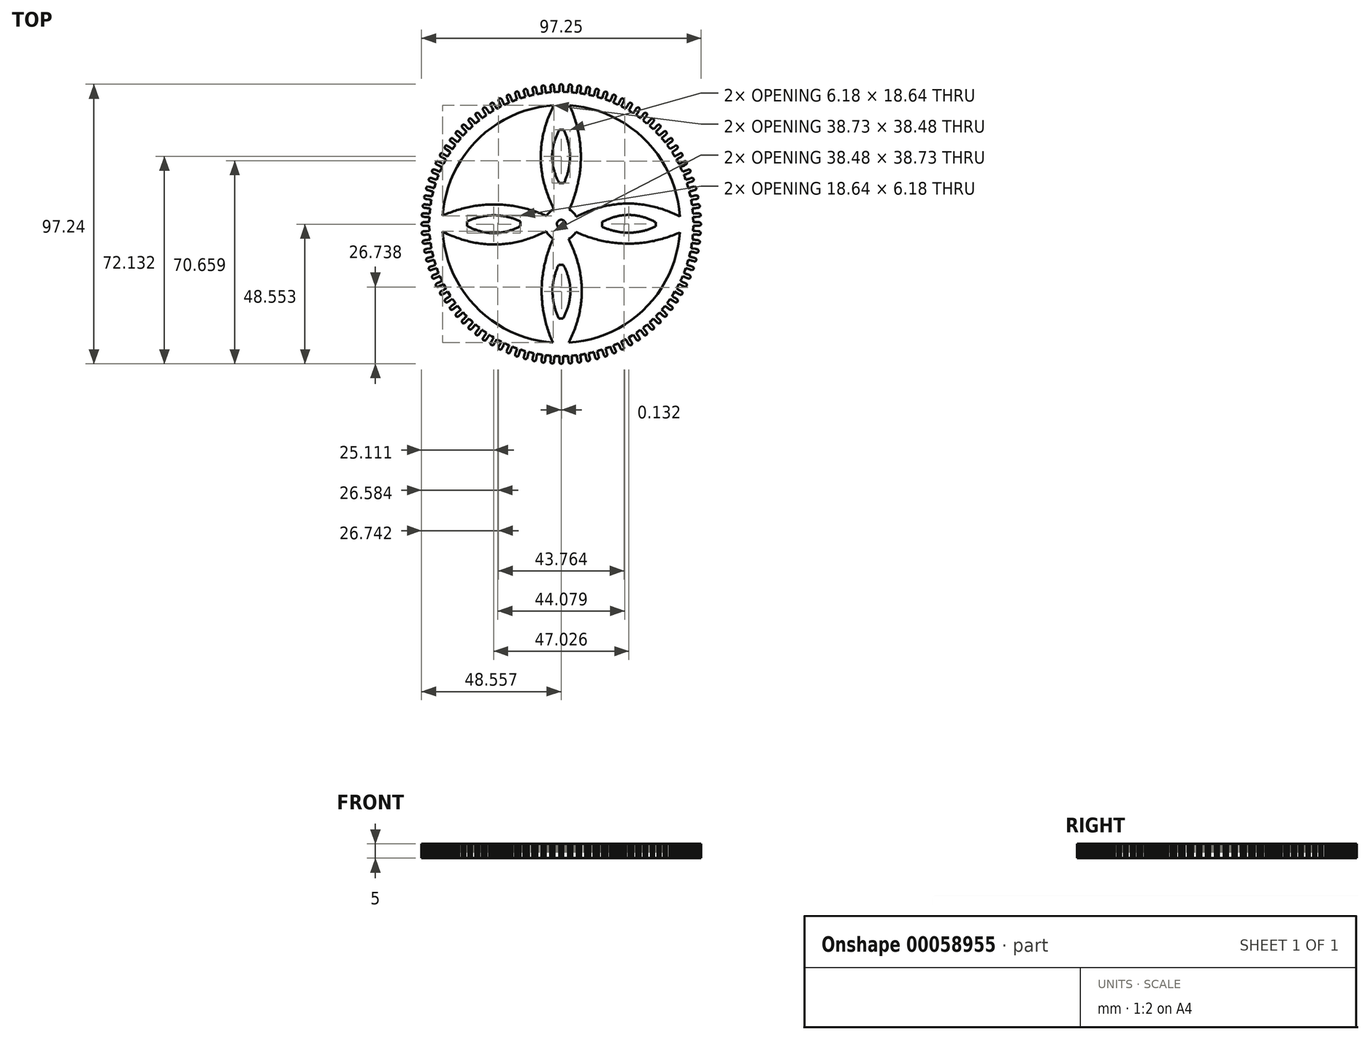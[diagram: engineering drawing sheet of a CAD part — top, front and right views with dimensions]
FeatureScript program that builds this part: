
annotation { "Feature Type Name" : "Feature", "Feature Type Description" : "" }
export const myFeature = defineFeature(function(context is Context, id is Id, definition is map)
    precondition{}
    {
        {
            var Q0;
            Q0=qCreatedBy(makeId("Top.planeOp"),FACE);
            var sketch = newSketch(context, id + "F0", { "sketchPlane" : qUnion([Q0])});
            skLineSegment(sketch, "E0", {"start": v(45.2, -0.6) * mm, "end": v(45.35, -0.6) * mm});
            skLineSegment(sketch, "E1", {"start": v(45.35, -0.6) * mm, "end": v(45.5, -0.6) * mm});
            skLineSegment(sketch, "E2", {"start": v(45.5, -0.6) * mm, "end": v(45.66, -0.6) * mm});
            skLineSegment(sketch, "E3", {"start": v(45.66, -0.6) * mm, "end": v(45.82, -0.6) * mm});
            skLineSegment(sketch, "E4", {"start": v(45.82, -0.6) * mm, "end": v(45.98, -0.6) * mm});
            skLineSegment(sketch, "E5", {"start": v(45.98, -0.6) * mm, "end": v(46.14, -0.61) * mm});
            skLineSegment(sketch, "E6", {"start": v(46.14, -0.61) * mm, "end": v(46.3, -0.61) * mm});
            skLineSegment(sketch, "E7", {"start": v(46.3, -0.61) * mm, "end": v(46.45, -0.62) * mm});
            skLineSegment(sketch, "E8", {"start": v(46.45, -0.62) * mm, "end": v(46.61, -0.62) * mm});
            skLineSegment(sketch, "E9", {"start": v(46.61, -0.62) * mm, "end": v(46.77, -0.62) * mm});
            skLineSegment(sketch, "E10", {"start": v(46.77, -0.62) * mm, "end": v(46.93, -0.62) * mm});
            skLineSegment(sketch, "E11", {"start": v(46.93, -0.62) * mm, "end": v(47.09, -0.62) * mm});
            skLineSegment(sketch, "E12", {"start": v(47.09, -0.62) * mm, "end": v(47.25, -0.63) * mm});
            skLineSegment(sketch, "E13", {"start": v(47.25, -0.63) * mm, "end": v(47.41, -0.6) * mm});
            skLineSegment(sketch, "E14", {"start": v(47.41, -0.6) * mm, "end": v(47.56, -0.54) * mm});
            skLineSegment(sketch, "E15", {"start": v(47.56, -0.54) * mm, "end": v(47.7, -0.44) * mm});
            skLineSegment(sketch, "E16", {"start": v(47.7, -0.44) * mm, "end": v(47.8, -0.31) * mm});
            skLineSegment(sketch, "E17", {"start": v(47.8, -0.31) * mm, "end": v(47.86, -0.16) * mm});
            skLineSegment(sketch, "E18", {"start": v(47.86, -0.16) * mm, "end": v(47.88, 0) * mm});
            skLineSegment(sketch, "E19", {"start": v(47.88, 0) * mm, "end": v(47.86, 0.16) * mm});
            skLineSegment(sketch, "E20", {"start": v(47.86, 0.16) * mm, "end": v(47.8, 0.31) * mm});
            skLineSegment(sketch, "E21", {"start": v(47.8, 0.31) * mm, "end": v(47.7, 0.44) * mm});
            skLineSegment(sketch, "E22", {"start": v(47.7, 0.44) * mm, "end": v(47.56, 0.54) * mm});
            skLineSegment(sketch, "E23", {"start": v(47.56, 0.54) * mm, "end": v(47.41, 0.6) * mm});
            skLineSegment(sketch, "E24", {"start": v(47.41, 0.6) * mm, "end": v(47.25, 0.62) * mm});
            skLineSegment(sketch, "E25", {"start": v(47.25, 0.62) * mm, "end": v(47.1, 0.62) * mm});
            skLineSegment(sketch, "E26", {"start": v(47.1, 0.62) * mm, "end": v(46.94, 0.62) * mm});
            skLineSegment(sketch, "E27", {"start": v(46.94, 0.62) * mm, "end": v(46.77, 0.62) * mm});
            skLineSegment(sketch, "E28", {"start": v(46.77, 0.62) * mm, "end": v(46.62, 0.62) * mm});
            skLineSegment(sketch, "E29", {"start": v(46.62, 0.62) * mm, "end": v(46.46, 0.61) * mm});
            skLineSegment(sketch, "E30", {"start": v(46.46, 0.61) * mm, "end": v(46.3, 0.61) * mm});
            skLineSegment(sketch, "E31", {"start": v(46.3, 0.61) * mm, "end": v(46.14, 0.61) * mm});
            skLineSegment(sketch, "E32", {"start": v(46.14, 0.61) * mm, "end": v(45.98, 0.6) * mm});
            skLineSegment(sketch, "E33", {"start": v(45.98, 0.6) * mm, "end": v(45.82, 0.6) * mm});
            skLineSegment(sketch, "E34", {"start": v(45.82, 0.6) * mm, "end": v(45.66, 0.6) * mm});
            skLineSegment(sketch, "E35", {"start": v(45.66, 0.6) * mm, "end": v(45.5, 0.6) * mm});
            skLineSegment(sketch, "E36", {"start": v(45.5, 0.6) * mm, "end": v(45.35, 0.6) * mm});
            skLineSegment(sketch, "E37", {"start": v(45.35, 0.6) * mm, "end": v(45.2, 0.6) * mm});
            skLineSegment(sketch, "E38", {"start": v(45.2, 0.6) * mm, "end": v(45.2, 0.76) * mm});
            skLineSegment(sketch, "E39", {"start": v(45.2, 0.76) * mm, "end": v(45.2, 0.91) * mm});
            skLineSegment(sketch, "E40", {"start": v(45.2, 0.91) * mm, "end": v(45.2, 1.07) * mm});
            skLineSegment(sketch, "E41", {"start": v(45.2, 1.07) * mm, "end": v(45.19, 1.23) * mm});
            skLineSegment(sketch, "E42", {"start": v(45.19, 1.23) * mm, "end": v(45.18, 1.38) * mm});
            skLineSegment(sketch, "E43", {"start": v(45.18, 1.38) * mm, "end": v(45.18, 1.54) * mm});
            skLineSegment(sketch, "E44", {"start": v(45.18, 1.54) * mm, "end": v(45.17, 1.7) * mm});
            skLineSegment(sketch, "E45", {"start": v(45.17, 1.7) * mm, "end": v(45.17, 1.86) * mm});
            skLineSegment(sketch, "E46", {"start": v(45.17, 1.86) * mm, "end": v(45.16, 2.01) * mm});
            skLineSegment(sketch, "E47", {"start": v(45.16, 2.01) * mm, "end": v(45.16, 2.17) * mm});
            skLineSegment(sketch, "E48", {"start": v(45.16, 2.17) * mm, "end": v(45.15, 2.33) * mm});
            skLineSegment(sketch, "E49", {"start": v(45.15, 2.33) * mm, "end": v(45.15, 2.4) * mm});
            skLineSegment(sketch, "E50", {"start": v(45.15, 2.4) * mm, "end": v(45.3, 2.42) * mm});
            skLineSegment(sketch, "E51", {"start": v(45.3, 2.42) * mm, "end": v(45.46, 2.42) * mm});
            skLineSegment(sketch, "E52", {"start": v(45.46, 2.42) * mm, "end": v(45.63, 2.43) * mm});
            skLineSegment(sketch, "E53", {"start": v(45.63, 2.43) * mm, "end": v(45.78, 2.44) * mm});
            skLineSegment(sketch, "E54", {"start": v(45.78, 2.44) * mm, "end": v(45.94, 2.45) * mm});
            skLineSegment(sketch, "E55", {"start": v(45.94, 2.45) * mm, "end": v(46.1, 2.46) * mm});
            skLineSegment(sketch, "E56", {"start": v(46.1, 2.46) * mm, "end": v(46.26, 2.47) * mm});
            skLineSegment(sketch, "E57", {"start": v(46.26, 2.47) * mm, "end": v(46.42, 2.47) * mm});
            skLineSegment(sketch, "E58", {"start": v(46.42, 2.47) * mm, "end": v(46.58, 2.48) * mm});
            skLineSegment(sketch, "E59", {"start": v(46.58, 2.48) * mm, "end": v(46.73, 2.5) * mm});
            skLineSegment(sketch, "E60", {"start": v(46.73, 2.5) * mm, "end": v(46.9, 2.5) * mm});
            skLineSegment(sketch, "E61", {"start": v(46.9, 2.5) * mm, "end": v(47.05, 2.5) * mm});
            skLineSegment(sketch, "E62", {"start": v(47.05, 2.5) * mm, "end": v(47.22, 2.52) * mm});
            skLineSegment(sketch, "E63", {"start": v(47.22, 2.52) * mm, "end": v(47.38, 2.56) * mm});
            skLineSegment(sketch, "E64", {"start": v(47.38, 2.56) * mm, "end": v(47.52, 2.64) * mm});
            skLineSegment(sketch, "E65", {"start": v(47.52, 2.64) * mm, "end": v(47.64, 2.75) * mm});
            skLineSegment(sketch, "E66", {"start": v(47.64, 2.75) * mm, "end": v(47.72, 2.9) * mm});
            skLineSegment(sketch, "E67", {"start": v(47.72, 2.9) * mm, "end": v(47.77, 3.05) * mm});
            skLineSegment(sketch, "E68", {"start": v(47.77, 3.05) * mm, "end": v(47.77, 3.21) * mm});
            skLineSegment(sketch, "E69", {"start": v(47.77, 3.21) * mm, "end": v(47.73, 3.37) * mm});
            skLineSegment(sketch, "E70", {"start": v(47.73, 3.37) * mm, "end": v(47.65, 3.51) * mm});
            skLineSegment(sketch, "E71", {"start": v(47.65, 3.51) * mm, "end": v(47.54, 3.63) * mm});
            skLineSegment(sketch, "E72", {"start": v(47.54, 3.63) * mm, "end": v(47.4, 3.71) * mm});
            skLineSegment(sketch, "E73", {"start": v(47.4, 3.71) * mm, "end": v(47.24, 3.76) * mm});
            skLineSegment(sketch, "E74", {"start": v(47.24, 3.76) * mm, "end": v(47.14, 3.76) * mm});
            skLineSegment(sketch, "E75", {"start": v(47.14, 3.76) * mm, "end": v(46.97, 3.75) * mm});
            skLineSegment(sketch, "E76", {"start": v(46.97, 3.75) * mm, "end": v(46.81, 3.74) * mm});
            skLineSegment(sketch, "E77", {"start": v(46.81, 3.74) * mm, "end": v(46.66, 3.73) * mm});
            skLineSegment(sketch, "E78", {"start": v(46.66, 3.73) * mm, "end": v(46.5, 3.71) * mm});
            skLineSegment(sketch, "E79", {"start": v(46.5, 3.71) * mm, "end": v(46.34, 3.7) * mm});
            skLineSegment(sketch, "E80", {"start": v(46.34, 3.7) * mm, "end": v(46.18, 3.69) * mm});
            skLineSegment(sketch, "E81", {"start": v(46.18, 3.69) * mm, "end": v(46.02, 3.68) * mm});
            skLineSegment(sketch, "E82", {"start": v(46.02, 3.68) * mm, "end": v(45.86, 3.66) * mm});
            skLineSegment(sketch, "E83", {"start": v(45.86, 3.66) * mm, "end": v(45.7, 3.65) * mm});
            skLineSegment(sketch, "E84", {"start": v(45.7, 3.65) * mm, "end": v(45.55, 3.64) * mm});
            skLineSegment(sketch, "E85", {"start": v(45.55, 3.64) * mm, "end": v(45.39, 3.63) * mm});
            skLineSegment(sketch, "E86", {"start": v(45.39, 3.63) * mm, "end": v(45.23, 3.62) * mm});
            skLineSegment(sketch, "E87", {"start": v(45.23, 3.62) * mm, "end": v(45.07, 3.6) * mm});
            skLineSegment(sketch, "E88", {"start": v(45.07, 3.6) * mm, "end": v(45.06, 3.76) * mm});
            skLineSegment(sketch, "E89", {"start": v(45.06, 3.76) * mm, "end": v(45.04, 3.92) * mm});
            skLineSegment(sketch, "E90", {"start": v(45.04, 3.92) * mm, "end": v(45.03, 4.07) * mm});
            skLineSegment(sketch, "E91", {"start": v(45.03, 4.07) * mm, "end": v(45, 4.23) * mm});
            skLineSegment(sketch, "E92", {"start": v(45, 4.23) * mm, "end": v(45, 4.39) * mm});
            skLineSegment(sketch, "E93", {"start": v(45, 4.39) * mm, "end": v(44.98, 4.54) * mm});
            skLineSegment(sketch, "E94", {"start": v(44.98, 4.54) * mm, "end": v(44.96, 4.7) * mm});
            skLineSegment(sketch, "E95", {"start": v(44.96, 4.7) * mm, "end": v(44.95, 4.85) * mm});
            skLineSegment(sketch, "E96", {"start": v(44.95, 4.85) * mm, "end": v(44.93, 5.01) * mm});
            skLineSegment(sketch, "E97", {"start": v(44.93, 5.01) * mm, "end": v(44.92, 5.17) * mm});
            skLineSegment(sketch, "E98", {"start": v(44.92, 5.17) * mm, "end": v(44.9, 5.32) * mm});
            skLineSegment(sketch, "E99", {"start": v(44.9, 5.32) * mm, "end": v(44.9, 5.4) * mm});
            skLineSegment(sketch, "E100", {"start": v(44.9, 5.4) * mm, "end": v(45.05, 5.42) * mm});
            skLineSegment(sketch, "E101", {"start": v(45.05, 5.42) * mm, "end": v(45.2, 5.44) * mm});
            skLineSegment(sketch, "E102", {"start": v(45.2, 5.44) * mm, "end": v(45.37, 5.46) * mm});
            skLineSegment(sketch, "E103", {"start": v(45.37, 5.46) * mm, "end": v(45.52, 5.48) * mm});
            skLineSegment(sketch, "E104", {"start": v(45.52, 5.48) * mm, "end": v(45.68, 5.5) * mm});
            skLineSegment(sketch, "E105", {"start": v(45.68, 5.5) * mm, "end": v(45.84, 5.52) * mm});
            skLineSegment(sketch, "E106", {"start": v(45.84, 5.52) * mm, "end": v(46, 5.53) * mm});
            skLineSegment(sketch, "E107", {"start": v(46, 5.53) * mm, "end": v(46.15, 5.55) * mm});
            skLineSegment(sketch, "E108", {"start": v(46.15, 5.55) * mm, "end": v(46.31, 5.57) * mm});
            skLineSegment(sketch, "E109", {"start": v(46.31, 5.57) * mm, "end": v(46.47, 5.6) * mm});
            skLineSegment(sketch, "E110", {"start": v(46.47, 5.6) * mm, "end": v(46.63, 5.6) * mm});
            skLineSegment(sketch, "E111", {"start": v(46.63, 5.6) * mm, "end": v(46.79, 5.63) * mm});
            skLineSegment(sketch, "E112", {"start": v(46.79, 5.63) * mm, "end": v(46.95, 5.65) * mm});
            skLineSegment(sketch, "E113", {"start": v(46.95, 5.65) * mm, "end": v(47.1, 5.7) * mm});
            skLineSegment(sketch, "E114", {"start": v(47.1, 5.7) * mm, "end": v(47.25, 5.79) * mm});
            skLineSegment(sketch, "E115", {"start": v(47.25, 5.79) * mm, "end": v(47.36, 5.9) * mm});
            skLineSegment(sketch, "E116", {"start": v(47.36, 5.9) * mm, "end": v(47.43, 6.05) * mm});
            skLineSegment(sketch, "E117", {"start": v(47.43, 6.05) * mm, "end": v(47.47, 6.22) * mm});
            skLineSegment(sketch, "E118", {"start": v(47.47, 6.22) * mm, "end": v(47.46, 6.38) * mm});
            skLineSegment(sketch, "E119", {"start": v(47.46, 6.38) * mm, "end": v(47.4, 6.53) * mm});
            skLineSegment(sketch, "E120", {"start": v(47.4, 6.53) * mm, "end": v(47.32, 6.67) * mm});
            skLineSegment(sketch, "E121", {"start": v(47.32, 6.67) * mm, "end": v(47.2, 6.78) * mm});
            skLineSegment(sketch, "E122", {"start": v(47.2, 6.78) * mm, "end": v(47.05, 6.86) * mm});
            skLineSegment(sketch, "E123", {"start": v(47.05, 6.86) * mm, "end": v(46.89, 6.89) * mm});
            skLineSegment(sketch, "E124", {"start": v(46.89, 6.89) * mm, "end": v(46.86, 6.9) * mm});
            skLineSegment(sketch, "E125", {"start": v(46.86, 6.9) * mm, "end": v(46.7, 6.87) * mm});
            skLineSegment(sketch, "E126", {"start": v(46.7, 6.87) * mm, "end": v(46.53, 6.85) * mm});
            skLineSegment(sketch, "E127", {"start": v(46.53, 6.85) * mm, "end": v(46.38, 6.83) * mm});
            skLineSegment(sketch, "E128", {"start": v(46.38, 6.83) * mm, "end": v(46.22, 6.8) * mm});
            skLineSegment(sketch, "E129", {"start": v(46.22, 6.8) * mm, "end": v(46.06, 6.78) * mm});
            skLineSegment(sketch, "E130", {"start": v(46.06, 6.78) * mm, "end": v(45.9, 6.76) * mm});
            skLineSegment(sketch, "E131", {"start": v(45.9, 6.76) * mm, "end": v(45.75, 6.74) * mm});
            skLineSegment(sketch, "E132", {"start": v(45.75, 6.74) * mm, "end": v(45.6, 6.72) * mm});
            skLineSegment(sketch, "E133", {"start": v(45.6, 6.72) * mm, "end": v(45.44, 6.7) * mm});
            skLineSegment(sketch, "E134", {"start": v(45.44, 6.7) * mm, "end": v(45.28, 6.67) * mm});
            skLineSegment(sketch, "E135", {"start": v(45.28, 6.67) * mm, "end": v(45.12, 6.65) * mm});
            skLineSegment(sketch, "E136", {"start": v(45.12, 6.65) * mm, "end": v(44.97, 6.62) * mm});
            skLineSegment(sketch, "E137", {"start": v(44.97, 6.62) * mm, "end": v(44.8, 6.6) * mm});
            skLineSegment(sketch, "E138", {"start": v(44.8, 6.6) * mm, "end": v(44.74, 6.6) * mm});
            skLineSegment(sketch, "E139", {"start": v(44.74, 6.6) * mm, "end": v(44.71, 6.75) * mm});
            skLineSegment(sketch, "E140", {"start": v(44.71, 6.75) * mm, "end": v(44.69, 6.9) * mm});
            skLineSegment(sketch, "E141", {"start": v(44.69, 6.9) * mm, "end": v(44.66, 7.06) * mm});
            skLineSegment(sketch, "E142", {"start": v(44.66, 7.06) * mm, "end": v(44.64, 7.21) * mm});
            skLineSegment(sketch, "E143", {"start": v(44.64, 7.21) * mm, "end": v(44.6, 7.37) * mm});
            skLineSegment(sketch, "E144", {"start": v(44.6, 7.37) * mm, "end": v(44.58, 7.52) * mm});
            skLineSegment(sketch, "E145", {"start": v(44.58, 7.52) * mm, "end": v(44.56, 7.68) * mm});
            skLineSegment(sketch, "E146", {"start": v(44.56, 7.68) * mm, "end": v(44.53, 7.83) * mm});
            skLineSegment(sketch, "E147", {"start": v(44.53, 7.83) * mm, "end": v(44.5, 7.99) * mm});
            skLineSegment(sketch, "E148", {"start": v(44.5, 7.99) * mm, "end": v(44.48, 8.14) * mm});
            skLineSegment(sketch, "E149", {"start": v(44.48, 8.14) * mm, "end": v(44.46, 8.3) * mm});
            skLineSegment(sketch, "E150", {"start": v(44.46, 8.3) * mm, "end": v(44.44, 8.38) * mm});
            skLineSegment(sketch, "E151", {"start": v(44.44, 8.38) * mm, "end": v(44.6, 8.4) * mm});
            skLineSegment(sketch, "E152", {"start": v(44.6, 8.4) * mm, "end": v(44.75, 8.44) * mm});
            skLineSegment(sketch, "E153", {"start": v(44.75, 8.44) * mm, "end": v(44.91, 8.46) * mm});
            skLineSegment(sketch, "E154", {"start": v(44.91, 8.46) * mm, "end": v(45.07, 8.5) * mm});
            skLineSegment(sketch, "E155", {"start": v(45.07, 8.5) * mm, "end": v(45.22, 8.52) * mm});
            skLineSegment(sketch, "E156", {"start": v(45.22, 8.52) * mm, "end": v(45.38, 8.55) * mm});
            skLineSegment(sketch, "E157", {"start": v(45.38, 8.55) * mm, "end": v(45.53, 8.58) * mm});
            skLineSegment(sketch, "E158", {"start": v(45.53, 8.58) * mm, "end": v(45.69, 8.6) * mm});
            skLineSegment(sketch, "E159", {"start": v(45.69, 8.6) * mm, "end": v(45.85, 8.64) * mm});
            skLineSegment(sketch, "E160", {"start": v(45.85, 8.64) * mm, "end": v(46, 8.67) * mm});
            skLineSegment(sketch, "E161", {"start": v(46, 8.67) * mm, "end": v(46.16, 8.7) * mm});
            skLineSegment(sketch, "E162", {"start": v(46.16, 8.7) * mm, "end": v(46.32, 8.73) * mm});
            skLineSegment(sketch, "E163", {"start": v(46.32, 8.73) * mm, "end": v(46.48, 8.76) * mm});
            skLineSegment(sketch, "E164", {"start": v(46.48, 8.76) * mm, "end": v(46.63, 8.82) * mm});
            skLineSegment(sketch, "E165", {"start": v(46.63, 8.82) * mm, "end": v(46.77, 8.91) * mm});
            skLineSegment(sketch, "E166", {"start": v(46.77, 8.91) * mm, "end": v(46.87, 9.04) * mm});
            skLineSegment(sketch, "E167", {"start": v(46.87, 9.04) * mm, "end": v(46.93, 9.2) * mm});
            skLineSegment(sketch, "E168", {"start": v(46.93, 9.2) * mm, "end": v(46.96, 9.36) * mm});
            skLineSegment(sketch, "E169", {"start": v(46.96, 9.36) * mm, "end": v(46.94, 9.52) * mm});
            skLineSegment(sketch, "E170", {"start": v(46.94, 9.52) * mm, "end": v(46.88, 9.67) * mm});
            skLineSegment(sketch, "E171", {"start": v(46.88, 9.67) * mm, "end": v(46.78, 9.8) * mm});
            skLineSegment(sketch, "E172", {"start": v(46.78, 9.8) * mm, "end": v(46.65, 9.9) * mm});
            skLineSegment(sketch, "E173", {"start": v(46.65, 9.9) * mm, "end": v(46.5, 9.97) * mm});
            skLineSegment(sketch, "E174", {"start": v(46.5, 9.97) * mm, "end": v(46.34, 9.99) * mm});
            skLineSegment(sketch, "E175", {"start": v(46.34, 9.99) * mm, "end": v(46.18, 9.97) * mm});
            skLineSegment(sketch, "E176", {"start": v(46.18, 9.97) * mm, "end": v(46.03, 9.94) * mm});
            skLineSegment(sketch, "E177", {"start": v(46.03, 9.94) * mm, "end": v(45.87, 9.9) * mm});
            skLineSegment(sketch, "E178", {"start": v(45.87, 9.9) * mm, "end": v(45.72, 9.87) * mm});
            skLineSegment(sketch, "E179", {"start": v(45.72, 9.87) * mm, "end": v(45.57, 9.84) * mm});
            skLineSegment(sketch, "E180", {"start": v(45.57, 9.84) * mm, "end": v(45.4, 9.8) * mm});
            skLineSegment(sketch, "E181", {"start": v(45.4, 9.8) * mm, "end": v(45.25, 9.77) * mm});
            skLineSegment(sketch, "E182", {"start": v(45.25, 9.77) * mm, "end": v(45.1, 9.74) * mm});
            skLineSegment(sketch, "E183", {"start": v(45.1, 9.74) * mm, "end": v(44.94, 9.7) * mm});
            skLineSegment(sketch, "E184", {"start": v(44.94, 9.7) * mm, "end": v(44.79, 9.68) * mm});
            skLineSegment(sketch, "E185", {"start": v(44.79, 9.68) * mm, "end": v(44.63, 9.64) * mm});
            skLineSegment(sketch, "E186", {"start": v(44.63, 9.64) * mm, "end": v(44.48, 9.6) * mm});
            skLineSegment(sketch, "E187", {"start": v(44.48, 9.6) * mm, "end": v(44.32, 9.58) * mm});
            skLineSegment(sketch, "E188", {"start": v(44.32, 9.58) * mm, "end": v(44.2, 9.55) * mm});
            skLineSegment(sketch, "E189", {"start": v(44.2, 9.55) * mm, "end": v(44.17, 9.7) * mm});
            skLineSegment(sketch, "E190", {"start": v(44.17, 9.7) * mm, "end": v(44.14, 9.86) * mm});
            skLineSegment(sketch, "E191", {"start": v(44.14, 9.86) * mm, "end": v(44.1, 10.01) * mm});
            skLineSegment(sketch, "E192", {"start": v(44.1, 10.01) * mm, "end": v(44.07, 10.16) * mm});
            skLineSegment(sketch, "E193", {"start": v(44.07, 10.16) * mm, "end": v(44.03, 10.32) * mm});
            skLineSegment(sketch, "E194", {"start": v(44.03, 10.32) * mm, "end": v(44, 10.47) * mm});
            skLineSegment(sketch, "E195", {"start": v(44, 10.47) * mm, "end": v(43.96, 10.62) * mm});
            skLineSegment(sketch, "E196", {"start": v(43.96, 10.62) * mm, "end": v(43.92, 10.78) * mm});
            skLineSegment(sketch, "E197", {"start": v(43.92, 10.78) * mm, "end": v(43.89, 10.93) * mm});
            skLineSegment(sketch, "E198", {"start": v(43.89, 10.93) * mm, "end": v(43.85, 11.08) * mm});
            skLineSegment(sketch, "E199", {"start": v(43.85, 11.08) * mm, "end": v(43.82, 11.24) * mm});
            skLineSegment(sketch, "E200", {"start": v(43.82, 11.24) * mm, "end": v(43.8, 11.32) * mm});
            skLineSegment(sketch, "E201", {"start": v(43.8, 11.32) * mm, "end": v(43.95, 11.35) * mm});
            skLineSegment(sketch, "E202", {"start": v(43.95, 11.35) * mm, "end": v(44.1, 11.4) * mm});
            skLineSegment(sketch, "E203", {"start": v(44.1, 11.4) * mm, "end": v(44.26, 11.43) * mm});
            skLineSegment(sketch, "E204", {"start": v(44.26, 11.43) * mm, "end": v(44.41, 11.47) * mm});
            skLineSegment(sketch, "E205", {"start": v(44.41, 11.47) * mm, "end": v(44.56, 11.51) * mm});
            skLineSegment(sketch, "E206", {"start": v(44.56, 11.51) * mm, "end": v(44.72, 11.55) * mm});
            skLineSegment(sketch, "E207", {"start": v(44.72, 11.55) * mm, "end": v(44.87, 11.59) * mm});
            skLineSegment(sketch, "E208", {"start": v(44.87, 11.59) * mm, "end": v(45.03, 11.63) * mm});
            skLineSegment(sketch, "E209", {"start": v(45.03, 11.63) * mm, "end": v(45.18, 11.67) * mm});
            skLineSegment(sketch, "E210", {"start": v(45.18, 11.67) * mm, "end": v(45.34, 11.7) * mm});
            skLineSegment(sketch, "E211", {"start": v(45.34, 11.7) * mm, "end": v(45.49, 11.74) * mm});
            skLineSegment(sketch, "E212", {"start": v(45.49, 11.74) * mm, "end": v(45.64, 11.78) * mm});
            skLineSegment(sketch, "E213", {"start": v(45.64, 11.78) * mm, "end": v(45.8, 11.83) * mm});
            skLineSegment(sketch, "E214", {"start": v(45.8, 11.83) * mm, "end": v(45.96, 11.9) * mm});
            skLineSegment(sketch, "E215", {"start": v(45.96, 11.9) * mm, "end": v(46.08, 12) * mm});
            skLineSegment(sketch, "E216", {"start": v(46.08, 12) * mm, "end": v(46.17, 12.14) * mm});
            skLineSegment(sketch, "E217", {"start": v(46.17, 12.14) * mm, "end": v(46.23, 12.3) * mm});
            skLineSegment(sketch, "E218", {"start": v(46.23, 12.3) * mm, "end": v(46.24, 12.46) * mm});
            skLineSegment(sketch, "E219", {"start": v(46.24, 12.46) * mm, "end": v(46.21, 12.62) * mm});
            skLineSegment(sketch, "E220", {"start": v(46.21, 12.62) * mm, "end": v(46.14, 12.76) * mm});
            skLineSegment(sketch, "E221", {"start": v(46.14, 12.76) * mm, "end": v(46.04, 12.89) * mm});
            skLineSegment(sketch, "E222", {"start": v(46.04, 12.89) * mm, "end": v(45.9, 12.98) * mm});
            skLineSegment(sketch, "E223", {"start": v(45.9, 12.98) * mm, "end": v(45.75, 13.04) * mm});
            skLineSegment(sketch, "E224", {"start": v(45.75, 13.04) * mm, "end": v(45.61, 13.05) * mm});
            skLineSegment(sketch, "E225", {"start": v(45.61, 13.05) * mm, "end": v(45.45, 13.03) * mm});
            skLineSegment(sketch, "E226", {"start": v(45.45, 13.03) * mm, "end": v(45.3, 12.98) * mm});
            skLineSegment(sketch, "E227", {"start": v(45.3, 12.98) * mm, "end": v(45.15, 12.94) * mm});
            skLineSegment(sketch, "E228", {"start": v(45.15, 12.94) * mm, "end": v(45, 12.9) * mm});
            skLineSegment(sketch, "E229", {"start": v(45, 12.9) * mm, "end": v(44.84, 12.85) * mm});
            skLineSegment(sketch, "E230", {"start": v(44.84, 12.85) * mm, "end": v(44.7, 12.81) * mm});
            skLineSegment(sketch, "E231", {"start": v(44.7, 12.81) * mm, "end": v(44.54, 12.77) * mm});
            skLineSegment(sketch, "E232", {"start": v(44.54, 12.77) * mm, "end": v(44.38, 12.72) * mm});
            skLineSegment(sketch, "E233", {"start": v(44.38, 12.72) * mm, "end": v(44.23, 12.68) * mm});
            skLineSegment(sketch, "E234", {"start": v(44.23, 12.68) * mm, "end": v(44.08, 12.64) * mm});
            skLineSegment(sketch, "E235", {"start": v(44.08, 12.64) * mm, "end": v(43.93, 12.6) * mm});
            skLineSegment(sketch, "E236", {"start": v(43.93, 12.6) * mm, "end": v(43.77, 12.55) * mm});
            skLineSegment(sketch, "E237", {"start": v(43.77, 12.55) * mm, "end": v(43.62, 12.5) * mm});
            skLineSegment(sketch, "E238", {"start": v(43.62, 12.5) * mm, "end": v(43.49, 12.47) * mm});
            skLineSegment(sketch, "E239", {"start": v(43.49, 12.47) * mm, "end": v(43.44, 12.62) * mm});
            skLineSegment(sketch, "E240", {"start": v(43.44, 12.62) * mm, "end": v(43.4, 12.77) * mm});
            skLineSegment(sketch, "E241", {"start": v(43.4, 12.77) * mm, "end": v(43.35, 12.92) * mm});
            skLineSegment(sketch, "E242", {"start": v(43.35, 12.92) * mm, "end": v(43.3, 13.07) * mm});
            skLineSegment(sketch, "E243", {"start": v(43.3, 13.07) * mm, "end": v(43.26, 13.22) * mm});
            skLineSegment(sketch, "E244", {"start": v(43.26, 13.22) * mm, "end": v(43.21, 13.38) * mm});
            skLineSegment(sketch, "E245", {"start": v(43.21, 13.38) * mm, "end": v(43.17, 13.53) * mm});
            skLineSegment(sketch, "E246", {"start": v(43.17, 13.53) * mm, "end": v(43.12, 13.68) * mm});
            skLineSegment(sketch, "E247", {"start": v(43.12, 13.68) * mm, "end": v(43.08, 13.83) * mm});
            skLineSegment(sketch, "E248", {"start": v(43.08, 13.83) * mm, "end": v(43.03, 13.98) * mm});
            skLineSegment(sketch, "E249", {"start": v(43.03, 13.98) * mm, "end": v(42.99, 14.13) * mm});
            skLineSegment(sketch, "E250", {"start": v(42.99, 14.13) * mm, "end": v(42.96, 14.2) * mm});
            skLineSegment(sketch, "E251", {"start": v(42.96, 14.2) * mm, "end": v(43.11, 14.25) * mm});
            skLineSegment(sketch, "E252", {"start": v(43.11, 14.25) * mm, "end": v(43.26, 14.3) * mm});
            skLineSegment(sketch, "E253", {"start": v(43.26, 14.3) * mm, "end": v(43.42, 14.35) * mm});
            skLineSegment(sketch, "E254", {"start": v(43.42, 14.35) * mm, "end": v(43.57, 14.4) * mm});
            skLineSegment(sketch, "E255", {"start": v(43.57, 14.4) * mm, "end": v(43.71, 14.45) * mm});
            skLineSegment(sketch, "E256", {"start": v(43.71, 14.45) * mm, "end": v(43.87, 14.5) * mm});
            skLineSegment(sketch, "E257", {"start": v(43.87, 14.5) * mm, "end": v(44.02, 14.55) * mm});
            skLineSegment(sketch, "E258", {"start": v(44.02, 14.55) * mm, "end": v(44.17, 14.6) * mm});
            skLineSegment(sketch, "E259", {"start": v(44.17, 14.6) * mm, "end": v(44.32, 14.65) * mm});
            skLineSegment(sketch, "E260", {"start": v(44.32, 14.65) * mm, "end": v(44.47, 14.7) * mm});
            skLineSegment(sketch, "E261", {"start": v(44.47, 14.7) * mm, "end": v(44.62, 14.74) * mm});
            skLineSegment(sketch, "E262", {"start": v(44.62, 14.74) * mm, "end": v(44.77, 14.8) * mm});
            skLineSegment(sketch, "E263", {"start": v(44.77, 14.8) * mm, "end": v(44.93, 14.85) * mm});
            skLineSegment(sketch, "E264", {"start": v(44.93, 14.85) * mm, "end": v(45.08, 14.93) * mm});
            skLineSegment(sketch, "E265", {"start": v(45.08, 14.93) * mm, "end": v(45.2, 15.04) * mm});
            skLineSegment(sketch, "E266", {"start": v(45.2, 15.04) * mm, "end": v(45.28, 15.18) * mm});
            skLineSegment(sketch, "E267", {"start": v(45.28, 15.18) * mm, "end": v(45.32, 15.34) * mm});
            skLineSegment(sketch, "E268", {"start": v(45.32, 15.34) * mm, "end": v(45.33, 15.5) * mm});
            skLineSegment(sketch, "E269", {"start": v(45.33, 15.5) * mm, "end": v(45.29, 15.66) * mm});
            skLineSegment(sketch, "E270", {"start": v(45.29, 15.66) * mm, "end": v(45.2, 15.8) * mm});
            skLineSegment(sketch, "E271", {"start": v(45.2, 15.8) * mm, "end": v(45.1, 15.92) * mm});
            skLineSegment(sketch, "E272", {"start": v(45.1, 15.92) * mm, "end": v(44.95, 16) * mm});
            skLineSegment(sketch, "E273", {"start": v(44.95, 16) * mm, "end": v(44.8, 16.05) * mm});
            skLineSegment(sketch, "E274", {"start": v(44.8, 16.05) * mm, "end": v(44.7, 16.05) * mm});
            skLineSegment(sketch, "E275", {"start": v(44.7, 16.05) * mm, "end": v(44.53, 16.03) * mm});
            skLineSegment(sketch, "E276", {"start": v(44.53, 16.03) * mm, "end": v(44.37, 15.97) * mm});
            skLineSegment(sketch, "E277", {"start": v(44.37, 15.97) * mm, "end": v(44.23, 15.92) * mm});
            skLineSegment(sketch, "E278", {"start": v(44.23, 15.92) * mm, "end": v(44.08, 15.87) * mm});
            skLineSegment(sketch, "E279", {"start": v(44.08, 15.87) * mm, "end": v(43.92, 15.82) * mm});
            skLineSegment(sketch, "E280", {"start": v(43.92, 15.82) * mm, "end": v(43.78, 15.76) * mm});
            skLineSegment(sketch, "E281", {"start": v(43.78, 15.76) * mm, "end": v(43.63, 15.71) * mm});
            skLineSegment(sketch, "E282", {"start": v(43.63, 15.71) * mm, "end": v(43.48, 15.66) * mm});
            skLineSegment(sketch, "E283", {"start": v(43.48, 15.66) * mm, "end": v(43.33, 15.6) * mm});
            skLineSegment(sketch, "E284", {"start": v(43.33, 15.6) * mm, "end": v(43.18, 15.55) * mm});
            skLineSegment(sketch, "E285", {"start": v(43.18, 15.55) * mm, "end": v(43.03, 15.5) * mm});
            skLineSegment(sketch, "E286", {"start": v(43.03, 15.5) * mm, "end": v(42.88, 15.44) * mm});
            skLineSegment(sketch, "E287", {"start": v(42.88, 15.44) * mm, "end": v(42.73, 15.4) * mm});
            skLineSegment(sketch, "E288", {"start": v(42.73, 15.4) * mm, "end": v(42.58, 15.34) * mm});
            skLineSegment(sketch, "E289", {"start": v(42.58, 15.34) * mm, "end": v(42.52, 15.49) * mm});
            skLineSegment(sketch, "E290", {"start": v(42.52, 15.49) * mm, "end": v(42.47, 15.63) * mm});
            skLineSegment(sketch, "E291", {"start": v(42.47, 15.63) * mm, "end": v(42.41, 15.78) * mm});
            skLineSegment(sketch, "E292", {"start": v(42.41, 15.78) * mm, "end": v(42.36, 15.93) * mm});
            skLineSegment(sketch, "E293", {"start": v(42.36, 15.93) * mm, "end": v(42.3, 16.07) * mm});
            skLineSegment(sketch, "E294", {"start": v(42.3, 16.07) * mm, "end": v(42.25, 16.22) * mm});
            skLineSegment(sketch, "E295", {"start": v(42.25, 16.22) * mm, "end": v(42.2, 16.37) * mm});
            skLineSegment(sketch, "E296", {"start": v(42.2, 16.37) * mm, "end": v(42.13, 16.52) * mm});
            skLineSegment(sketch, "E297", {"start": v(42.13, 16.52) * mm, "end": v(42.08, 16.66) * mm});
            skLineSegment(sketch, "E298", {"start": v(42.08, 16.66) * mm, "end": v(42.02, 16.81) * mm});
            skLineSegment(sketch, "E299", {"start": v(42.02, 16.81) * mm, "end": v(41.97, 16.96) * mm});
            skLineSegment(sketch, "E300", {"start": v(41.97, 16.96) * mm, "end": v(41.94, 17.03) * mm});
            skLineSegment(sketch, "E301", {"start": v(41.94, 17.03) * mm, "end": v(42.09, 17.1) * mm});
            skLineSegment(sketch, "E302", {"start": v(42.09, 17.1) * mm, "end": v(42.23, 17.15) * mm});
            skLineSegment(sketch, "E303", {"start": v(42.23, 17.15) * mm, "end": v(42.38, 17.2) * mm});
            skLineSegment(sketch, "E304", {"start": v(42.38, 17.2) * mm, "end": v(42.53, 17.27) * mm});
            skLineSegment(sketch, "E305", {"start": v(42.53, 17.27) * mm, "end": v(42.67, 17.33) * mm});
            skLineSegment(sketch, "E306", {"start": v(42.67, 17.33) * mm, "end": v(42.82, 17.39) * mm});
            skLineSegment(sketch, "E307", {"start": v(42.82, 17.39) * mm, "end": v(42.97, 17.44) * mm});
            skLineSegment(sketch, "E308", {"start": v(42.97, 17.44) * mm, "end": v(43.12, 17.5) * mm});
            skLineSegment(sketch, "E309", {"start": v(43.12, 17.5) * mm, "end": v(43.27, 17.56) * mm});
            skLineSegment(sketch, "E310", {"start": v(43.27, 17.56) * mm, "end": v(43.41, 17.62) * mm});
            skLineSegment(sketch, "E311", {"start": v(43.41, 17.62) * mm, "end": v(43.56, 17.68) * mm});
            skLineSegment(sketch, "E312", {"start": v(43.56, 17.68) * mm, "end": v(43.7, 17.74) * mm});
            skLineSegment(sketch, "E313", {"start": v(43.7, 17.74) * mm, "end": v(43.87, 17.8) * mm});
            skLineSegment(sketch, "E314", {"start": v(43.87, 17.8) * mm, "end": v(44, 17.9) * mm});
            skLineSegment(sketch, "E315", {"start": v(44, 17.9) * mm, "end": v(44.11, 18.01) * mm});
            skLineSegment(sketch, "E316", {"start": v(44.11, 18.01) * mm, "end": v(44.19, 18.16) * mm});
            skLineSegment(sketch, "E317", {"start": v(44.19, 18.16) * mm, "end": v(44.22, 18.32) * mm});
            skLineSegment(sketch, "E318", {"start": v(44.22, 18.32) * mm, "end": v(44.21, 18.48) * mm});
            skLineSegment(sketch, "E319", {"start": v(44.21, 18.48) * mm, "end": v(44.16, 18.64) * mm});
            skLineSegment(sketch, "E320", {"start": v(44.16, 18.64) * mm, "end": v(44.07, 18.78) * mm});
            skLineSegment(sketch, "E321", {"start": v(44.07, 18.78) * mm, "end": v(43.95, 18.88) * mm});
            skLineSegment(sketch, "E322", {"start": v(43.95, 18.88) * mm, "end": v(43.8, 18.96) * mm});
            skLineSegment(sketch, "E323", {"start": v(43.8, 18.96) * mm, "end": v(43.65, 19) * mm});
            skLineSegment(sketch, "E324", {"start": v(43.65, 19) * mm, "end": v(43.61, 19) * mm});
            skLineSegment(sketch, "E325", {"start": v(43.61, 19) * mm, "end": v(43.45, 18.98) * mm});
            skLineSegment(sketch, "E326", {"start": v(43.45, 18.98) * mm, "end": v(43.3, 18.92) * mm});
            skLineSegment(sketch, "E327", {"start": v(43.3, 18.92) * mm, "end": v(43.15, 18.86) * mm});
            skLineSegment(sketch, "E328", {"start": v(43.15, 18.86) * mm, "end": v(43, 18.8) * mm});
            skLineSegment(sketch, "E329", {"start": v(43, 18.8) * mm, "end": v(42.86, 18.73) * mm});
            skLineSegment(sketch, "E330", {"start": v(42.86, 18.73) * mm, "end": v(42.71, 18.67) * mm});
            skLineSegment(sketch, "E331", {"start": v(42.71, 18.67) * mm, "end": v(42.57, 18.6) * mm});
            skLineSegment(sketch, "E332", {"start": v(42.57, 18.6) * mm, "end": v(42.42, 18.54) * mm});
            skLineSegment(sketch, "E333", {"start": v(42.42, 18.54) * mm, "end": v(42.27, 18.48) * mm});
            skLineSegment(sketch, "E334", {"start": v(42.27, 18.48) * mm, "end": v(42.13, 18.42) * mm});
            skLineSegment(sketch, "E335", {"start": v(42.13, 18.42) * mm, "end": v(41.98, 18.35) * mm});
            skLineSegment(sketch, "E336", {"start": v(41.98, 18.35) * mm, "end": v(41.84, 18.3) * mm});
            skLineSegment(sketch, "E337", {"start": v(41.84, 18.3) * mm, "end": v(41.7, 18.23) * mm});
            skLineSegment(sketch, "E338", {"start": v(41.7, 18.23) * mm, "end": v(41.54, 18.17) * mm});
            skLineSegment(sketch, "E339", {"start": v(41.54, 18.17) * mm, "end": v(41.48, 18.14) * mm});
            skLineSegment(sketch, "E340", {"start": v(41.48, 18.14) * mm, "end": v(41.42, 18.28) * mm});
            skLineSegment(sketch, "E341", {"start": v(41.42, 18.28) * mm, "end": v(41.35, 18.43) * mm});
            skLineSegment(sketch, "E342", {"start": v(41.35, 18.43) * mm, "end": v(41.29, 18.57) * mm});
            skLineSegment(sketch, "E343", {"start": v(41.29, 18.57) * mm, "end": v(41.22, 18.71) * mm});
            skLineSegment(sketch, "E344", {"start": v(41.22, 18.71) * mm, "end": v(41.16, 18.86) * mm});
            skLineSegment(sketch, "E345", {"start": v(41.16, 18.86) * mm, "end": v(41.1, 19) * mm});
            skLineSegment(sketch, "E346", {"start": v(41.1, 19) * mm, "end": v(41.03, 19.14) * mm});
            skLineSegment(sketch, "E347", {"start": v(41.03, 19.14) * mm, "end": v(40.96, 19.29) * mm});
            skLineSegment(sketch, "E348", {"start": v(40.96, 19.29) * mm, "end": v(40.9, 19.43) * mm});
            skLineSegment(sketch, "E349", {"start": v(40.9, 19.43) * mm, "end": v(40.83, 19.57) * mm});
            skLineSegment(sketch, "E350", {"start": v(40.83, 19.57) * mm, "end": v(40.77, 19.71) * mm});
            skLineSegment(sketch, "E351", {"start": v(40.77, 19.71) * mm, "end": v(40.73, 19.79) * mm});
            skLineSegment(sketch, "E352", {"start": v(40.73, 19.79) * mm, "end": v(40.88, 19.86) * mm});
            skLineSegment(sketch, "E353", {"start": v(40.88, 19.86) * mm, "end": v(41.02, 19.92) * mm});
            skLineSegment(sketch, "E354", {"start": v(41.02, 19.92) * mm, "end": v(41.16, 20) * mm});
            skLineSegment(sketch, "E355", {"start": v(41.16, 20) * mm, "end": v(41.3, 20.06) * mm});
            skLineSegment(sketch, "E356", {"start": v(41.3, 20.06) * mm, "end": v(41.45, 20.13) * mm});
            skLineSegment(sketch, "E357", {"start": v(41.45, 20.13) * mm, "end": v(41.6, 20.2) * mm});
            skLineSegment(sketch, "E358", {"start": v(41.6, 20.2) * mm, "end": v(41.74, 20.27) * mm});
            skLineSegment(sketch, "E359", {"start": v(41.74, 20.27) * mm, "end": v(41.88, 20.33) * mm});
            skLineSegment(sketch, "E360", {"start": v(41.88, 20.33) * mm, "end": v(42.02, 20.4) * mm});
            skLineSegment(sketch, "E361", {"start": v(42.02, 20.4) * mm, "end": v(42.17, 20.47) * mm});
            skLineSegment(sketch, "E362", {"start": v(42.17, 20.47) * mm, "end": v(42.3, 20.54) * mm});
            skLineSegment(sketch, "E363", {"start": v(42.3, 20.54) * mm, "end": v(42.45, 20.6) * mm});
            skLineSegment(sketch, "E364", {"start": v(42.45, 20.6) * mm, "end": v(42.6, 20.68) * mm});
            skLineSegment(sketch, "E365", {"start": v(42.6, 20.68) * mm, "end": v(42.74, 20.78) * mm});
            skLineSegment(sketch, "E366", {"start": v(42.74, 20.78) * mm, "end": v(42.84, 20.9) * mm});
            skLineSegment(sketch, "E367", {"start": v(42.84, 20.9) * mm, "end": v(42.9, 21.06) * mm});
            skLineSegment(sketch, "E368", {"start": v(42.9, 21.06) * mm, "end": v(42.93, 21.22) * mm});
            skLineSegment(sketch, "E369", {"start": v(42.93, 21.22) * mm, "end": v(42.9, 21.38) * mm});
            skLineSegment(sketch, "E370", {"start": v(42.9, 21.38) * mm, "end": v(42.85, 21.53) * mm});
            skLineSegment(sketch, "E371", {"start": v(42.85, 21.53) * mm, "end": v(42.75, 21.67) * mm});
            skLineSegment(sketch, "E372", {"start": v(42.75, 21.67) * mm, "end": v(42.62, 21.77) * mm});
            skLineSegment(sketch, "E373", {"start": v(42.62, 21.77) * mm, "end": v(42.47, 21.83) * mm});
            skLineSegment(sketch, "E374", {"start": v(42.47, 21.83) * mm, "end": v(42.3, 21.85) * mm});
            skLineSegment(sketch, "E375", {"start": v(42.3, 21.85) * mm, "end": v(42.15, 21.83) * mm});
            skLineSegment(sketch, "E376", {"start": v(42.15, 21.83) * mm, "end": v(42, 21.77) * mm});
            skLineSegment(sketch, "E377", {"start": v(42, 21.77) * mm, "end": v(41.86, 21.7) * mm});
            skLineSegment(sketch, "E378", {"start": v(41.86, 21.7) * mm, "end": v(41.72, 21.63) * mm});
            skLineSegment(sketch, "E379", {"start": v(41.72, 21.63) * mm, "end": v(41.58, 21.56) * mm});
            skLineSegment(sketch, "E380", {"start": v(41.58, 21.56) * mm, "end": v(41.44, 21.5) * mm});
            skLineSegment(sketch, "E381", {"start": v(41.44, 21.5) * mm, "end": v(41.3, 21.42) * mm});
            skLineSegment(sketch, "E382", {"start": v(41.3, 21.42) * mm, "end": v(41.16, 21.35) * mm});
            skLineSegment(sketch, "E383", {"start": v(41.16, 21.35) * mm, "end": v(41.02, 21.28) * mm});
            skLineSegment(sketch, "E384", {"start": v(41.02, 21.28) * mm, "end": v(40.87, 21.2) * mm});
            skLineSegment(sketch, "E385", {"start": v(40.87, 21.2) * mm, "end": v(40.73, 21.13) * mm});
            skLineSegment(sketch, "E386", {"start": v(40.73, 21.13) * mm, "end": v(40.6, 21.06) * mm});
            skLineSegment(sketch, "E387", {"start": v(40.6, 21.06) * mm, "end": v(40.45, 20.99) * mm});
            skLineSegment(sketch, "E388", {"start": v(40.45, 20.99) * mm, "end": v(40.3, 20.91) * mm});
            skLineSegment(sketch, "E389", {"start": v(40.3, 20.91) * mm, "end": v(40.2, 20.86) * mm});
            skLineSegment(sketch, "E390", {"start": v(40.2, 20.86) * mm, "end": v(40.13, 21) * mm});
            skLineSegment(sketch, "E391", {"start": v(40.13, 21) * mm, "end": v(40.06, 21.14) * mm});
            skLineSegment(sketch, "E392", {"start": v(40.06, 21.14) * mm, "end": v(39.98, 21.28) * mm});
            skLineSegment(sketch, "E393", {"start": v(39.98, 21.28) * mm, "end": v(39.9, 21.42) * mm});
            skLineSegment(sketch, "E394", {"start": v(39.9, 21.42) * mm, "end": v(39.83, 21.56) * mm});
            skLineSegment(sketch, "E395", {"start": v(39.83, 21.56) * mm, "end": v(39.76, 21.7) * mm});
            skLineSegment(sketch, "E396", {"start": v(39.76, 21.7) * mm, "end": v(39.69, 21.83) * mm});
            skLineSegment(sketch, "E397", {"start": v(39.69, 21.83) * mm, "end": v(39.61, 21.97) * mm});
            skLineSegment(sketch, "E398", {"start": v(39.61, 21.97) * mm, "end": v(39.54, 22.11) * mm});
            skLineSegment(sketch, "E399", {"start": v(39.54, 22.11) * mm, "end": v(39.46, 22.25) * mm});
            skLineSegment(sketch, "E400", {"start": v(39.46, 22.25) * mm, "end": v(39.39, 22.39) * mm});
            skLineSegment(sketch, "E401", {"start": v(39.39, 22.39) * mm, "end": v(39.35, 22.46) * mm});
            skLineSegment(sketch, "E402", {"start": v(39.35, 22.46) * mm, "end": v(39.49, 22.54) * mm});
            skLineSegment(sketch, "E403", {"start": v(39.49, 22.54) * mm, "end": v(39.63, 22.61) * mm});
            skLineSegment(sketch, "E404", {"start": v(39.63, 22.61) * mm, "end": v(39.77, 22.7) * mm});
            skLineSegment(sketch, "E405", {"start": v(39.77, 22.7) * mm, "end": v(39.9, 22.77) * mm});
            skLineSegment(sketch, "E406", {"start": v(39.9, 22.77) * mm, "end": v(40.04, 22.85) * mm});
            skLineSegment(sketch, "E407", {"start": v(40.04, 22.85) * mm, "end": v(40.18, 22.92) * mm});
            skLineSegment(sketch, "E408", {"start": v(40.18, 22.92) * mm, "end": v(40.32, 23) * mm});
            skLineSegment(sketch, "E409", {"start": v(40.32, 23) * mm, "end": v(40.46, 23.08) * mm});
            skLineSegment(sketch, "E410", {"start": v(40.46, 23.08) * mm, "end": v(40.6, 23.16) * mm});
            skLineSegment(sketch, "E411", {"start": v(40.6, 23.16) * mm, "end": v(40.74, 23.23) * mm});
            skLineSegment(sketch, "E412", {"start": v(40.74, 23.23) * mm, "end": v(40.87, 23.31) * mm});
            skLineSegment(sketch, "E413", {"start": v(40.87, 23.31) * mm, "end": v(41.01, 23.39) * mm});
            skLineSegment(sketch, "E414", {"start": v(41.01, 23.39) * mm, "end": v(41.16, 23.47) * mm});
            skLineSegment(sketch, "E415", {"start": v(41.16, 23.47) * mm, "end": v(41.29, 23.58) * mm});
            skLineSegment(sketch, "E416", {"start": v(41.29, 23.58) * mm, "end": v(41.38, 23.71) * mm});
            skLineSegment(sketch, "E417", {"start": v(41.38, 23.71) * mm, "end": v(41.43, 23.87) * mm});
            skLineSegment(sketch, "E418", {"start": v(41.43, 23.87) * mm, "end": v(41.45, 24.03) * mm});
            skLineSegment(sketch, "E419", {"start": v(41.45, 24.03) * mm, "end": v(41.42, 24.2) * mm});
            skLineSegment(sketch, "E420", {"start": v(41.42, 24.2) * mm, "end": v(41.35, 24.34) * mm});
            skLineSegment(sketch, "E421", {"start": v(41.35, 24.34) * mm, "end": v(41.24, 24.46) * mm});
            skLineSegment(sketch, "E422", {"start": v(41.24, 24.46) * mm, "end": v(41.1, 24.56) * mm});
            skLineSegment(sketch, "E423", {"start": v(41.1, 24.56) * mm, "end": v(40.95, 24.61) * mm});
            skLineSegment(sketch, "E424", {"start": v(40.95, 24.61) * mm, "end": v(40.82, 24.62) * mm});
            skLineSegment(sketch, "E425", {"start": v(40.82, 24.62) * mm, "end": v(40.66, 24.6) * mm});
            skLineSegment(sketch, "E426", {"start": v(40.66, 24.6) * mm, "end": v(40.5, 24.54) * mm});
            skLineSegment(sketch, "E427", {"start": v(40.5, 24.54) * mm, "end": v(40.37, 24.46) * mm});
            skLineSegment(sketch, "E428", {"start": v(40.37, 24.46) * mm, "end": v(40.24, 24.38) * mm});
            skLineSegment(sketch, "E429", {"start": v(40.24, 24.38) * mm, "end": v(40.1, 24.3) * mm});
            skLineSegment(sketch, "E430", {"start": v(40.1, 24.3) * mm, "end": v(39.96, 24.22) * mm});
            skLineSegment(sketch, "E431", {"start": v(39.96, 24.22) * mm, "end": v(39.83, 24.13) * mm});
            skLineSegment(sketch, "E432", {"start": v(39.83, 24.13) * mm, "end": v(39.69, 24.05) * mm});
            skLineSegment(sketch, "E433", {"start": v(39.69, 24.05) * mm, "end": v(39.55, 23.97) * mm});
            skLineSegment(sketch, "E434", {"start": v(39.55, 23.97) * mm, "end": v(39.42, 23.9) * mm});
            skLineSegment(sketch, "E435", {"start": v(39.42, 23.9) * mm, "end": v(39.28, 23.8) * mm});
            skLineSegment(sketch, "E436", {"start": v(39.28, 23.8) * mm, "end": v(39.14, 23.73) * mm});
            skLineSegment(sketch, "E437", {"start": v(39.14, 23.73) * mm, "end": v(39, 23.65) * mm});
            skLineSegment(sketch, "E438", {"start": v(39, 23.65) * mm, "end": v(38.87, 23.57) * mm});
            skLineSegment(sketch, "E439", {"start": v(38.87, 23.57) * mm, "end": v(38.75, 23.5) * mm});
            skLineSegment(sketch, "E440", {"start": v(38.75, 23.5) * mm, "end": v(38.67, 23.63) * mm});
            skLineSegment(sketch, "E441", {"start": v(38.67, 23.63) * mm, "end": v(38.59, 23.76) * mm});
            skLineSegment(sketch, "E442", {"start": v(38.59, 23.76) * mm, "end": v(38.5, 23.9) * mm});
            skLineSegment(sketch, "E443", {"start": v(38.5, 23.9) * mm, "end": v(38.42, 24.03) * mm});
            skLineSegment(sketch, "E444", {"start": v(38.42, 24.03) * mm, "end": v(38.34, 24.16) * mm});
            skLineSegment(sketch, "E445", {"start": v(38.34, 24.16) * mm, "end": v(38.25, 24.3) * mm});
            skLineSegment(sketch, "E446", {"start": v(38.25, 24.3) * mm, "end": v(38.17, 24.43) * mm});
            skLineSegment(sketch, "E447", {"start": v(38.17, 24.43) * mm, "end": v(38.09, 24.56) * mm});
            skLineSegment(sketch, "E448", {"start": v(38.09, 24.56) * mm, "end": v(38, 24.7) * mm});
            skLineSegment(sketch, "E449", {"start": v(38, 24.7) * mm, "end": v(37.92, 24.83) * mm});
            skLineSegment(sketch, "E450", {"start": v(37.92, 24.83) * mm, "end": v(37.84, 24.96) * mm});
            skLineSegment(sketch, "E451", {"start": v(37.84, 24.96) * mm, "end": v(37.8, 25.03) * mm});
            skLineSegment(sketch, "E452", {"start": v(37.8, 25.03) * mm, "end": v(37.93, 25.12) * mm});
            skLineSegment(sketch, "E453", {"start": v(37.93, 25.12) * mm, "end": v(38.06, 25.2) * mm});
            skLineSegment(sketch, "E454", {"start": v(38.06, 25.2) * mm, "end": v(38.2, 25.3) * mm});
            skLineSegment(sketch, "E455", {"start": v(38.2, 25.3) * mm, "end": v(38.33, 25.38) * mm});
            skLineSegment(sketch, "E456", {"start": v(38.33, 25.38) * mm, "end": v(38.46, 25.46) * mm});
            skLineSegment(sketch, "E457", {"start": v(38.46, 25.46) * mm, "end": v(38.6, 25.55) * mm});
            skLineSegment(sketch, "E458", {"start": v(38.6, 25.55) * mm, "end": v(38.73, 25.64) * mm});
            skLineSegment(sketch, "E459", {"start": v(38.73, 25.64) * mm, "end": v(38.86, 25.72) * mm});
            skLineSegment(sketch, "E460", {"start": v(38.86, 25.72) * mm, "end": v(39, 25.81) * mm});
            skLineSegment(sketch, "E461", {"start": v(39, 25.81) * mm, "end": v(39.13, 25.9) * mm});
            skLineSegment(sketch, "E462", {"start": v(39.13, 25.9) * mm, "end": v(39.26, 25.98) * mm});
            skLineSegment(sketch, "E463", {"start": v(39.26, 25.98) * mm, "end": v(39.4, 26.07) * mm});
            skLineSegment(sketch, "E464", {"start": v(39.4, 26.07) * mm, "end": v(39.54, 26.16) * mm});
            skLineSegment(sketch, "E465", {"start": v(39.54, 26.16) * mm, "end": v(39.65, 26.28) * mm});
            skLineSegment(sketch, "E466", {"start": v(39.65, 26.28) * mm, "end": v(39.74, 26.42) * mm});
            skLineSegment(sketch, "E467", {"start": v(39.74, 26.42) * mm, "end": v(39.78, 26.58) * mm});
            skLineSegment(sketch, "E468", {"start": v(39.78, 26.58) * mm, "end": v(39.79, 26.74) * mm});
            skLineSegment(sketch, "E469", {"start": v(39.79, 26.74) * mm, "end": v(39.75, 26.9) * mm});
            skLineSegment(sketch, "E470", {"start": v(39.75, 26.9) * mm, "end": v(39.66, 27.04) * mm});
            skLineSegment(sketch, "E471", {"start": v(39.66, 27.04) * mm, "end": v(39.55, 27.16) * mm});
            skLineSegment(sketch, "E472", {"start": v(39.55, 27.16) * mm, "end": v(39.4, 27.24) * mm});
            skLineSegment(sketch, "E473", {"start": v(39.4, 27.24) * mm, "end": v(39.25, 27.29) * mm});
            skLineSegment(sketch, "E474", {"start": v(39.25, 27.29) * mm, "end": v(39.15, 27.3) * mm});
            skLineSegment(sketch, "E475", {"start": v(39.15, 27.3) * mm, "end": v(39, 27.27) * mm});
            skLineSegment(sketch, "E476", {"start": v(39, 27.27) * mm, "end": v(38.84, 27.2) * mm});
            skLineSegment(sketch, "E477", {"start": v(38.84, 27.2) * mm, "end": v(38.7, 27.1) * mm});
            skLineSegment(sketch, "E478", {"start": v(38.7, 27.1) * mm, "end": v(38.57, 27.02) * mm});
            skLineSegment(sketch, "E479", {"start": v(38.57, 27.02) * mm, "end": v(38.44, 26.93) * mm});
            skLineSegment(sketch, "E480", {"start": v(38.44, 26.93) * mm, "end": v(38.3, 26.84) * mm});
            skLineSegment(sketch, "E481", {"start": v(38.3, 26.84) * mm, "end": v(38.18, 26.75) * mm});
            skLineSegment(sketch, "E482", {"start": v(38.18, 26.75) * mm, "end": v(38.05, 26.66) * mm});
            skLineSegment(sketch, "E483", {"start": v(38.05, 26.66) * mm, "end": v(37.92, 26.57) * mm});
            skLineSegment(sketch, "E484", {"start": v(37.92, 26.57) * mm, "end": v(37.79, 26.48) * mm});
            skLineSegment(sketch, "E485", {"start": v(37.79, 26.48) * mm, "end": v(37.66, 26.4) * mm});
            skLineSegment(sketch, "E486", {"start": v(37.66, 26.4) * mm, "end": v(37.52, 26.3) * mm});
            skLineSegment(sketch, "E487", {"start": v(37.52, 26.3) * mm, "end": v(37.4, 26.2) * mm});
            skLineSegment(sketch, "E488", {"start": v(37.4, 26.2) * mm, "end": v(37.26, 26.12) * mm});
            skLineSegment(sketch, "E489", {"start": v(37.26, 26.12) * mm, "end": v(37.13, 26.03) * mm});
            skLineSegment(sketch, "E490", {"start": v(37.13, 26.03) * mm, "end": v(37.04, 26.16) * mm});
            skLineSegment(sketch, "E491", {"start": v(37.04, 26.16) * mm, "end": v(36.95, 26.28) * mm});
            skLineSegment(sketch, "E492", {"start": v(36.95, 26.28) * mm, "end": v(36.86, 26.41) * mm});
            skLineSegment(sketch, "E493", {"start": v(36.86, 26.41) * mm, "end": v(36.77, 26.54) * mm});
            skLineSegment(sketch, "E494", {"start": v(36.77, 26.54) * mm, "end": v(36.67, 26.67) * mm});
            skLineSegment(sketch, "E495", {"start": v(36.67, 26.67) * mm, "end": v(36.58, 26.8) * mm});
            skLineSegment(sketch, "E496", {"start": v(36.58, 26.8) * mm, "end": v(36.5, 26.92) * mm});
            skLineSegment(sketch, "E497", {"start": v(36.5, 26.92) * mm, "end": v(36.4, 27.05) * mm});
            skLineSegment(sketch, "E498", {"start": v(36.4, 27.05) * mm, "end": v(36.3, 27.18) * mm});
            skLineSegment(sketch, "E499", {"start": v(36.3, 27.18) * mm, "end": v(36.22, 27.3) * mm});
            skLineSegment(sketch, "E500", {"start": v(36.22, 27.3) * mm, "end": v(36.12, 27.44) * mm});
            skLineSegment(sketch, "E501", {"start": v(36.12, 27.44) * mm, "end": v(36.08, 27.5) * mm});
            skLineSegment(sketch, "E502", {"start": v(36.08, 27.5) * mm, "end": v(36.2, 27.6) * mm});
            skLineSegment(sketch, "E503", {"start": v(36.2, 27.6) * mm, "end": v(36.33, 27.69) * mm});
            skLineSegment(sketch, "E504", {"start": v(36.33, 27.69) * mm, "end": v(36.46, 27.79) * mm});
            skLineSegment(sketch, "E505", {"start": v(36.46, 27.79) * mm, "end": v(36.58, 27.88) * mm});
            skLineSegment(sketch, "E506", {"start": v(36.58, 27.88) * mm, "end": v(36.71, 27.97) * mm});
            skLineSegment(sketch, "E507", {"start": v(36.71, 27.97) * mm, "end": v(36.84, 28.07) * mm});
            skLineSegment(sketch, "E508", {"start": v(36.84, 28.07) * mm, "end": v(36.97, 28.16) * mm});
            skLineSegment(sketch, "E509", {"start": v(36.97, 28.16) * mm, "end": v(37.1, 28.26) * mm});
            skLineSegment(sketch, "E510", {"start": v(37.1, 28.26) * mm, "end": v(37.22, 28.36) * mm});
            skLineSegment(sketch, "E511", {"start": v(37.22, 28.36) * mm, "end": v(37.35, 28.45) * mm});
            skLineSegment(sketch, "E512", {"start": v(37.35, 28.45) * mm, "end": v(37.47, 28.54) * mm});
            skLineSegment(sketch, "E513", {"start": v(37.47, 28.54) * mm, "end": v(37.6, 28.64) * mm});
            skLineSegment(sketch, "E514", {"start": v(37.6, 28.64) * mm, "end": v(37.74, 28.74) * mm});
            skLineSegment(sketch, "E515", {"start": v(37.74, 28.74) * mm, "end": v(37.85, 28.86) * mm});
            skLineSegment(sketch, "E516", {"start": v(37.85, 28.86) * mm, "end": v(37.92, 29) * mm});
            skLineSegment(sketch, "E517", {"start": v(37.92, 29) * mm, "end": v(37.96, 29.17) * mm});
            skLineSegment(sketch, "E518", {"start": v(37.96, 29.17) * mm, "end": v(37.95, 29.33) * mm});
            skLineSegment(sketch, "E519", {"start": v(37.95, 29.33) * mm, "end": v(37.9, 29.49) * mm});
            skLineSegment(sketch, "E520", {"start": v(37.9, 29.49) * mm, "end": v(37.8, 29.63) * mm});
            skLineSegment(sketch, "E521", {"start": v(37.8, 29.63) * mm, "end": v(37.69, 29.74) * mm});
            skLineSegment(sketch, "E522", {"start": v(37.69, 29.74) * mm, "end": v(37.54, 29.8) * mm});
            skLineSegment(sketch, "E523", {"start": v(37.54, 29.8) * mm, "end": v(37.38, 29.84) * mm});
            skLineSegment(sketch, "E524", {"start": v(37.38, 29.84) * mm, "end": v(37.35, 29.85) * mm});
            skLineSegment(sketch, "E525", {"start": v(37.35, 29.85) * mm, "end": v(37.19, 29.83) * mm});
            skLineSegment(sketch, "E526", {"start": v(37.19, 29.83) * mm, "end": v(37.03, 29.77) * mm});
            skLineSegment(sketch, "E527", {"start": v(37.03, 29.77) * mm, "end": v(36.9, 29.67) * mm});
            skLineSegment(sketch, "E528", {"start": v(36.9, 29.67) * mm, "end": v(36.77, 29.57) * mm});
            skLineSegment(sketch, "E529", {"start": v(36.77, 29.57) * mm, "end": v(36.65, 29.48) * mm});
            skLineSegment(sketch, "E530", {"start": v(36.65, 29.48) * mm, "end": v(36.52, 29.38) * mm});
            skLineSegment(sketch, "E531", {"start": v(36.52, 29.38) * mm, "end": v(36.4, 29.28) * mm});
            skLineSegment(sketch, "E532", {"start": v(36.4, 29.28) * mm, "end": v(36.28, 29.18) * mm});
            skLineSegment(sketch, "E533", {"start": v(36.28, 29.18) * mm, "end": v(36.15, 29.08) * mm});
            skLineSegment(sketch, "E534", {"start": v(36.15, 29.08) * mm, "end": v(36.03, 28.98) * mm});
            skLineSegment(sketch, "E535", {"start": v(36.03, 28.98) * mm, "end": v(35.9, 28.89) * mm});
            skLineSegment(sketch, "E536", {"start": v(35.9, 28.89) * mm, "end": v(35.78, 28.79) * mm});
            skLineSegment(sketch, "E537", {"start": v(35.78, 28.79) * mm, "end": v(35.65, 28.69) * mm});
            skLineSegment(sketch, "E538", {"start": v(35.65, 28.69) * mm, "end": v(35.53, 28.6) * mm});
            skLineSegment(sketch, "E539", {"start": v(35.53, 28.6) * mm, "end": v(35.4, 28.5) * mm});
            skLineSegment(sketch, "E540", {"start": v(35.4, 28.5) * mm, "end": v(35.35, 28.45) * mm});
            skLineSegment(sketch, "E541", {"start": v(35.35, 28.45) * mm, "end": v(35.25, 28.57) * mm});
            skLineSegment(sketch, "E542", {"start": v(35.25, 28.57) * mm, "end": v(35.15, 28.7) * mm});
            skLineSegment(sketch, "E543", {"start": v(35.15, 28.7) * mm, "end": v(35.05, 28.82) * mm});
            skLineSegment(sketch, "E544", {"start": v(35.05, 28.82) * mm, "end": v(34.95, 28.94) * mm});
            skLineSegment(sketch, "E545", {"start": v(34.95, 28.94) * mm, "end": v(34.85, 29.06) * mm});
            skLineSegment(sketch, "E546", {"start": v(34.85, 29.06) * mm, "end": v(34.75, 29.18) * mm});
            skLineSegment(sketch, "E547", {"start": v(34.75, 29.18) * mm, "end": v(34.65, 29.3) * mm});
            skLineSegment(sketch, "E548", {"start": v(34.65, 29.3) * mm, "end": v(34.55, 29.42) * mm});
            skLineSegment(sketch, "E549", {"start": v(34.55, 29.42) * mm, "end": v(34.45, 29.54) * mm});
            skLineSegment(sketch, "E550", {"start": v(34.45, 29.54) * mm, "end": v(34.35, 29.67) * mm});
            skLineSegment(sketch, "E551", {"start": v(34.35, 29.67) * mm, "end": v(34.25, 29.79) * mm});
            skLineSegment(sketch, "E552", {"start": v(34.25, 29.79) * mm, "end": v(34.2, 29.85) * mm});
            skLineSegment(sketch, "E553", {"start": v(34.2, 29.85) * mm, "end": v(34.32, 29.95) * mm});
            skLineSegment(sketch, "E554", {"start": v(34.32, 29.95) * mm, "end": v(34.44, 30.05) * mm});
            skLineSegment(sketch, "E555", {"start": v(34.44, 30.05) * mm, "end": v(34.56, 30.16) * mm});
            skLineSegment(sketch, "E556", {"start": v(34.56, 30.16) * mm, "end": v(34.68, 30.26) * mm});
            skLineSegment(sketch, "E557", {"start": v(34.68, 30.26) * mm, "end": v(34.8, 30.36) * mm});
            skLineSegment(sketch, "E558", {"start": v(34.8, 30.36) * mm, "end": v(34.92, 30.47) * mm});
            skLineSegment(sketch, "E559", {"start": v(34.92, 30.47) * mm, "end": v(35.04, 30.57) * mm});
            skLineSegment(sketch, "E560", {"start": v(35.04, 30.57) * mm, "end": v(35.16, 30.67) * mm});
            skLineSegment(sketch, "E561", {"start": v(35.16, 30.67) * mm, "end": v(35.29, 30.78) * mm});
            skLineSegment(sketch, "E562", {"start": v(35.29, 30.78) * mm, "end": v(35.4, 30.88) * mm});
            skLineSegment(sketch, "E563", {"start": v(35.4, 30.88) * mm, "end": v(35.52, 30.98) * mm});
            skLineSegment(sketch, "E564", {"start": v(35.52, 30.98) * mm, "end": v(35.65, 31.09) * mm});
            skLineSegment(sketch, "E565", {"start": v(35.65, 31.09) * mm, "end": v(35.78, 31.2) * mm});
            skLineSegment(sketch, "E566", {"start": v(35.78, 31.2) * mm, "end": v(35.88, 31.33) * mm});
            skLineSegment(sketch, "E567", {"start": v(35.88, 31.33) * mm, "end": v(35.94, 31.48) * mm});
            skLineSegment(sketch, "E568", {"start": v(35.94, 31.48) * mm, "end": v(35.97, 31.64) * mm});
            skLineSegment(sketch, "E569", {"start": v(35.97, 31.64) * mm, "end": v(35.95, 31.8) * mm});
            skLineSegment(sketch, "E570", {"start": v(35.95, 31.8) * mm, "end": v(35.89, 31.95) * mm});
            skLineSegment(sketch, "E571", {"start": v(35.89, 31.95) * mm, "end": v(35.79, 32.08) * mm});
            skLineSegment(sketch, "E572", {"start": v(35.79, 32.08) * mm, "end": v(35.66, 32.19) * mm});
            skLineSegment(sketch, "E573", {"start": v(35.66, 32.19) * mm, "end": v(35.51, 32.25) * mm});
            skLineSegment(sketch, "E574", {"start": v(35.51, 32.25) * mm, "end": v(35.35, 32.27) * mm});
            skLineSegment(sketch, "E575", {"start": v(35.35, 32.27) * mm, "end": v(35.19, 32.25) * mm});
            skLineSegment(sketch, "E576", {"start": v(35.19, 32.25) * mm, "end": v(35.03, 32.2) * mm});
            skLineSegment(sketch, "E577", {"start": v(35.03, 32.2) * mm, "end": v(34.9, 32.1) * mm});
            skLineSegment(sketch, "E578", {"start": v(34.9, 32.1) * mm, "end": v(34.8, 32) * mm});
            skLineSegment(sketch, "E579", {"start": v(34.8, 32) * mm, "end": v(34.67, 31.89) * mm});
            skLineSegment(sketch, "E580", {"start": v(34.67, 31.89) * mm, "end": v(34.56, 31.78) * mm});
            skLineSegment(sketch, "E581", {"start": v(34.56, 31.78) * mm, "end": v(34.44, 31.68) * mm});
            skLineSegment(sketch, "E582", {"start": v(34.44, 31.68) * mm, "end": v(34.32, 31.57) * mm});
            skLineSegment(sketch, "E583", {"start": v(34.32, 31.57) * mm, "end": v(34.2, 31.46) * mm});
            skLineSegment(sketch, "E584", {"start": v(34.2, 31.46) * mm, "end": v(34.09, 31.36) * mm});
            skLineSegment(sketch, "E585", {"start": v(34.09, 31.36) * mm, "end": v(33.97, 31.25) * mm});
            skLineSegment(sketch, "E586", {"start": v(33.97, 31.25) * mm, "end": v(33.85, 31.15) * mm});
            skLineSegment(sketch, "E587", {"start": v(33.85, 31.15) * mm, "end": v(33.73, 31.04) * mm});
            skLineSegment(sketch, "E588", {"start": v(33.73, 31.04) * mm, "end": v(33.61, 30.93) * mm});
            skLineSegment(sketch, "E589", {"start": v(33.61, 30.93) * mm, "end": v(33.5, 30.83) * mm});
            skLineSegment(sketch, "E590", {"start": v(33.5, 30.83) * mm, "end": v(33.41, 30.75) * mm});
            skLineSegment(sketch, "E591", {"start": v(33.41, 30.75) * mm, "end": v(33.3, 30.87) * mm});
            skLineSegment(sketch, "E592", {"start": v(33.3, 30.87) * mm, "end": v(33.2, 30.98) * mm});
            skLineSegment(sketch, "E593", {"start": v(33.2, 30.98) * mm, "end": v(33.09, 31.1) * mm});
            skLineSegment(sketch, "E594", {"start": v(33.09, 31.1) * mm, "end": v(32.98, 31.2) * mm});
            skLineSegment(sketch, "E595", {"start": v(32.98, 31.2) * mm, "end": v(32.87, 31.32) * mm});
            skLineSegment(sketch, "E596", {"start": v(32.87, 31.32) * mm, "end": v(32.76, 31.44) * mm});
            skLineSegment(sketch, "E597", {"start": v(32.76, 31.44) * mm, "end": v(32.66, 31.55) * mm});
            skLineSegment(sketch, "E598", {"start": v(32.66, 31.55) * mm, "end": v(32.55, 31.67) * mm});
            skLineSegment(sketch, "E599", {"start": v(32.55, 31.67) * mm, "end": v(32.44, 31.78) * mm});
            skLineSegment(sketch, "E600", {"start": v(32.44, 31.78) * mm, "end": v(32.33, 31.9) * mm});
            skLineSegment(sketch, "E601", {"start": v(32.33, 31.9) * mm, "end": v(32.23, 32.01) * mm});
            skLineSegment(sketch, "E602", {"start": v(32.23, 32.01) * mm, "end": v(32.17, 32.07) * mm});
            skLineSegment(sketch, "E603", {"start": v(32.17, 32.07) * mm, "end": v(32.29, 32.18) * mm});
            skLineSegment(sketch, "E604", {"start": v(32.29, 32.18) * mm, "end": v(32.4, 32.3) * mm});
            skLineSegment(sketch, "E605", {"start": v(32.4, 32.3) * mm, "end": v(32.51, 32.4) * mm});
            skLineSegment(sketch, "E606", {"start": v(32.51, 32.4) * mm, "end": v(32.63, 32.51) * mm});
            skLineSegment(sketch, "E607", {"start": v(32.63, 32.51) * mm, "end": v(32.74, 32.62) * mm});
            skLineSegment(sketch, "E608", {"start": v(32.74, 32.62) * mm, "end": v(32.85, 32.74) * mm});
            skLineSegment(sketch, "E609", {"start": v(32.85, 32.74) * mm, "end": v(32.97, 32.85) * mm});
            skLineSegment(sketch, "E610", {"start": v(32.97, 32.85) * mm, "end": v(33.08, 32.96) * mm});
            skLineSegment(sketch, "E611", {"start": v(33.08, 32.96) * mm, "end": v(33.2, 33.07) * mm});
            skLineSegment(sketch, "E612", {"start": v(33.2, 33.07) * mm, "end": v(33.3, 33.18) * mm});
            skLineSegment(sketch, "E613", {"start": v(33.3, 33.18) * mm, "end": v(33.42, 33.29) * mm});
            skLineSegment(sketch, "E614", {"start": v(33.42, 33.29) * mm, "end": v(33.54, 33.4) * mm});
            skLineSegment(sketch, "E615", {"start": v(33.54, 33.4) * mm, "end": v(33.66, 33.52) * mm});
            skLineSegment(sketch, "E616", {"start": v(33.66, 33.52) * mm, "end": v(33.75, 33.65) * mm});
            skLineSegment(sketch, "E617", {"start": v(33.75, 33.65) * mm, "end": v(33.8, 33.8) * mm});
            skLineSegment(sketch, "E618", {"start": v(33.8, 33.8) * mm, "end": v(33.82, 33.97) * mm});
            skLineSegment(sketch, "E619", {"start": v(33.82, 33.97) * mm, "end": v(33.79, 34.13) * mm});
            skLineSegment(sketch, "E620", {"start": v(33.79, 34.13) * mm, "end": v(33.72, 34.28) * mm});
            skLineSegment(sketch, "E621", {"start": v(33.72, 34.28) * mm, "end": v(33.61, 34.4) * mm});
            skLineSegment(sketch, "E622", {"start": v(33.61, 34.4) * mm, "end": v(33.48, 34.5) * mm});
            skLineSegment(sketch, "E623", {"start": v(33.48, 34.5) * mm, "end": v(33.32, 34.55) * mm});
            skLineSegment(sketch, "E624", {"start": v(33.32, 34.55) * mm, "end": v(33.2, 34.57) * mm});
            skLineSegment(sketch, "E625", {"start": v(33.2, 34.57) * mm, "end": v(33.03, 34.54) * mm});
            skLineSegment(sketch, "E626", {"start": v(33.03, 34.54) * mm, "end": v(32.88, 34.48) * mm});
            skLineSegment(sketch, "E627", {"start": v(32.88, 34.48) * mm, "end": v(32.75, 34.38) * mm});
            skLineSegment(sketch, "E628", {"start": v(32.75, 34.38) * mm, "end": v(32.64, 34.27) * mm});
            skLineSegment(sketch, "E629", {"start": v(32.64, 34.27) * mm, "end": v(32.53, 34.15) * mm});
            skLineSegment(sketch, "E630", {"start": v(32.53, 34.15) * mm, "end": v(32.42, 34.04) * mm});
            skLineSegment(sketch, "E631", {"start": v(32.42, 34.04) * mm, "end": v(32.3, 33.93) * mm});
            skLineSegment(sketch, "E632", {"start": v(32.3, 33.93) * mm, "end": v(32.2, 33.81) * mm});
            skLineSegment(sketch, "E633", {"start": v(32.2, 33.81) * mm, "end": v(32.09, 33.7) * mm});
            skLineSegment(sketch, "E634", {"start": v(32.09, 33.7) * mm, "end": v(31.98, 33.59) * mm});
            skLineSegment(sketch, "E635", {"start": v(31.98, 33.59) * mm, "end": v(31.87, 33.47) * mm});
            skLineSegment(sketch, "E636", {"start": v(31.87, 33.47) * mm, "end": v(31.75, 33.36) * mm});
            skLineSegment(sketch, "E637", {"start": v(31.75, 33.36) * mm, "end": v(31.64, 33.24) * mm});
            skLineSegment(sketch, "E638", {"start": v(31.64, 33.24) * mm, "end": v(31.53, 33.13) * mm});
            skLineSegment(sketch, "E639", {"start": v(31.53, 33.13) * mm, "end": v(31.42, 33.02) * mm});
            skLineSegment(sketch, "E640", {"start": v(31.42, 33.02) * mm, "end": v(31.33, 32.92) * mm});
            skLineSegment(sketch, "E641", {"start": v(31.33, 32.92) * mm, "end": v(31.21, 33.03) * mm});
            skLineSegment(sketch, "E642", {"start": v(31.21, 33.03) * mm, "end": v(31.1, 33.13) * mm});
            skLineSegment(sketch, "E643", {"start": v(31.1, 33.13) * mm, "end": v(30.98, 33.24) * mm});
            skLineSegment(sketch, "E644", {"start": v(30.98, 33.24) * mm, "end": v(30.87, 33.35) * mm});
            skLineSegment(sketch, "E645", {"start": v(30.87, 33.35) * mm, "end": v(30.75, 33.46) * mm});
            skLineSegment(sketch, "E646", {"start": v(30.75, 33.46) * mm, "end": v(30.64, 33.56) * mm});
            skLineSegment(sketch, "E647", {"start": v(30.64, 33.56) * mm, "end": v(30.52, 33.67) * mm});
            skLineSegment(sketch, "E648", {"start": v(30.52, 33.67) * mm, "end": v(30.4, 33.78) * mm});
            skLineSegment(sketch, "E649", {"start": v(30.4, 33.78) * mm, "end": v(30.3, 33.89) * mm});
            skLineSegment(sketch, "E650", {"start": v(30.3, 33.89) * mm, "end": v(30.18, 34) * mm});
            skLineSegment(sketch, "E651", {"start": v(30.18, 34) * mm, "end": v(30.06, 34.1) * mm});
            skLineSegment(sketch, "E652", {"start": v(30.06, 34.1) * mm, "end": v(30, 34.16) * mm});
            skLineSegment(sketch, "E653", {"start": v(30, 34.16) * mm, "end": v(30.1, 34.27) * mm});
            skLineSegment(sketch, "E654", {"start": v(30.1, 34.27) * mm, "end": v(30.21, 34.39) * mm});
            skLineSegment(sketch, "E655", {"start": v(30.21, 34.39) * mm, "end": v(30.32, 34.5) * mm});
            skLineSegment(sketch, "E656", {"start": v(30.32, 34.5) * mm, "end": v(30.43, 34.63) * mm});
            skLineSegment(sketch, "E657", {"start": v(30.43, 34.63) * mm, "end": v(30.53, 34.74) * mm});
            skLineSegment(sketch, "E658", {"start": v(30.53, 34.74) * mm, "end": v(30.64, 34.86) * mm});
            skLineSegment(sketch, "E659", {"start": v(30.64, 34.86) * mm, "end": v(30.75, 34.98) * mm});
            skLineSegment(sketch, "E660", {"start": v(30.75, 34.98) * mm, "end": v(30.85, 35.1) * mm});
            skLineSegment(sketch, "E661", {"start": v(30.85, 35.1) * mm, "end": v(30.96, 35.22) * mm});
            skLineSegment(sketch, "E662", {"start": v(30.96, 35.22) * mm, "end": v(31.07, 35.33) * mm});
            skLineSegment(sketch, "E663", {"start": v(31.07, 35.33) * mm, "end": v(31.17, 35.45) * mm});
            skLineSegment(sketch, "E664", {"start": v(31.17, 35.45) * mm, "end": v(31.28, 35.57) * mm});
            skLineSegment(sketch, "E665", {"start": v(31.28, 35.57) * mm, "end": v(31.4, 35.7) * mm});
            skLineSegment(sketch, "E666", {"start": v(31.4, 35.7) * mm, "end": v(31.48, 35.84) * mm});
            skLineSegment(sketch, "E667", {"start": v(31.48, 35.84) * mm, "end": v(31.52, 36) * mm});
            skLineSegment(sketch, "E668", {"start": v(31.52, 36) * mm, "end": v(31.52, 36.16) * mm});
            skLineSegment(sketch, "E669", {"start": v(31.52, 36.16) * mm, "end": v(31.48, 36.32) * mm});
            skLineSegment(sketch, "E670", {"start": v(31.48, 36.32) * mm, "end": v(31.4, 36.46) * mm});
            skLineSegment(sketch, "E671", {"start": v(31.4, 36.46) * mm, "end": v(31.29, 36.58) * mm});
            skLineSegment(sketch, "E672", {"start": v(31.29, 36.58) * mm, "end": v(31.15, 36.66) * mm});
            skLineSegment(sketch, "E673", {"start": v(31.15, 36.66) * mm, "end": v(31, 36.7) * mm});
            skLineSegment(sketch, "E674", {"start": v(31, 36.7) * mm, "end": v(30.9, 36.71) * mm});
            skLineSegment(sketch, "E675", {"start": v(30.9, 36.71) * mm, "end": v(30.73, 36.69) * mm});
            skLineSegment(sketch, "E676", {"start": v(30.73, 36.69) * mm, "end": v(30.58, 36.62) * mm});
            skLineSegment(sketch, "E677", {"start": v(30.58, 36.62) * mm, "end": v(30.45, 36.52) * mm});
            skLineSegment(sketch, "E678", {"start": v(30.45, 36.52) * mm, "end": v(30.34, 36.4) * mm});
            skLineSegment(sketch, "E679", {"start": v(30.34, 36.4) * mm, "end": v(30.24, 36.27) * mm});
            skLineSegment(sketch, "E680", {"start": v(30.24, 36.27) * mm, "end": v(30.14, 36.15) * mm});
            skLineSegment(sketch, "E681", {"start": v(30.14, 36.15) * mm, "end": v(30.03, 36.03) * mm});
            skLineSegment(sketch, "E682", {"start": v(30.03, 36.03) * mm, "end": v(29.93, 35.91) * mm});
            skLineSegment(sketch, "E683", {"start": v(29.93, 35.91) * mm, "end": v(29.83, 35.8) * mm});
            skLineSegment(sketch, "E684", {"start": v(29.83, 35.8) * mm, "end": v(29.72, 35.67) * mm});
            skLineSegment(sketch, "E685", {"start": v(29.72, 35.67) * mm, "end": v(29.62, 35.55) * mm});
            skLineSegment(sketch, "E686", {"start": v(29.62, 35.55) * mm, "end": v(29.52, 35.43) * mm});
            skLineSegment(sketch, "E687", {"start": v(29.52, 35.43) * mm, "end": v(29.41, 35.3) * mm});
            skLineSegment(sketch, "E688", {"start": v(29.41, 35.3) * mm, "end": v(29.31, 35.19) * mm});
            skLineSegment(sketch, "E689", {"start": v(29.31, 35.19) * mm, "end": v(29.2, 35.07) * mm});
            skLineSegment(sketch, "E690", {"start": v(29.2, 35.07) * mm, "end": v(29.1, 34.95) * mm});
            skLineSegment(sketch, "E691", {"start": v(29.1, 34.95) * mm, "end": v(28.98, 35.05) * mm});
            skLineSegment(sketch, "E692", {"start": v(28.98, 35.05) * mm, "end": v(28.86, 35.14) * mm});
            skLineSegment(sketch, "E693", {"start": v(28.86, 35.14) * mm, "end": v(28.74, 35.24) * mm});
            skLineSegment(sketch, "E694", {"start": v(28.74, 35.24) * mm, "end": v(28.62, 35.34) * mm});
            skLineSegment(sketch, "E695", {"start": v(28.62, 35.34) * mm, "end": v(28.5, 35.44) * mm});
            skLineSegment(sketch, "E696", {"start": v(28.5, 35.44) * mm, "end": v(28.37, 35.54) * mm});
            skLineSegment(sketch, "E697", {"start": v(28.37, 35.54) * mm, "end": v(28.25, 35.64) * mm});
            skLineSegment(sketch, "E698", {"start": v(28.25, 35.64) * mm, "end": v(28.13, 35.74) * mm});
            skLineSegment(sketch, "E699", {"start": v(28.13, 35.74) * mm, "end": v(28, 35.84) * mm});
            skLineSegment(sketch, "E700", {"start": v(28, 35.84) * mm, "end": v(27.89, 35.94) * mm});
            skLineSegment(sketch, "E701", {"start": v(27.89, 35.94) * mm, "end": v(27.77, 36.04) * mm});
            skLineSegment(sketch, "E702", {"start": v(27.77, 36.04) * mm, "end": v(27.7, 36.1) * mm});
            skLineSegment(sketch, "E703", {"start": v(27.7, 36.1) * mm, "end": v(27.8, 36.22) * mm});
            skLineSegment(sketch, "E704", {"start": v(27.8, 36.22) * mm, "end": v(27.9, 36.34) * mm});
            skLineSegment(sketch, "E705", {"start": v(27.9, 36.34) * mm, "end": v(28, 36.47) * mm});
            skLineSegment(sketch, "E706", {"start": v(28, 36.47) * mm, "end": v(28.1, 36.6) * mm});
            skLineSegment(sketch, "E707", {"start": v(28.1, 36.6) * mm, "end": v(28.2, 36.71) * mm});
            skLineSegment(sketch, "E708", {"start": v(28.2, 36.71) * mm, "end": v(28.3, 36.84) * mm});
            skLineSegment(sketch, "E709", {"start": v(28.3, 36.84) * mm, "end": v(28.4, 36.97) * mm});
            skLineSegment(sketch, "E710", {"start": v(28.4, 36.97) * mm, "end": v(28.49, 37.09) * mm});
            skLineSegment(sketch, "E711", {"start": v(28.49, 37.09) * mm, "end": v(28.59, 37.22) * mm});
            skLineSegment(sketch, "E712", {"start": v(28.59, 37.22) * mm, "end": v(28.69, 37.34) * mm});
            skLineSegment(sketch, "E713", {"start": v(28.69, 37.34) * mm, "end": v(28.78, 37.46) * mm});
            skLineSegment(sketch, "E714", {"start": v(28.78, 37.46) * mm, "end": v(28.88, 37.59) * mm});
            skLineSegment(sketch, "E715", {"start": v(28.88, 37.59) * mm, "end": v(28.99, 37.72) * mm});
            skLineSegment(sketch, "E716", {"start": v(28.99, 37.72) * mm, "end": v(29.06, 37.87) * mm});
            skLineSegment(sketch, "E717", {"start": v(29.06, 37.87) * mm, "end": v(29.1, 38.03) * mm});
            skLineSegment(sketch, "E718", {"start": v(29.1, 38.03) * mm, "end": v(29.09, 38.2) * mm});
            skLineSegment(sketch, "E719", {"start": v(29.09, 38.2) * mm, "end": v(29.04, 38.35) * mm});
            skLineSegment(sketch, "E720", {"start": v(29.04, 38.35) * mm, "end": v(28.95, 38.49) * mm});
            skLineSegment(sketch, "E721", {"start": v(28.95, 38.49) * mm, "end": v(28.83, 38.6) * mm});
            skLineSegment(sketch, "E722", {"start": v(28.83, 38.6) * mm, "end": v(28.68, 38.67) * mm});
            skLineSegment(sketch, "E723", {"start": v(28.68, 38.67) * mm, "end": v(28.52, 38.7) * mm});
            skLineSegment(sketch, "E724", {"start": v(28.52, 38.7) * mm, "end": v(28.49, 38.7) * mm});
            skLineSegment(sketch, "E725", {"start": v(28.49, 38.7) * mm, "end": v(28.33, 38.69) * mm});
            skLineSegment(sketch, "E726", {"start": v(28.33, 38.69) * mm, "end": v(28.17, 38.63) * mm});
            skLineSegment(sketch, "E727", {"start": v(28.17, 38.63) * mm, "end": v(28.04, 38.53) * mm});
            skLineSegment(sketch, "E728", {"start": v(28.04, 38.53) * mm, "end": v(27.94, 38.4) * mm});
            skLineSegment(sketch, "E729", {"start": v(27.94, 38.4) * mm, "end": v(27.84, 38.28) * mm});
            skLineSegment(sketch, "E730", {"start": v(27.84, 38.28) * mm, "end": v(27.75, 38.15) * mm});
            skLineSegment(sketch, "E731", {"start": v(27.75, 38.15) * mm, "end": v(27.65, 38.02) * mm});
            skLineSegment(sketch, "E732", {"start": v(27.65, 38.02) * mm, "end": v(27.56, 37.9) * mm});
            skLineSegment(sketch, "E733", {"start": v(27.56, 37.9) * mm, "end": v(27.46, 37.77) * mm});
            skLineSegment(sketch, "E734", {"start": v(27.46, 37.77) * mm, "end": v(27.37, 37.64) * mm});
            skLineSegment(sketch, "E735", {"start": v(27.37, 37.64) * mm, "end": v(27.27, 37.51) * mm});
            skLineSegment(sketch, "E736", {"start": v(27.27, 37.51) * mm, "end": v(27.18, 37.39) * mm});
            skLineSegment(sketch, "E737", {"start": v(27.18, 37.39) * mm, "end": v(27.08, 37.26) * mm});
            skLineSegment(sketch, "E738", {"start": v(27.08, 37.26) * mm, "end": v(26.99, 37.13) * mm});
            skLineSegment(sketch, "E739", {"start": v(26.99, 37.13) * mm, "end": v(26.9, 37) * mm});
            skLineSegment(sketch, "E740", {"start": v(26.9, 37) * mm, "end": v(26.8, 36.88) * mm});
            skLineSegment(sketch, "E741", {"start": v(26.8, 36.88) * mm, "end": v(26.75, 36.82) * mm});
            skLineSegment(sketch, "E742", {"start": v(26.75, 36.82) * mm, "end": v(26.63, 36.91) * mm});
            skLineSegment(sketch, "E743", {"start": v(26.63, 36.91) * mm, "end": v(26.5, 37) * mm});
            skLineSegment(sketch, "E744", {"start": v(26.5, 37) * mm, "end": v(26.37, 37.1) * mm});
            skLineSegment(sketch, "E745", {"start": v(26.37, 37.1) * mm, "end": v(26.24, 37.19) * mm});
            skLineSegment(sketch, "E746", {"start": v(26.24, 37.19) * mm, "end": v(26.12, 37.28) * mm});
            skLineSegment(sketch, "E747", {"start": v(26.12, 37.28) * mm, "end": v(25.99, 37.37) * mm});
            skLineSegment(sketch, "E748", {"start": v(25.99, 37.37) * mm, "end": v(25.86, 37.46) * mm});
            skLineSegment(sketch, "E749", {"start": v(25.86, 37.46) * mm, "end": v(25.73, 37.56) * mm});
            skLineSegment(sketch, "E750", {"start": v(25.73, 37.56) * mm, "end": v(25.6, 37.65) * mm});
            skLineSegment(sketch, "E751", {"start": v(25.6, 37.65) * mm, "end": v(25.48, 37.74) * mm});
            skLineSegment(sketch, "E752", {"start": v(25.48, 37.74) * mm, "end": v(25.35, 37.83) * mm});
            skLineSegment(sketch, "E753", {"start": v(25.35, 37.83) * mm, "end": v(25.28, 37.88) * mm});
            skLineSegment(sketch, "E754", {"start": v(25.28, 37.88) * mm, "end": v(25.37, 38) * mm});
            skLineSegment(sketch, "E755", {"start": v(25.37, 38) * mm, "end": v(25.46, 38.14) * mm});
            skLineSegment(sketch, "E756", {"start": v(25.46, 38.14) * mm, "end": v(25.55, 38.27) * mm});
            skLineSegment(sketch, "E757", {"start": v(25.55, 38.27) * mm, "end": v(25.64, 38.4) * mm});
            skLineSegment(sketch, "E758", {"start": v(25.64, 38.4) * mm, "end": v(25.73, 38.53) * mm});
            skLineSegment(sketch, "E759", {"start": v(25.73, 38.53) * mm, "end": v(25.82, 38.66) * mm});
            skLineSegment(sketch, "E760", {"start": v(25.82, 38.66) * mm, "end": v(25.91, 38.8) * mm});
            skLineSegment(sketch, "E761", {"start": v(25.91, 38.8) * mm, "end": v(26, 38.92) * mm});
            skLineSegment(sketch, "E762", {"start": v(26, 38.92) * mm, "end": v(26.1, 39.05) * mm});
            skLineSegment(sketch, "E763", {"start": v(26.1, 39.05) * mm, "end": v(26.18, 39.18) * mm});
            skLineSegment(sketch, "E764", {"start": v(26.18, 39.18) * mm, "end": v(26.27, 39.31) * mm});
            skLineSegment(sketch, "E765", {"start": v(26.27, 39.31) * mm, "end": v(26.36, 39.45) * mm});
            skLineSegment(sketch, "E766", {"start": v(26.36, 39.45) * mm, "end": v(26.46, 39.59) * mm});
            skLineSegment(sketch, "E767", {"start": v(26.46, 39.59) * mm, "end": v(26.52, 39.74) * mm});
            skLineSegment(sketch, "E768", {"start": v(26.52, 39.74) * mm, "end": v(26.55, 39.9) * mm});
            skLineSegment(sketch, "E769", {"start": v(26.55, 39.9) * mm, "end": v(26.53, 40.06) * mm});
            skLineSegment(sketch, "E770", {"start": v(26.53, 40.06) * mm, "end": v(26.47, 40.21) * mm});
            skLineSegment(sketch, "E771", {"start": v(26.47, 40.21) * mm, "end": v(26.37, 40.35) * mm});
            skLineSegment(sketch, "E772", {"start": v(26.37, 40.35) * mm, "end": v(26.24, 40.45) * mm});
            skLineSegment(sketch, "E773", {"start": v(26.24, 40.45) * mm, "end": v(26.09, 40.51) * mm});
            skLineSegment(sketch, "E774", {"start": v(26.09, 40.51) * mm, "end": v(25.93, 40.54) * mm});
            skLineSegment(sketch, "E775", {"start": v(25.93, 40.54) * mm, "end": v(25.77, 40.52) * mm});
            skLineSegment(sketch, "E776", {"start": v(25.77, 40.52) * mm, "end": v(25.61, 40.45) * mm});
            skLineSegment(sketch, "E777", {"start": v(25.61, 40.45) * mm, "end": v(25.48, 40.36) * mm});
            skLineSegment(sketch, "E778", {"start": v(25.48, 40.36) * mm, "end": v(25.39, 40.23) * mm});
            skLineSegment(sketch, "E779", {"start": v(25.39, 40.23) * mm, "end": v(25.3, 40.1) * mm});
            skLineSegment(sketch, "E780", {"start": v(25.3, 40.1) * mm, "end": v(25.21, 39.97) * mm});
            skLineSegment(sketch, "E781", {"start": v(25.21, 39.97) * mm, "end": v(25.13, 39.84) * mm});
            skLineSegment(sketch, "E782", {"start": v(25.13, 39.84) * mm, "end": v(25.04, 39.7) * mm});
            skLineSegment(sketch, "E783", {"start": v(25.04, 39.7) * mm, "end": v(24.95, 39.57) * mm});
            skLineSegment(sketch, "E784", {"start": v(24.95, 39.57) * mm, "end": v(24.87, 39.44) * mm});
            skLineSegment(sketch, "E785", {"start": v(24.87, 39.44) * mm, "end": v(24.78, 39.3) * mm});
            skLineSegment(sketch, "E786", {"start": v(24.78, 39.3) * mm, "end": v(24.7, 39.17) * mm});
            skLineSegment(sketch, "E787", {"start": v(24.7, 39.17) * mm, "end": v(24.6, 39.04) * mm});
            skLineSegment(sketch, "E788", {"start": v(24.6, 39.04) * mm, "end": v(24.52, 38.9) * mm});
            skLineSegment(sketch, "E789", {"start": v(24.52, 38.9) * mm, "end": v(24.44, 38.77) * mm});
            skLineSegment(sketch, "E790", {"start": v(24.44, 38.77) * mm, "end": v(24.35, 38.64) * mm});
            skLineSegment(sketch, "E791", {"start": v(24.35, 38.64) * mm, "end": v(24.29, 38.54) * mm});
            skLineSegment(sketch, "E792", {"start": v(24.29, 38.54) * mm, "end": v(24.15, 38.63) * mm});
            skLineSegment(sketch, "E793", {"start": v(24.15, 38.63) * mm, "end": v(24.02, 38.7) * mm});
            skLineSegment(sketch, "E794", {"start": v(24.02, 38.7) * mm, "end": v(23.89, 38.8) * mm});
            skLineSegment(sketch, "E795", {"start": v(23.89, 38.8) * mm, "end": v(23.75, 38.87) * mm});
            skLineSegment(sketch, "E796", {"start": v(23.75, 38.87) * mm, "end": v(23.62, 38.96) * mm});
            skLineSegment(sketch, "E797", {"start": v(23.62, 38.96) * mm, "end": v(23.49, 39.04) * mm});
            skLineSegment(sketch, "E798", {"start": v(23.49, 39.04) * mm, "end": v(23.35, 39.12) * mm});
            skLineSegment(sketch, "E799", {"start": v(23.35, 39.12) * mm, "end": v(23.22, 39.2) * mm});
            skLineSegment(sketch, "E800", {"start": v(23.22, 39.2) * mm, "end": v(23.09, 39.3) * mm});
            skLineSegment(sketch, "E801", {"start": v(23.09, 39.3) * mm, "end": v(22.95, 39.37) * mm});
            skLineSegment(sketch, "E802", {"start": v(22.95, 39.37) * mm, "end": v(22.82, 39.46) * mm});
            skLineSegment(sketch, "E803", {"start": v(22.82, 39.46) * mm, "end": v(22.75, 39.5) * mm});
            skLineSegment(sketch, "E804", {"start": v(22.75, 39.5) * mm, "end": v(22.83, 39.63) * mm});
            skLineSegment(sketch, "E805", {"start": v(22.83, 39.63) * mm, "end": v(22.91, 39.77) * mm});
            skLineSegment(sketch, "E806", {"start": v(22.91, 39.77) * mm, "end": v(23, 39.9) * mm});
            skLineSegment(sketch, "E807", {"start": v(23, 39.9) * mm, "end": v(23.07, 40.04) * mm});
            skLineSegment(sketch, "E808", {"start": v(23.07, 40.04) * mm, "end": v(23.15, 40.18) * mm});
            skLineSegment(sketch, "E809", {"start": v(23.15, 40.18) * mm, "end": v(23.24, 40.32) * mm});
            skLineSegment(sketch, "E810", {"start": v(23.24, 40.32) * mm, "end": v(23.32, 40.45) * mm});
            skLineSegment(sketch, "E811", {"start": v(23.32, 40.45) * mm, "end": v(23.4, 40.59) * mm});
            skLineSegment(sketch, "E812", {"start": v(23.4, 40.59) * mm, "end": v(23.48, 40.73) * mm});
            skLineSegment(sketch, "E813", {"start": v(23.48, 40.73) * mm, "end": v(23.56, 40.86) * mm});
            skLineSegment(sketch, "E814", {"start": v(23.56, 40.86) * mm, "end": v(23.64, 41) * mm});
            skLineSegment(sketch, "E815", {"start": v(23.64, 41) * mm, "end": v(23.72, 41.14) * mm});
            skLineSegment(sketch, "E816", {"start": v(23.72, 41.14) * mm, "end": v(23.8, 41.28) * mm});
            skLineSegment(sketch, "E817", {"start": v(23.8, 41.28) * mm, "end": v(23.86, 41.44) * mm});
            skLineSegment(sketch, "E818", {"start": v(23.86, 41.44) * mm, "end": v(23.88, 41.6) * mm});
            skLineSegment(sketch, "E819", {"start": v(23.88, 41.6) * mm, "end": v(23.85, 41.76) * mm});
            skLineSegment(sketch, "E820", {"start": v(23.85, 41.76) * mm, "end": v(23.78, 41.9) * mm});
            skLineSegment(sketch, "E821", {"start": v(23.78, 41.9) * mm, "end": v(23.67, 42.03) * mm});
            skLineSegment(sketch, "E822", {"start": v(23.67, 42.03) * mm, "end": v(23.54, 42.13) * mm});
            skLineSegment(sketch, "E823", {"start": v(23.54, 42.13) * mm, "end": v(23.38, 42.18) * mm});
            skLineSegment(sketch, "E824", {"start": v(23.38, 42.18) * mm, "end": v(23.25, 42.2) * mm});
            skLineSegment(sketch, "E825", {"start": v(23.25, 42.2) * mm, "end": v(23.09, 42.17) * mm});
            skLineSegment(sketch, "E826", {"start": v(23.09, 42.17) * mm, "end": v(22.94, 42.1) * mm});
            skLineSegment(sketch, "E827", {"start": v(22.94, 42.1) * mm, "end": v(22.8, 42) * mm});
            skLineSegment(sketch, "E828", {"start": v(22.8, 42) * mm, "end": v(22.71, 41.88) * mm});
            skLineSegment(sketch, "E829", {"start": v(22.71, 41.88) * mm, "end": v(22.63, 41.74) * mm});
            skLineSegment(sketch, "E830", {"start": v(22.63, 41.74) * mm, "end": v(22.56, 41.6) * mm});
            skLineSegment(sketch, "E831", {"start": v(22.56, 41.6) * mm, "end": v(22.48, 41.46) * mm});
            skLineSegment(sketch, "E832", {"start": v(22.48, 41.46) * mm, "end": v(22.4, 41.33) * mm});
            skLineSegment(sketch, "E833", {"start": v(22.4, 41.33) * mm, "end": v(22.32, 41.19) * mm});
            skLineSegment(sketch, "E834", {"start": v(22.32, 41.19) * mm, "end": v(22.24, 41.05) * mm});
            skLineSegment(sketch, "E835", {"start": v(22.24, 41.05) * mm, "end": v(22.17, 40.9) * mm});
            skLineSegment(sketch, "E836", {"start": v(22.17, 40.9) * mm, "end": v(22.1, 40.77) * mm});
            skLineSegment(sketch, "E837", {"start": v(22.1, 40.77) * mm, "end": v(22.01, 40.63) * mm});
            skLineSegment(sketch, "E838", {"start": v(22.01, 40.63) * mm, "end": v(21.94, 40.5) * mm});
            skLineSegment(sketch, "E839", {"start": v(21.94, 40.5) * mm, "end": v(21.86, 40.36) * mm});
            skLineSegment(sketch, "E840", {"start": v(21.86, 40.36) * mm, "end": v(21.78, 40.22) * mm});
            skLineSegment(sketch, "E841", {"start": v(21.78, 40.22) * mm, "end": v(21.71, 40.1) * mm});
            skLineSegment(sketch, "E842", {"start": v(21.71, 40.1) * mm, "end": v(21.57, 40.17) * mm});
            skLineSegment(sketch, "E843", {"start": v(21.57, 40.17) * mm, "end": v(21.44, 40.25) * mm});
            skLineSegment(sketch, "E844", {"start": v(21.44, 40.25) * mm, "end": v(21.3, 40.32) * mm});
            skLineSegment(sketch, "E845", {"start": v(21.3, 40.32) * mm, "end": v(21.16, 40.4) * mm});
            skLineSegment(sketch, "E846", {"start": v(21.16, 40.4) * mm, "end": v(21.02, 40.47) * mm});
            skLineSegment(sketch, "E847", {"start": v(21.02, 40.47) * mm, "end": v(20.88, 40.54) * mm});
            skLineSegment(sketch, "E848", {"start": v(20.88, 40.54) * mm, "end": v(20.74, 40.62) * mm});
            skLineSegment(sketch, "E849", {"start": v(20.74, 40.62) * mm, "end": v(20.6, 40.7) * mm});
            skLineSegment(sketch, "E850", {"start": v(20.6, 40.7) * mm, "end": v(20.46, 40.76) * mm});
            skLineSegment(sketch, "E851", {"start": v(20.46, 40.76) * mm, "end": v(20.33, 40.84) * mm});
            skLineSegment(sketch, "E852", {"start": v(20.33, 40.84) * mm, "end": v(20.19, 40.91) * mm});
            skLineSegment(sketch, "E853", {"start": v(20.19, 40.91) * mm, "end": v(20.12, 40.95) * mm});
            skLineSegment(sketch, "E854", {"start": v(20.12, 40.95) * mm, "end": v(20.19, 41.1) * mm});
            skLineSegment(sketch, "E855", {"start": v(20.19, 41.1) * mm, "end": v(20.26, 41.23) * mm});
            skLineSegment(sketch, "E856", {"start": v(20.26, 41.23) * mm, "end": v(20.33, 41.38) * mm});
            skLineSegment(sketch, "E857", {"start": v(20.33, 41.38) * mm, "end": v(20.4, 41.52) * mm});
            skLineSegment(sketch, "E858", {"start": v(20.4, 41.52) * mm, "end": v(20.48, 41.66) * mm});
            skLineSegment(sketch, "E859", {"start": v(20.48, 41.66) * mm, "end": v(20.55, 41.8) * mm});
            skLineSegment(sketch, "E860", {"start": v(20.55, 41.8) * mm, "end": v(20.62, 41.94) * mm});
            skLineSegment(sketch, "E861", {"start": v(20.62, 41.94) * mm, "end": v(20.7, 42.08) * mm});
            skLineSegment(sketch, "E862", {"start": v(20.7, 42.08) * mm, "end": v(20.76, 42.22) * mm});
            skLineSegment(sketch, "E863", {"start": v(20.76, 42.22) * mm, "end": v(20.84, 42.36) * mm});
            skLineSegment(sketch, "E864", {"start": v(20.84, 42.36) * mm, "end": v(20.9, 42.5) * mm});
            skLineSegment(sketch, "E865", {"start": v(20.9, 42.5) * mm, "end": v(20.98, 42.65) * mm});
            skLineSegment(sketch, "E866", {"start": v(20.98, 42.65) * mm, "end": v(21.06, 42.8) * mm});
            skLineSegment(sketch, "E867", {"start": v(21.06, 42.8) * mm, "end": v(21.1, 42.96) * mm});
            skLineSegment(sketch, "E868", {"start": v(21.1, 42.96) * mm, "end": v(21.1, 43.12) * mm});
            skLineSegment(sketch, "E869", {"start": v(21.1, 43.12) * mm, "end": v(21.07, 43.28) * mm});
            skLineSegment(sketch, "E870", {"start": v(21.07, 43.28) * mm, "end": v(20.99, 43.42) * mm});
            skLineSegment(sketch, "E871", {"start": v(20.99, 43.42) * mm, "end": v(20.87, 43.54) * mm});
            skLineSegment(sketch, "E872", {"start": v(20.87, 43.54) * mm, "end": v(20.73, 43.62) * mm});
            skLineSegment(sketch, "E873", {"start": v(20.73, 43.62) * mm, "end": v(20.57, 43.67) * mm});
            skLineSegment(sketch, "E874", {"start": v(20.57, 43.67) * mm, "end": v(20.47, 43.67) * mm});
            skLineSegment(sketch, "E875", {"start": v(20.47, 43.67) * mm, "end": v(20.31, 43.65) * mm});
            skLineSegment(sketch, "E876", {"start": v(20.31, 43.65) * mm, "end": v(20.16, 43.59) * mm});
            skLineSegment(sketch, "E877", {"start": v(20.16, 43.59) * mm, "end": v(20.03, 43.48) * mm});
            skLineSegment(sketch, "E878", {"start": v(20.03, 43.48) * mm, "end": v(19.94, 43.35) * mm});
            skLineSegment(sketch, "E879", {"start": v(19.94, 43.35) * mm, "end": v(19.86, 43.2) * mm});
            skLineSegment(sketch, "E880", {"start": v(19.86, 43.2) * mm, "end": v(19.8, 43.06) * mm});
            skLineSegment(sketch, "E881", {"start": v(19.8, 43.06) * mm, "end": v(19.73, 42.92) * mm});
            skLineSegment(sketch, "E882", {"start": v(19.73, 42.92) * mm, "end": v(19.66, 42.77) * mm});
            skLineSegment(sketch, "E883", {"start": v(19.66, 42.77) * mm, "end": v(19.59, 42.63) * mm});
            skLineSegment(sketch, "E884", {"start": v(19.59, 42.63) * mm, "end": v(19.52, 42.49) * mm});
            skLineSegment(sketch, "E885", {"start": v(19.52, 42.49) * mm, "end": v(19.45, 42.34) * mm});
            skLineSegment(sketch, "E886", {"start": v(19.45, 42.34) * mm, "end": v(19.38, 42.2) * mm});
            skLineSegment(sketch, "E887", {"start": v(19.38, 42.2) * mm, "end": v(19.32, 42.06) * mm});
            skLineSegment(sketch, "E888", {"start": v(19.32, 42.06) * mm, "end": v(19.25, 41.91) * mm});
            skLineSegment(sketch, "E889", {"start": v(19.25, 41.91) * mm, "end": v(19.18, 41.77) * mm});
            skLineSegment(sketch, "E890", {"start": v(19.18, 41.77) * mm, "end": v(19.11, 41.63) * mm});
            skLineSegment(sketch, "E891", {"start": v(19.11, 41.63) * mm, "end": v(19.04, 41.48) * mm});
            skLineSegment(sketch, "E892", {"start": v(19.04, 41.48) * mm, "end": v(18.9, 41.55) * mm});
            skLineSegment(sketch, "E893", {"start": v(18.9, 41.55) * mm, "end": v(18.76, 41.61) * mm});
            skLineSegment(sketch, "E894", {"start": v(18.76, 41.61) * mm, "end": v(18.61, 41.68) * mm});
            skLineSegment(sketch, "E895", {"start": v(18.61, 41.68) * mm, "end": v(18.47, 41.74) * mm});
            skLineSegment(sketch, "E896", {"start": v(18.47, 41.74) * mm, "end": v(18.33, 41.8) * mm});
            skLineSegment(sketch, "E897", {"start": v(18.33, 41.8) * mm, "end": v(18.18, 41.87) * mm});
            skLineSegment(sketch, "E898", {"start": v(18.18, 41.87) * mm, "end": v(18.04, 41.93) * mm});
            skLineSegment(sketch, "E899", {"start": v(18.04, 41.93) * mm, "end": v(17.9, 42) * mm});
            skLineSegment(sketch, "E900", {"start": v(17.9, 42) * mm, "end": v(17.75, 42.06) * mm});
            skLineSegment(sketch, "E901", {"start": v(17.75, 42.06) * mm, "end": v(17.6, 42.13) * mm});
            skLineSegment(sketch, "E902", {"start": v(17.6, 42.13) * mm, "end": v(17.47, 42.2) * mm});
            skLineSegment(sketch, "E903", {"start": v(17.47, 42.2) * mm, "end": v(17.4, 42.23) * mm});
            skLineSegment(sketch, "E904", {"start": v(17.4, 42.23) * mm, "end": v(17.46, 42.37) * mm});
            skLineSegment(sketch, "E905", {"start": v(17.46, 42.37) * mm, "end": v(17.52, 42.52) * mm});
            skLineSegment(sketch, "E906", {"start": v(17.52, 42.52) * mm, "end": v(17.58, 42.67) * mm});
            skLineSegment(sketch, "E907", {"start": v(17.58, 42.67) * mm, "end": v(17.64, 42.8) * mm});
            skLineSegment(sketch, "E908", {"start": v(17.64, 42.8) * mm, "end": v(17.7, 42.95) * mm});
            skLineSegment(sketch, "E909", {"start": v(17.7, 42.95) * mm, "end": v(17.77, 43.1) * mm});
            skLineSegment(sketch, "E910", {"start": v(17.77, 43.1) * mm, "end": v(17.83, 43.25) * mm});
            skLineSegment(sketch, "E911", {"start": v(17.83, 43.25) * mm, "end": v(17.9, 43.4) * mm});
            skLineSegment(sketch, "E912", {"start": v(17.9, 43.4) * mm, "end": v(17.96, 43.54) * mm});
            skLineSegment(sketch, "E913", {"start": v(17.96, 43.54) * mm, "end": v(18.02, 43.68) * mm});
            skLineSegment(sketch, "E914", {"start": v(18.02, 43.68) * mm, "end": v(18.08, 43.83) * mm});
            skLineSegment(sketch, "E915", {"start": v(18.08, 43.83) * mm, "end": v(18.14, 43.98) * mm});
            skLineSegment(sketch, "E916", {"start": v(18.14, 43.98) * mm, "end": v(18.21, 44.13) * mm});
            skLineSegment(sketch, "E917", {"start": v(18.21, 44.13) * mm, "end": v(18.25, 44.3) * mm});
            skLineSegment(sketch, "E918", {"start": v(18.25, 44.3) * mm, "end": v(18.24, 44.46) * mm});
            skLineSegment(sketch, "E919", {"start": v(18.24, 44.46) * mm, "end": v(18.19, 44.61) * mm});
            skLineSegment(sketch, "E920", {"start": v(18.19, 44.61) * mm, "end": v(18.1, 44.75) * mm});
            skLineSegment(sketch, "E921", {"start": v(18.1, 44.75) * mm, "end": v(17.98, 44.86) * mm});
            skLineSegment(sketch, "E922", {"start": v(17.98, 44.86) * mm, "end": v(17.83, 44.94) * mm});
            skLineSegment(sketch, "E923", {"start": v(17.83, 44.94) * mm, "end": v(17.67, 44.97) * mm});
            skLineSegment(sketch, "E924", {"start": v(17.67, 44.97) * mm, "end": v(17.64, 44.97) * mm});
            skLineSegment(sketch, "E925", {"start": v(17.64, 44.97) * mm, "end": v(17.47, 44.95) * mm});
            skLineSegment(sketch, "E926", {"start": v(17.47, 44.95) * mm, "end": v(17.32, 44.9) * mm});
            skLineSegment(sketch, "E927", {"start": v(17.32, 44.9) * mm, "end": v(17.19, 44.8) * mm});
            skLineSegment(sketch, "E928", {"start": v(17.19, 44.8) * mm, "end": v(17.09, 44.67) * mm});
            skLineSegment(sketch, "E929", {"start": v(17.09, 44.67) * mm, "end": v(17.02, 44.52) * mm});
            skLineSegment(sketch, "E930", {"start": v(17.02, 44.52) * mm, "end": v(16.96, 44.37) * mm});
            skLineSegment(sketch, "E931", {"start": v(16.96, 44.37) * mm, "end": v(16.9, 44.23) * mm});
            skLineSegment(sketch, "E932", {"start": v(16.9, 44.23) * mm, "end": v(16.84, 44.08) * mm});
            skLineSegment(sketch, "E933", {"start": v(16.84, 44.08) * mm, "end": v(16.78, 43.93) * mm});
            skLineSegment(sketch, "E934", {"start": v(16.78, 43.93) * mm, "end": v(16.73, 43.78) * mm});
            skLineSegment(sketch, "E935", {"start": v(16.73, 43.78) * mm, "end": v(16.67, 43.63) * mm});
            skLineSegment(sketch, "E936", {"start": v(16.67, 43.63) * mm, "end": v(16.6, 43.49) * mm});
            skLineSegment(sketch, "E937", {"start": v(16.6, 43.49) * mm, "end": v(16.55, 43.34) * mm});
            skLineSegment(sketch, "E938", {"start": v(16.55, 43.34) * mm, "end": v(16.49, 43.2) * mm});
            skLineSegment(sketch, "E939", {"start": v(16.49, 43.2) * mm, "end": v(16.43, 43.05) * mm});
            skLineSegment(sketch, "E940", {"start": v(16.43, 43.05) * mm, "end": v(16.37, 42.9) * mm});
            skLineSegment(sketch, "E941", {"start": v(16.37, 42.9) * mm, "end": v(16.31, 42.75) * mm});
            skLineSegment(sketch, "E942", {"start": v(16.31, 42.75) * mm, "end": v(16.29, 42.69) * mm});
            skLineSegment(sketch, "E943", {"start": v(16.29, 42.69) * mm, "end": v(16.14, 42.74) * mm});
            skLineSegment(sketch, "E944", {"start": v(16.14, 42.74) * mm, "end": v(16, 42.8) * mm});
            skLineSegment(sketch, "E945", {"start": v(16, 42.8) * mm, "end": v(15.85, 42.85) * mm});
            skLineSegment(sketch, "E946", {"start": v(15.85, 42.85) * mm, "end": v(15.7, 42.9) * mm});
            skLineSegment(sketch, "E947", {"start": v(15.7, 42.9) * mm, "end": v(15.55, 42.96) * mm});
            skLineSegment(sketch, "E948", {"start": v(15.55, 42.96) * mm, "end": v(15.4, 43.02) * mm});
            skLineSegment(sketch, "E949", {"start": v(15.4, 43.02) * mm, "end": v(15.26, 43.07) * mm});
            skLineSegment(sketch, "E950", {"start": v(15.26, 43.07) * mm, "end": v(15.1, 43.13) * mm});
            skLineSegment(sketch, "E951", {"start": v(15.1, 43.13) * mm, "end": v(14.96, 43.18) * mm});
            skLineSegment(sketch, "E952", {"start": v(14.96, 43.18) * mm, "end": v(14.81, 43.24) * mm});
            skLineSegment(sketch, "E953", {"start": v(14.81, 43.24) * mm, "end": v(14.67, 43.3) * mm});
            skLineSegment(sketch, "E954", {"start": v(14.67, 43.3) * mm, "end": v(14.6, 43.32) * mm});
            skLineSegment(sketch, "E955", {"start": v(14.6, 43.32) * mm, "end": v(14.65, 43.47) * mm});
            skLineSegment(sketch, "E956", {"start": v(14.65, 43.47) * mm, "end": v(14.7, 43.62) * mm});
            skLineSegment(sketch, "E957", {"start": v(14.7, 43.62) * mm, "end": v(14.75, 43.77) * mm});
            skLineSegment(sketch, "E958", {"start": v(14.75, 43.77) * mm, "end": v(14.8, 43.92) * mm});
            skLineSegment(sketch, "E959", {"start": v(14.8, 43.92) * mm, "end": v(14.86, 44.07) * mm});
            skLineSegment(sketch, "E960", {"start": v(14.86, 44.07) * mm, "end": v(14.91, 44.22) * mm});
            skLineSegment(sketch, "E961", {"start": v(14.91, 44.22) * mm, "end": v(14.96, 44.37) * mm});
            skLineSegment(sketch, "E962", {"start": v(14.96, 44.37) * mm, "end": v(15.02, 44.52) * mm});
            skLineSegment(sketch, "E963", {"start": v(15.02, 44.52) * mm, "end": v(15.07, 44.67) * mm});
            skLineSegment(sketch, "E964", {"start": v(15.07, 44.67) * mm, "end": v(15.12, 44.82) * mm});
            skLineSegment(sketch, "E965", {"start": v(15.12, 44.82) * mm, "end": v(15.17, 44.97) * mm});
            skLineSegment(sketch, "E966", {"start": v(15.17, 44.97) * mm, "end": v(15.23, 45.12) * mm});
            skLineSegment(sketch, "E967", {"start": v(15.23, 45.12) * mm, "end": v(15.28, 45.28) * mm});
            skLineSegment(sketch, "E968", {"start": v(15.28, 45.28) * mm, "end": v(15.3, 45.44) * mm});
            skLineSegment(sketch, "E969", {"start": v(15.3, 45.44) * mm, "end": v(15.29, 45.6) * mm});
            skLineSegment(sketch, "E970", {"start": v(15.29, 45.6) * mm, "end": v(15.23, 45.76) * mm});
            skLineSegment(sketch, "E971", {"start": v(15.23, 45.76) * mm, "end": v(15.13, 45.89) * mm});
            skLineSegment(sketch, "E972", {"start": v(15.13, 45.89) * mm, "end": v(15, 45.99) * mm});
            skLineSegment(sketch, "E973", {"start": v(15, 45.99) * mm, "end": v(14.85, 46.05) * mm});
            skLineSegment(sketch, "E974", {"start": v(14.85, 46.05) * mm, "end": v(14.7, 46.08) * mm});
            skLineSegment(sketch, "E975", {"start": v(14.7, 46.08) * mm, "end": v(14.53, 46.06) * mm});
            skLineSegment(sketch, "E976", {"start": v(14.53, 46.06) * mm, "end": v(14.38, 46) * mm});
            skLineSegment(sketch, "E977", {"start": v(14.38, 46) * mm, "end": v(14.24, 45.9) * mm});
            skLineSegment(sketch, "E978", {"start": v(14.24, 45.9) * mm, "end": v(14.14, 45.77) * mm});
            skLineSegment(sketch, "E979", {"start": v(14.14, 45.77) * mm, "end": v(14.08, 45.62) * mm});
            skLineSegment(sketch, "E980", {"start": v(14.08, 45.62) * mm, "end": v(14.03, 45.47) * mm});
            skLineSegment(sketch, "E981", {"start": v(14.03, 45.47) * mm, "end": v(13.98, 45.33) * mm});
            skLineSegment(sketch, "E982", {"start": v(13.98, 45.33) * mm, "end": v(13.94, 45.18) * mm});
            skLineSegment(sketch, "E983", {"start": v(13.94, 45.18) * mm, "end": v(13.89, 45.03) * mm});
            skLineSegment(sketch, "E984", {"start": v(13.89, 45.03) * mm, "end": v(13.84, 44.87) * mm});
            skLineSegment(sketch, "E985", {"start": v(13.84, 44.87) * mm, "end": v(13.79, 44.72) * mm});
            skLineSegment(sketch, "E986", {"start": v(13.79, 44.72) * mm, "end": v(13.74, 44.57) * mm});
            skLineSegment(sketch, "E987", {"start": v(13.74, 44.57) * mm, "end": v(13.69, 44.42) * mm});
            skLineSegment(sketch, "E988", {"start": v(13.69, 44.42) * mm, "end": v(13.64, 44.27) * mm});
            skLineSegment(sketch, "E989", {"start": v(13.64, 44.27) * mm, "end": v(13.6, 44.12) * mm});
            skLineSegment(sketch, "E990", {"start": v(13.6, 44.12) * mm, "end": v(13.54, 43.97) * mm});
            skLineSegment(sketch, "E991", {"start": v(13.54, 43.97) * mm, "end": v(13.5, 43.82) * mm});
            skLineSegment(sketch, "E992", {"start": v(13.5, 43.82) * mm, "end": v(13.46, 43.7) * mm});
            skLineSegment(sketch, "E993", {"start": v(13.46, 43.7) * mm, "end": v(13.3, 43.75) * mm});
            skLineSegment(sketch, "E994", {"start": v(13.3, 43.75) * mm, "end": v(13.16, 43.8) * mm});
            skLineSegment(sketch, "E995", {"start": v(13.16, 43.8) * mm, "end": v(13, 43.85) * mm});
            skLineSegment(sketch, "E996", {"start": v(13, 43.85) * mm, "end": v(12.86, 43.9) * mm});
            skLineSegment(sketch, "E997", {"start": v(12.86, 43.9) * mm, "end": v(12.7, 43.94) * mm});
            skLineSegment(sketch, "E998", {"start": v(12.7, 43.94) * mm, "end": v(12.56, 43.98) * mm});
            skLineSegment(sketch, "E999", {"start": v(12.56, 43.98) * mm, "end": v(12.4, 44.03) * mm});
            skLineSegment(sketch, "E1000", {"start": v(12.4, 44.03) * mm, "end": v(12.25, 44.07) * mm});
            skLineSegment(sketch, "E1001", {"start": v(12.25, 44.07) * mm, "end": v(12.1, 44.12) * mm});
            skLineSegment(sketch, "E1002", {"start": v(12.1, 44.12) * mm, "end": v(11.95, 44.17) * mm});
            skLineSegment(sketch, "E1003", {"start": v(11.95, 44.17) * mm, "end": v(11.8, 44.21) * mm});
            skLineSegment(sketch, "E1004", {"start": v(11.8, 44.21) * mm, "end": v(11.73, 44.23) * mm});
            skLineSegment(sketch, "E1005", {"start": v(11.73, 44.23) * mm, "end": v(11.77, 44.39) * mm});
            skLineSegment(sketch, "E1006", {"start": v(11.77, 44.39) * mm, "end": v(11.81, 44.54) * mm});
            skLineSegment(sketch, "E1007", {"start": v(11.81, 44.54) * mm, "end": v(11.86, 44.7) * mm});
            skLineSegment(sketch, "E1008", {"start": v(11.86, 44.7) * mm, "end": v(11.9, 44.84) * mm});
            skLineSegment(sketch, "E1009", {"start": v(11.9, 44.84) * mm, "end": v(11.94, 45) * mm});
            skLineSegment(sketch, "E1010", {"start": v(11.94, 45) * mm, "end": v(11.98, 45.15) * mm});
            skLineSegment(sketch, "E1011", {"start": v(11.98, 45.15) * mm, "end": v(12.03, 45.3) * mm});
            skLineSegment(sketch, "E1012", {"start": v(12.03, 45.3) * mm, "end": v(12.07, 45.45) * mm});
            skLineSegment(sketch, "E1013", {"start": v(12.07, 45.45) * mm, "end": v(12.11, 45.6) * mm});
            skLineSegment(sketch, "E1014", {"start": v(12.11, 45.6) * mm, "end": v(12.16, 45.76) * mm});
            skLineSegment(sketch, "E1015", {"start": v(12.16, 45.76) * mm, "end": v(12.2, 45.91) * mm});
            skLineSegment(sketch, "E1016", {"start": v(12.2, 45.91) * mm, "end": v(12.24, 46.07) * mm});
            skLineSegment(sketch, "E1017", {"start": v(12.24, 46.07) * mm, "end": v(12.29, 46.23) * mm});
            skLineSegment(sketch, "E1018", {"start": v(12.29, 46.23) * mm, "end": v(12.3, 46.4) * mm});
            skLineSegment(sketch, "E1019", {"start": v(12.3, 46.4) * mm, "end": v(12.27, 46.55) * mm});
            skLineSegment(sketch, "E1020", {"start": v(12.27, 46.55) * mm, "end": v(12.2, 46.7) * mm});
            skLineSegment(sketch, "E1021", {"start": v(12.2, 46.7) * mm, "end": v(12.1, 46.83) * mm});
            skLineSegment(sketch, "E1022", {"start": v(12.1, 46.83) * mm, "end": v(11.96, 46.92) * mm});
            skLineSegment(sketch, "E1023", {"start": v(11.96, 46.92) * mm, "end": v(11.8, 46.98) * mm});
            skLineSegment(sketch, "E1024", {"start": v(11.8, 46.98) * mm, "end": v(11.68, 46.99) * mm});
            skLineSegment(sketch, "E1025", {"start": v(11.68, 46.99) * mm, "end": v(11.51, 46.97) * mm});
            skLineSegment(sketch, "E1026", {"start": v(11.51, 46.97) * mm, "end": v(11.36, 46.9) * mm});
            skLineSegment(sketch, "E1027", {"start": v(11.36, 46.9) * mm, "end": v(11.23, 46.8) * mm});
            skLineSegment(sketch, "E1028", {"start": v(11.23, 46.8) * mm, "end": v(11.13, 46.67) * mm});
            skLineSegment(sketch, "E1029", {"start": v(11.13, 46.67) * mm, "end": v(11.07, 46.52) * mm});
            skLineSegment(sketch, "E1030", {"start": v(11.07, 46.52) * mm, "end": v(11.03, 46.37) * mm});
            skLineSegment(sketch, "E1031", {"start": v(11.03, 46.37) * mm, "end": v(11, 46.22) * mm});
            skLineSegment(sketch, "E1032", {"start": v(11, 46.22) * mm, "end": v(10.95, 46.06) * mm});
            skLineSegment(sketch, "E1033", {"start": v(10.95, 46.06) * mm, "end": v(10.92, 45.9) * mm});
            skLineSegment(sketch, "E1034", {"start": v(10.92, 45.9) * mm, "end": v(10.88, 45.76) * mm});
            skLineSegment(sketch, "E1035", {"start": v(10.88, 45.76) * mm, "end": v(10.84, 45.6) * mm});
            skLineSegment(sketch, "E1036", {"start": v(10.84, 45.6) * mm, "end": v(10.8, 45.45) * mm});
            skLineSegment(sketch, "E1037", {"start": v(10.8, 45.45) * mm, "end": v(10.76, 45.3) * mm});
            skLineSegment(sketch, "E1038", {"start": v(10.76, 45.3) * mm, "end": v(10.72, 45.14) * mm});
            skLineSegment(sketch, "E1039", {"start": v(10.72, 45.14) * mm, "end": v(10.68, 44.98) * mm});
            skLineSegment(sketch, "E1040", {"start": v(10.68, 44.98) * mm, "end": v(10.64, 44.83) * mm});
            skLineSegment(sketch, "E1041", {"start": v(10.64, 44.83) * mm, "end": v(10.6, 44.68) * mm});
            skLineSegment(sketch, "E1042", {"start": v(10.6, 44.68) * mm, "end": v(10.57, 44.54) * mm});
            skLineSegment(sketch, "E1043", {"start": v(10.57, 44.54) * mm, "end": v(10.42, 44.58) * mm});
            skLineSegment(sketch, "E1044", {"start": v(10.42, 44.58) * mm, "end": v(10.26, 44.62) * mm});
            skLineSegment(sketch, "E1045", {"start": v(10.26, 44.62) * mm, "end": v(10.11, 44.65) * mm});
            skLineSegment(sketch, "E1046", {"start": v(10.11, 44.65) * mm, "end": v(9.96, 44.69) * mm});
            skLineSegment(sketch, "E1047", {"start": v(9.96, 44.69) * mm, "end": v(9.8, 44.72) * mm});
            skLineSegment(sketch, "E1048", {"start": v(9.8, 44.72) * mm, "end": v(9.65, 44.76) * mm});
            skLineSegment(sketch, "E1049", {"start": v(9.65, 44.76) * mm, "end": v(9.5, 44.8) * mm});
            skLineSegment(sketch, "E1050", {"start": v(9.5, 44.8) * mm, "end": v(9.34, 44.83) * mm});
            skLineSegment(sketch, "E1051", {"start": v(9.34, 44.83) * mm, "end": v(9.2, 44.87) * mm});
            skLineSegment(sketch, "E1052", {"start": v(9.2, 44.87) * mm, "end": v(9.04, 44.9) * mm});
            skLineSegment(sketch, "E1053", {"start": v(9.04, 44.9) * mm, "end": v(8.88, 44.94) * mm});
            skLineSegment(sketch, "E1054", {"start": v(8.88, 44.94) * mm, "end": v(8.8, 44.96) * mm});
            skLineSegment(sketch, "E1055", {"start": v(8.8, 44.96) * mm, "end": v(8.84, 45.1) * mm});
            skLineSegment(sketch, "E1056", {"start": v(8.84, 45.1) * mm, "end": v(8.87, 45.26) * mm});
            skLineSegment(sketch, "E1057", {"start": v(8.87, 45.26) * mm, "end": v(8.9, 45.42) * mm});
            skLineSegment(sketch, "E1058", {"start": v(8.9, 45.42) * mm, "end": v(8.94, 45.57) * mm});
            skLineSegment(sketch, "E1059", {"start": v(8.94, 45.57) * mm, "end": v(8.97, 45.73) * mm});
            skLineSegment(sketch, "E1060", {"start": v(8.97, 45.73) * mm, "end": v(9, 45.89) * mm});
            skLineSegment(sketch, "E1061", {"start": v(9, 45.89) * mm, "end": v(9.04, 46.04) * mm});
            skLineSegment(sketch, "E1062", {"start": v(9.04, 46.04) * mm, "end": v(9.07, 46.2) * mm});
            skLineSegment(sketch, "E1063", {"start": v(9.07, 46.2) * mm, "end": v(9.1, 46.35) * mm});
            skLineSegment(sketch, "E1064", {"start": v(9.1, 46.35) * mm, "end": v(9.14, 46.5) * mm});
            skLineSegment(sketch, "E1065", {"start": v(9.14, 46.5) * mm, "end": v(9.17, 46.66) * mm});
            skLineSegment(sketch, "E1066", {"start": v(9.17, 46.66) * mm, "end": v(9.2, 46.82) * mm});
            skLineSegment(sketch, "E1067", {"start": v(9.2, 46.82) * mm, "end": v(9.24, 46.98) * mm});
            skLineSegment(sketch, "E1068", {"start": v(9.24, 46.98) * mm, "end": v(9.24, 47.15) * mm});
            skLineSegment(sketch, "E1069", {"start": v(9.24, 47.15) * mm, "end": v(9.2, 47.3) * mm});
            skLineSegment(sketch, "E1070", {"start": v(9.2, 47.3) * mm, "end": v(9.12, 47.45) * mm});
            skLineSegment(sketch, "E1071", {"start": v(9.12, 47.45) * mm, "end": v(9, 47.57) * mm});
            skLineSegment(sketch, "E1072", {"start": v(9, 47.57) * mm, "end": v(8.87, 47.65) * mm});
            skLineSegment(sketch, "E1073", {"start": v(8.87, 47.65) * mm, "end": v(8.7, 47.7) * mm});
            skLineSegment(sketch, "E1074", {"start": v(8.7, 47.7) * mm, "end": v(8.6, 47.7) * mm});
            skLineSegment(sketch, "E1075", {"start": v(8.6, 47.7) * mm, "end": v(8.45, 47.68) * mm});
            skLineSegment(sketch, "E1076", {"start": v(8.45, 47.68) * mm, "end": v(8.3, 47.61) * mm});
            skLineSegment(sketch, "E1077", {"start": v(8.3, 47.61) * mm, "end": v(8.17, 47.51) * mm});
            skLineSegment(sketch, "E1078", {"start": v(8.17, 47.51) * mm, "end": v(8.07, 47.38) * mm});
            skLineSegment(sketch, "E1079", {"start": v(8.07, 47.38) * mm, "end": v(8.01, 47.23) * mm});
            skLineSegment(sketch, "E1080", {"start": v(8.01, 47.23) * mm, "end": v(7.98, 47.06) * mm});
            skLineSegment(sketch, "E1081", {"start": v(7.98, 47.06) * mm, "end": v(7.95, 46.9) * mm});
            skLineSegment(sketch, "E1082", {"start": v(7.95, 46.9) * mm, "end": v(7.92, 46.75) * mm});
            skLineSegment(sketch, "E1083", {"start": v(7.92, 46.75) * mm, "end": v(7.9, 46.6) * mm});
            skLineSegment(sketch, "E1084", {"start": v(7.9, 46.6) * mm, "end": v(7.86, 46.44) * mm});
            skLineSegment(sketch, "E1085", {"start": v(7.86, 46.44) * mm, "end": v(7.84, 46.28) * mm});
            skLineSegment(sketch, "E1086", {"start": v(7.84, 46.28) * mm, "end": v(7.8, 46.13) * mm});
            skLineSegment(sketch, "E1087", {"start": v(7.8, 46.13) * mm, "end": v(7.78, 45.97) * mm});
            skLineSegment(sketch, "E1088", {"start": v(7.78, 45.97) * mm, "end": v(7.75, 45.82) * mm});
            skLineSegment(sketch, "E1089", {"start": v(7.75, 45.82) * mm, "end": v(7.72, 45.66) * mm});
            skLineSegment(sketch, "E1090", {"start": v(7.72, 45.66) * mm, "end": v(7.7, 45.5) * mm});
            skLineSegment(sketch, "E1091", {"start": v(7.7, 45.5) * mm, "end": v(7.66, 45.35) * mm});
            skLineSegment(sketch, "E1092", {"start": v(7.66, 45.35) * mm, "end": v(7.63, 45.19) * mm});
            skLineSegment(sketch, "E1093", {"start": v(7.63, 45.19) * mm, "end": v(7.48, 45.21) * mm});
            skLineSegment(sketch, "E1094", {"start": v(7.48, 45.21) * mm, "end": v(7.32, 45.24) * mm});
            skLineSegment(sketch, "E1095", {"start": v(7.32, 45.24) * mm, "end": v(7.17, 45.27) * mm});
            skLineSegment(sketch, "E1096", {"start": v(7.17, 45.27) * mm, "end": v(7.01, 45.3) * mm});
            skLineSegment(sketch, "E1097", {"start": v(7.01, 45.3) * mm, "end": v(6.86, 45.32) * mm});
            skLineSegment(sketch, "E1098", {"start": v(6.86, 45.32) * mm, "end": v(6.7, 45.34) * mm});
            skLineSegment(sketch, "E1099", {"start": v(6.7, 45.34) * mm, "end": v(6.55, 45.37) * mm});
            skLineSegment(sketch, "E1100", {"start": v(6.55, 45.37) * mm, "end": v(6.4, 45.4) * mm});
            skLineSegment(sketch, "E1101", {"start": v(6.4, 45.4) * mm, "end": v(6.24, 45.42) * mm});
            skLineSegment(sketch, "E1102", {"start": v(6.24, 45.42) * mm, "end": v(6.08, 45.44) * mm});
            skLineSegment(sketch, "E1103", {"start": v(6.08, 45.44) * mm, "end": v(5.93, 45.47) * mm});
            skLineSegment(sketch, "E1104", {"start": v(5.93, 45.47) * mm, "end": v(5.85, 45.48) * mm});
            skLineSegment(sketch, "E1105", {"start": v(5.85, 45.48) * mm, "end": v(5.87, 45.64) * mm});
            skLineSegment(sketch, "E1106", {"start": v(5.87, 45.64) * mm, "end": v(5.9, 45.8) * mm});
            skLineSegment(sketch, "E1107", {"start": v(5.9, 45.8) * mm, "end": v(5.91, 45.95) * mm});
            skLineSegment(sketch, "E1108", {"start": v(5.91, 45.95) * mm, "end": v(5.94, 46.11) * mm});
            skLineSegment(sketch, "E1109", {"start": v(5.94, 46.11) * mm, "end": v(5.96, 46.27) * mm});
            skLineSegment(sketch, "E1110", {"start": v(5.96, 46.27) * mm, "end": v(5.98, 46.43) * mm});
            skLineSegment(sketch, "E1111", {"start": v(5.98, 46.43) * mm, "end": v(6, 46.58) * mm});
            skLineSegment(sketch, "E1112", {"start": v(6, 46.58) * mm, "end": v(6.03, 46.74) * mm});
            skLineSegment(sketch, "E1113", {"start": v(6.03, 46.74) * mm, "end": v(6.05, 46.9) * mm});
            skLineSegment(sketch, "E1114", {"start": v(6.05, 46.9) * mm, "end": v(6.07, 47.05) * mm});
            skLineSegment(sketch, "E1115", {"start": v(6.07, 47.05) * mm, "end": v(6.1, 47.2) * mm});
            skLineSegment(sketch, "E1116", {"start": v(6.1, 47.2) * mm, "end": v(6.12, 47.37) * mm});
            skLineSegment(sketch, "E1117", {"start": v(6.12, 47.37) * mm, "end": v(6.14, 47.54) * mm});
            skLineSegment(sketch, "E1118", {"start": v(6.14, 47.54) * mm, "end": v(6.13, 47.7) * mm});
            skLineSegment(sketch, "E1119", {"start": v(6.13, 47.7) * mm, "end": v(6.08, 47.86) * mm});
            skLineSegment(sketch, "E1120", {"start": v(6.08, 47.86) * mm, "end": v(6, 48) * mm});
            skLineSegment(sketch, "E1121", {"start": v(6, 48) * mm, "end": v(5.87, 48.1) * mm});
            skLineSegment(sketch, "E1122", {"start": v(5.87, 48.1) * mm, "end": v(5.73, 48.18) * mm});
            skLineSegment(sketch, "E1123", {"start": v(5.73, 48.18) * mm, "end": v(5.57, 48.21) * mm});
            skLineSegment(sketch, "E1124", {"start": v(5.57, 48.21) * mm, "end": v(5.54, 48.21) * mm});
            skLineSegment(sketch, "E1125", {"start": v(5.54, 48.21) * mm, "end": v(5.37, 48.2) * mm});
            skLineSegment(sketch, "E1126", {"start": v(5.37, 48.2) * mm, "end": v(5.22, 48.14) * mm});
            skLineSegment(sketch, "E1127", {"start": v(5.22, 48.14) * mm, "end": v(5.09, 48.04) * mm});
            skLineSegment(sketch, "E1128", {"start": v(5.09, 48.04) * mm, "end": v(4.98, 47.91) * mm});
            skLineSegment(sketch, "E1129", {"start": v(4.98, 47.91) * mm, "end": v(4.92, 47.76) * mm});
            skLineSegment(sketch, "E1130", {"start": v(4.92, 47.76) * mm, "end": v(4.9, 47.6) * mm});
            skLineSegment(sketch, "E1131", {"start": v(4.9, 47.6) * mm, "end": v(4.87, 47.44) * mm});
            skLineSegment(sketch, "E1132", {"start": v(4.87, 47.44) * mm, "end": v(4.85, 47.29) * mm});
            skLineSegment(sketch, "E1133", {"start": v(4.85, 47.29) * mm, "end": v(4.83, 47.13) * mm});
            skLineSegment(sketch, "E1134", {"start": v(4.83, 47.13) * mm, "end": v(4.82, 46.97) * mm});
            skLineSegment(sketch, "E1135", {"start": v(4.82, 46.97) * mm, "end": v(4.8, 46.81) * mm});
            skLineSegment(sketch, "E1136", {"start": v(4.8, 46.81) * mm, "end": v(4.78, 46.65) * mm});
            skLineSegment(sketch, "E1137", {"start": v(4.78, 46.65) * mm, "end": v(4.76, 46.5) * mm});
            skLineSegment(sketch, "E1138", {"start": v(4.76, 46.5) * mm, "end": v(4.74, 46.34) * mm});
            skLineSegment(sketch, "E1139", {"start": v(4.74, 46.34) * mm, "end": v(4.72, 46.18) * mm});
            skLineSegment(sketch, "E1140", {"start": v(4.72, 46.18) * mm, "end": v(4.7, 46.02) * mm});
            skLineSegment(sketch, "E1141", {"start": v(4.7, 46.02) * mm, "end": v(4.69, 45.87) * mm});
            skLineSegment(sketch, "E1142", {"start": v(4.69, 45.87) * mm, "end": v(4.67, 45.7) * mm});
            skLineSegment(sketch, "E1143", {"start": v(4.67, 45.7) * mm, "end": v(4.66, 45.64) * mm});
            skLineSegment(sketch, "E1144", {"start": v(4.66, 45.64) * mm, "end": v(4.5, 45.66) * mm});
            skLineSegment(sketch, "E1145", {"start": v(4.5, 45.66) * mm, "end": v(4.35, 45.67) * mm});
            skLineSegment(sketch, "E1146", {"start": v(4.35, 45.67) * mm, "end": v(4.19, 45.69) * mm});
            skLineSegment(sketch, "E1147", {"start": v(4.19, 45.69) * mm, "end": v(4.03, 45.7) * mm});
            skLineSegment(sketch, "E1148", {"start": v(4.03, 45.7) * mm, "end": v(3.88, 45.72) * mm});
            skLineSegment(sketch, "E1149", {"start": v(3.88, 45.72) * mm, "end": v(3.72, 45.73) * mm});
            skLineSegment(sketch, "E1150", {"start": v(3.72, 45.73) * mm, "end": v(3.56, 45.75) * mm});
            skLineSegment(sketch, "E1151", {"start": v(3.56, 45.75) * mm, "end": v(3.4, 45.76) * mm});
            skLineSegment(sketch, "E1152", {"start": v(3.4, 45.76) * mm, "end": v(3.25, 45.78) * mm});
            skLineSegment(sketch, "E1153", {"start": v(3.25, 45.78) * mm, "end": v(3.1, 45.8) * mm});
            skLineSegment(sketch, "E1154", {"start": v(3.1, 45.8) * mm, "end": v(2.94, 45.8) * mm});
            skLineSegment(sketch, "E1155", {"start": v(2.94, 45.8) * mm, "end": v(2.86, 45.82) * mm});
            skLineSegment(sketch, "E1156", {"start": v(2.86, 45.82) * mm, "end": v(2.87, 45.97) * mm});
            skLineSegment(sketch, "E1157", {"start": v(2.87, 45.97) * mm, "end": v(2.88, 46.13) * mm});
            skLineSegment(sketch, "E1158", {"start": v(2.88, 46.13) * mm, "end": v(2.9, 46.3) * mm});
            skLineSegment(sketch, "E1159", {"start": v(2.9, 46.3) * mm, "end": v(2.9, 46.45) * mm});
            skLineSegment(sketch, "E1160", {"start": v(2.9, 46.45) * mm, "end": v(2.92, 46.6) * mm});
            skLineSegment(sketch, "E1161", {"start": v(2.92, 46.6) * mm, "end": v(2.93, 46.77) * mm});
            skLineSegment(sketch, "E1162", {"start": v(2.93, 46.77) * mm, "end": v(2.94, 46.92) * mm});
            skLineSegment(sketch, "E1163", {"start": v(2.94, 46.92) * mm, "end": v(2.96, 47.08) * mm});
            skLineSegment(sketch, "E1164", {"start": v(2.96, 47.08) * mm, "end": v(2.97, 47.24) * mm});
            skLineSegment(sketch, "E1165", {"start": v(2.97, 47.24) * mm, "end": v(2.98, 47.4) * mm});
            skLineSegment(sketch, "E1166", {"start": v(2.98, 47.4) * mm, "end": v(3, 47.56) * mm});
            skLineSegment(sketch, "E1167", {"start": v(3, 47.56) * mm, "end": v(3, 47.72) * mm});
            skLineSegment(sketch, "E1168", {"start": v(3, 47.72) * mm, "end": v(3.02, 47.88) * mm});
            skLineSegment(sketch, "E1169", {"start": v(3.02, 47.88) * mm, "end": v(3, 48.05) * mm});
            skLineSegment(sketch, "E1170", {"start": v(3, 48.05) * mm, "end": v(2.94, 48.2) * mm});
            skLineSegment(sketch, "E1171", {"start": v(2.94, 48.2) * mm, "end": v(2.84, 48.33) * mm});
            skLineSegment(sketch, "E1172", {"start": v(2.84, 48.33) * mm, "end": v(2.71, 48.43) * mm});
            skLineSegment(sketch, "E1173", {"start": v(2.71, 48.43) * mm, "end": v(2.56, 48.5) * mm});
            skLineSegment(sketch, "E1174", {"start": v(2.56, 48.5) * mm, "end": v(2.4, 48.52) * mm});
            skLineSegment(sketch, "E1175", {"start": v(2.4, 48.52) * mm, "end": v(2.24, 48.5) * mm});
            skLineSegment(sketch, "E1176", {"start": v(2.24, 48.5) * mm, "end": v(2.09, 48.44) * mm});
            skLineSegment(sketch, "E1177", {"start": v(2.09, 48.44) * mm, "end": v(1.96, 48.34) * mm});
            skLineSegment(sketch, "E1178", {"start": v(1.96, 48.34) * mm, "end": v(1.85, 48.21) * mm});
            skLineSegment(sketch, "E1179", {"start": v(1.85, 48.21) * mm, "end": v(1.8, 48.06) * mm});
            skLineSegment(sketch, "E1180", {"start": v(1.8, 48.06) * mm, "end": v(1.77, 47.9) * mm});
            skLineSegment(sketch, "E1181", {"start": v(1.77, 47.9) * mm, "end": v(1.76, 47.75) * mm});
            skLineSegment(sketch, "E1182", {"start": v(1.76, 47.75) * mm, "end": v(1.75, 47.6) * mm});
            skLineSegment(sketch, "E1183", {"start": v(1.75, 47.6) * mm, "end": v(1.74, 47.44) * mm});
            skLineSegment(sketch, "E1184", {"start": v(1.74, 47.44) * mm, "end": v(1.73, 47.28) * mm});
            skLineSegment(sketch, "E1185", {"start": v(1.73, 47.28) * mm, "end": v(1.73, 47.12) * mm});
            skLineSegment(sketch, "E1186", {"start": v(1.73, 47.12) * mm, "end": v(1.72, 46.96) * mm});
            skLineSegment(sketch, "E1187", {"start": v(1.72, 46.96) * mm, "end": v(1.7, 46.8) * mm});
            skLineSegment(sketch, "E1188", {"start": v(1.7, 46.8) * mm, "end": v(1.7, 46.64) * mm});
            skLineSegment(sketch, "E1189", {"start": v(1.7, 46.64) * mm, "end": v(1.7, 46.49) * mm});
            skLineSegment(sketch, "E1190", {"start": v(1.7, 46.49) * mm, "end": v(1.68, 46.33) * mm});
            skLineSegment(sketch, "E1191", {"start": v(1.68, 46.33) * mm, "end": v(1.68, 46.17) * mm});
            skLineSegment(sketch, "E1192", {"start": v(1.68, 46.17) * mm, "end": v(1.67, 46.01) * mm});
            skLineSegment(sketch, "E1193", {"start": v(1.67, 46.01) * mm, "end": v(1.66, 45.9) * mm});
            skLineSegment(sketch, "E1194", {"start": v(1.66, 45.9) * mm, "end": v(1.5, 45.9) * mm});
            skLineSegment(sketch, "E1195", {"start": v(1.5, 45.9) * mm, "end": v(1.35, 45.9) * mm});
            skLineSegment(sketch, "E1196", {"start": v(1.35, 45.9) * mm, "end": v(1.2, 45.91) * mm});
            skLineSegment(sketch, "E1197", {"start": v(1.2, 45.91) * mm, "end": v(1.03, 45.92) * mm});
            skLineSegment(sketch, "E1198", {"start": v(1.03, 45.92) * mm, "end": v(0.88, 45.92) * mm});
            skLineSegment(sketch, "E1199", {"start": v(0.88, 45.92) * mm, "end": v(0.72, 45.93) * mm});
            skLineSegment(sketch, "E1200", {"start": v(0.72, 45.93) * mm, "end": v(0.56, 45.93) * mm});
            skLineSegment(sketch, "E1201", {"start": v(0.56, 45.93) * mm, "end": v(0.4, 45.94) * mm});
            skLineSegment(sketch, "E1202", {"start": v(0.4, 45.94) * mm, "end": v(0.25, 45.94) * mm});
            skLineSegment(sketch, "E1203", {"start": v(0.25, 45.94) * mm, "end": v(0.09, 45.95) * mm});
            skLineSegment(sketch, "E1204", {"start": v(0.09, 45.95) * mm, "end": v(-0.07, 45.95) * mm});
            skLineSegment(sketch, "E1205", {"start": v(-0.07, 45.95) * mm, "end": v(-0.15, 45.95) * mm});
            skLineSegment(sketch, "E1206", {"start": v(-0.15, 45.95) * mm, "end": v(-0.15, 46.11) * mm});
            skLineSegment(sketch, "E1207", {"start": v(-0.15, 46.11) * mm, "end": v(-0.14, 46.27) * mm});
            skLineSegment(sketch, "E1208", {"start": v(-0.14, 46.27) * mm, "end": v(-0.14, 46.43) * mm});
            skLineSegment(sketch, "E1209", {"start": v(-0.14, 46.43) * mm, "end": v(-0.14, 46.59) * mm});
            skLineSegment(sketch, "E1210", {"start": v(-0.14, 46.59) * mm, "end": v(-0.14, 46.75) * mm});
            skLineSegment(sketch, "E1211", {"start": v(-0.14, 46.75) * mm, "end": v(-0.14, 46.9) * mm});
            skLineSegment(sketch, "E1212", {"start": v(-0.14, 46.9) * mm, "end": v(-0.13, 47.06) * mm});
            skLineSegment(sketch, "E1213", {"start": v(-0.13, 47.06) * mm, "end": v(-0.13, 47.22) * mm});
            skLineSegment(sketch, "E1214", {"start": v(-0.13, 47.22) * mm, "end": v(-0.13, 47.38) * mm});
            skLineSegment(sketch, "E1215", {"start": v(-0.13, 47.38) * mm, "end": v(-0.13, 47.54) * mm});
            skLineSegment(sketch, "E1216", {"start": v(-0.13, 47.54) * mm, "end": v(-0.12, 47.7) * mm});
            skLineSegment(sketch, "E1217", {"start": v(-0.12, 47.7) * mm, "end": v(-0.12, 47.86) * mm});
            skLineSegment(sketch, "E1218", {"start": v(-0.12, 47.86) * mm, "end": v(-0.12, 48.03) * mm});
            skLineSegment(sketch, "E1219", {"start": v(-0.12, 48.03) * mm, "end": v(-0.15, 48.19) * mm});
            skLineSegment(sketch, "E1220", {"start": v(-0.15, 48.19) * mm, "end": v(-0.22, 48.34) * mm});
            skLineSegment(sketch, "E1221", {"start": v(-0.22, 48.34) * mm, "end": v(-0.33, 48.46) * mm});
            skLineSegment(sketch, "E1222", {"start": v(-0.33, 48.46) * mm, "end": v(-0.46, 48.56) * mm});
            skLineSegment(sketch, "E1223", {"start": v(-0.46, 48.56) * mm, "end": v(-0.62, 48.61) * mm});
            skLineSegment(sketch, "E1224", {"start": v(-0.62, 48.61) * mm, "end": v(-0.75, 48.62) * mm});
            skLineSegment(sketch, "E1225", {"start": v(-0.75, 48.62) * mm, "end": v(-0.9, 48.6) * mm});
            skLineSegment(sketch, "E1226", {"start": v(-0.9, 48.6) * mm, "end": v(-1.06, 48.54) * mm});
            skLineSegment(sketch, "E1227", {"start": v(-1.06, 48.54) * mm, "end": v(-1.19, 48.44) * mm});
            skLineSegment(sketch, "E1228", {"start": v(-1.19, 48.44) * mm, "end": v(-1.29, 48.3) * mm});
            skLineSegment(sketch, "E1229", {"start": v(-1.29, 48.3) * mm, "end": v(-1.35, 48.16) * mm});
            skLineSegment(sketch, "E1230", {"start": v(-1.35, 48.16) * mm, "end": v(-1.37, 48) * mm});
            skLineSegment(sketch, "E1231", {"start": v(-1.37, 48) * mm, "end": v(-1.37, 47.84) * mm});
            skLineSegment(sketch, "E1232", {"start": v(-1.37, 47.84) * mm, "end": v(-1.37, 47.68) * mm});
            skLineSegment(sketch, "E1233", {"start": v(-1.37, 47.68) * mm, "end": v(-1.37, 47.52) * mm});
            skLineSegment(sketch, "E1234", {"start": v(-1.37, 47.52) * mm, "end": v(-1.36, 47.36) * mm});
            skLineSegment(sketch, "E1235", {"start": v(-1.36, 47.36) * mm, "end": v(-1.36, 47.2) * mm});
            skLineSegment(sketch, "E1236", {"start": v(-1.36, 47.2) * mm, "end": v(-1.36, 47.04) * mm});
            skLineSegment(sketch, "E1237", {"start": v(-1.36, 47.04) * mm, "end": v(-1.36, 46.89) * mm});
            skLineSegment(sketch, "E1238", {"start": v(-1.36, 46.89) * mm, "end": v(-1.36, 46.73) * mm});
            skLineSegment(sketch, "E1239", {"start": v(-1.36, 46.73) * mm, "end": v(-1.35, 46.57) * mm});
            skLineSegment(sketch, "E1240", {"start": v(-1.35, 46.57) * mm, "end": v(-1.35, 46.4) * mm});
            skLineSegment(sketch, "E1241", {"start": v(-1.35, 46.4) * mm, "end": v(-1.35, 46.25) * mm});
            skLineSegment(sketch, "E1242", {"start": v(-1.35, 46.25) * mm, "end": v(-1.35, 46.1) * mm});
            skLineSegment(sketch, "E1243", {"start": v(-1.35, 46.1) * mm, "end": v(-1.34, 45.95) * mm});
            skLineSegment(sketch, "E1244", {"start": v(-1.34, 45.95) * mm, "end": v(-1.5, 45.95) * mm});
            skLineSegment(sketch, "E1245", {"start": v(-1.5, 45.95) * mm, "end": v(-1.66, 45.94) * mm});
            skLineSegment(sketch, "E1246", {"start": v(-1.66, 45.94) * mm, "end": v(-1.82, 45.94) * mm});
            skLineSegment(sketch, "E1247", {"start": v(-1.82, 45.94) * mm, "end": v(-1.97, 45.93) * mm});
            skLineSegment(sketch, "E1248", {"start": v(-1.97, 45.93) * mm, "end": v(-2.13, 45.93) * mm});
            skLineSegment(sketch, "E1249", {"start": v(-2.13, 45.93) * mm, "end": v(-2.29, 45.92) * mm});
            skLineSegment(sketch, "E1250", {"start": v(-2.29, 45.92) * mm, "end": v(-2.45, 45.92) * mm});
            skLineSegment(sketch, "E1251", {"start": v(-2.45, 45.92) * mm, "end": v(-2.6, 45.91) * mm});
            skLineSegment(sketch, "E1252", {"start": v(-2.6, 45.91) * mm, "end": v(-2.76, 45.9) * mm});
            skLineSegment(sketch, "E1253", {"start": v(-2.76, 45.9) * mm, "end": v(-2.92, 45.9) * mm});
            skLineSegment(sketch, "E1254", {"start": v(-2.92, 45.9) * mm, "end": v(-3.07, 45.9) * mm});
            skLineSegment(sketch, "E1255", {"start": v(-3.07, 45.9) * mm, "end": v(-3.15, 45.9) * mm});
            skLineSegment(sketch, "E1256", {"start": v(-3.15, 45.9) * mm, "end": v(-3.16, 46.05) * mm});
            skLineSegment(sketch, "E1257", {"start": v(-3.16, 46.05) * mm, "end": v(-3.17, 46.2) * mm});
            skLineSegment(sketch, "E1258", {"start": v(-3.17, 46.2) * mm, "end": v(-3.18, 46.37) * mm});
            skLineSegment(sketch, "E1259", {"start": v(-3.18, 46.37) * mm, "end": v(-3.19, 46.53) * mm});
            skLineSegment(sketch, "E1260", {"start": v(-3.19, 46.53) * mm, "end": v(-3.2, 46.69) * mm});
            skLineSegment(sketch, "E1261", {"start": v(-3.2, 46.69) * mm, "end": v(-3.2, 46.85) * mm});
            skLineSegment(sketch, "E1262", {"start": v(-3.2, 46.85) * mm, "end": v(-3.21, 47) * mm});
            skLineSegment(sketch, "E1263", {"start": v(-3.21, 47) * mm, "end": v(-3.22, 47.16) * mm});
            skLineSegment(sketch, "E1264", {"start": v(-3.22, 47.16) * mm, "end": v(-3.23, 47.32) * mm});
            skLineSegment(sketch, "E1265", {"start": v(-3.23, 47.32) * mm, "end": v(-3.24, 47.48) * mm});
            skLineSegment(sketch, "E1266", {"start": v(-3.24, 47.48) * mm, "end": v(-3.25, 47.64) * mm});
            skLineSegment(sketch, "E1267", {"start": v(-3.25, 47.64) * mm, "end": v(-3.25, 47.8) * mm});
            skLineSegment(sketch, "E1268", {"start": v(-3.25, 47.8) * mm, "end": v(-3.26, 47.97) * mm});
            skLineSegment(sketch, "E1269", {"start": v(-3.26, 47.97) * mm, "end": v(-3.3, 48.13) * mm});
            skLineSegment(sketch, "E1270", {"start": v(-3.3, 48.13) * mm, "end": v(-3.38, 48.27) * mm});
            skLineSegment(sketch, "E1271", {"start": v(-3.38, 48.27) * mm, "end": v(-3.5, 48.39) * mm});
            skLineSegment(sketch, "E1272", {"start": v(-3.5, 48.39) * mm, "end": v(-3.64, 48.47) * mm});
            skLineSegment(sketch, "E1273", {"start": v(-3.64, 48.47) * mm, "end": v(-3.8, 48.52) * mm});
            skLineSegment(sketch, "E1274", {"start": v(-3.8, 48.52) * mm, "end": v(-3.9, 48.52) * mm});
            skLineSegment(sketch, "E1275", {"start": v(-3.9, 48.52) * mm, "end": v(-4.06, 48.5) * mm});
            skLineSegment(sketch, "E1276", {"start": v(-4.06, 48.5) * mm, "end": v(-4.2, 48.43) * mm});
            skLineSegment(sketch, "E1277", {"start": v(-4.2, 48.43) * mm, "end": v(-4.33, 48.33) * mm});
            skLineSegment(sketch, "E1278", {"start": v(-4.33, 48.33) * mm, "end": v(-4.43, 48.2) * mm});
            skLineSegment(sketch, "E1279", {"start": v(-4.43, 48.2) * mm, "end": v(-4.5, 48.05) * mm});
            skLineSegment(sketch, "E1280", {"start": v(-4.5, 48.05) * mm, "end": v(-4.51, 47.88) * mm});
            skLineSegment(sketch, "E1281", {"start": v(-4.51, 47.88) * mm, "end": v(-4.5, 47.72) * mm});
            skLineSegment(sketch, "E1282", {"start": v(-4.5, 47.72) * mm, "end": v(-4.49, 47.56) * mm});
            skLineSegment(sketch, "E1283", {"start": v(-4.49, 47.56) * mm, "end": v(-4.47, 47.4) * mm});
            skLineSegment(sketch, "E1284", {"start": v(-4.47, 47.4) * mm, "end": v(-4.46, 47.24) * mm});
            skLineSegment(sketch, "E1285", {"start": v(-4.46, 47.24) * mm, "end": v(-4.45, 47.08) * mm});
            skLineSegment(sketch, "E1286", {"start": v(-4.45, 47.08) * mm, "end": v(-4.44, 46.93) * mm});
            skLineSegment(sketch, "E1287", {"start": v(-4.44, 46.93) * mm, "end": v(-4.42, 46.77) * mm});
            skLineSegment(sketch, "E1288", {"start": v(-4.42, 46.77) * mm, "end": v(-4.41, 46.61) * mm});
            skLineSegment(sketch, "E1289", {"start": v(-4.41, 46.61) * mm, "end": v(-4.4, 46.45) * mm});
            skLineSegment(sketch, "E1290", {"start": v(-4.4, 46.45) * mm, "end": v(-4.39, 46.3) * mm});
            skLineSegment(sketch, "E1291", {"start": v(-4.39, 46.3) * mm, "end": v(-4.37, 46.14) * mm});
            skLineSegment(sketch, "E1292", {"start": v(-4.37, 46.14) * mm, "end": v(-4.36, 45.98) * mm});
            skLineSegment(sketch, "E1293", {"start": v(-4.36, 45.98) * mm, "end": v(-4.35, 45.82) * mm});
            skLineSegment(sketch, "E1294", {"start": v(-4.35, 45.82) * mm, "end": v(-4.5, 45.8) * mm});
            skLineSegment(sketch, "E1295", {"start": v(-4.5, 45.8) * mm, "end": v(-4.66, 45.79) * mm});
            skLineSegment(sketch, "E1296", {"start": v(-4.66, 45.79) * mm, "end": v(-4.82, 45.77) * mm});
            skLineSegment(sketch, "E1297", {"start": v(-4.82, 45.77) * mm, "end": v(-4.98, 45.76) * mm});
            skLineSegment(sketch, "E1298", {"start": v(-4.98, 45.76) * mm, "end": v(-5.13, 45.74) * mm});
            skLineSegment(sketch, "E1299", {"start": v(-5.13, 45.74) * mm, "end": v(-5.29, 45.72) * mm});
            skLineSegment(sketch, "E1300", {"start": v(-5.29, 45.72) * mm, "end": v(-5.44, 45.7) * mm});
            skLineSegment(sketch, "E1301", {"start": v(-5.44, 45.7) * mm, "end": v(-5.6, 45.7) * mm});
            skLineSegment(sketch, "E1302", {"start": v(-5.6, 45.7) * mm, "end": v(-5.76, 45.68) * mm});
            skLineSegment(sketch, "E1303", {"start": v(-5.76, 45.68) * mm, "end": v(-5.91, 45.66) * mm});
            skLineSegment(sketch, "E1304", {"start": v(-5.91, 45.66) * mm, "end": v(-6.07, 45.65) * mm});
            skLineSegment(sketch, "E1305", {"start": v(-6.07, 45.65) * mm, "end": v(-6.15, 45.64) * mm});
            skLineSegment(sketch, "E1306", {"start": v(-6.15, 45.64) * mm, "end": v(-6.17, 45.8) * mm});
            skLineSegment(sketch, "E1307", {"start": v(-6.17, 45.8) * mm, "end": v(-6.19, 45.95) * mm});
            skLineSegment(sketch, "E1308", {"start": v(-6.19, 45.95) * mm, "end": v(-6.2, 46.11) * mm});
            skLineSegment(sketch, "E1309", {"start": v(-6.2, 46.11) * mm, "end": v(-6.23, 46.27) * mm});
            skLineSegment(sketch, "E1310", {"start": v(-6.23, 46.27) * mm, "end": v(-6.24, 46.43) * mm});
            skLineSegment(sketch, "E1311", {"start": v(-6.24, 46.43) * mm, "end": v(-6.26, 46.59) * mm});
            skLineSegment(sketch, "E1312", {"start": v(-6.26, 46.59) * mm, "end": v(-6.28, 46.74) * mm});
            skLineSegment(sketch, "E1313", {"start": v(-6.28, 46.74) * mm, "end": v(-6.3, 46.9) * mm});
            skLineSegment(sketch, "E1314", {"start": v(-6.3, 46.9) * mm, "end": v(-6.32, 47.06) * mm});
            skLineSegment(sketch, "E1315", {"start": v(-6.32, 47.06) * mm, "end": v(-6.34, 47.21) * mm});
            skLineSegment(sketch, "E1316", {"start": v(-6.34, 47.21) * mm, "end": v(-6.36, 47.37) * mm});
            skLineSegment(sketch, "E1317", {"start": v(-6.36, 47.37) * mm, "end": v(-6.38, 47.53) * mm});
            skLineSegment(sketch, "E1318", {"start": v(-6.38, 47.53) * mm, "end": v(-6.4, 47.7) * mm});
            skLineSegment(sketch, "E1319", {"start": v(-6.4, 47.7) * mm, "end": v(-6.45, 47.86) * mm});
            skLineSegment(sketch, "E1320", {"start": v(-6.45, 47.86) * mm, "end": v(-6.53, 48) * mm});
            skLineSegment(sketch, "E1321", {"start": v(-6.53, 48) * mm, "end": v(-6.66, 48.1) * mm});
            skLineSegment(sketch, "E1322", {"start": v(-6.66, 48.1) * mm, "end": v(-6.8, 48.18) * mm});
            skLineSegment(sketch, "E1323", {"start": v(-6.8, 48.18) * mm, "end": v(-6.96, 48.21) * mm});
            skLineSegment(sketch, "E1324", {"start": v(-6.96, 48.21) * mm, "end": v(-7.03, 48.21) * mm});
            skLineSegment(sketch, "E1325", {"start": v(-7.03, 48.21) * mm, "end": v(-7.19, 48.19) * mm});
            skLineSegment(sketch, "E1326", {"start": v(-7.19, 48.19) * mm, "end": v(-7.34, 48.12) * mm});
            skLineSegment(sketch, "E1327", {"start": v(-7.34, 48.12) * mm, "end": v(-7.47, 48.02) * mm});
            skLineSegment(sketch, "E1328", {"start": v(-7.47, 48.02) * mm, "end": v(-7.56, 47.89) * mm});
            skLineSegment(sketch, "E1329", {"start": v(-7.56, 47.89) * mm, "end": v(-7.62, 47.73) * mm});
            skLineSegment(sketch, "E1330", {"start": v(-7.62, 47.73) * mm, "end": v(-7.64, 47.57) * mm});
            skLineSegment(sketch, "E1331", {"start": v(-7.64, 47.57) * mm, "end": v(-7.62, 47.41) * mm});
            skLineSegment(sketch, "E1332", {"start": v(-7.62, 47.41) * mm, "end": v(-7.6, 47.26) * mm});
            skLineSegment(sketch, "E1333", {"start": v(-7.6, 47.26) * mm, "end": v(-7.57, 47.1) * mm});
            skLineSegment(sketch, "E1334", {"start": v(-7.57, 47.1) * mm, "end": v(-7.55, 46.94) * mm});
            skLineSegment(sketch, "E1335", {"start": v(-7.55, 46.94) * mm, "end": v(-7.53, 46.79) * mm});
            skLineSegment(sketch, "E1336", {"start": v(-7.53, 46.79) * mm, "end": v(-7.5, 46.63) * mm});
            skLineSegment(sketch, "E1337", {"start": v(-7.5, 46.63) * mm, "end": v(-7.48, 46.47) * mm});
            skLineSegment(sketch, "E1338", {"start": v(-7.48, 46.47) * mm, "end": v(-7.46, 46.32) * mm});
            skLineSegment(sketch, "E1339", {"start": v(-7.46, 46.32) * mm, "end": v(-7.44, 46.16) * mm});
            skLineSegment(sketch, "E1340", {"start": v(-7.44, 46.16) * mm, "end": v(-7.41, 46) * mm});
            skLineSegment(sketch, "E1341", {"start": v(-7.41, 46) * mm, "end": v(-7.4, 45.85) * mm});
            skLineSegment(sketch, "E1342", {"start": v(-7.4, 45.85) * mm, "end": v(-7.37, 45.69) * mm});
            skLineSegment(sketch, "E1343", {"start": v(-7.37, 45.69) * mm, "end": v(-7.34, 45.53) * mm});
            skLineSegment(sketch, "E1344", {"start": v(-7.34, 45.53) * mm, "end": v(-7.34, 45.48) * mm});
            skLineSegment(sketch, "E1345", {"start": v(-7.34, 45.48) * mm, "end": v(-7.5, 45.46) * mm});
            skLineSegment(sketch, "E1346", {"start": v(-7.5, 45.46) * mm, "end": v(-7.65, 45.43) * mm});
            skLineSegment(sketch, "E1347", {"start": v(-7.65, 45.43) * mm, "end": v(-7.8, 45.4) * mm});
            skLineSegment(sketch, "E1348", {"start": v(-7.8, 45.4) * mm, "end": v(-7.96, 45.38) * mm});
            skLineSegment(sketch, "E1349", {"start": v(-7.96, 45.38) * mm, "end": v(-8.11, 45.36) * mm});
            skLineSegment(sketch, "E1350", {"start": v(-8.11, 45.36) * mm, "end": v(-8.27, 45.33) * mm});
            skLineSegment(sketch, "E1351", {"start": v(-8.27, 45.33) * mm, "end": v(-8.42, 45.3) * mm});
            skLineSegment(sketch, "E1352", {"start": v(-8.42, 45.3) * mm, "end": v(-8.58, 45.28) * mm});
            skLineSegment(sketch, "E1353", {"start": v(-8.58, 45.28) * mm, "end": v(-8.73, 45.25) * mm});
            skLineSegment(sketch, "E1354", {"start": v(-8.73, 45.25) * mm, "end": v(-8.9, 45.23) * mm});
            skLineSegment(sketch, "E1355", {"start": v(-8.9, 45.23) * mm, "end": v(-9.05, 45.2) * mm});
            skLineSegment(sketch, "E1356", {"start": v(-9.05, 45.2) * mm, "end": v(-9.12, 45.19) * mm});
            skLineSegment(sketch, "E1357", {"start": v(-9.12, 45.19) * mm, "end": v(-9.15, 45.34) * mm});
            skLineSegment(sketch, "E1358", {"start": v(-9.15, 45.34) * mm, "end": v(-9.18, 45.5) * mm});
            skLineSegment(sketch, "E1359", {"start": v(-9.18, 45.5) * mm, "end": v(-9.21, 45.66) * mm});
            skLineSegment(sketch, "E1360", {"start": v(-9.21, 45.66) * mm, "end": v(-9.24, 45.81) * mm});
            skLineSegment(sketch, "E1361", {"start": v(-9.24, 45.81) * mm, "end": v(-9.27, 45.97) * mm});
            skLineSegment(sketch, "E1362", {"start": v(-9.27, 45.97) * mm, "end": v(-9.3, 46.13) * mm});
            skLineSegment(sketch, "E1363", {"start": v(-9.3, 46.13) * mm, "end": v(-9.33, 46.28) * mm});
            skLineSegment(sketch, "E1364", {"start": v(-9.33, 46.28) * mm, "end": v(-9.36, 46.43) * mm});
            skLineSegment(sketch, "E1365", {"start": v(-9.36, 46.43) * mm, "end": v(-9.38, 46.6) * mm});
            skLineSegment(sketch, "E1366", {"start": v(-9.38, 46.6) * mm, "end": v(-9.41, 46.75) * mm});
            skLineSegment(sketch, "E1367", {"start": v(-9.41, 46.75) * mm, "end": v(-9.44, 46.9) * mm});
            skLineSegment(sketch, "E1368", {"start": v(-9.44, 46.9) * mm, "end": v(-9.47, 47.06) * mm});
            skLineSegment(sketch, "E1369", {"start": v(-9.47, 47.06) * mm, "end": v(-9.5, 47.23) * mm});
            skLineSegment(sketch, "E1370", {"start": v(-9.5, 47.23) * mm, "end": v(-9.56, 47.38) * mm});
            skLineSegment(sketch, "E1371", {"start": v(-9.56, 47.38) * mm, "end": v(-9.66, 47.51) * mm});
            skLineSegment(sketch, "E1372", {"start": v(-9.66, 47.51) * mm, "end": v(-9.79, 47.61) * mm});
            skLineSegment(sketch, "E1373", {"start": v(-9.79, 47.61) * mm, "end": v(-9.94, 47.68) * mm});
            skLineSegment(sketch, "E1374", {"start": v(-9.94, 47.68) * mm, "end": v(-10.1, 47.7) * mm});
            skLineSegment(sketch, "E1375", {"start": v(-10.1, 47.7) * mm, "end": v(-10.26, 47.68) * mm});
            skLineSegment(sketch, "E1376", {"start": v(-10.26, 47.68) * mm, "end": v(-10.42, 47.62) * mm});
            skLineSegment(sketch, "E1377", {"start": v(-10.42, 47.62) * mm, "end": v(-10.55, 47.52) * mm});
            skLineSegment(sketch, "E1378", {"start": v(-10.55, 47.52) * mm, "end": v(-10.65, 47.4) * mm});
            skLineSegment(sketch, "E1379", {"start": v(-10.65, 47.4) * mm, "end": v(-10.71, 47.24) * mm});
            skLineSegment(sketch, "E1380", {"start": v(-10.71, 47.24) * mm, "end": v(-10.74, 47.08) * mm});
            skLineSegment(sketch, "E1381", {"start": v(-10.74, 47.08) * mm, "end": v(-10.71, 46.93) * mm});
            skLineSegment(sketch, "E1382", {"start": v(-10.71, 46.93) * mm, "end": v(-10.68, 46.77) * mm});
            skLineSegment(sketch, "E1383", {"start": v(-10.68, 46.77) * mm, "end": v(-10.65, 46.62) * mm});
            skLineSegment(sketch, "E1384", {"start": v(-10.65, 46.62) * mm, "end": v(-10.62, 46.46) * mm});
            skLineSegment(sketch, "E1385", {"start": v(-10.62, 46.46) * mm, "end": v(-10.59, 46.31) * mm});
            skLineSegment(sketch, "E1386", {"start": v(-10.59, 46.31) * mm, "end": v(-10.55, 46.15) * mm});
            skLineSegment(sketch, "E1387", {"start": v(-10.55, 46.15) * mm, "end": v(-10.52, 46) * mm});
            skLineSegment(sketch, "E1388", {"start": v(-10.52, 46) * mm, "end": v(-10.49, 45.85) * mm});
            skLineSegment(sketch, "E1389", {"start": v(-10.49, 45.85) * mm, "end": v(-10.45, 45.69) * mm});
            skLineSegment(sketch, "E1390", {"start": v(-10.45, 45.69) * mm, "end": v(-10.42, 45.53) * mm});
            skLineSegment(sketch, "E1391", {"start": v(-10.42, 45.53) * mm, "end": v(-10.39, 45.38) * mm});
            skLineSegment(sketch, "E1392", {"start": v(-10.39, 45.38) * mm, "end": v(-10.36, 45.22) * mm});
            skLineSegment(sketch, "E1393", {"start": v(-10.36, 45.22) * mm, "end": v(-10.32, 45.07) * mm});
            skLineSegment(sketch, "E1394", {"start": v(-10.32, 45.07) * mm, "end": v(-10.3, 44.96) * mm});
            skLineSegment(sketch, "E1395", {"start": v(-10.3, 44.96) * mm, "end": v(-10.45, 44.92) * mm});
            skLineSegment(sketch, "E1396", {"start": v(-10.45, 44.92) * mm, "end": v(-10.6, 44.88) * mm});
            skLineSegment(sketch, "E1397", {"start": v(-10.6, 44.88) * mm, "end": v(-10.76, 44.85) * mm});
            skLineSegment(sketch, "E1398", {"start": v(-10.76, 44.85) * mm, "end": v(-10.91, 44.81) * mm});
            skLineSegment(sketch, "E1399", {"start": v(-10.91, 44.81) * mm, "end": v(-11.06, 44.78) * mm});
            skLineSegment(sketch, "E1400", {"start": v(-11.06, 44.78) * mm, "end": v(-11.22, 44.74) * mm});
            skLineSegment(sketch, "E1401", {"start": v(-11.22, 44.74) * mm, "end": v(-11.37, 44.7) * mm});
            skLineSegment(sketch, "E1402", {"start": v(-11.37, 44.7) * mm, "end": v(-11.52, 44.67) * mm});
            skLineSegment(sketch, "E1403", {"start": v(-11.52, 44.67) * mm, "end": v(-11.68, 44.63) * mm});
            skLineSegment(sketch, "E1404", {"start": v(-11.68, 44.63) * mm, "end": v(-11.83, 44.6) * mm});
            skLineSegment(sketch, "E1405", {"start": v(-11.83, 44.6) * mm, "end": v(-11.98, 44.56) * mm});
            skLineSegment(sketch, "E1406", {"start": v(-11.98, 44.56) * mm, "end": v(-12.06, 44.54) * mm});
            skLineSegment(sketch, "E1407", {"start": v(-12.06, 44.54) * mm, "end": v(-12.1, 44.7) * mm});
            skLineSegment(sketch, "E1408", {"start": v(-12.1, 44.7) * mm, "end": v(-12.14, 44.85) * mm});
            skLineSegment(sketch, "E1409", {"start": v(-12.14, 44.85) * mm, "end": v(-12.18, 45) * mm});
            skLineSegment(sketch, "E1410", {"start": v(-12.18, 45) * mm, "end": v(-12.22, 45.16) * mm});
            skLineSegment(sketch, "E1411", {"start": v(-12.22, 45.16) * mm, "end": v(-12.26, 45.31) * mm});
            skLineSegment(sketch, "E1412", {"start": v(-12.26, 45.31) * mm, "end": v(-12.3, 45.47) * mm});
            skLineSegment(sketch, "E1413", {"start": v(-12.3, 45.47) * mm, "end": v(-12.34, 45.62) * mm});
            skLineSegment(sketch, "E1414", {"start": v(-12.34, 45.62) * mm, "end": v(-12.37, 45.77) * mm});
            skLineSegment(sketch, "E1415", {"start": v(-12.37, 45.77) * mm, "end": v(-12.41, 45.93) * mm});
            skLineSegment(sketch, "E1416", {"start": v(-12.41, 45.93) * mm, "end": v(-12.45, 46.08) * mm});
            skLineSegment(sketch, "E1417", {"start": v(-12.45, 46.08) * mm, "end": v(-12.5, 46.23) * mm});
            skLineSegment(sketch, "E1418", {"start": v(-12.5, 46.23) * mm, "end": v(-12.53, 46.4) * mm});
            skLineSegment(sketch, "E1419", {"start": v(-12.53, 46.4) * mm, "end": v(-12.57, 46.55) * mm});
            skLineSegment(sketch, "E1420", {"start": v(-12.57, 46.55) * mm, "end": v(-12.64, 46.7) * mm});
            skLineSegment(sketch, "E1421", {"start": v(-12.64, 46.7) * mm, "end": v(-12.75, 46.83) * mm});
            skLineSegment(sketch, "E1422", {"start": v(-12.75, 46.83) * mm, "end": v(-12.88, 46.92) * mm});
            skLineSegment(sketch, "E1423", {"start": v(-12.88, 46.92) * mm, "end": v(-13.04, 46.98) * mm});
            skLineSegment(sketch, "E1424", {"start": v(-13.04, 46.98) * mm, "end": v(-13.17, 46.99) * mm});
            skLineSegment(sketch, "E1425", {"start": v(-13.17, 46.99) * mm, "end": v(-13.33, 46.97) * mm});
            skLineSegment(sketch, "E1426", {"start": v(-13.33, 46.97) * mm, "end": v(-13.48, 46.9) * mm});
            skLineSegment(sketch, "E1427", {"start": v(-13.48, 46.9) * mm, "end": v(-13.61, 46.8) * mm});
            skLineSegment(sketch, "E1428", {"start": v(-13.61, 46.8) * mm, "end": v(-13.71, 46.67) * mm});
            skLineSegment(sketch, "E1429", {"start": v(-13.71, 46.67) * mm, "end": v(-13.77, 46.52) * mm});
            skLineSegment(sketch, "E1430", {"start": v(-13.77, 46.52) * mm, "end": v(-13.8, 46.36) * mm});
            skLineSegment(sketch, "E1431", {"start": v(-13.8, 46.36) * mm, "end": v(-13.77, 46.2) * mm});
            skLineSegment(sketch, "E1432", {"start": v(-13.77, 46.2) * mm, "end": v(-13.73, 46.05) * mm});
            skLineSegment(sketch, "E1433", {"start": v(-13.73, 46.05) * mm, "end": v(-13.69, 45.9) * mm});
            skLineSegment(sketch, "E1434", {"start": v(-13.69, 45.9) * mm, "end": v(-13.64, 45.74) * mm});
            skLineSegment(sketch, "E1435", {"start": v(-13.64, 45.74) * mm, "end": v(-13.6, 45.59) * mm});
            skLineSegment(sketch, "E1436", {"start": v(-13.6, 45.59) * mm, "end": v(-13.56, 45.44) * mm});
            skLineSegment(sketch, "E1437", {"start": v(-13.56, 45.44) * mm, "end": v(-13.51, 45.28) * mm});
            skLineSegment(sketch, "E1438", {"start": v(-13.51, 45.28) * mm, "end": v(-13.47, 45.13) * mm});
            skLineSegment(sketch, "E1439", {"start": v(-13.47, 45.13) * mm, "end": v(-13.43, 44.98) * mm});
            skLineSegment(sketch, "E1440", {"start": v(-13.43, 44.98) * mm, "end": v(-13.38, 44.82) * mm});
            skLineSegment(sketch, "E1441", {"start": v(-13.38, 44.82) * mm, "end": v(-13.34, 44.67) * mm});
            skLineSegment(sketch, "E1442", {"start": v(-13.34, 44.67) * mm, "end": v(-13.3, 44.52) * mm});
            skLineSegment(sketch, "E1443", {"start": v(-13.3, 44.52) * mm, "end": v(-13.26, 44.37) * mm});
            skLineSegment(sketch, "E1444", {"start": v(-13.26, 44.37) * mm, "end": v(-13.22, 44.23) * mm});
            skLineSegment(sketch, "E1445", {"start": v(-13.22, 44.23) * mm, "end": v(-13.37, 44.19) * mm});
            skLineSegment(sketch, "E1446", {"start": v(-13.37, 44.19) * mm, "end": v(-13.52, 44.14) * mm});
            skLineSegment(sketch, "E1447", {"start": v(-13.52, 44.14) * mm, "end": v(-13.67, 44.1) * mm});
            skLineSegment(sketch, "E1448", {"start": v(-13.67, 44.1) * mm, "end": v(-13.82, 44.05) * mm});
            skLineSegment(sketch, "E1449", {"start": v(-13.82, 44.05) * mm, "end": v(-13.97, 44) * mm});
            skLineSegment(sketch, "E1450", {"start": v(-13.97, 44) * mm, "end": v(-14.12, 43.96) * mm});
            skLineSegment(sketch, "E1451", {"start": v(-14.12, 43.96) * mm, "end": v(-14.27, 43.91) * mm});
            skLineSegment(sketch, "E1452", {"start": v(-14.27, 43.91) * mm, "end": v(-14.42, 43.87) * mm});
            skLineSegment(sketch, "E1453", {"start": v(-14.42, 43.87) * mm, "end": v(-14.57, 43.82) * mm});
            skLineSegment(sketch, "E1454", {"start": v(-14.57, 43.82) * mm, "end": v(-14.72, 43.78) * mm});
            skLineSegment(sketch, "E1455", {"start": v(-14.72, 43.78) * mm, "end": v(-14.87, 43.73) * mm});
            skLineSegment(sketch, "E1456", {"start": v(-14.87, 43.73) * mm, "end": v(-14.95, 43.7) * mm});
            skLineSegment(sketch, "E1457", {"start": v(-14.95, 43.7) * mm, "end": v(-15, 43.86) * mm});
            skLineSegment(sketch, "E1458", {"start": v(-15, 43.86) * mm, "end": v(-15.05, 44) * mm});
            skLineSegment(sketch, "E1459", {"start": v(-15.05, 44) * mm, "end": v(-15.1, 44.16) * mm});
            skLineSegment(sketch, "E1460", {"start": v(-15.1, 44.16) * mm, "end": v(-15.15, 44.31) * mm});
            skLineSegment(sketch, "E1461", {"start": v(-15.15, 44.31) * mm, "end": v(-15.2, 44.46) * mm});
            skLineSegment(sketch, "E1462", {"start": v(-15.2, 44.46) * mm, "end": v(-15.25, 44.61) * mm});
            skLineSegment(sketch, "E1463", {"start": v(-15.25, 44.61) * mm, "end": v(-15.3, 44.76) * mm});
            skLineSegment(sketch, "E1464", {"start": v(-15.3, 44.76) * mm, "end": v(-15.34, 44.91) * mm});
            skLineSegment(sketch, "E1465", {"start": v(-15.34, 44.91) * mm, "end": v(-15.4, 45.07) * mm});
            skLineSegment(sketch, "E1466", {"start": v(-15.4, 45.07) * mm, "end": v(-15.44, 45.22) * mm});
            skLineSegment(sketch, "E1467", {"start": v(-15.44, 45.22) * mm, "end": v(-15.49, 45.37) * mm});
            skLineSegment(sketch, "E1468", {"start": v(-15.49, 45.37) * mm, "end": v(-15.54, 45.52) * mm});
            skLineSegment(sketch, "E1469", {"start": v(-15.54, 45.52) * mm, "end": v(-15.6, 45.68) * mm});
            skLineSegment(sketch, "E1470", {"start": v(-15.6, 45.68) * mm, "end": v(-15.67, 45.82) * mm});
            skLineSegment(sketch, "E1471", {"start": v(-15.67, 45.82) * mm, "end": v(-15.79, 45.94) * mm});
            skLineSegment(sketch, "E1472", {"start": v(-15.79, 45.94) * mm, "end": v(-15.93, 46.03) * mm});
            skLineSegment(sketch, "E1473", {"start": v(-15.93, 46.03) * mm, "end": v(-16.08, 46.07) * mm});
            skLineSegment(sketch, "E1474", {"start": v(-16.08, 46.07) * mm, "end": v(-16.18, 46.08) * mm});
            skLineSegment(sketch, "E1475", {"start": v(-16.18, 46.08) * mm, "end": v(-16.34, 46.05) * mm});
            skLineSegment(sketch, "E1476", {"start": v(-16.34, 46.05) * mm, "end": v(-16.5, 45.99) * mm});
            skLineSegment(sketch, "E1477", {"start": v(-16.5, 45.99) * mm, "end": v(-16.62, 45.89) * mm});
            skLineSegment(sketch, "E1478", {"start": v(-16.62, 45.89) * mm, "end": v(-16.72, 45.76) * mm});
            skLineSegment(sketch, "E1479", {"start": v(-16.72, 45.76) * mm, "end": v(-16.78, 45.6) * mm});
            skLineSegment(sketch, "E1480", {"start": v(-16.78, 45.6) * mm, "end": v(-16.8, 45.44) * mm});
            skLineSegment(sketch, "E1481", {"start": v(-16.8, 45.44) * mm, "end": v(-16.78, 45.28) * mm});
            skLineSegment(sketch, "E1482", {"start": v(-16.78, 45.28) * mm, "end": v(-16.72, 45.12) * mm});
            skLineSegment(sketch, "E1483", {"start": v(-16.72, 45.12) * mm, "end": v(-16.67, 44.97) * mm});
            skLineSegment(sketch, "E1484", {"start": v(-16.67, 44.97) * mm, "end": v(-16.62, 44.82) * mm});
            skLineSegment(sketch, "E1485", {"start": v(-16.62, 44.82) * mm, "end": v(-16.56, 44.67) * mm});
            skLineSegment(sketch, "E1486", {"start": v(-16.56, 44.67) * mm, "end": v(-16.5, 44.52) * mm});
            skLineSegment(sketch, "E1487", {"start": v(-16.5, 44.52) * mm, "end": v(-16.46, 44.37) * mm});
            skLineSegment(sketch, "E1488", {"start": v(-16.46, 44.37) * mm, "end": v(-16.4, 44.22) * mm});
            skLineSegment(sketch, "E1489", {"start": v(-16.4, 44.22) * mm, "end": v(-16.35, 44.07) * mm});
            skLineSegment(sketch, "E1490", {"start": v(-16.35, 44.07) * mm, "end": v(-16.3, 43.92) * mm});
            skLineSegment(sketch, "E1491", {"start": v(-16.3, 43.92) * mm, "end": v(-16.24, 43.77) * mm});
            skLineSegment(sketch, "E1492", {"start": v(-16.24, 43.77) * mm, "end": v(-16.2, 43.62) * mm});
            skLineSegment(sketch, "E1493", {"start": v(-16.2, 43.62) * mm, "end": v(-16.14, 43.48) * mm});
            skLineSegment(sketch, "E1494", {"start": v(-16.14, 43.48) * mm, "end": v(-16.09, 43.32) * mm});
            skLineSegment(sketch, "E1495", {"start": v(-16.09, 43.32) * mm, "end": v(-16.23, 43.27) * mm});
            skLineSegment(sketch, "E1496", {"start": v(-16.23, 43.27) * mm, "end": v(-16.38, 43.21) * mm});
            skLineSegment(sketch, "E1497", {"start": v(-16.38, 43.21) * mm, "end": v(-16.53, 43.16) * mm});
            skLineSegment(sketch, "E1498", {"start": v(-16.53, 43.16) * mm, "end": v(-16.67, 43.1) * mm});
            skLineSegment(sketch, "E1499", {"start": v(-16.67, 43.1) * mm, "end": v(-16.82, 43.05) * mm});
            skLineSegment(sketch, "E1500", {"start": v(-16.82, 43.05) * mm, "end": v(-16.97, 43) * mm});
            skLineSegment(sketch, "E1501", {"start": v(-16.97, 43) * mm, "end": v(-17.12, 42.94) * mm});
            skLineSegment(sketch, "E1502", {"start": v(-17.12, 42.94) * mm, "end": v(-17.26, 42.88) * mm});
            skLineSegment(sketch, "E1503", {"start": v(-17.26, 42.88) * mm, "end": v(-17.4, 42.83) * mm});
            skLineSegment(sketch, "E1504", {"start": v(-17.4, 42.83) * mm, "end": v(-17.56, 42.77) * mm});
            skLineSegment(sketch, "E1505", {"start": v(-17.56, 42.77) * mm, "end": v(-17.7, 42.71) * mm});
            skLineSegment(sketch, "E1506", {"start": v(-17.7, 42.71) * mm, "end": v(-17.78, 42.69) * mm});
            skLineSegment(sketch, "E1507", {"start": v(-17.78, 42.69) * mm, "end": v(-17.84, 42.83) * mm});
            skLineSegment(sketch, "E1508", {"start": v(-17.84, 42.83) * mm, "end": v(-17.9, 42.98) * mm});
            skLineSegment(sketch, "E1509", {"start": v(-17.9, 42.98) * mm, "end": v(-17.96, 43.13) * mm});
            skLineSegment(sketch, "E1510", {"start": v(-17.96, 43.13) * mm, "end": v(-18.01, 43.27) * mm});
            skLineSegment(sketch, "E1511", {"start": v(-18.01, 43.27) * mm, "end": v(-18.07, 43.42) * mm});
            skLineSegment(sketch, "E1512", {"start": v(-18.07, 43.42) * mm, "end": v(-18.13, 43.57) * mm});
            skLineSegment(sketch, "E1513", {"start": v(-18.13, 43.57) * mm, "end": v(-18.2, 43.72) * mm});
            skLineSegment(sketch, "E1514", {"start": v(-18.2, 43.72) * mm, "end": v(-18.25, 43.86) * mm});
            skLineSegment(sketch, "E1515", {"start": v(-18.25, 43.86) * mm, "end": v(-18.3, 44.01) * mm});
            skLineSegment(sketch, "E1516", {"start": v(-18.3, 44.01) * mm, "end": v(-18.37, 44.16) * mm});
            skLineSegment(sketch, "E1517", {"start": v(-18.37, 44.16) * mm, "end": v(-18.43, 44.3) * mm});
            skLineSegment(sketch, "E1518", {"start": v(-18.43, 44.3) * mm, "end": v(-18.49, 44.45) * mm});
            skLineSegment(sketch, "E1519", {"start": v(-18.49, 44.45) * mm, "end": v(-18.55, 44.61) * mm});
            skLineSegment(sketch, "E1520", {"start": v(-18.55, 44.61) * mm, "end": v(-18.64, 44.75) * mm});
            skLineSegment(sketch, "E1521", {"start": v(-18.64, 44.75) * mm, "end": v(-18.76, 44.86) * mm});
            skLineSegment(sketch, "E1522", {"start": v(-18.76, 44.86) * mm, "end": v(-18.9, 44.93) * mm});
            skLineSegment(sketch, "E1523", {"start": v(-18.9, 44.93) * mm, "end": v(-19.06, 44.97) * mm});
            skLineSegment(sketch, "E1524", {"start": v(-19.06, 44.97) * mm, "end": v(-19.13, 44.97) * mm});
            skLineSegment(sketch, "E1525", {"start": v(-19.13, 44.97) * mm, "end": v(-19.3, 44.95) * mm});
            skLineSegment(sketch, "E1526", {"start": v(-19.3, 44.95) * mm, "end": v(-19.44, 44.88) * mm});
            skLineSegment(sketch, "E1527", {"start": v(-19.44, 44.88) * mm, "end": v(-19.57, 44.78) * mm});
            skLineSegment(sketch, "E1528", {"start": v(-19.57, 44.78) * mm, "end": v(-19.67, 44.64) * mm});
            skLineSegment(sketch, "E1529", {"start": v(-19.67, 44.64) * mm, "end": v(-19.72, 44.49) * mm});
            skLineSegment(sketch, "E1530", {"start": v(-19.72, 44.49) * mm, "end": v(-19.74, 44.33) * mm});
            skLineSegment(sketch, "E1531", {"start": v(-19.74, 44.33) * mm, "end": v(-19.71, 44.16) * mm});
            skLineSegment(sketch, "E1532", {"start": v(-19.71, 44.16) * mm, "end": v(-19.65, 44.02) * mm});
            skLineSegment(sketch, "E1533", {"start": v(-19.65, 44.02) * mm, "end": v(-19.6, 43.87) * mm});
            skLineSegment(sketch, "E1534", {"start": v(-19.6, 43.87) * mm, "end": v(-19.53, 43.73) * mm});
            skLineSegment(sketch, "E1535", {"start": v(-19.53, 43.73) * mm, "end": v(-19.47, 43.58) * mm});
            skLineSegment(sketch, "E1536", {"start": v(-19.47, 43.58) * mm, "end": v(-19.4, 43.44) * mm});
            skLineSegment(sketch, "E1537", {"start": v(-19.4, 43.44) * mm, "end": v(-19.34, 43.3) * mm});
            skLineSegment(sketch, "E1538", {"start": v(-19.34, 43.3) * mm, "end": v(-19.28, 43.15) * mm});
            skLineSegment(sketch, "E1539", {"start": v(-19.28, 43.15) * mm, "end": v(-19.22, 43) * mm});
            skLineSegment(sketch, "E1540", {"start": v(-19.22, 43) * mm, "end": v(-19.15, 42.85) * mm});
            skLineSegment(sketch, "E1541", {"start": v(-19.15, 42.85) * mm, "end": v(-19.1, 42.7) * mm});
            skLineSegment(sketch, "E1542", {"start": v(-19.1, 42.7) * mm, "end": v(-19.03, 42.56) * mm});
            skLineSegment(sketch, "E1543", {"start": v(-19.03, 42.56) * mm, "end": v(-18.97, 42.42) * mm});
            skLineSegment(sketch, "E1544", {"start": v(-18.97, 42.42) * mm, "end": v(-18.9, 42.27) * mm});
            skLineSegment(sketch, "E1545", {"start": v(-18.9, 42.27) * mm, "end": v(-18.89, 42.23) * mm});
            skLineSegment(sketch, "E1546", {"start": v(-18.89, 42.23) * mm, "end": v(-19.03, 42.16) * mm});
            skLineSegment(sketch, "E1547", {"start": v(-19.03, 42.16) * mm, "end": v(-19.17, 42.1) * mm});
            skLineSegment(sketch, "E1548", {"start": v(-19.17, 42.1) * mm, "end": v(-19.32, 42.03) * mm});
            skLineSegment(sketch, "E1549", {"start": v(-19.32, 42.03) * mm, "end": v(-19.46, 41.97) * mm});
            skLineSegment(sketch, "E1550", {"start": v(-19.46, 41.97) * mm, "end": v(-19.6, 41.9) * mm});
            skLineSegment(sketch, "E1551", {"start": v(-19.6, 41.9) * mm, "end": v(-19.75, 41.84) * mm});
            skLineSegment(sketch, "E1552", {"start": v(-19.75, 41.84) * mm, "end": v(-19.89, 41.77) * mm});
            skLineSegment(sketch, "E1553", {"start": v(-19.89, 41.77) * mm, "end": v(-20.03, 41.7) * mm});
            skLineSegment(sketch, "E1554", {"start": v(-20.03, 41.7) * mm, "end": v(-20.18, 41.64) * mm});
            skLineSegment(sketch, "E1555", {"start": v(-20.18, 41.64) * mm, "end": v(-20.32, 41.58) * mm});
            skLineSegment(sketch, "E1556", {"start": v(-20.32, 41.58) * mm, "end": v(-20.46, 41.51) * mm});
            skLineSegment(sketch, "E1557", {"start": v(-20.46, 41.51) * mm, "end": v(-20.53, 41.48) * mm});
            skLineSegment(sketch, "E1558", {"start": v(-20.53, 41.48) * mm, "end": v(-20.6, 41.62) * mm});
            skLineSegment(sketch, "E1559", {"start": v(-20.6, 41.62) * mm, "end": v(-20.67, 41.76) * mm});
            skLineSegment(sketch, "E1560", {"start": v(-20.67, 41.76) * mm, "end": v(-20.74, 41.91) * mm});
            skLineSegment(sketch, "E1561", {"start": v(-20.74, 41.91) * mm, "end": v(-20.8, 42.05) * mm});
            skLineSegment(sketch, "E1562", {"start": v(-20.8, 42.05) * mm, "end": v(-20.88, 42.2) * mm});
            skLineSegment(sketch, "E1563", {"start": v(-20.88, 42.2) * mm, "end": v(-20.94, 42.34) * mm});
            skLineSegment(sketch, "E1564", {"start": v(-20.94, 42.34) * mm, "end": v(-21.01, 42.48) * mm});
            skLineSegment(sketch, "E1565", {"start": v(-21.01, 42.48) * mm, "end": v(-21.08, 42.62) * mm});
            skLineSegment(sketch, "E1566", {"start": v(-21.08, 42.62) * mm, "end": v(-21.15, 42.77) * mm});
            skLineSegment(sketch, "E1567", {"start": v(-21.15, 42.77) * mm, "end": v(-21.22, 42.91) * mm});
            skLineSegment(sketch, "E1568", {"start": v(-21.22, 42.91) * mm, "end": v(-21.29, 43.05) * mm});
            skLineSegment(sketch, "E1569", {"start": v(-21.29, 43.05) * mm, "end": v(-21.35, 43.2) * mm});
            skLineSegment(sketch, "E1570", {"start": v(-21.35, 43.2) * mm, "end": v(-21.43, 43.35) * mm});
            skLineSegment(sketch, "E1571", {"start": v(-21.43, 43.35) * mm, "end": v(-21.53, 43.48) * mm});
            skLineSegment(sketch, "E1572", {"start": v(-21.53, 43.48) * mm, "end": v(-21.65, 43.59) * mm});
            skLineSegment(sketch, "E1573", {"start": v(-21.65, 43.59) * mm, "end": v(-21.8, 43.65) * mm});
            skLineSegment(sketch, "E1574", {"start": v(-21.8, 43.65) * mm, "end": v(-21.97, 43.67) * mm});
            skLineSegment(sketch, "E1575", {"start": v(-21.97, 43.67) * mm, "end": v(-22.13, 43.66) * mm});
            skLineSegment(sketch, "E1576", {"start": v(-22.13, 43.66) * mm, "end": v(-22.28, 43.6) * mm});
            skLineSegment(sketch, "E1577", {"start": v(-22.28, 43.6) * mm, "end": v(-22.41, 43.5) * mm});
            skLineSegment(sketch, "E1578", {"start": v(-22.41, 43.5) * mm, "end": v(-22.51, 43.37) * mm});
            skLineSegment(sketch, "E1579", {"start": v(-22.51, 43.37) * mm, "end": v(-22.58, 43.22) * mm});
            skLineSegment(sketch, "E1580", {"start": v(-22.58, 43.22) * mm, "end": v(-22.6, 43.05) * mm});
            skLineSegment(sketch, "E1581", {"start": v(-22.6, 43.05) * mm, "end": v(-22.58, 42.9) * mm});
            skLineSegment(sketch, "E1582", {"start": v(-22.58, 42.9) * mm, "end": v(-22.52, 42.75) * mm});
            skLineSegment(sketch, "E1583", {"start": v(-22.52, 42.75) * mm, "end": v(-22.45, 42.6) * mm});
            skLineSegment(sketch, "E1584", {"start": v(-22.45, 42.6) * mm, "end": v(-22.38, 42.47) * mm});
            skLineSegment(sketch, "E1585", {"start": v(-22.38, 42.47) * mm, "end": v(-22.3, 42.33) * mm});
            skLineSegment(sketch, "E1586", {"start": v(-22.3, 42.33) * mm, "end": v(-22.24, 42.19) * mm});
            skLineSegment(sketch, "E1587", {"start": v(-22.24, 42.19) * mm, "end": v(-22.16, 42.04) * mm});
            skLineSegment(sketch, "E1588", {"start": v(-22.16, 42.04) * mm, "end": v(-22.1, 41.9) * mm});
            skLineSegment(sketch, "E1589", {"start": v(-22.1, 41.9) * mm, "end": v(-22.02, 41.76) * mm});
            skLineSegment(sketch, "E1590", {"start": v(-22.02, 41.76) * mm, "end": v(-21.95, 41.62) * mm});
            skLineSegment(sketch, "E1591", {"start": v(-21.95, 41.62) * mm, "end": v(-21.88, 41.48) * mm});
            skLineSegment(sketch, "E1592", {"start": v(-21.88, 41.48) * mm, "end": v(-21.8, 41.34) * mm});
            skLineSegment(sketch, "E1593", {"start": v(-21.8, 41.34) * mm, "end": v(-21.73, 41.2) * mm});
            skLineSegment(sketch, "E1594", {"start": v(-21.73, 41.2) * mm, "end": v(-21.66, 41.05) * mm});
            skLineSegment(sketch, "E1595", {"start": v(-21.66, 41.05) * mm, "end": v(-21.6, 40.95) * mm});
            skLineSegment(sketch, "E1596", {"start": v(-21.6, 40.95) * mm, "end": v(-21.75, 40.88) * mm});
            skLineSegment(sketch, "E1597", {"start": v(-21.75, 40.88) * mm, "end": v(-21.89, 40.8) * mm});
            skLineSegment(sketch, "E1598", {"start": v(-21.89, 40.8) * mm, "end": v(-22.02, 40.73) * mm});
            skLineSegment(sketch, "E1599", {"start": v(-22.02, 40.73) * mm, "end": v(-22.16, 40.65) * mm});
            skLineSegment(sketch, "E1600", {"start": v(-22.16, 40.65) * mm, "end": v(-22.3, 40.58) * mm});
            skLineSegment(sketch, "E1601", {"start": v(-22.3, 40.58) * mm, "end": v(-22.44, 40.5) * mm});
            skLineSegment(sketch, "E1602", {"start": v(-22.44, 40.5) * mm, "end": v(-22.58, 40.43) * mm});
            skLineSegment(sketch, "E1603", {"start": v(-22.58, 40.43) * mm, "end": v(-22.72, 40.36) * mm});
            skLineSegment(sketch, "E1604", {"start": v(-22.72, 40.36) * mm, "end": v(-22.86, 40.28) * mm});
            skLineSegment(sketch, "E1605", {"start": v(-22.86, 40.28) * mm, "end": v(-23, 40.2) * mm});
            skLineSegment(sketch, "E1606", {"start": v(-23, 40.2) * mm, "end": v(-23.13, 40.14) * mm});
            skLineSegment(sketch, "E1607", {"start": v(-23.13, 40.14) * mm, "end": v(-23.2, 40.1) * mm});
            skLineSegment(sketch, "E1608", {"start": v(-23.2, 40.1) * mm, "end": v(-23.28, 40.23) * mm});
            skLineSegment(sketch, "E1609", {"start": v(-23.28, 40.23) * mm, "end": v(-23.36, 40.37) * mm});
            skLineSegment(sketch, "E1610", {"start": v(-23.36, 40.37) * mm, "end": v(-23.44, 40.51) * mm});
            skLineSegment(sketch, "E1611", {"start": v(-23.44, 40.51) * mm, "end": v(-23.52, 40.65) * mm});
            skLineSegment(sketch, "E1612", {"start": v(-23.52, 40.65) * mm, "end": v(-23.6, 40.79) * mm});
            skLineSegment(sketch, "E1613", {"start": v(-23.6, 40.79) * mm, "end": v(-23.67, 40.93) * mm});
            skLineSegment(sketch, "E1614", {"start": v(-23.67, 40.93) * mm, "end": v(-23.75, 41.07) * mm});
            skLineSegment(sketch, "E1615", {"start": v(-23.75, 41.07) * mm, "end": v(-23.82, 41.2) * mm});
            skLineSegment(sketch, "E1616", {"start": v(-23.82, 41.2) * mm, "end": v(-23.9, 41.34) * mm});
            skLineSegment(sketch, "E1617", {"start": v(-23.9, 41.34) * mm, "end": v(-23.98, 41.48) * mm});
            skLineSegment(sketch, "E1618", {"start": v(-23.98, 41.48) * mm, "end": v(-24.06, 41.62) * mm});
            skLineSegment(sketch, "E1619", {"start": v(-24.06, 41.62) * mm, "end": v(-24.14, 41.76) * mm});
            skLineSegment(sketch, "E1620", {"start": v(-24.14, 41.76) * mm, "end": v(-24.22, 41.9) * mm});
            skLineSegment(sketch, "E1621", {"start": v(-24.22, 41.9) * mm, "end": v(-24.33, 42.03) * mm});
            skLineSegment(sketch, "E1622", {"start": v(-24.33, 42.03) * mm, "end": v(-24.46, 42.12) * mm});
            skLineSegment(sketch, "E1623", {"start": v(-24.46, 42.12) * mm, "end": v(-24.61, 42.18) * mm});
            skLineSegment(sketch, "E1624", {"start": v(-24.61, 42.18) * mm, "end": v(-24.74, 42.2) * mm});
            skLineSegment(sketch, "E1625", {"start": v(-24.74, 42.2) * mm, "end": v(-24.9, 42.17) * mm});
            skLineSegment(sketch, "E1626", {"start": v(-24.9, 42.17) * mm, "end": v(-25.06, 42.11) * mm});
            skLineSegment(sketch, "E1627", {"start": v(-25.06, 42.11) * mm, "end": v(-25.19, 42.01) * mm});
            skLineSegment(sketch, "E1628", {"start": v(-25.19, 42.01) * mm, "end": v(-25.29, 41.88) * mm});
            skLineSegment(sketch, "E1629", {"start": v(-25.29, 41.88) * mm, "end": v(-25.35, 41.73) * mm});
            skLineSegment(sketch, "E1630", {"start": v(-25.35, 41.73) * mm, "end": v(-25.37, 41.57) * mm});
            skLineSegment(sketch, "E1631", {"start": v(-25.37, 41.57) * mm, "end": v(-25.35, 41.4) * mm});
            skLineSegment(sketch, "E1632", {"start": v(-25.35, 41.4) * mm, "end": v(-25.29, 41.25) * mm});
            skLineSegment(sketch, "E1633", {"start": v(-25.29, 41.25) * mm, "end": v(-25.2, 41.12) * mm});
            skLineSegment(sketch, "E1634", {"start": v(-25.2, 41.12) * mm, "end": v(-25.12, 40.98) * mm});
            skLineSegment(sketch, "E1635", {"start": v(-25.12, 40.98) * mm, "end": v(-25.04, 40.84) * mm});
            skLineSegment(sketch, "E1636", {"start": v(-25.04, 40.84) * mm, "end": v(-24.96, 40.7) * mm});
            skLineSegment(sketch, "E1637", {"start": v(-24.96, 40.7) * mm, "end": v(-24.88, 40.57) * mm});
            skLineSegment(sketch, "E1638", {"start": v(-24.88, 40.57) * mm, "end": v(-24.8, 40.43) * mm});
            skLineSegment(sketch, "E1639", {"start": v(-24.8, 40.43) * mm, "end": v(-24.72, 40.3) * mm});
            skLineSegment(sketch, "E1640", {"start": v(-24.72, 40.3) * mm, "end": v(-24.64, 40.16) * mm});
            skLineSegment(sketch, "E1641", {"start": v(-24.64, 40.16) * mm, "end": v(-24.56, 40.02) * mm});
            skLineSegment(sketch, "E1642", {"start": v(-24.56, 40.02) * mm, "end": v(-24.48, 39.89) * mm});
            skLineSegment(sketch, "E1643", {"start": v(-24.48, 39.89) * mm, "end": v(-24.4, 39.75) * mm});
            skLineSegment(sketch, "E1644", {"start": v(-24.4, 39.75) * mm, "end": v(-24.31, 39.62) * mm});
            skLineSegment(sketch, "E1645", {"start": v(-24.31, 39.62) * mm, "end": v(-24.24, 39.5) * mm});
            skLineSegment(sketch, "E1646", {"start": v(-24.24, 39.5) * mm, "end": v(-24.38, 39.42) * mm});
            skLineSegment(sketch, "E1647", {"start": v(-24.38, 39.42) * mm, "end": v(-24.5, 39.33) * mm});
            skLineSegment(sketch, "E1648", {"start": v(-24.5, 39.33) * mm, "end": v(-24.64, 39.25) * mm});
            skLineSegment(sketch, "E1649", {"start": v(-24.64, 39.25) * mm, "end": v(-24.78, 39.17) * mm});
            skLineSegment(sketch, "E1650", {"start": v(-24.78, 39.17) * mm, "end": v(-24.91, 39.08) * mm});
            skLineSegment(sketch, "E1651", {"start": v(-24.91, 39.08) * mm, "end": v(-25.04, 39) * mm});
            skLineSegment(sketch, "E1652", {"start": v(-25.04, 39) * mm, "end": v(-25.18, 38.92) * mm});
            skLineSegment(sketch, "E1653", {"start": v(-25.18, 38.92) * mm, "end": v(-25.31, 38.83) * mm});
            skLineSegment(sketch, "E1654", {"start": v(-25.31, 38.83) * mm, "end": v(-25.44, 38.75) * mm});
            skLineSegment(sketch, "E1655", {"start": v(-25.44, 38.75) * mm, "end": v(-25.58, 38.67) * mm});
            skLineSegment(sketch, "E1656", {"start": v(-25.58, 38.67) * mm, "end": v(-25.71, 38.59) * mm});
            skLineSegment(sketch, "E1657", {"start": v(-25.71, 38.59) * mm, "end": v(-25.78, 38.54) * mm});
            skLineSegment(sketch, "E1658", {"start": v(-25.78, 38.54) * mm, "end": v(-25.87, 38.67) * mm});
            skLineSegment(sketch, "E1659", {"start": v(-25.87, 38.67) * mm, "end": v(-25.95, 38.8) * mm});
            skLineSegment(sketch, "E1660", {"start": v(-25.95, 38.8) * mm, "end": v(-26.04, 38.94) * mm});
            skLineSegment(sketch, "E1661", {"start": v(-26.04, 38.94) * mm, "end": v(-26.12, 39.07) * mm});
            skLineSegment(sketch, "E1662", {"start": v(-26.12, 39.07) * mm, "end": v(-26.21, 39.2) * mm});
            skLineSegment(sketch, "E1663", {"start": v(-26.21, 39.2) * mm, "end": v(-26.3, 39.34) * mm});
            skLineSegment(sketch, "E1664", {"start": v(-26.3, 39.34) * mm, "end": v(-26.38, 39.47) * mm});
            skLineSegment(sketch, "E1665", {"start": v(-26.38, 39.47) * mm, "end": v(-26.47, 39.6) * mm});
            skLineSegment(sketch, "E1666", {"start": v(-26.47, 39.6) * mm, "end": v(-26.56, 39.74) * mm});
            skLineSegment(sketch, "E1667", {"start": v(-26.56, 39.74) * mm, "end": v(-26.64, 39.87) * mm});
            skLineSegment(sketch, "E1668", {"start": v(-26.64, 39.87) * mm, "end": v(-26.73, 40) * mm});
            skLineSegment(sketch, "E1669", {"start": v(-26.73, 40) * mm, "end": v(-26.82, 40.14) * mm});
            skLineSegment(sketch, "E1670", {"start": v(-26.82, 40.14) * mm, "end": v(-26.91, 40.28) * mm});
            skLineSegment(sketch, "E1671", {"start": v(-26.91, 40.28) * mm, "end": v(-27.02, 40.4) * mm});
            skLineSegment(sketch, "E1672", {"start": v(-27.02, 40.4) * mm, "end": v(-27.16, 40.48) * mm});
            skLineSegment(sketch, "E1673", {"start": v(-27.16, 40.48) * mm, "end": v(-27.32, 40.53) * mm});
            skLineSegment(sketch, "E1674", {"start": v(-27.32, 40.53) * mm, "end": v(-27.42, 40.54) * mm});
            skLineSegment(sketch, "E1675", {"start": v(-27.42, 40.54) * mm, "end": v(-27.58, 40.51) * mm});
            skLineSegment(sketch, "E1676", {"start": v(-27.58, 40.51) * mm, "end": v(-27.73, 40.45) * mm});
            skLineSegment(sketch, "E1677", {"start": v(-27.73, 40.45) * mm, "end": v(-27.86, 40.35) * mm});
            skLineSegment(sketch, "E1678", {"start": v(-27.86, 40.35) * mm, "end": v(-27.96, 40.21) * mm});
            skLineSegment(sketch, "E1679", {"start": v(-27.96, 40.21) * mm, "end": v(-28.02, 40.06) * mm});
            skLineSegment(sketch, "E1680", {"start": v(-28.02, 40.06) * mm, "end": v(-28.04, 39.9) * mm});
            skLineSegment(sketch, "E1681", {"start": v(-28.04, 39.9) * mm, "end": v(-28.01, 39.74) * mm});
            skLineSegment(sketch, "E1682", {"start": v(-28.01, 39.74) * mm, "end": v(-27.95, 39.59) * mm});
            skLineSegment(sketch, "E1683", {"start": v(-27.95, 39.59) * mm, "end": v(-27.85, 39.45) * mm});
            skLineSegment(sketch, "E1684", {"start": v(-27.85, 39.45) * mm, "end": v(-27.77, 39.32) * mm});
            skLineSegment(sketch, "E1685", {"start": v(-27.77, 39.32) * mm, "end": v(-27.68, 39.19) * mm});
            skLineSegment(sketch, "E1686", {"start": v(-27.68, 39.19) * mm, "end": v(-27.58, 39.05) * mm});
            skLineSegment(sketch, "E1687", {"start": v(-27.58, 39.05) * mm, "end": v(-27.5, 38.93) * mm});
            skLineSegment(sketch, "E1688", {"start": v(-27.5, 38.93) * mm, "end": v(-27.4, 38.8) * mm});
            skLineSegment(sketch, "E1689", {"start": v(-27.4, 38.8) * mm, "end": v(-27.31, 38.66) * mm});
            skLineSegment(sketch, "E1690", {"start": v(-27.31, 38.66) * mm, "end": v(-27.23, 38.53) * mm});
            skLineSegment(sketch, "E1691", {"start": v(-27.23, 38.53) * mm, "end": v(-27.14, 38.4) * mm});
            skLineSegment(sketch, "E1692", {"start": v(-27.14, 38.4) * mm, "end": v(-27.05, 38.27) * mm});
            skLineSegment(sketch, "E1693", {"start": v(-27.05, 38.27) * mm, "end": v(-26.96, 38.14) * mm});
            skLineSegment(sketch, "E1694", {"start": v(-26.96, 38.14) * mm, "end": v(-26.87, 38.01) * mm});
            skLineSegment(sketch, "E1695", {"start": v(-26.87, 38.01) * mm, "end": v(-26.78, 37.88) * mm});
            skLineSegment(sketch, "E1696", {"start": v(-26.78, 37.88) * mm, "end": v(-26.9, 37.79) * mm});
            skLineSegment(sketch, "E1697", {"start": v(-26.9, 37.79) * mm, "end": v(-27.03, 37.7) * mm});
            skLineSegment(sketch, "E1698", {"start": v(-27.03, 37.7) * mm, "end": v(-27.16, 37.6) * mm});
            skLineSegment(sketch, "E1699", {"start": v(-27.16, 37.6) * mm, "end": v(-27.29, 37.51) * mm});
            skLineSegment(sketch, "E1700", {"start": v(-27.29, 37.51) * mm, "end": v(-27.41, 37.42) * mm});
            skLineSegment(sketch, "E1701", {"start": v(-27.41, 37.42) * mm, "end": v(-27.54, 37.33) * mm});
            skLineSegment(sketch, "E1702", {"start": v(-27.54, 37.33) * mm, "end": v(-27.67, 37.24) * mm});
            skLineSegment(sketch, "E1703", {"start": v(-27.67, 37.24) * mm, "end": v(-27.8, 37.14) * mm});
            skLineSegment(sketch, "E1704", {"start": v(-27.8, 37.14) * mm, "end": v(-27.93, 37.05) * mm});
            skLineSegment(sketch, "E1705", {"start": v(-27.93, 37.05) * mm, "end": v(-28.05, 36.96) * mm});
            skLineSegment(sketch, "E1706", {"start": v(-28.05, 36.96) * mm, "end": v(-28.18, 36.87) * mm});
            skLineSegment(sketch, "E1707", {"start": v(-28.18, 36.87) * mm, "end": v(-28.25, 36.82) * mm});
            skLineSegment(sketch, "E1708", {"start": v(-28.25, 36.82) * mm, "end": v(-28.34, 36.95) * mm});
            skLineSegment(sketch, "E1709", {"start": v(-28.34, 36.95) * mm, "end": v(-28.44, 37.07) * mm});
            skLineSegment(sketch, "E1710", {"start": v(-28.44, 37.07) * mm, "end": v(-28.53, 37.2) * mm});
            skLineSegment(sketch, "E1711", {"start": v(-28.53, 37.2) * mm, "end": v(-28.63, 37.33) * mm});
            skLineSegment(sketch, "E1712", {"start": v(-28.63, 37.33) * mm, "end": v(-28.72, 37.46) * mm});
            skLineSegment(sketch, "E1713", {"start": v(-28.72, 37.46) * mm, "end": v(-28.82, 37.59) * mm});
            skLineSegment(sketch, "E1714", {"start": v(-28.82, 37.59) * mm, "end": v(-28.91, 37.71) * mm});
            skLineSegment(sketch, "E1715", {"start": v(-28.91, 37.71) * mm, "end": v(-29, 37.84) * mm});
            skLineSegment(sketch, "E1716", {"start": v(-29, 37.84) * mm, "end": v(-29.1, 37.97) * mm});
            skLineSegment(sketch, "E1717", {"start": v(-29.1, 37.97) * mm, "end": v(-29.2, 38.1) * mm});
            skLineSegment(sketch, "E1718", {"start": v(-29.2, 38.1) * mm, "end": v(-29.3, 38.22) * mm});
            skLineSegment(sketch, "E1719", {"start": v(-29.3, 38.22) * mm, "end": v(-29.39, 38.35) * mm});
            skLineSegment(sketch, "E1720", {"start": v(-29.39, 38.35) * mm, "end": v(-29.49, 38.48) * mm});
            skLineSegment(sketch, "E1721", {"start": v(-29.49, 38.48) * mm, "end": v(-29.6, 38.6) * mm});
            skLineSegment(sketch, "E1722", {"start": v(-29.6, 38.6) * mm, "end": v(-29.76, 38.67) * mm});
            skLineSegment(sketch, "E1723", {"start": v(-29.76, 38.67) * mm, "end": v(-29.92, 38.7) * mm});
            skLineSegment(sketch, "E1724", {"start": v(-29.92, 38.7) * mm, "end": v(-29.98, 38.7) * mm});
            skLineSegment(sketch, "E1725", {"start": v(-29.98, 38.7) * mm, "end": v(-30.14, 38.68) * mm});
            skLineSegment(sketch, "E1726", {"start": v(-30.14, 38.68) * mm, "end": v(-30.3, 38.61) * mm});
            skLineSegment(sketch, "E1727", {"start": v(-30.3, 38.61) * mm, "end": v(-30.42, 38.51) * mm});
            skLineSegment(sketch, "E1728", {"start": v(-30.42, 38.51) * mm, "end": v(-30.52, 38.38) * mm});
            skLineSegment(sketch, "E1729", {"start": v(-30.52, 38.38) * mm, "end": v(-30.58, 38.22) * mm});
            skLineSegment(sketch, "E1730", {"start": v(-30.58, 38.22) * mm, "end": v(-30.6, 38.06) * mm});
            skLineSegment(sketch, "E1731", {"start": v(-30.6, 38.06) * mm, "end": v(-30.57, 37.9) * mm});
            skLineSegment(sketch, "E1732", {"start": v(-30.57, 37.9) * mm, "end": v(-30.5, 37.75) * mm});
            skLineSegment(sketch, "E1733", {"start": v(-30.5, 37.75) * mm, "end": v(-30.4, 37.63) * mm});
            skLineSegment(sketch, "E1734", {"start": v(-30.4, 37.63) * mm, "end": v(-30.3, 37.5) * mm});
            skLineSegment(sketch, "E1735", {"start": v(-30.3, 37.5) * mm, "end": v(-30.2, 37.38) * mm});
            skLineSegment(sketch, "E1736", {"start": v(-30.2, 37.38) * mm, "end": v(-30.11, 37.25) * mm});
            skLineSegment(sketch, "E1737", {"start": v(-30.11, 37.25) * mm, "end": v(-30.01, 37.13) * mm});
            skLineSegment(sketch, "E1738", {"start": v(-30.01, 37.13) * mm, "end": v(-29.91, 37) * mm});
            skLineSegment(sketch, "E1739", {"start": v(-29.91, 37) * mm, "end": v(-29.82, 36.88) * mm});
            skLineSegment(sketch, "E1740", {"start": v(-29.82, 36.88) * mm, "end": v(-29.72, 36.76) * mm});
            skLineSegment(sketch, "E1741", {"start": v(-29.72, 36.76) * mm, "end": v(-29.62, 36.63) * mm});
            skLineSegment(sketch, "E1742", {"start": v(-29.62, 36.63) * mm, "end": v(-29.52, 36.5) * mm});
            skLineSegment(sketch, "E1743", {"start": v(-29.52, 36.5) * mm, "end": v(-29.42, 36.38) * mm});
            skLineSegment(sketch, "E1744", {"start": v(-29.42, 36.38) * mm, "end": v(-29.32, 36.25) * mm});
            skLineSegment(sketch, "E1745", {"start": v(-29.32, 36.25) * mm, "end": v(-29.23, 36.13) * mm});
            skLineSegment(sketch, "E1746", {"start": v(-29.23, 36.13) * mm, "end": v(-29.2, 36.1) * mm});
            skLineSegment(sketch, "E1747", {"start": v(-29.2, 36.1) * mm, "end": v(-29.32, 36) * mm});
            skLineSegment(sketch, "E1748", {"start": v(-29.32, 36) * mm, "end": v(-29.44, 35.9) * mm});
            skLineSegment(sketch, "E1749", {"start": v(-29.44, 35.9) * mm, "end": v(-29.56, 35.8) * mm});
            skLineSegment(sketch, "E1750", {"start": v(-29.56, 35.8) * mm, "end": v(-29.68, 35.7) * mm});
            skLineSegment(sketch, "E1751", {"start": v(-29.68, 35.7) * mm, "end": v(-29.8, 35.6) * mm});
            skLineSegment(sketch, "E1752", {"start": v(-29.8, 35.6) * mm, "end": v(-29.93, 35.5) * mm});
            skLineSegment(sketch, "E1753", {"start": v(-29.93, 35.5) * mm, "end": v(-30.05, 35.4) * mm});
            skLineSegment(sketch, "E1754", {"start": v(-30.05, 35.4) * mm, "end": v(-30.17, 35.3) * mm});
            skLineSegment(sketch, "E1755", {"start": v(-30.17, 35.3) * mm, "end": v(-30.3, 35.2) * mm});
            skLineSegment(sketch, "E1756", {"start": v(-30.3, 35.2) * mm, "end": v(-30.41, 35.1) * mm});
            skLineSegment(sketch, "E1757", {"start": v(-30.41, 35.1) * mm, "end": v(-30.53, 35) * mm});
            skLineSegment(sketch, "E1758", {"start": v(-30.53, 35) * mm, "end": v(-30.6, 34.95) * mm});
            skLineSegment(sketch, "E1759", {"start": v(-30.6, 34.95) * mm, "end": v(-30.7, 35.07) * mm});
            skLineSegment(sketch, "E1760", {"start": v(-30.7, 35.07) * mm, "end": v(-30.8, 35.18) * mm});
            skLineSegment(sketch, "E1761", {"start": v(-30.8, 35.18) * mm, "end": v(-30.9, 35.3) * mm});
            skLineSegment(sketch, "E1762", {"start": v(-30.9, 35.3) * mm, "end": v(-31, 35.43) * mm});
            skLineSegment(sketch, "E1763", {"start": v(-31, 35.43) * mm, "end": v(-31.11, 35.55) * mm});
            skLineSegment(sketch, "E1764", {"start": v(-31.11, 35.55) * mm, "end": v(-31.22, 35.67) * mm});
            skLineSegment(sketch, "E1765", {"start": v(-31.22, 35.67) * mm, "end": v(-31.32, 35.79) * mm});
            skLineSegment(sketch, "E1766", {"start": v(-31.32, 35.79) * mm, "end": v(-31.42, 35.9) * mm});
            skLineSegment(sketch, "E1767", {"start": v(-31.42, 35.9) * mm, "end": v(-31.52, 36.03) * mm});
            skLineSegment(sketch, "E1768", {"start": v(-31.52, 36.03) * mm, "end": v(-31.63, 36.15) * mm});
            skLineSegment(sketch, "E1769", {"start": v(-31.63, 36.15) * mm, "end": v(-31.73, 36.27) * mm});
            skLineSegment(sketch, "E1770", {"start": v(-31.73, 36.27) * mm, "end": v(-31.83, 36.4) * mm});
            skLineSegment(sketch, "E1771", {"start": v(-31.83, 36.4) * mm, "end": v(-31.94, 36.52) * mm});
            skLineSegment(sketch, "E1772", {"start": v(-31.94, 36.52) * mm, "end": v(-32.07, 36.62) * mm});
            skLineSegment(sketch, "E1773", {"start": v(-32.07, 36.62) * mm, "end": v(-32.22, 36.69) * mm});
            skLineSegment(sketch, "E1774", {"start": v(-32.22, 36.69) * mm, "end": v(-32.38, 36.71) * mm});
            skLineSegment(sketch, "E1775", {"start": v(-32.38, 36.71) * mm, "end": v(-32.55, 36.7) * mm});
            skLineSegment(sketch, "E1776", {"start": v(-32.55, 36.7) * mm, "end": v(-32.7, 36.63) * mm});
            skLineSegment(sketch, "E1777", {"start": v(-32.7, 36.63) * mm, "end": v(-32.83, 36.54) * mm});
            skLineSegment(sketch, "E1778", {"start": v(-32.83, 36.54) * mm, "end": v(-32.93, 36.4) * mm});
            skLineSegment(sketch, "E1779", {"start": v(-32.93, 36.4) * mm, "end": v(-33, 36.26) * mm});
            skLineSegment(sketch, "E1780", {"start": v(-33, 36.26) * mm, "end": v(-33.02, 36.1) * mm});
            skLineSegment(sketch, "E1781", {"start": v(-33.02, 36.1) * mm, "end": v(-33, 35.93) * mm});
            skLineSegment(sketch, "E1782", {"start": v(-33, 35.93) * mm, "end": v(-32.94, 35.78) * mm});
            skLineSegment(sketch, "E1783", {"start": v(-32.94, 35.78) * mm, "end": v(-32.84, 35.65) * mm});
            skLineSegment(sketch, "E1784", {"start": v(-32.84, 35.65) * mm, "end": v(-32.74, 35.54) * mm});
            skLineSegment(sketch, "E1785", {"start": v(-32.74, 35.54) * mm, "end": v(-32.63, 35.42) * mm});
            skLineSegment(sketch, "E1786", {"start": v(-32.63, 35.42) * mm, "end": v(-32.53, 35.3) * mm});
            skLineSegment(sketch, "E1787", {"start": v(-32.53, 35.3) * mm, "end": v(-32.42, 35.19) * mm});
            skLineSegment(sketch, "E1788", {"start": v(-32.42, 35.19) * mm, "end": v(-32.32, 35.07) * mm});
            skLineSegment(sketch, "E1789", {"start": v(-32.32, 35.07) * mm, "end": v(-32.21, 34.95) * mm});
            skLineSegment(sketch, "E1790", {"start": v(-32.21, 34.95) * mm, "end": v(-32.1, 34.83) * mm});
            skLineSegment(sketch, "E1791", {"start": v(-32.1, 34.83) * mm, "end": v(-32, 34.71) * mm});
            skLineSegment(sketch, "E1792", {"start": v(-32, 34.71) * mm, "end": v(-31.9, 34.6) * mm});
            skLineSegment(sketch, "E1793", {"start": v(-31.9, 34.6) * mm, "end": v(-31.79, 34.48) * mm});
            skLineSegment(sketch, "E1794", {"start": v(-31.79, 34.48) * mm, "end": v(-31.68, 34.36) * mm});
            skLineSegment(sketch, "E1795", {"start": v(-31.68, 34.36) * mm, "end": v(-31.57, 34.24) * mm});
            skLineSegment(sketch, "E1796", {"start": v(-31.57, 34.24) * mm, "end": v(-31.5, 34.16) * mm});
            skLineSegment(sketch, "E1797", {"start": v(-31.5, 34.16) * mm, "end": v(-31.61, 34.05) * mm});
            skLineSegment(sketch, "E1798", {"start": v(-31.61, 34.05) * mm, "end": v(-31.73, 33.94) * mm});
            skLineSegment(sketch, "E1799", {"start": v(-31.73, 33.94) * mm, "end": v(-31.84, 33.83) * mm});
            skLineSegment(sketch, "E1800", {"start": v(-31.84, 33.83) * mm, "end": v(-31.96, 33.73) * mm});
            skLineSegment(sketch, "E1801", {"start": v(-31.96, 33.73) * mm, "end": v(-32.07, 33.62) * mm});
            skLineSegment(sketch, "E1802", {"start": v(-32.07, 33.62) * mm, "end": v(-32.19, 33.51) * mm});
            skLineSegment(sketch, "E1803", {"start": v(-32.19, 33.51) * mm, "end": v(-32.3, 33.4) * mm});
            skLineSegment(sketch, "E1804", {"start": v(-32.3, 33.4) * mm, "end": v(-32.42, 33.3) * mm});
            skLineSegment(sketch, "E1805", {"start": v(-32.42, 33.3) * mm, "end": v(-32.53, 33.19) * mm});
            skLineSegment(sketch, "E1806", {"start": v(-32.53, 33.19) * mm, "end": v(-32.64, 33.08) * mm});
            skLineSegment(sketch, "E1807", {"start": v(-32.64, 33.08) * mm, "end": v(-32.76, 32.97) * mm});
            skLineSegment(sketch, "E1808", {"start": v(-32.76, 32.97) * mm, "end": v(-32.82, 32.92) * mm});
            skLineSegment(sketch, "E1809", {"start": v(-32.82, 32.92) * mm, "end": v(-32.93, 33.03) * mm});
            skLineSegment(sketch, "E1810", {"start": v(-32.93, 33.03) * mm, "end": v(-33.04, 33.14) * mm});
            skLineSegment(sketch, "E1811", {"start": v(-33.04, 33.14) * mm, "end": v(-33.15, 33.26) * mm});
            skLineSegment(sketch, "E1812", {"start": v(-33.15, 33.26) * mm, "end": v(-33.26, 33.37) * mm});
            skLineSegment(sketch, "E1813", {"start": v(-33.26, 33.37) * mm, "end": v(-33.37, 33.48) * mm});
            skLineSegment(sketch, "E1814", {"start": v(-33.37, 33.48) * mm, "end": v(-33.48, 33.6) * mm});
            skLineSegment(sketch, "E1815", {"start": v(-33.48, 33.6) * mm, "end": v(-33.6, 33.71) * mm});
            skLineSegment(sketch, "E1816", {"start": v(-33.6, 33.71) * mm, "end": v(-33.7, 33.83) * mm});
            skLineSegment(sketch, "E1817", {"start": v(-33.7, 33.83) * mm, "end": v(-33.82, 33.94) * mm});
            skLineSegment(sketch, "E1818", {"start": v(-33.82, 33.94) * mm, "end": v(-33.92, 34.05) * mm});
            skLineSegment(sketch, "E1819", {"start": v(-33.92, 34.05) * mm, "end": v(-34.03, 34.17) * mm});
            skLineSegment(sketch, "E1820", {"start": v(-34.03, 34.17) * mm, "end": v(-34.15, 34.28) * mm});
            skLineSegment(sketch, "E1821", {"start": v(-34.15, 34.28) * mm, "end": v(-34.27, 34.4) * mm});
            skLineSegment(sketch, "E1822", {"start": v(-34.27, 34.4) * mm, "end": v(-34.4, 34.5) * mm});
            skLineSegment(sketch, "E1823", {"start": v(-34.4, 34.5) * mm, "end": v(-34.55, 34.55) * mm});
            skLineSegment(sketch, "E1824", {"start": v(-34.55, 34.55) * mm, "end": v(-34.69, 34.57) * mm});
            skLineSegment(sketch, "E1825", {"start": v(-34.69, 34.57) * mm, "end": v(-34.85, 34.54) * mm});
            skLineSegment(sketch, "E1826", {"start": v(-34.85, 34.54) * mm, "end": v(-35, 34.48) * mm});
            skLineSegment(sketch, "E1827", {"start": v(-35, 34.48) * mm, "end": v(-35.13, 34.38) * mm});
            skLineSegment(sketch, "E1828", {"start": v(-35.13, 34.38) * mm, "end": v(-35.23, 34.25) * mm});
            skLineSegment(sketch, "E1829", {"start": v(-35.23, 34.25) * mm, "end": v(-35.3, 34.1) * mm});
            skLineSegment(sketch, "E1830", {"start": v(-35.3, 34.1) * mm, "end": v(-35.31, 33.94) * mm});
            skLineSegment(sketch, "E1831", {"start": v(-35.31, 33.94) * mm, "end": v(-35.3, 33.78) * mm});
            skLineSegment(sketch, "E1832", {"start": v(-35.3, 33.78) * mm, "end": v(-35.23, 33.63) * mm});
            skLineSegment(sketch, "E1833", {"start": v(-35.23, 33.63) * mm, "end": v(-35.13, 33.5) * mm});
            skLineSegment(sketch, "E1834", {"start": v(-35.13, 33.5) * mm, "end": v(-35.01, 33.39) * mm});
            skLineSegment(sketch, "E1835", {"start": v(-35.01, 33.39) * mm, "end": v(-34.9, 33.28) * mm});
            skLineSegment(sketch, "E1836", {"start": v(-34.9, 33.28) * mm, "end": v(-34.79, 33.16) * mm});
            skLineSegment(sketch, "E1837", {"start": v(-34.79, 33.16) * mm, "end": v(-34.67, 33.05) * mm});
            skLineSegment(sketch, "E1838", {"start": v(-34.67, 33.05) * mm, "end": v(-34.56, 32.94) * mm});
            skLineSegment(sketch, "E1839", {"start": v(-34.56, 32.94) * mm, "end": v(-34.44, 32.83) * mm});
            skLineSegment(sketch, "E1840", {"start": v(-34.44, 32.83) * mm, "end": v(-34.33, 32.72) * mm});
            skLineSegment(sketch, "E1841", {"start": v(-34.33, 32.72) * mm, "end": v(-34.22, 32.61) * mm});
            skLineSegment(sketch, "E1842", {"start": v(-34.22, 32.61) * mm, "end": v(-34.1, 32.5) * mm});
            skLineSegment(sketch, "E1843", {"start": v(-34.1, 32.5) * mm, "end": v(-34, 32.39) * mm});
            skLineSegment(sketch, "E1844", {"start": v(-34, 32.39) * mm, "end": v(-33.88, 32.28) * mm});
            skLineSegment(sketch, "E1845", {"start": v(-33.88, 32.28) * mm, "end": v(-33.76, 32.17) * mm});
            skLineSegment(sketch, "E1846", {"start": v(-33.76, 32.17) * mm, "end": v(-33.67, 32.07) * mm});
            skLineSegment(sketch, "E1847", {"start": v(-33.67, 32.07) * mm, "end": v(-33.77, 31.96) * mm});
            skLineSegment(sketch, "E1848", {"start": v(-33.77, 31.96) * mm, "end": v(-33.88, 31.84) * mm});
            skLineSegment(sketch, "E1849", {"start": v(-33.88, 31.84) * mm, "end": v(-33.99, 31.73) * mm});
            skLineSegment(sketch, "E1850", {"start": v(-33.99, 31.73) * mm, "end": v(-34.1, 31.61) * mm});
            skLineSegment(sketch, "E1851", {"start": v(-34.1, 31.61) * mm, "end": v(-34.2, 31.5) * mm});
            skLineSegment(sketch, "E1852", {"start": v(-34.2, 31.5) * mm, "end": v(-34.31, 31.38) * mm});
            skLineSegment(sketch, "E1853", {"start": v(-34.31, 31.38) * mm, "end": v(-34.42, 31.27) * mm});
            skLineSegment(sketch, "E1854", {"start": v(-34.42, 31.27) * mm, "end": v(-34.53, 31.15) * mm});
            skLineSegment(sketch, "E1855", {"start": v(-34.53, 31.15) * mm, "end": v(-34.63, 31.04) * mm});
            skLineSegment(sketch, "E1856", {"start": v(-34.63, 31.04) * mm, "end": v(-34.74, 30.92) * mm});
            skLineSegment(sketch, "E1857", {"start": v(-34.74, 30.92) * mm, "end": v(-34.85, 30.8) * mm});
            skLineSegment(sketch, "E1858", {"start": v(-34.85, 30.8) * mm, "end": v(-34.9, 30.75) * mm});
            skLineSegment(sketch, "E1859", {"start": v(-34.9, 30.75) * mm, "end": v(-35.02, 30.86) * mm});
            skLineSegment(sketch, "E1860", {"start": v(-35.02, 30.86) * mm, "end": v(-35.14, 30.96) * mm});
            skLineSegment(sketch, "E1861", {"start": v(-35.14, 30.96) * mm, "end": v(-35.26, 31.07) * mm});
            skLineSegment(sketch, "E1862", {"start": v(-35.26, 31.07) * mm, "end": v(-35.37, 31.17) * mm});
            skLineSegment(sketch, "E1863", {"start": v(-35.37, 31.17) * mm, "end": v(-35.5, 31.28) * mm});
            skLineSegment(sketch, "E1864", {"start": v(-35.5, 31.28) * mm, "end": v(-35.61, 31.39) * mm});
            skLineSegment(sketch, "E1865", {"start": v(-35.61, 31.39) * mm, "end": v(-35.73, 31.5) * mm});
            skLineSegment(sketch, "E1866", {"start": v(-35.73, 31.5) * mm, "end": v(-35.84, 31.6) * mm});
            skLineSegment(sketch, "E1867", {"start": v(-35.84, 31.6) * mm, "end": v(-35.96, 31.7) * mm});
            skLineSegment(sketch, "E1868", {"start": v(-35.96, 31.7) * mm, "end": v(-36.08, 31.81) * mm});
            skLineSegment(sketch, "E1869", {"start": v(-36.08, 31.81) * mm, "end": v(-36.2, 31.92) * mm});
            skLineSegment(sketch, "E1870", {"start": v(-36.2, 31.92) * mm, "end": v(-36.32, 32.02) * mm});
            skLineSegment(sketch, "E1871", {"start": v(-36.32, 32.02) * mm, "end": v(-36.44, 32.14) * mm});
            skLineSegment(sketch, "E1872", {"start": v(-36.44, 32.14) * mm, "end": v(-36.58, 32.22) * mm});
            skLineSegment(sketch, "E1873", {"start": v(-36.58, 32.22) * mm, "end": v(-36.74, 32.27) * mm});
            skLineSegment(sketch, "E1874", {"start": v(-36.74, 32.27) * mm, "end": v(-36.84, 32.27) * mm});
            skLineSegment(sketch, "E1875", {"start": v(-36.84, 32.27) * mm, "end": v(-37, 32.25) * mm});
            skLineSegment(sketch, "E1876", {"start": v(-37, 32.25) * mm, "end": v(-37.15, 32.19) * mm});
            skLineSegment(sketch, "E1877", {"start": v(-37.15, 32.19) * mm, "end": v(-37.28, 32.08) * mm});
            skLineSegment(sketch, "E1878", {"start": v(-37.28, 32.08) * mm, "end": v(-37.38, 31.95) * mm});
            skLineSegment(sketch, "E1879", {"start": v(-37.38, 31.95) * mm, "end": v(-37.44, 31.8) * mm});
            skLineSegment(sketch, "E1880", {"start": v(-37.44, 31.8) * mm, "end": v(-37.46, 31.64) * mm});
            skLineSegment(sketch, "E1881", {"start": v(-37.46, 31.64) * mm, "end": v(-37.44, 31.48) * mm});
            skLineSegment(sketch, "E1882", {"start": v(-37.44, 31.48) * mm, "end": v(-37.37, 31.33) * mm});
            skLineSegment(sketch, "E1883", {"start": v(-37.37, 31.33) * mm, "end": v(-37.27, 31.2) * mm});
            skLineSegment(sketch, "E1884", {"start": v(-37.27, 31.2) * mm, "end": v(-37.14, 31.09) * mm});
            skLineSegment(sketch, "E1885", {"start": v(-37.14, 31.09) * mm, "end": v(-37.02, 30.98) * mm});
            skLineSegment(sketch, "E1886", {"start": v(-37.02, 30.98) * mm, "end": v(-36.9, 30.88) * mm});
            skLineSegment(sketch, "E1887", {"start": v(-36.9, 30.88) * mm, "end": v(-36.78, 30.78) * mm});
            skLineSegment(sketch, "E1888", {"start": v(-36.78, 30.78) * mm, "end": v(-36.66, 30.68) * mm});
            skLineSegment(sketch, "E1889", {"start": v(-36.66, 30.68) * mm, "end": v(-36.54, 30.57) * mm});
            skLineSegment(sketch, "E1890", {"start": v(-36.54, 30.57) * mm, "end": v(-36.42, 30.47) * mm});
            skLineSegment(sketch, "E1891", {"start": v(-36.42, 30.47) * mm, "end": v(-36.3, 30.37) * mm});
            skLineSegment(sketch, "E1892", {"start": v(-36.3, 30.37) * mm, "end": v(-36.18, 30.26) * mm});
            skLineSegment(sketch, "E1893", {"start": v(-36.18, 30.26) * mm, "end": v(-36.05, 30.16) * mm});
            skLineSegment(sketch, "E1894", {"start": v(-36.05, 30.16) * mm, "end": v(-35.93, 30.06) * mm});
            skLineSegment(sketch, "E1895", {"start": v(-35.93, 30.06) * mm, "end": v(-35.82, 29.95) * mm});
            skLineSegment(sketch, "E1896", {"start": v(-35.82, 29.95) * mm, "end": v(-35.7, 29.85) * mm});
            skLineSegment(sketch, "E1897", {"start": v(-35.7, 29.85) * mm, "end": v(-35.8, 29.73) * mm});
            skLineSegment(sketch, "E1898", {"start": v(-35.8, 29.73) * mm, "end": v(-35.9, 29.6) * mm});
            skLineSegment(sketch, "E1899", {"start": v(-35.9, 29.6) * mm, "end": v(-36, 29.49) * mm});
            skLineSegment(sketch, "E1900", {"start": v(-36, 29.49) * mm, "end": v(-36.1, 29.36) * mm});
            skLineSegment(sketch, "E1901", {"start": v(-36.1, 29.36) * mm, "end": v(-36.2, 29.24) * mm});
            skLineSegment(sketch, "E1902", {"start": v(-36.2, 29.24) * mm, "end": v(-36.3, 29.12) * mm});
            skLineSegment(sketch, "E1903", {"start": v(-36.3, 29.12) * mm, "end": v(-36.4, 29) * mm});
            skLineSegment(sketch, "E1904", {"start": v(-36.4, 29) * mm, "end": v(-36.5, 28.88) * mm});
            skLineSegment(sketch, "E1905", {"start": v(-36.5, 28.88) * mm, "end": v(-36.6, 28.76) * mm});
            skLineSegment(sketch, "E1906", {"start": v(-36.6, 28.76) * mm, "end": v(-36.69, 28.63) * mm});
            skLineSegment(sketch, "E1907", {"start": v(-36.69, 28.63) * mm, "end": v(-36.79, 28.51) * mm});
            skLineSegment(sketch, "E1908", {"start": v(-36.79, 28.51) * mm, "end": v(-36.84, 28.45) * mm});
            skLineSegment(sketch, "E1909", {"start": v(-36.84, 28.45) * mm, "end": v(-36.96, 28.55) * mm});
            skLineSegment(sketch, "E1910", {"start": v(-36.96, 28.55) * mm, "end": v(-37.09, 28.65) * mm});
            skLineSegment(sketch, "E1911", {"start": v(-37.09, 28.65) * mm, "end": v(-37.21, 28.75) * mm});
            skLineSegment(sketch, "E1912", {"start": v(-37.21, 28.75) * mm, "end": v(-37.34, 28.84) * mm});
            skLineSegment(sketch, "E1913", {"start": v(-37.34, 28.84) * mm, "end": v(-37.46, 28.94) * mm});
            skLineSegment(sketch, "E1914", {"start": v(-37.46, 28.94) * mm, "end": v(-37.59, 29.04) * mm});
            skLineSegment(sketch, "E1915", {"start": v(-37.59, 29.04) * mm, "end": v(-37.71, 29.14) * mm});
            skLineSegment(sketch, "E1916", {"start": v(-37.71, 29.14) * mm, "end": v(-37.84, 29.23) * mm});
            skLineSegment(sketch, "E1917", {"start": v(-37.84, 29.23) * mm, "end": v(-37.96, 29.33) * mm});
            skLineSegment(sketch, "E1918", {"start": v(-37.96, 29.33) * mm, "end": v(-38.09, 29.43) * mm});
            skLineSegment(sketch, "E1919", {"start": v(-38.09, 29.43) * mm, "end": v(-38.2, 29.53) * mm});
            skLineSegment(sketch, "E1920", {"start": v(-38.2, 29.53) * mm, "end": v(-38.34, 29.63) * mm});
            skLineSegment(sketch, "E1921", {"start": v(-38.34, 29.63) * mm, "end": v(-38.47, 29.73) * mm});
            skLineSegment(sketch, "E1922", {"start": v(-38.47, 29.73) * mm, "end": v(-38.62, 29.8) * mm});
            skLineSegment(sketch, "E1923", {"start": v(-38.62, 29.8) * mm, "end": v(-38.78, 29.84) * mm});
            skLineSegment(sketch, "E1924", {"start": v(-38.78, 29.84) * mm, "end": v(-38.84, 29.85) * mm});
            skLineSegment(sketch, "E1925", {"start": v(-38.84, 29.85) * mm, "end": v(-39, 29.82) * mm});
            skLineSegment(sketch, "E1926", {"start": v(-39, 29.82) * mm, "end": v(-39.15, 29.75) * mm});
            skLineSegment(sketch, "E1927", {"start": v(-39.15, 29.75) * mm, "end": v(-39.28, 29.65) * mm});
            skLineSegment(sketch, "E1928", {"start": v(-39.28, 29.65) * mm, "end": v(-39.38, 29.52) * mm});
            skLineSegment(sketch, "E1929", {"start": v(-39.38, 29.52) * mm, "end": v(-39.44, 29.36) * mm});
            skLineSegment(sketch, "E1930", {"start": v(-39.44, 29.36) * mm, "end": v(-39.45, 29.2) * mm});
            skLineSegment(sketch, "E1931", {"start": v(-39.45, 29.2) * mm, "end": v(-39.43, 29.04) * mm});
            skLineSegment(sketch, "E1932", {"start": v(-39.43, 29.04) * mm, "end": v(-39.36, 28.9) * mm});
            skLineSegment(sketch, "E1933", {"start": v(-39.36, 28.9) * mm, "end": v(-39.25, 28.76) * mm});
            skLineSegment(sketch, "E1934", {"start": v(-39.25, 28.76) * mm, "end": v(-39.13, 28.67) * mm});
            skLineSegment(sketch, "E1935", {"start": v(-39.13, 28.67) * mm, "end": v(-39, 28.57) * mm});
            skLineSegment(sketch, "E1936", {"start": v(-39, 28.57) * mm, "end": v(-38.88, 28.48) * mm});
            skLineSegment(sketch, "E1937", {"start": v(-38.88, 28.48) * mm, "end": v(-38.75, 28.38) * mm});
            skLineSegment(sketch, "E1938", {"start": v(-38.75, 28.38) * mm, "end": v(-38.63, 28.29) * mm});
            skLineSegment(sketch, "E1939", {"start": v(-38.63, 28.29) * mm, "end": v(-38.5, 28.2) * mm});
            skLineSegment(sketch, "E1940", {"start": v(-38.5, 28.2) * mm, "end": v(-38.37, 28.1) * mm});
            skLineSegment(sketch, "E1941", {"start": v(-38.37, 28.1) * mm, "end": v(-38.24, 28) * mm});
            skLineSegment(sketch, "E1942", {"start": v(-38.24, 28) * mm, "end": v(-38.11, 27.9) * mm});
            skLineSegment(sketch, "E1943", {"start": v(-38.11, 27.9) * mm, "end": v(-37.99, 27.81) * mm});
            skLineSegment(sketch, "E1944", {"start": v(-37.99, 27.81) * mm, "end": v(-37.86, 27.72) * mm});
            skLineSegment(sketch, "E1945", {"start": v(-37.86, 27.72) * mm, "end": v(-37.73, 27.62) * mm});
            skLineSegment(sketch, "E1946", {"start": v(-37.73, 27.62) * mm, "end": v(-37.6, 27.53) * mm});
            skLineSegment(sketch, "E1947", {"start": v(-37.6, 27.53) * mm, "end": v(-37.57, 27.5) * mm});
            skLineSegment(sketch, "E1948", {"start": v(-37.57, 27.5) * mm, "end": v(-37.66, 27.37) * mm});
            skLineSegment(sketch, "E1949", {"start": v(-37.66, 27.37) * mm, "end": v(-37.75, 27.24) * mm});
            skLineSegment(sketch, "E1950", {"start": v(-37.75, 27.24) * mm, "end": v(-37.84, 27.12) * mm});
            skLineSegment(sketch, "E1951", {"start": v(-37.84, 27.12) * mm, "end": v(-37.94, 26.99) * mm});
            skLineSegment(sketch, "E1952", {"start": v(-37.94, 26.99) * mm, "end": v(-38.03, 26.86) * mm});
            skLineSegment(sketch, "E1953", {"start": v(-38.03, 26.86) * mm, "end": v(-38.12, 26.73) * mm});
            skLineSegment(sketch, "E1954", {"start": v(-38.12, 26.73) * mm, "end": v(-38.21, 26.6) * mm});
            skLineSegment(sketch, "E1955", {"start": v(-38.21, 26.6) * mm, "end": v(-38.3, 26.48) * mm});
            skLineSegment(sketch, "E1956", {"start": v(-38.3, 26.48) * mm, "end": v(-38.4, 26.35) * mm});
            skLineSegment(sketch, "E1957", {"start": v(-38.4, 26.35) * mm, "end": v(-38.49, 26.22) * mm});
            skLineSegment(sketch, "E1958", {"start": v(-38.49, 26.22) * mm, "end": v(-38.58, 26.1) * mm});
            skLineSegment(sketch, "E1959", {"start": v(-38.58, 26.1) * mm, "end": v(-38.62, 26.03) * mm});
            skLineSegment(sketch, "E1960", {"start": v(-38.62, 26.03) * mm, "end": v(-38.75, 26.12) * mm});
            skLineSegment(sketch, "E1961", {"start": v(-38.75, 26.12) * mm, "end": v(-38.88, 26.2) * mm});
            skLineSegment(sketch, "E1962", {"start": v(-38.88, 26.2) * mm, "end": v(-39.02, 26.3) * mm});
            skLineSegment(sketch, "E1963", {"start": v(-39.02, 26.3) * mm, "end": v(-39.15, 26.39) * mm});
            skLineSegment(sketch, "E1964", {"start": v(-39.15, 26.39) * mm, "end": v(-39.28, 26.48) * mm});
            skLineSegment(sketch, "E1965", {"start": v(-39.28, 26.48) * mm, "end": v(-39.4, 26.57) * mm});
            skLineSegment(sketch, "E1966", {"start": v(-39.4, 26.57) * mm, "end": v(-39.54, 26.66) * mm});
            skLineSegment(sketch, "E1967", {"start": v(-39.54, 26.66) * mm, "end": v(-39.67, 26.75) * mm});
            skLineSegment(sketch, "E1968", {"start": v(-39.67, 26.75) * mm, "end": v(-39.8, 26.84) * mm});
            skLineSegment(sketch, "E1969", {"start": v(-39.8, 26.84) * mm, "end": v(-39.93, 26.93) * mm});
            skLineSegment(sketch, "E1970", {"start": v(-39.93, 26.93) * mm, "end": v(-40.06, 27.02) * mm});
            skLineSegment(sketch, "E1971", {"start": v(-40.06, 27.02) * mm, "end": v(-40.2, 27.1) * mm});
            skLineSegment(sketch, "E1972", {"start": v(-40.2, 27.1) * mm, "end": v(-40.33, 27.2) * mm});
            skLineSegment(sketch, "E1973", {"start": v(-40.33, 27.2) * mm, "end": v(-40.48, 27.27) * mm});
            skLineSegment(sketch, "E1974", {"start": v(-40.48, 27.27) * mm, "end": v(-40.65, 27.3) * mm});
            skLineSegment(sketch, "E1975", {"start": v(-40.65, 27.3) * mm, "end": v(-40.8, 27.27) * mm});
            skLineSegment(sketch, "E1976", {"start": v(-40.8, 27.27) * mm, "end": v(-40.96, 27.21) * mm});
            skLineSegment(sketch, "E1977", {"start": v(-40.96, 27.21) * mm, "end": v(-41.1, 27.12) * mm});
            skLineSegment(sketch, "E1978", {"start": v(-41.1, 27.12) * mm, "end": v(-41.2, 26.99) * mm});
            skLineSegment(sketch, "E1979", {"start": v(-41.2, 26.99) * mm, "end": v(-41.26, 26.84) * mm});
            skLineSegment(sketch, "E1980", {"start": v(-41.26, 26.84) * mm, "end": v(-41.28, 26.67) * mm});
            skLineSegment(sketch, "E1981", {"start": v(-41.28, 26.67) * mm, "end": v(-41.26, 26.51) * mm});
            skLineSegment(sketch, "E1982", {"start": v(-41.26, 26.51) * mm, "end": v(-41.2, 26.36) * mm});
            skLineSegment(sketch, "E1983", {"start": v(-41.2, 26.36) * mm, "end": v(-41.1, 26.23) * mm});
            skLineSegment(sketch, "E1984", {"start": v(-41.1, 26.23) * mm, "end": v(-40.98, 26.13) * mm});
            skLineSegment(sketch, "E1985", {"start": v(-40.98, 26.13) * mm, "end": v(-40.85, 26.05) * mm});
            skLineSegment(sketch, "E1986", {"start": v(-40.85, 26.05) * mm, "end": v(-40.72, 25.96) * mm});
            skLineSegment(sketch, "E1987", {"start": v(-40.72, 25.96) * mm, "end": v(-40.58, 25.87) * mm});
            skLineSegment(sketch, "E1988", {"start": v(-40.58, 25.87) * mm, "end": v(-40.45, 25.79) * mm});
            skLineSegment(sketch, "E1989", {"start": v(-40.45, 25.79) * mm, "end": v(-40.32, 25.7) * mm});
            skLineSegment(sketch, "E1990", {"start": v(-40.32, 25.7) * mm, "end": v(-40.18, 25.61) * mm});
            skLineSegment(sketch, "E1991", {"start": v(-40.18, 25.61) * mm, "end": v(-40.05, 25.53) * mm});
            skLineSegment(sketch, "E1992", {"start": v(-40.05, 25.53) * mm, "end": v(-39.92, 25.44) * mm});
            skLineSegment(sketch, "E1993", {"start": v(-39.92, 25.44) * mm, "end": v(-39.79, 25.36) * mm});
            skLineSegment(sketch, "E1994", {"start": v(-39.79, 25.36) * mm, "end": v(-39.65, 25.27) * mm});
            skLineSegment(sketch, "E1995", {"start": v(-39.65, 25.27) * mm, "end": v(-39.52, 25.18) * mm});
            skLineSegment(sketch, "E1996", {"start": v(-39.52, 25.18) * mm, "end": v(-39.39, 25.1) * mm});
            skLineSegment(sketch, "E1997", {"start": v(-39.39, 25.1) * mm, "end": v(-39.29, 25.03) * mm});
            skLineSegment(sketch, "E1998", {"start": v(-39.29, 25.03) * mm, "end": v(-39.37, 24.9) * mm});
            skLineSegment(sketch, "E1999", {"start": v(-39.37, 24.9) * mm, "end": v(-39.46, 24.77) * mm});
            skLineSegment(sketch, "E2000", {"start": v(-39.46, 24.77) * mm, "end": v(-39.54, 24.63) * mm});
            skLineSegment(sketch, "E2001", {"start": v(-39.54, 24.63) * mm, "end": v(-39.62, 24.5) * mm});
            skLineSegment(sketch, "E2002", {"start": v(-39.62, 24.5) * mm, "end": v(-39.7, 24.37) * mm});
            skLineSegment(sketch, "E2003", {"start": v(-39.7, 24.37) * mm, "end": v(-39.79, 24.23) * mm});
            skLineSegment(sketch, "E2004", {"start": v(-39.79, 24.23) * mm, "end": v(-39.87, 24.1) * mm});
            skLineSegment(sketch, "E2005", {"start": v(-39.87, 24.1) * mm, "end": v(-39.95, 23.96) * mm});
            skLineSegment(sketch, "E2006", {"start": v(-39.95, 23.96) * mm, "end": v(-40.04, 23.83) * mm});
            skLineSegment(sketch, "E2007", {"start": v(-40.04, 23.83) * mm, "end": v(-40.12, 23.7) * mm});
            skLineSegment(sketch, "E2008", {"start": v(-40.12, 23.7) * mm, "end": v(-40.2, 23.56) * mm});
            skLineSegment(sketch, "E2009", {"start": v(-40.2, 23.56) * mm, "end": v(-40.25, 23.5) * mm});
            skLineSegment(sketch, "E2010", {"start": v(-40.25, 23.5) * mm, "end": v(-40.38, 23.58) * mm});
            skLineSegment(sketch, "E2011", {"start": v(-40.38, 23.58) * mm, "end": v(-40.52, 23.66) * mm});
            skLineSegment(sketch, "E2012", {"start": v(-40.52, 23.66) * mm, "end": v(-40.65, 23.74) * mm});
            skLineSegment(sketch, "E2013", {"start": v(-40.65, 23.74) * mm, "end": v(-40.79, 23.82) * mm});
            skLineSegment(sketch, "E2014", {"start": v(-40.79, 23.82) * mm, "end": v(-40.93, 23.9) * mm});
            skLineSegment(sketch, "E2015", {"start": v(-40.93, 23.9) * mm, "end": v(-41.06, 23.98) * mm});
            skLineSegment(sketch, "E2016", {"start": v(-41.06, 23.98) * mm, "end": v(-41.2, 24.06) * mm});
            skLineSegment(sketch, "E2017", {"start": v(-41.2, 24.06) * mm, "end": v(-41.33, 24.14) * mm});
            skLineSegment(sketch, "E2018", {"start": v(-41.33, 24.14) * mm, "end": v(-41.47, 24.23) * mm});
            skLineSegment(sketch, "E2019", {"start": v(-41.47, 24.23) * mm, "end": v(-41.6, 24.3) * mm});
            skLineSegment(sketch, "E2020", {"start": v(-41.6, 24.3) * mm, "end": v(-41.74, 24.39) * mm});
            skLineSegment(sketch, "E2021", {"start": v(-41.74, 24.39) * mm, "end": v(-41.88, 24.47) * mm});
            skLineSegment(sketch, "E2022", {"start": v(-41.88, 24.47) * mm, "end": v(-42.03, 24.55) * mm});
            skLineSegment(sketch, "E2023", {"start": v(-42.03, 24.55) * mm, "end": v(-42.18, 24.61) * mm});
            skLineSegment(sketch, "E2024", {"start": v(-42.18, 24.61) * mm, "end": v(-42.31, 24.62) * mm});
            skLineSegment(sketch, "E2025", {"start": v(-42.31, 24.62) * mm, "end": v(-42.48, 24.6) * mm});
            skLineSegment(sketch, "E2026", {"start": v(-42.48, 24.6) * mm, "end": v(-42.63, 24.54) * mm});
            skLineSegment(sketch, "E2027", {"start": v(-42.63, 24.54) * mm, "end": v(-42.76, 24.44) * mm});
            skLineSegment(sketch, "E2028", {"start": v(-42.76, 24.44) * mm, "end": v(-42.86, 24.31) * mm});
            skLineSegment(sketch, "E2029", {"start": v(-42.86, 24.31) * mm, "end": v(-42.92, 24.16) * mm});
            skLineSegment(sketch, "E2030", {"start": v(-42.92, 24.16) * mm, "end": v(-42.94, 24) * mm});
            skLineSegment(sketch, "E2031", {"start": v(-42.94, 24) * mm, "end": v(-42.92, 23.84) * mm});
            skLineSegment(sketch, "E2032", {"start": v(-42.92, 23.84) * mm, "end": v(-42.86, 23.68) * mm});
            skLineSegment(sketch, "E2033", {"start": v(-42.86, 23.68) * mm, "end": v(-42.76, 23.56) * mm});
            skLineSegment(sketch, "E2034", {"start": v(-42.76, 23.56) * mm, "end": v(-42.62, 23.46) * mm});
            skLineSegment(sketch, "E2035", {"start": v(-42.62, 23.46) * mm, "end": v(-42.49, 23.38) * mm});
            skLineSegment(sketch, "E2036", {"start": v(-42.49, 23.38) * mm, "end": v(-42.35, 23.3) * mm});
            skLineSegment(sketch, "E2037", {"start": v(-42.35, 23.3) * mm, "end": v(-42.2, 23.22) * mm});
            skLineSegment(sketch, "E2038", {"start": v(-42.2, 23.22) * mm, "end": v(-42.07, 23.15) * mm});
            skLineSegment(sketch, "E2039", {"start": v(-42.07, 23.15) * mm, "end": v(-41.93, 23.07) * mm});
            skLineSegment(sketch, "E2040", {"start": v(-41.93, 23.07) * mm, "end": v(-41.8, 23) * mm});
            skLineSegment(sketch, "E2041", {"start": v(-41.8, 23) * mm, "end": v(-41.66, 22.91) * mm});
            skLineSegment(sketch, "E2042", {"start": v(-41.66, 22.91) * mm, "end": v(-41.52, 22.84) * mm});
            skLineSegment(sketch, "E2043", {"start": v(-41.52, 22.84) * mm, "end": v(-41.38, 22.76) * mm});
            skLineSegment(sketch, "E2044", {"start": v(-41.38, 22.76) * mm, "end": v(-41.24, 22.68) * mm});
            skLineSegment(sketch, "E2045", {"start": v(-41.24, 22.68) * mm, "end": v(-41.1, 22.6) * mm});
            skLineSegment(sketch, "E2046", {"start": v(-41.1, 22.6) * mm, "end": v(-40.96, 22.53) * mm});
            skLineSegment(sketch, "E2047", {"start": v(-40.96, 22.53) * mm, "end": v(-40.84, 22.46) * mm});
            skLineSegment(sketch, "E2048", {"start": v(-40.84, 22.46) * mm, "end": v(-40.92, 22.32) * mm});
            skLineSegment(sketch, "E2049", {"start": v(-40.92, 22.32) * mm, "end": v(-41, 22.18) * mm});
            skLineSegment(sketch, "E2050", {"start": v(-41, 22.18) * mm, "end": v(-41.07, 22.04) * mm});
            skLineSegment(sketch, "E2051", {"start": v(-41.07, 22.04) * mm, "end": v(-41.14, 21.9) * mm});
            skLineSegment(sketch, "E2052", {"start": v(-41.14, 21.9) * mm, "end": v(-41.21, 21.77) * mm});
            skLineSegment(sketch, "E2053", {"start": v(-41.21, 21.77) * mm, "end": v(-41.29, 21.63) * mm});
            skLineSegment(sketch, "E2054", {"start": v(-41.29, 21.63) * mm, "end": v(-41.36, 21.49) * mm});
            skLineSegment(sketch, "E2055", {"start": v(-41.36, 21.49) * mm, "end": v(-41.44, 21.35) * mm});
            skLineSegment(sketch, "E2056", {"start": v(-41.44, 21.35) * mm, "end": v(-41.51, 21.21) * mm});
            skLineSegment(sketch, "E2057", {"start": v(-41.51, 21.21) * mm, "end": v(-41.59, 21.07) * mm});
            skLineSegment(sketch, "E2058", {"start": v(-41.59, 21.07) * mm, "end": v(-41.66, 20.93) * mm});
            skLineSegment(sketch, "E2059", {"start": v(-41.66, 20.93) * mm, "end": v(-41.7, 20.86) * mm});
            skLineSegment(sketch, "E2060", {"start": v(-41.7, 20.86) * mm, "end": v(-41.84, 20.93) * mm});
            skLineSegment(sketch, "E2061", {"start": v(-41.84, 20.93) * mm, "end": v(-41.98, 21) * mm});
            skLineSegment(sketch, "E2062", {"start": v(-41.98, 21) * mm, "end": v(-42.12, 21.08) * mm});
            skLineSegment(sketch, "E2063", {"start": v(-42.12, 21.08) * mm, "end": v(-42.26, 21.15) * mm});
            skLineSegment(sketch, "E2064", {"start": v(-42.26, 21.15) * mm, "end": v(-42.4, 21.22) * mm});
            skLineSegment(sketch, "E2065", {"start": v(-42.4, 21.22) * mm, "end": v(-42.55, 21.3) * mm});
            skLineSegment(sketch, "E2066", {"start": v(-42.55, 21.3) * mm, "end": v(-42.69, 21.37) * mm});
            skLineSegment(sketch, "E2067", {"start": v(-42.69, 21.37) * mm, "end": v(-42.83, 21.44) * mm});
            skLineSegment(sketch, "E2068", {"start": v(-42.83, 21.44) * mm, "end": v(-42.97, 21.51) * mm});
            skLineSegment(sketch, "E2069", {"start": v(-42.97, 21.51) * mm, "end": v(-43.11, 21.58) * mm});
            skLineSegment(sketch, "E2070", {"start": v(-43.11, 21.58) * mm, "end": v(-43.25, 21.65) * mm});
            skLineSegment(sketch, "E2071", {"start": v(-43.25, 21.65) * mm, "end": v(-43.4, 21.73) * mm});
            skLineSegment(sketch, "E2072", {"start": v(-43.4, 21.73) * mm, "end": v(-43.55, 21.8) * mm});
            skLineSegment(sketch, "E2073", {"start": v(-43.55, 21.8) * mm, "end": v(-43.7, 21.85) * mm});
            skLineSegment(sketch, "E2074", {"start": v(-43.7, 21.85) * mm, "end": v(-43.8, 21.85) * mm});
            skLineSegment(sketch, "E2075", {"start": v(-43.8, 21.85) * mm, "end": v(-43.96, 21.83) * mm});
            skLineSegment(sketch, "E2076", {"start": v(-43.96, 21.83) * mm, "end": v(-44.11, 21.77) * mm});
            skLineSegment(sketch, "E2077", {"start": v(-44.11, 21.77) * mm, "end": v(-44.24, 21.67) * mm});
            skLineSegment(sketch, "E2078", {"start": v(-44.24, 21.67) * mm, "end": v(-44.34, 21.53) * mm});
            skLineSegment(sketch, "E2079", {"start": v(-44.34, 21.53) * mm, "end": v(-44.4, 21.38) * mm});
            skLineSegment(sketch, "E2080", {"start": v(-44.4, 21.38) * mm, "end": v(-44.42, 21.22) * mm});
            skLineSegment(sketch, "E2081", {"start": v(-44.42, 21.22) * mm, "end": v(-44.4, 21.06) * mm});
            skLineSegment(sketch, "E2082", {"start": v(-44.4, 21.06) * mm, "end": v(-44.33, 20.9) * mm});
            skLineSegment(sketch, "E2083", {"start": v(-44.33, 20.9) * mm, "end": v(-44.23, 20.78) * mm});
            skLineSegment(sketch, "E2084", {"start": v(-44.23, 20.78) * mm, "end": v(-44.1, 20.68) * mm});
            skLineSegment(sketch, "E2085", {"start": v(-44.1, 20.68) * mm, "end": v(-43.95, 20.6) * mm});
            skLineSegment(sketch, "E2086", {"start": v(-43.95, 20.6) * mm, "end": v(-43.8, 20.54) * mm});
            skLineSegment(sketch, "E2087", {"start": v(-43.8, 20.54) * mm, "end": v(-43.66, 20.47) * mm});
            skLineSegment(sketch, "E2088", {"start": v(-43.66, 20.47) * mm, "end": v(-43.52, 20.4) * mm});
            skLineSegment(sketch, "E2089", {"start": v(-43.52, 20.4) * mm, "end": v(-43.37, 20.34) * mm});
            skLineSegment(sketch, "E2090", {"start": v(-43.37, 20.34) * mm, "end": v(-43.23, 20.27) * mm});
            skLineSegment(sketch, "E2091", {"start": v(-43.23, 20.27) * mm, "end": v(-43.09, 20.2) * mm});
            skLineSegment(sketch, "E2092", {"start": v(-43.09, 20.2) * mm, "end": v(-42.94, 20.13) * mm});
            skLineSegment(sketch, "E2093", {"start": v(-42.94, 20.13) * mm, "end": v(-42.8, 20.06) * mm});
            skLineSegment(sketch, "E2094", {"start": v(-42.8, 20.06) * mm, "end": v(-42.66, 20) * mm});
            skLineSegment(sketch, "E2095", {"start": v(-42.66, 20) * mm, "end": v(-42.52, 19.93) * mm});
            skLineSegment(sketch, "E2096", {"start": v(-42.52, 19.93) * mm, "end": v(-42.37, 19.86) * mm});
            skLineSegment(sketch, "E2097", {"start": v(-42.37, 19.86) * mm, "end": v(-42.23, 19.79) * mm});
            skLineSegment(sketch, "E2098", {"start": v(-42.23, 19.79) * mm, "end": v(-42.3, 19.64) * mm});
            skLineSegment(sketch, "E2099", {"start": v(-42.3, 19.64) * mm, "end": v(-42.36, 19.5) * mm});
            skLineSegment(sketch, "E2100", {"start": v(-42.36, 19.5) * mm, "end": v(-42.42, 19.36) * mm});
            skLineSegment(sketch, "E2101", {"start": v(-42.42, 19.36) * mm, "end": v(-42.49, 19.22) * mm});
            skLineSegment(sketch, "E2102", {"start": v(-42.49, 19.22) * mm, "end": v(-42.55, 19.07) * mm});
            skLineSegment(sketch, "E2103", {"start": v(-42.55, 19.07) * mm, "end": v(-42.62, 18.93) * mm});
            skLineSegment(sketch, "E2104", {"start": v(-42.62, 18.93) * mm, "end": v(-42.68, 18.79) * mm});
            skLineSegment(sketch, "E2105", {"start": v(-42.68, 18.79) * mm, "end": v(-42.75, 18.64) * mm});
            skLineSegment(sketch, "E2106", {"start": v(-42.75, 18.64) * mm, "end": v(-42.81, 18.5) * mm});
            skLineSegment(sketch, "E2107", {"start": v(-42.81, 18.5) * mm, "end": v(-42.88, 18.36) * mm});
            skLineSegment(sketch, "E2108", {"start": v(-42.88, 18.36) * mm, "end": v(-42.94, 18.21) * mm});
            skLineSegment(sketch, "E2109", {"start": v(-42.94, 18.21) * mm, "end": v(-42.97, 18.14) * mm});
            skLineSegment(sketch, "E2110", {"start": v(-42.97, 18.14) * mm, "end": v(-43.12, 18.2) * mm});
            skLineSegment(sketch, "E2111", {"start": v(-43.12, 18.2) * mm, "end": v(-43.26, 18.26) * mm});
            skLineSegment(sketch, "E2112", {"start": v(-43.26, 18.26) * mm, "end": v(-43.41, 18.33) * mm});
            skLineSegment(sketch, "E2113", {"start": v(-43.41, 18.33) * mm, "end": v(-43.56, 18.39) * mm});
            skLineSegment(sketch, "E2114", {"start": v(-43.56, 18.39) * mm, "end": v(-43.7, 18.45) * mm});
            skLineSegment(sketch, "E2115", {"start": v(-43.7, 18.45) * mm, "end": v(-43.85, 18.51) * mm});
            skLineSegment(sketch, "E2116", {"start": v(-43.85, 18.51) * mm, "end": v(-44, 18.58) * mm});
            skLineSegment(sketch, "E2117", {"start": v(-44, 18.58) * mm, "end": v(-44.14, 18.64) * mm});
            skLineSegment(sketch, "E2118", {"start": v(-44.14, 18.64) * mm, "end": v(-44.29, 18.7) * mm});
            skLineSegment(sketch, "E2119", {"start": v(-44.29, 18.7) * mm, "end": v(-44.43, 18.76) * mm});
            skLineSegment(sketch, "E2120", {"start": v(-44.43, 18.76) * mm, "end": v(-44.58, 18.83) * mm});
            skLineSegment(sketch, "E2121", {"start": v(-44.58, 18.83) * mm, "end": v(-44.72, 18.9) * mm});
            skLineSegment(sketch, "E2122", {"start": v(-44.72, 18.9) * mm, "end": v(-44.88, 18.96) * mm});
            skLineSegment(sketch, "E2123", {"start": v(-44.88, 18.96) * mm, "end": v(-45.04, 19) * mm});
            skLineSegment(sketch, "E2124", {"start": v(-45.04, 19) * mm, "end": v(-45.1, 19) * mm});
            skLineSegment(sketch, "E2125", {"start": v(-45.1, 19) * mm, "end": v(-45.27, 18.97) * mm});
            skLineSegment(sketch, "E2126", {"start": v(-45.27, 18.97) * mm, "end": v(-45.42, 18.9) * mm});
            skLineSegment(sketch, "E2127", {"start": v(-45.42, 18.9) * mm, "end": v(-45.55, 18.8) * mm});
            skLineSegment(sketch, "E2128", {"start": v(-45.55, 18.8) * mm, "end": v(-45.64, 18.67) * mm});
            skLineSegment(sketch, "E2129", {"start": v(-45.64, 18.67) * mm, "end": v(-45.7, 18.51) * mm});
            skLineSegment(sketch, "E2130", {"start": v(-45.7, 18.51) * mm, "end": v(-45.72, 18.35) * mm});
            skLineSegment(sketch, "E2131", {"start": v(-45.72, 18.35) * mm, "end": v(-45.7, 18.19) * mm});
            skLineSegment(sketch, "E2132", {"start": v(-45.7, 18.19) * mm, "end": v(-45.62, 18.04) * mm});
            skLineSegment(sketch, "E2133", {"start": v(-45.62, 18.04) * mm, "end": v(-45.52, 17.91) * mm});
            skLineSegment(sketch, "E2134", {"start": v(-45.52, 17.91) * mm, "end": v(-45.39, 17.82) * mm});
            skLineSegment(sketch, "E2135", {"start": v(-45.39, 17.82) * mm, "end": v(-45.24, 17.76) * mm});
            skLineSegment(sketch, "E2136", {"start": v(-45.24, 17.76) * mm, "end": v(-45.1, 17.7) * mm});
            skLineSegment(sketch, "E2137", {"start": v(-45.1, 17.7) * mm, "end": v(-44.95, 17.64) * mm});
            skLineSegment(sketch, "E2138", {"start": v(-44.95, 17.64) * mm, "end": v(-44.8, 17.58) * mm});
            skLineSegment(sketch, "E2139", {"start": v(-44.8, 17.58) * mm, "end": v(-44.66, 17.52) * mm});
            skLineSegment(sketch, "E2140", {"start": v(-44.66, 17.52) * mm, "end": v(-44.5, 17.46) * mm});
            skLineSegment(sketch, "E2141", {"start": v(-44.5, 17.46) * mm, "end": v(-44.36, 17.4) * mm});
            skLineSegment(sketch, "E2142", {"start": v(-44.36, 17.4) * mm, "end": v(-44.21, 17.34) * mm});
            skLineSegment(sketch, "E2143", {"start": v(-44.21, 17.34) * mm, "end": v(-44.06, 17.28) * mm});
            skLineSegment(sketch, "E2144", {"start": v(-44.06, 17.28) * mm, "end": v(-43.92, 17.23) * mm});
            skLineSegment(sketch, "E2145", {"start": v(-43.92, 17.23) * mm, "end": v(-43.77, 17.17) * mm});
            skLineSegment(sketch, "E2146", {"start": v(-43.77, 17.17) * mm, "end": v(-43.62, 17.1) * mm});
            skLineSegment(sketch, "E2147", {"start": v(-43.62, 17.1) * mm, "end": v(-43.48, 17.05) * mm});
            skLineSegment(sketch, "E2148", {"start": v(-43.48, 17.05) * mm, "end": v(-43.43, 17.03) * mm});
            skLineSegment(sketch, "E2149", {"start": v(-43.43, 17.03) * mm, "end": v(-43.49, 16.89) * mm});
            skLineSegment(sketch, "E2150", {"start": v(-43.49, 16.89) * mm, "end": v(-43.54, 16.74) * mm});
            skLineSegment(sketch, "E2151", {"start": v(-43.54, 16.74) * mm, "end": v(-43.6, 16.6) * mm});
            skLineSegment(sketch, "E2152", {"start": v(-43.6, 16.6) * mm, "end": v(-43.65, 16.44) * mm});
            skLineSegment(sketch, "E2153", {"start": v(-43.65, 16.44) * mm, "end": v(-43.7, 16.3) * mm});
            skLineSegment(sketch, "E2154", {"start": v(-43.7, 16.3) * mm, "end": v(-43.77, 16.15) * mm});
            skLineSegment(sketch, "E2155", {"start": v(-43.77, 16.15) * mm, "end": v(-43.82, 16) * mm});
            skLineSegment(sketch, "E2156", {"start": v(-43.82, 16) * mm, "end": v(-43.88, 15.86) * mm});
            skLineSegment(sketch, "E2157", {"start": v(-43.88, 15.86) * mm, "end": v(-43.93, 15.7) * mm});
            skLineSegment(sketch, "E2158", {"start": v(-43.93, 15.7) * mm, "end": v(-43.99, 15.56) * mm});
            skLineSegment(sketch, "E2159", {"start": v(-43.99, 15.56) * mm, "end": v(-44.04, 15.41) * mm});
            skLineSegment(sketch, "E2160", {"start": v(-44.04, 15.41) * mm, "end": v(-44.07, 15.34) * mm});
            skLineSegment(sketch, "E2161", {"start": v(-44.07, 15.34) * mm, "end": v(-44.22, 15.4) * mm});
            skLineSegment(sketch, "E2162", {"start": v(-44.22, 15.4) * mm, "end": v(-44.37, 15.44) * mm});
            skLineSegment(sketch, "E2163", {"start": v(-44.37, 15.44) * mm, "end": v(-44.52, 15.5) * mm});
            skLineSegment(sketch, "E2164", {"start": v(-44.52, 15.5) * mm, "end": v(-44.67, 15.55) * mm});
            skLineSegment(sketch, "E2165", {"start": v(-44.67, 15.55) * mm, "end": v(-44.82, 15.6) * mm});
            skLineSegment(sketch, "E2166", {"start": v(-44.82, 15.6) * mm, "end": v(-44.97, 15.66) * mm});
            skLineSegment(sketch, "E2167", {"start": v(-44.97, 15.66) * mm, "end": v(-45.12, 15.7) * mm});
            skLineSegment(sketch, "E2168", {"start": v(-45.12, 15.7) * mm, "end": v(-45.26, 15.76) * mm});
            skLineSegment(sketch, "E2169", {"start": v(-45.26, 15.76) * mm, "end": v(-45.42, 15.82) * mm});
            skLineSegment(sketch, "E2170", {"start": v(-45.42, 15.82) * mm, "end": v(-45.57, 15.87) * mm});
            skLineSegment(sketch, "E2171", {"start": v(-45.57, 15.87) * mm, "end": v(-45.71, 15.92) * mm});
            skLineSegment(sketch, "E2172", {"start": v(-45.71, 15.92) * mm, "end": v(-45.87, 15.97) * mm});
            skLineSegment(sketch, "E2173", {"start": v(-45.87, 15.97) * mm, "end": v(-46.03, 16.03) * mm});
            skLineSegment(sketch, "E2174", {"start": v(-46.03, 16.03) * mm, "end": v(-46.19, 16.05) * mm});
            skLineSegment(sketch, "E2175", {"start": v(-46.19, 16.05) * mm, "end": v(-46.35, 16.04) * mm});
            skLineSegment(sketch, "E2176", {"start": v(-46.35, 16.04) * mm, "end": v(-46.5, 15.98) * mm});
            skLineSegment(sketch, "E2177", {"start": v(-46.5, 15.98) * mm, "end": v(-46.63, 15.88) * mm});
            skLineSegment(sketch, "E2178", {"start": v(-46.63, 15.88) * mm, "end": v(-46.74, 15.75) * mm});
            skLineSegment(sketch, "E2179", {"start": v(-46.74, 15.75) * mm, "end": v(-46.8, 15.6) * mm});
            skLineSegment(sketch, "E2180", {"start": v(-46.8, 15.6) * mm, "end": v(-46.82, 15.44) * mm});
            skLineSegment(sketch, "E2181", {"start": v(-46.82, 15.44) * mm, "end": v(-46.8, 15.27) * mm});
            skLineSegment(sketch, "E2182", {"start": v(-46.8, 15.27) * mm, "end": v(-46.74, 15.12) * mm});
            skLineSegment(sketch, "E2183", {"start": v(-46.74, 15.12) * mm, "end": v(-46.64, 15) * mm});
            skLineSegment(sketch, "E2184", {"start": v(-46.64, 15) * mm, "end": v(-46.52, 14.89) * mm});
            skLineSegment(sketch, "E2185", {"start": v(-46.52, 14.89) * mm, "end": v(-46.37, 14.83) * mm});
            skLineSegment(sketch, "E2186", {"start": v(-46.37, 14.83) * mm, "end": v(-46.22, 14.78) * mm});
            skLineSegment(sketch, "E2187", {"start": v(-46.22, 14.78) * mm, "end": v(-46.07, 14.73) * mm});
            skLineSegment(sketch, "E2188", {"start": v(-46.07, 14.73) * mm, "end": v(-45.92, 14.68) * mm});
            skLineSegment(sketch, "E2189", {"start": v(-45.92, 14.68) * mm, "end": v(-45.77, 14.63) * mm});
            skLineSegment(sketch, "E2190", {"start": v(-45.77, 14.63) * mm, "end": v(-45.62, 14.58) * mm});
            skLineSegment(sketch, "E2191", {"start": v(-45.62, 14.58) * mm, "end": v(-45.47, 14.53) * mm});
            skLineSegment(sketch, "E2192", {"start": v(-45.47, 14.53) * mm, "end": v(-45.32, 14.49) * mm});
            skLineSegment(sketch, "E2193", {"start": v(-45.32, 14.49) * mm, "end": v(-45.17, 14.44) * mm});
            skLineSegment(sketch, "E2194", {"start": v(-45.17, 14.44) * mm, "end": v(-45.02, 14.39) * mm});
            skLineSegment(sketch, "E2195", {"start": v(-45.02, 14.39) * mm, "end": v(-44.87, 14.34) * mm});
            skLineSegment(sketch, "E2196", {"start": v(-44.87, 14.34) * mm, "end": v(-44.71, 14.29) * mm});
            skLineSegment(sketch, "E2197", {"start": v(-44.71, 14.29) * mm, "end": v(-44.56, 14.24) * mm});
            skLineSegment(sketch, "E2198", {"start": v(-44.56, 14.24) * mm, "end": v(-44.46, 14.2) * mm});
            skLineSegment(sketch, "E2199", {"start": v(-44.46, 14.2) * mm, "end": v(-44.5, 14.05) * mm});
            skLineSegment(sketch, "E2200", {"start": v(-44.5, 14.05) * mm, "end": v(-44.55, 13.9) * mm});
            skLineSegment(sketch, "E2201", {"start": v(-44.55, 13.9) * mm, "end": v(-44.6, 13.75) * mm});
            skLineSegment(sketch, "E2202", {"start": v(-44.6, 13.75) * mm, "end": v(-44.64, 13.6) * mm});
            skLineSegment(sketch, "E2203", {"start": v(-44.64, 13.6) * mm, "end": v(-44.68, 13.45) * mm});
            skLineSegment(sketch, "E2204", {"start": v(-44.68, 13.45) * mm, "end": v(-44.73, 13.3) * mm});
            skLineSegment(sketch, "E2205", {"start": v(-44.73, 13.3) * mm, "end": v(-44.77, 13.15) * mm});
            skLineSegment(sketch, "E2206", {"start": v(-44.77, 13.15) * mm, "end": v(-44.82, 13) * mm});
            skLineSegment(sketch, "E2207", {"start": v(-44.82, 13) * mm, "end": v(-44.87, 12.85) * mm});
            skLineSegment(sketch, "E2208", {"start": v(-44.87, 12.85) * mm, "end": v(-44.91, 12.7) * mm});
            skLineSegment(sketch, "E2209", {"start": v(-44.91, 12.7) * mm, "end": v(-44.96, 12.55) * mm});
            skLineSegment(sketch, "E2210", {"start": v(-44.96, 12.55) * mm, "end": v(-44.98, 12.47) * mm});
            skLineSegment(sketch, "E2211", {"start": v(-44.98, 12.47) * mm, "end": v(-45.13, 12.51) * mm});
            skLineSegment(sketch, "E2212", {"start": v(-45.13, 12.51) * mm, "end": v(-45.28, 12.56) * mm});
            skLineSegment(sketch, "E2213", {"start": v(-45.28, 12.56) * mm, "end": v(-45.44, 12.6) * mm});
            skLineSegment(sketch, "E2214", {"start": v(-45.44, 12.6) * mm, "end": v(-45.6, 12.64) * mm});
            skLineSegment(sketch, "E2215", {"start": v(-45.6, 12.64) * mm, "end": v(-45.74, 12.69) * mm});
            skLineSegment(sketch, "E2216", {"start": v(-45.74, 12.69) * mm, "end": v(-45.9, 12.73) * mm});
            skLineSegment(sketch, "E2217", {"start": v(-45.9, 12.73) * mm, "end": v(-46.05, 12.77) * mm});
            skLineSegment(sketch, "E2218", {"start": v(-46.05, 12.77) * mm, "end": v(-46.2, 12.82) * mm});
            skLineSegment(sketch, "E2219", {"start": v(-46.2, 12.82) * mm, "end": v(-46.36, 12.86) * mm});
            skLineSegment(sketch, "E2220", {"start": v(-46.36, 12.86) * mm, "end": v(-46.5, 12.9) * mm});
            skLineSegment(sketch, "E2221", {"start": v(-46.5, 12.9) * mm, "end": v(-46.66, 12.95) * mm});
            skLineSegment(sketch, "E2222", {"start": v(-46.66, 12.95) * mm, "end": v(-46.81, 12.99) * mm});
            skLineSegment(sketch, "E2223", {"start": v(-46.81, 12.99) * mm, "end": v(-46.98, 13.03) * mm});
            skLineSegment(sketch, "E2224", {"start": v(-46.98, 13.03) * mm, "end": v(-47.1, 13.05) * mm});
            skLineSegment(sketch, "E2225", {"start": v(-47.1, 13.05) * mm, "end": v(-47.27, 13.03) * mm});
            skLineSegment(sketch, "E2226", {"start": v(-47.27, 13.03) * mm, "end": v(-47.42, 12.97) * mm});
            skLineSegment(sketch, "E2227", {"start": v(-47.42, 12.97) * mm, "end": v(-47.55, 12.87) * mm});
            skLineSegment(sketch, "E2228", {"start": v(-47.55, 12.87) * mm, "end": v(-47.65, 12.74) * mm});
            skLineSegment(sketch, "E2229", {"start": v(-47.65, 12.74) * mm, "end": v(-47.71, 12.58) * mm});
            skLineSegment(sketch, "E2230", {"start": v(-47.71, 12.58) * mm, "end": v(-47.74, 12.42) * mm});
            skLineSegment(sketch, "E2231", {"start": v(-47.74, 12.42) * mm, "end": v(-47.71, 12.26) * mm});
            skLineSegment(sketch, "E2232", {"start": v(-47.71, 12.26) * mm, "end": v(-47.65, 12.1) * mm});
            skLineSegment(sketch, "E2233", {"start": v(-47.65, 12.1) * mm, "end": v(-47.55, 11.98) * mm});
            skLineSegment(sketch, "E2234", {"start": v(-47.55, 11.98) * mm, "end": v(-47.42, 11.88) * mm});
            skLineSegment(sketch, "E2235", {"start": v(-47.42, 11.88) * mm, "end": v(-47.27, 11.82) * mm});
            skLineSegment(sketch, "E2236", {"start": v(-47.27, 11.82) * mm, "end": v(-47.12, 11.78) * mm});
            skLineSegment(sketch, "E2237", {"start": v(-47.12, 11.78) * mm, "end": v(-46.96, 11.74) * mm});
            skLineSegment(sketch, "E2238", {"start": v(-46.96, 11.74) * mm, "end": v(-46.8, 11.7) * mm});
            skLineSegment(sketch, "E2239", {"start": v(-46.8, 11.7) * mm, "end": v(-46.65, 11.66) * mm});
            skLineSegment(sketch, "E2240", {"start": v(-46.65, 11.66) * mm, "end": v(-46.5, 11.62) * mm});
            skLineSegment(sketch, "E2241", {"start": v(-46.5, 11.62) * mm, "end": v(-46.35, 11.58) * mm});
            skLineSegment(sketch, "E2242", {"start": v(-46.35, 11.58) * mm, "end": v(-46.2, 11.54) * mm});
            skLineSegment(sketch, "E2243", {"start": v(-46.2, 11.54) * mm, "end": v(-46.04, 11.5) * mm});
            skLineSegment(sketch, "E2244", {"start": v(-46.04, 11.5) * mm, "end": v(-45.88, 11.47) * mm});
            skLineSegment(sketch, "E2245", {"start": v(-45.88, 11.47) * mm, "end": v(-45.73, 11.43) * mm});
            skLineSegment(sketch, "E2246", {"start": v(-45.73, 11.43) * mm, "end": v(-45.58, 11.39) * mm});
            skLineSegment(sketch, "E2247", {"start": v(-45.58, 11.39) * mm, "end": v(-45.42, 11.35) * mm});
            skLineSegment(sketch, "E2248", {"start": v(-45.42, 11.35) * mm, "end": v(-45.3, 11.32) * mm});
            skLineSegment(sketch, "E2249", {"start": v(-45.3, 11.32) * mm, "end": v(-45.33, 11.16) * mm});
            skLineSegment(sketch, "E2250", {"start": v(-45.33, 11.16) * mm, "end": v(-45.36, 11) * mm});
            skLineSegment(sketch, "E2251", {"start": v(-45.36, 11) * mm, "end": v(-45.4, 10.86) * mm});
            skLineSegment(sketch, "E2252", {"start": v(-45.4, 10.86) * mm, "end": v(-45.43, 10.7) * mm});
            skLineSegment(sketch, "E2253", {"start": v(-45.43, 10.7) * mm, "end": v(-45.47, 10.55) * mm});
            skLineSegment(sketch, "E2254", {"start": v(-45.47, 10.55) * mm, "end": v(-45.5, 10.4) * mm});
            skLineSegment(sketch, "E2255", {"start": v(-45.5, 10.4) * mm, "end": v(-45.54, 10.24) * mm});
            skLineSegment(sketch, "E2256", {"start": v(-45.54, 10.24) * mm, "end": v(-45.58, 10.1) * mm});
            skLineSegment(sketch, "E2257", {"start": v(-45.58, 10.1) * mm, "end": v(-45.61, 9.94) * mm});
            skLineSegment(sketch, "E2258", {"start": v(-45.61, 9.94) * mm, "end": v(-45.65, 9.78) * mm});
            skLineSegment(sketch, "E2259", {"start": v(-45.65, 9.78) * mm, "end": v(-45.68, 9.63) * mm});
            skLineSegment(sketch, "E2260", {"start": v(-45.68, 9.63) * mm, "end": v(-45.7, 9.55) * mm});
            skLineSegment(sketch, "E2261", {"start": v(-45.7, 9.55) * mm, "end": v(-45.86, 9.58) * mm});
            skLineSegment(sketch, "E2262", {"start": v(-45.86, 9.58) * mm, "end": v(-46, 9.62) * mm});
            skLineSegment(sketch, "E2263", {"start": v(-46, 9.62) * mm, "end": v(-46.17, 9.65) * mm});
            skLineSegment(sketch, "E2264", {"start": v(-46.17, 9.65) * mm, "end": v(-46.32, 9.68) * mm});
            skLineSegment(sketch, "E2265", {"start": v(-46.32, 9.68) * mm, "end": v(-46.48, 9.72) * mm});
            skLineSegment(sketch, "E2266", {"start": v(-46.48, 9.72) * mm, "end": v(-46.63, 9.75) * mm});
            skLineSegment(sketch, "E2267", {"start": v(-46.63, 9.75) * mm, "end": v(-46.79, 9.78) * mm});
            skLineSegment(sketch, "E2268", {"start": v(-46.79, 9.78) * mm, "end": v(-46.94, 9.82) * mm});
            skLineSegment(sketch, "E2269", {"start": v(-46.94, 9.82) * mm, "end": v(-47.1, 9.85) * mm});
            skLineSegment(sketch, "E2270", {"start": v(-47.1, 9.85) * mm, "end": v(-47.25, 9.88) * mm});
            skLineSegment(sketch, "E2271", {"start": v(-47.25, 9.88) * mm, "end": v(-47.4, 9.91) * mm});
            skLineSegment(sketch, "E2272", {"start": v(-47.4, 9.91) * mm, "end": v(-47.56, 9.95) * mm});
            skLineSegment(sketch, "E2273", {"start": v(-47.56, 9.95) * mm, "end": v(-47.73, 9.98) * mm});
            skLineSegment(sketch, "E2274", {"start": v(-47.73, 9.98) * mm, "end": v(-47.83, 9.99) * mm});
            skLineSegment(sketch, "E2275", {"start": v(-47.83, 9.99) * mm, "end": v(-48, 9.97) * mm});
            skLineSegment(sketch, "E2276", {"start": v(-48, 9.97) * mm, "end": v(-48.14, 9.9) * mm});
            skLineSegment(sketch, "E2277", {"start": v(-48.14, 9.9) * mm, "end": v(-48.27, 9.8) * mm});
            skLineSegment(sketch, "E2278", {"start": v(-48.27, 9.8) * mm, "end": v(-48.37, 9.67) * mm});
            skLineSegment(sketch, "E2279", {"start": v(-48.37, 9.67) * mm, "end": v(-48.43, 9.52) * mm});
            skLineSegment(sketch, "E2280", {"start": v(-48.43, 9.52) * mm, "end": v(-48.45, 9.36) * mm});
            skLineSegment(sketch, "E2281", {"start": v(-48.45, 9.36) * mm, "end": v(-48.43, 9.2) * mm});
            skLineSegment(sketch, "E2282", {"start": v(-48.43, 9.2) * mm, "end": v(-48.36, 9.04) * mm});
            skLineSegment(sketch, "E2283", {"start": v(-48.36, 9.04) * mm, "end": v(-48.26, 8.91) * mm});
            skLineSegment(sketch, "E2284", {"start": v(-48.26, 8.91) * mm, "end": v(-48.13, 8.82) * mm});
            skLineSegment(sketch, "E2285", {"start": v(-48.13, 8.82) * mm, "end": v(-47.97, 8.76) * mm});
            skLineSegment(sketch, "E2286", {"start": v(-47.97, 8.76) * mm, "end": v(-47.8, 8.73) * mm});
            skLineSegment(sketch, "E2287", {"start": v(-47.8, 8.73) * mm, "end": v(-47.65, 8.7) * mm});
            skLineSegment(sketch, "E2288", {"start": v(-47.65, 8.7) * mm, "end": v(-47.5, 8.67) * mm});
            skLineSegment(sketch, "E2289", {"start": v(-47.5, 8.67) * mm, "end": v(-47.34, 8.64) * mm});
            skLineSegment(sketch, "E2290", {"start": v(-47.34, 8.64) * mm, "end": v(-47.19, 8.6) * mm});
            skLineSegment(sketch, "E2291", {"start": v(-47.19, 8.6) * mm, "end": v(-47.03, 8.58) * mm});
            skLineSegment(sketch, "E2292", {"start": v(-47.03, 8.58) * mm, "end": v(-46.87, 8.55) * mm});
            skLineSegment(sketch, "E2293", {"start": v(-46.87, 8.55) * mm, "end": v(-46.72, 8.52) * mm});
            skLineSegment(sketch, "E2294", {"start": v(-46.72, 8.52) * mm, "end": v(-46.56, 8.5) * mm});
            skLineSegment(sketch, "E2295", {"start": v(-46.56, 8.5) * mm, "end": v(-46.4, 8.46) * mm});
            skLineSegment(sketch, "E2296", {"start": v(-46.4, 8.46) * mm, "end": v(-46.25, 8.44) * mm});
            skLineSegment(sketch, "E2297", {"start": v(-46.25, 8.44) * mm, "end": v(-46.1, 8.4) * mm});
            skLineSegment(sketch, "E2298", {"start": v(-46.1, 8.4) * mm, "end": v(-45.94, 8.38) * mm});
            skLineSegment(sketch, "E2299", {"start": v(-45.94, 8.38) * mm, "end": v(-45.96, 8.22) * mm});
            skLineSegment(sketch, "E2300", {"start": v(-45.96, 8.22) * mm, "end": v(-45.99, 8.07) * mm});
            skLineSegment(sketch, "E2301", {"start": v(-45.99, 8.07) * mm, "end": v(-46.01, 7.91) * mm});
            skLineSegment(sketch, "E2302", {"start": v(-46.01, 7.91) * mm, "end": v(-46.04, 7.76) * mm});
            skLineSegment(sketch, "E2303", {"start": v(-46.04, 7.76) * mm, "end": v(-46.06, 7.6) * mm});
            skLineSegment(sketch, "E2304", {"start": v(-46.06, 7.6) * mm, "end": v(-46.09, 7.45) * mm});
            skLineSegment(sketch, "E2305", {"start": v(-46.09, 7.45) * mm, "end": v(-46.11, 7.3) * mm});
            skLineSegment(sketch, "E2306", {"start": v(-46.11, 7.3) * mm, "end": v(-46.14, 7.14) * mm});
            skLineSegment(sketch, "E2307", {"start": v(-46.14, 7.14) * mm, "end": v(-46.17, 6.98) * mm});
            skLineSegment(sketch, "E2308", {"start": v(-46.17, 6.98) * mm, "end": v(-46.2, 6.83) * mm});
            skLineSegment(sketch, "E2309", {"start": v(-46.2, 6.83) * mm, "end": v(-46.22, 6.67) * mm});
            skLineSegment(sketch, "E2310", {"start": v(-46.22, 6.67) * mm, "end": v(-46.23, 6.6) * mm});
            skLineSegment(sketch, "E2311", {"start": v(-46.23, 6.6) * mm, "end": v(-46.39, 6.61) * mm});
            skLineSegment(sketch, "E2312", {"start": v(-46.39, 6.61) * mm, "end": v(-46.54, 6.64) * mm});
            skLineSegment(sketch, "E2313", {"start": v(-46.54, 6.64) * mm, "end": v(-46.7, 6.66) * mm});
            skLineSegment(sketch, "E2314", {"start": v(-46.7, 6.66) * mm, "end": v(-46.86, 6.68) * mm});
            skLineSegment(sketch, "E2315", {"start": v(-46.86, 6.68) * mm, "end": v(-47.01, 6.7) * mm});
            skLineSegment(sketch, "E2316", {"start": v(-47.01, 6.7) * mm, "end": v(-47.17, 6.73) * mm});
            skLineSegment(sketch, "E2317", {"start": v(-47.17, 6.73) * mm, "end": v(-47.33, 6.75) * mm});
            skLineSegment(sketch, "E2318", {"start": v(-47.33, 6.75) * mm, "end": v(-47.48, 6.77) * mm});
            skLineSegment(sketch, "E2319", {"start": v(-47.48, 6.77) * mm, "end": v(-47.64, 6.8) * mm});
            skLineSegment(sketch, "E2320", {"start": v(-47.64, 6.8) * mm, "end": v(-47.8, 6.82) * mm});
            skLineSegment(sketch, "E2321", {"start": v(-47.8, 6.82) * mm, "end": v(-47.96, 6.84) * mm});
            skLineSegment(sketch, "E2322", {"start": v(-47.96, 6.84) * mm, "end": v(-48.12, 6.86) * mm});
            skLineSegment(sketch, "E2323", {"start": v(-48.12, 6.86) * mm, "end": v(-48.28, 6.89) * mm});
            skLineSegment(sketch, "E2324", {"start": v(-48.28, 6.89) * mm, "end": v(-48.35, 6.9) * mm});
            skLineSegment(sketch, "E2325", {"start": v(-48.35, 6.9) * mm, "end": v(-48.51, 6.87) * mm});
            skLineSegment(sketch, "E2326", {"start": v(-48.51, 6.87) * mm, "end": v(-48.66, 6.8) * mm});
            skLineSegment(sketch, "E2327", {"start": v(-48.66, 6.8) * mm, "end": v(-48.79, 6.7) * mm});
            skLineSegment(sketch, "E2328", {"start": v(-48.79, 6.7) * mm, "end": v(-48.88, 6.56) * mm});
            skLineSegment(sketch, "E2329", {"start": v(-48.88, 6.56) * mm, "end": v(-48.94, 6.41) * mm});
            skLineSegment(sketch, "E2330", {"start": v(-48.94, 6.41) * mm, "end": v(-48.96, 6.25) * mm});
            skLineSegment(sketch, "E2331", {"start": v(-48.96, 6.25) * mm, "end": v(-48.93, 6.09) * mm});
            skLineSegment(sketch, "E2332", {"start": v(-48.93, 6.09) * mm, "end": v(-48.87, 5.94) * mm});
            skLineSegment(sketch, "E2333", {"start": v(-48.87, 5.94) * mm, "end": v(-48.76, 5.8) * mm});
            skLineSegment(sketch, "E2334", {"start": v(-48.76, 5.8) * mm, "end": v(-48.63, 5.71) * mm});
            skLineSegment(sketch, "E2335", {"start": v(-48.63, 5.71) * mm, "end": v(-48.48, 5.66) * mm});
            skLineSegment(sketch, "E2336", {"start": v(-48.48, 5.66) * mm, "end": v(-48.32, 5.63) * mm});
            skLineSegment(sketch, "E2337", {"start": v(-48.32, 5.63) * mm, "end": v(-48.17, 5.62) * mm});
            skLineSegment(sketch, "E2338", {"start": v(-48.17, 5.62) * mm, "end": v(-48, 5.6) * mm});
            skLineSegment(sketch, "E2339", {"start": v(-48, 5.6) * mm, "end": v(-47.85, 5.58) * mm});
            skLineSegment(sketch, "E2340", {"start": v(-47.85, 5.58) * mm, "end": v(-47.7, 5.56) * mm});
            skLineSegment(sketch, "E2341", {"start": v(-47.7, 5.56) * mm, "end": v(-47.54, 5.54) * mm});
            skLineSegment(sketch, "E2342", {"start": v(-47.54, 5.54) * mm, "end": v(-47.38, 5.52) * mm});
            skLineSegment(sketch, "E2343", {"start": v(-47.38, 5.52) * mm, "end": v(-47.22, 5.5) * mm});
            skLineSegment(sketch, "E2344", {"start": v(-47.22, 5.5) * mm, "end": v(-47.06, 5.48) * mm});
            skLineSegment(sketch, "E2345", {"start": v(-47.06, 5.48) * mm, "end": v(-46.9, 5.47) * mm});
            skLineSegment(sketch, "E2346", {"start": v(-46.9, 5.47) * mm, "end": v(-46.75, 5.45) * mm});
            skLineSegment(sketch, "E2347", {"start": v(-46.75, 5.45) * mm, "end": v(-46.59, 5.43) * mm});
            skLineSegment(sketch, "E2348", {"start": v(-46.59, 5.43) * mm, "end": v(-46.43, 5.4) * mm});
            skLineSegment(sketch, "E2349", {"start": v(-46.43, 5.4) * mm, "end": v(-46.39, 5.4) * mm});
            skLineSegment(sketch, "E2350", {"start": v(-46.39, 5.4) * mm, "end": v(-46.4, 5.25) * mm});
            skLineSegment(sketch, "E2351", {"start": v(-46.4, 5.25) * mm, "end": v(-46.42, 5.1) * mm});
            skLineSegment(sketch, "E2352", {"start": v(-46.42, 5.1) * mm, "end": v(-46.43, 4.93) * mm});
            skLineSegment(sketch, "E2353", {"start": v(-46.43, 4.93) * mm, "end": v(-46.45, 4.78) * mm});
            skLineSegment(sketch, "E2354", {"start": v(-46.45, 4.78) * mm, "end": v(-46.46, 4.62) * mm});
            skLineSegment(sketch, "E2355", {"start": v(-46.46, 4.62) * mm, "end": v(-46.48, 4.47) * mm});
            skLineSegment(sketch, "E2356", {"start": v(-46.48, 4.47) * mm, "end": v(-46.5, 4.3) * mm});
            skLineSegment(sketch, "E2357", {"start": v(-46.5, 4.3) * mm, "end": v(-46.51, 4.15) * mm});
            skLineSegment(sketch, "E2358", {"start": v(-46.51, 4.15) * mm, "end": v(-46.53, 4) * mm});
            skLineSegment(sketch, "E2359", {"start": v(-46.53, 4) * mm, "end": v(-46.54, 3.84) * mm});
            skLineSegment(sketch, "E2360", {"start": v(-46.54, 3.84) * mm, "end": v(-46.56, 3.68) * mm});
            skLineSegment(sketch, "E2361", {"start": v(-46.56, 3.68) * mm, "end": v(-46.56, 3.6) * mm});
            skLineSegment(sketch, "E2362", {"start": v(-46.56, 3.6) * mm, "end": v(-46.72, 3.61) * mm});
            skLineSegment(sketch, "E2363", {"start": v(-46.72, 3.61) * mm, "end": v(-46.88, 3.63) * mm});
            skLineSegment(sketch, "E2364", {"start": v(-46.88, 3.63) * mm, "end": v(-47.04, 3.64) * mm});
            skLineSegment(sketch, "E2365", {"start": v(-47.04, 3.64) * mm, "end": v(-47.2, 3.65) * mm});
            skLineSegment(sketch, "E2366", {"start": v(-47.2, 3.65) * mm, "end": v(-47.35, 3.66) * mm});
            skLineSegment(sketch, "E2367", {"start": v(-47.35, 3.66) * mm, "end": v(-47.51, 3.68) * mm});
            skLineSegment(sketch, "E2368", {"start": v(-47.51, 3.68) * mm, "end": v(-47.67, 3.69) * mm});
            skLineSegment(sketch, "E2369", {"start": v(-47.67, 3.69) * mm, "end": v(-47.83, 3.7) * mm});
            skLineSegment(sketch, "E2370", {"start": v(-47.83, 3.7) * mm, "end": v(-47.99, 3.71) * mm});
            skLineSegment(sketch, "E2371", {"start": v(-47.99, 3.71) * mm, "end": v(-48.15, 3.73) * mm});
            skLineSegment(sketch, "E2372", {"start": v(-48.15, 3.73) * mm, "end": v(-48.3, 3.74) * mm});
            skLineSegment(sketch, "E2373", {"start": v(-48.3, 3.74) * mm, "end": v(-48.46, 3.75) * mm});
            skLineSegment(sketch, "E2374", {"start": v(-48.46, 3.75) * mm, "end": v(-48.63, 3.76) * mm});
            skLineSegment(sketch, "E2375", {"start": v(-48.63, 3.76) * mm, "end": v(-48.8, 3.75) * mm});
            skLineSegment(sketch, "E2376", {"start": v(-48.8, 3.75) * mm, "end": v(-48.95, 3.69) * mm});
            skLineSegment(sketch, "E2377", {"start": v(-48.95, 3.69) * mm, "end": v(-49.08, 3.59) * mm});
            skLineSegment(sketch, "E2378", {"start": v(-49.08, 3.59) * mm, "end": v(-49.18, 3.46) * mm});
            skLineSegment(sketch, "E2379", {"start": v(-49.18, 3.46) * mm, "end": v(-49.24, 3.3) * mm});
            skLineSegment(sketch, "E2380", {"start": v(-49.24, 3.3) * mm, "end": v(-49.27, 3.15) * mm});
            skLineSegment(sketch, "E2381", {"start": v(-49.27, 3.15) * mm, "end": v(-49.25, 2.98) * mm});
            skLineSegment(sketch, "E2382", {"start": v(-49.25, 2.98) * mm, "end": v(-49.19, 2.83) * mm});
            skLineSegment(sketch, "E2383", {"start": v(-49.19, 2.83) * mm, "end": v(-49.09, 2.7) * mm});
            skLineSegment(sketch, "E2384", {"start": v(-49.09, 2.7) * mm, "end": v(-48.96, 2.6) * mm});
            skLineSegment(sketch, "E2385", {"start": v(-48.96, 2.6) * mm, "end": v(-48.8, 2.54) * mm});
            skLineSegment(sketch, "E2386", {"start": v(-48.8, 2.54) * mm, "end": v(-48.65, 2.52) * mm});
            skLineSegment(sketch, "E2387", {"start": v(-48.65, 2.52) * mm, "end": v(-48.5, 2.5) * mm});
            skLineSegment(sketch, "E2388", {"start": v(-48.5, 2.5) * mm, "end": v(-48.34, 2.5) * mm});
            skLineSegment(sketch, "E2389", {"start": v(-48.34, 2.5) * mm, "end": v(-48.18, 2.49) * mm});
            skLineSegment(sketch, "E2390", {"start": v(-48.18, 2.49) * mm, "end": v(-48.03, 2.48) * mm});
            skLineSegment(sketch, "E2391", {"start": v(-48.03, 2.48) * mm, "end": v(-47.87, 2.47) * mm});
            skLineSegment(sketch, "E2392", {"start": v(-47.87, 2.47) * mm, "end": v(-47.7, 2.46) * mm});
            skLineSegment(sketch, "E2393", {"start": v(-47.7, 2.46) * mm, "end": v(-47.55, 2.46) * mm});
            skLineSegment(sketch, "E2394", {"start": v(-47.55, 2.46) * mm, "end": v(-47.39, 2.45) * mm});
            skLineSegment(sketch, "E2395", {"start": v(-47.39, 2.45) * mm, "end": v(-47.23, 2.44) * mm});
            skLineSegment(sketch, "E2396", {"start": v(-47.23, 2.44) * mm, "end": v(-47.08, 2.43) * mm});
            skLineSegment(sketch, "E2397", {"start": v(-47.08, 2.43) * mm, "end": v(-46.91, 2.42) * mm});
            skLineSegment(sketch, "E2398", {"start": v(-46.91, 2.42) * mm, "end": v(-46.76, 2.41) * mm});
            skLineSegment(sketch, "E2399", {"start": v(-46.76, 2.41) * mm, "end": v(-46.64, 2.4) * mm});
            skLineSegment(sketch, "E2400", {"start": v(-46.64, 2.4) * mm, "end": v(-46.65, 2.25) * mm});
            skLineSegment(sketch, "E2401", {"start": v(-46.65, 2.25) * mm, "end": v(-46.65, 2.1) * mm});
            skLineSegment(sketch, "E2402", {"start": v(-46.65, 2.1) * mm, "end": v(-46.66, 1.94) * mm});
            skLineSegment(sketch, "E2403", {"start": v(-46.66, 1.94) * mm, "end": v(-46.66, 1.78) * mm});
            skLineSegment(sketch, "E2404", {"start": v(-46.66, 1.78) * mm, "end": v(-46.67, 1.62) * mm});
            skLineSegment(sketch, "E2405", {"start": v(-46.67, 1.62) * mm, "end": v(-46.67, 1.46) * mm});
            skLineSegment(sketch, "E2406", {"start": v(-46.67, 1.46) * mm, "end": v(-46.68, 1.3) * mm});
            skLineSegment(sketch, "E2407", {"start": v(-46.68, 1.3) * mm, "end": v(-46.68, 1.15) * mm});
            skLineSegment(sketch, "E2408", {"start": v(-46.68, 1.15) * mm, "end": v(-46.69, 1) * mm});
            skLineSegment(sketch, "E2409", {"start": v(-46.69, 1) * mm, "end": v(-46.7, 0.84) * mm});
            skLineSegment(sketch, "E2410", {"start": v(-46.7, 0.84) * mm, "end": v(-46.7, 0.68) * mm});
            skLineSegment(sketch, "E2411", {"start": v(-46.7, 0.68) * mm, "end": v(-46.7, 0.6) * mm});
            skLineSegment(sketch, "E2412", {"start": v(-46.7, 0.6) * mm, "end": v(-46.86, 0.6) * mm});
            skLineSegment(sketch, "E2413", {"start": v(-46.86, 0.6) * mm, "end": v(-47.02, 0.6) * mm});
            skLineSegment(sketch, "E2414", {"start": v(-47.02, 0.6) * mm, "end": v(-47.18, 0.6) * mm});
            skLineSegment(sketch, "E2415", {"start": v(-47.18, 0.6) * mm, "end": v(-47.34, 0.6) * mm});
            skLineSegment(sketch, "E2416", {"start": v(-47.34, 0.6) * mm, "end": v(-47.5, 0.6) * mm});
            skLineSegment(sketch, "E2417", {"start": v(-47.5, 0.6) * mm, "end": v(-47.65, 0.61) * mm});
            skLineSegment(sketch, "E2418", {"start": v(-47.65, 0.61) * mm, "end": v(-47.81, 0.61) * mm});
            skLineSegment(sketch, "E2419", {"start": v(-47.81, 0.61) * mm, "end": v(-47.97, 0.61) * mm});
            skLineSegment(sketch, "E2420", {"start": v(-47.97, 0.61) * mm, "end": v(-48.13, 0.62) * mm});
            skLineSegment(sketch, "E2421", {"start": v(-48.13, 0.62) * mm, "end": v(-48.29, 0.62) * mm});
            skLineSegment(sketch, "E2422", {"start": v(-48.29, 0.62) * mm, "end": v(-48.44, 0.62) * mm});
            skLineSegment(sketch, "E2423", {"start": v(-48.44, 0.62) * mm, "end": v(-48.6, 0.62) * mm});
            skLineSegment(sketch, "E2424", {"start": v(-48.6, 0.62) * mm, "end": v(-48.74, 0.62) * mm});
            skLineSegment(sketch, "E2425", {"start": v(-48.74, 0.62) * mm, "end": v(-48.9, 0.6) * mm});
            skLineSegment(sketch, "E2426", {"start": v(-48.9, 0.6) * mm, "end": v(-49.06, 0.54) * mm});
            skLineSegment(sketch, "E2427", {"start": v(-49.06, 0.54) * mm, "end": v(-49.19, 0.44) * mm});
            skLineSegment(sketch, "E2428", {"start": v(-49.19, 0.44) * mm, "end": v(-49.29, 0.31) * mm});
            skLineSegment(sketch, "E2429", {"start": v(-49.29, 0.31) * mm, "end": v(-49.35, 0.16) * mm});
            skLineSegment(sketch, "E2430", {"start": v(-49.35, 0.16) * mm, "end": v(-49.37, 0) * mm});
            skLineSegment(sketch, "E2431", {"start": v(-49.37, 0) * mm, "end": v(-49.35, -0.16) * mm});
            skLineSegment(sketch, "E2432", {"start": v(-49.35, -0.16) * mm, "end": v(-49.29, -0.31) * mm});
            skLineSegment(sketch, "E2433", {"start": v(-49.29, -0.31) * mm, "end": v(-49.19, -0.44) * mm});
            skLineSegment(sketch, "E2434", {"start": v(-49.19, -0.44) * mm, "end": v(-49.06, -0.54) * mm});
            skLineSegment(sketch, "E2435", {"start": v(-49.06, -0.54) * mm, "end": v(-48.9, -0.6) * mm});
            skLineSegment(sketch, "E2436", {"start": v(-48.9, -0.6) * mm, "end": v(-48.74, -0.63) * mm});
            skLineSegment(sketch, "E2437", {"start": v(-48.74, -0.63) * mm, "end": v(-48.58, -0.62) * mm});
            skLineSegment(sketch, "E2438", {"start": v(-48.58, -0.62) * mm, "end": v(-48.43, -0.62) * mm});
            skLineSegment(sketch, "E2439", {"start": v(-48.43, -0.62) * mm, "end": v(-48.27, -0.62) * mm});
            skLineSegment(sketch, "E2440", {"start": v(-48.27, -0.62) * mm, "end": v(-48.1, -0.62) * mm});
            skLineSegment(sketch, "E2441", {"start": v(-48.1, -0.62) * mm, "end": v(-47.95, -0.62) * mm});
            skLineSegment(sketch, "E2442", {"start": v(-47.95, -0.62) * mm, "end": v(-47.79, -0.61) * mm});
            skLineSegment(sketch, "E2443", {"start": v(-47.79, -0.61) * mm, "end": v(-47.63, -0.61) * mm});
            skLineSegment(sketch, "E2444", {"start": v(-47.63, -0.61) * mm, "end": v(-47.48, -0.6) * mm});
            skLineSegment(sketch, "E2445", {"start": v(-47.48, -0.6) * mm, "end": v(-47.31, -0.6) * mm});
            skLineSegment(sketch, "E2446", {"start": v(-47.31, -0.6) * mm, "end": v(-47.16, -0.6) * mm});
            skLineSegment(sketch, "E2447", {"start": v(-47.16, -0.6) * mm, "end": v(-47, -0.6) * mm});
            skLineSegment(sketch, "E2448", {"start": v(-47, -0.6) * mm, "end": v(-46.84, -0.6) * mm});
            skLineSegment(sketch, "E2449", {"start": v(-46.84, -0.6) * mm, "end": v(-46.7, -0.6) * mm});
            skLineSegment(sketch, "E2450", {"start": v(-46.7, -0.6) * mm, "end": v(-46.7, -0.76) * mm});
            skLineSegment(sketch, "E2451", {"start": v(-46.7, -0.76) * mm, "end": v(-46.7, -0.91) * mm});
            skLineSegment(sketch, "E2452", {"start": v(-46.7, -0.91) * mm, "end": v(-46.69, -1.07) * mm});
            skLineSegment(sketch, "E2453", {"start": v(-46.69, -1.07) * mm, "end": v(-46.68, -1.23) * mm});
            skLineSegment(sketch, "E2454", {"start": v(-46.68, -1.23) * mm, "end": v(-46.68, -1.39) * mm});
            skLineSegment(sketch, "E2455", {"start": v(-46.68, -1.39) * mm, "end": v(-46.67, -1.54) * mm});
            skLineSegment(sketch, "E2456", {"start": v(-46.67, -1.54) * mm, "end": v(-46.67, -1.7) * mm});
            skLineSegment(sketch, "E2457", {"start": v(-46.67, -1.7) * mm, "end": v(-46.66, -1.86) * mm});
            skLineSegment(sketch, "E2458", {"start": v(-46.66, -1.86) * mm, "end": v(-46.66, -2.01) * mm});
            skLineSegment(sketch, "E2459", {"start": v(-46.66, -2.01) * mm, "end": v(-46.65, -2.17) * mm});
            skLineSegment(sketch, "E2460", {"start": v(-46.65, -2.17) * mm, "end": v(-46.65, -2.33) * mm});
            skLineSegment(sketch, "E2461", {"start": v(-46.65, -2.33) * mm, "end": v(-46.64, -2.4) * mm});
            skLineSegment(sketch, "E2462", {"start": v(-46.64, -2.4) * mm, "end": v(-46.8, -2.42) * mm});
            skLineSegment(sketch, "E2463", {"start": v(-46.8, -2.42) * mm, "end": v(-46.96, -2.43) * mm});
            skLineSegment(sketch, "E2464", {"start": v(-46.96, -2.43) * mm, "end": v(-47.12, -2.43) * mm});
            skLineSegment(sketch, "E2465", {"start": v(-47.12, -2.43) * mm, "end": v(-47.28, -2.44) * mm});
            skLineSegment(sketch, "E2466", {"start": v(-47.28, -2.44) * mm, "end": v(-47.43, -2.45) * mm});
            skLineSegment(sketch, "E2467", {"start": v(-47.43, -2.45) * mm, "end": v(-47.6, -2.46) * mm});
            skLineSegment(sketch, "E2468", {"start": v(-47.6, -2.46) * mm, "end": v(-47.75, -2.47) * mm});
            skLineSegment(sketch, "E2469", {"start": v(-47.75, -2.47) * mm, "end": v(-47.9, -2.48) * mm});
            skLineSegment(sketch, "E2470", {"start": v(-47.9, -2.48) * mm, "end": v(-48.07, -2.48) * mm});
            skLineSegment(sketch, "E2471", {"start": v(-48.07, -2.48) * mm, "end": v(-48.23, -2.5) * mm});
            skLineSegment(sketch, "E2472", {"start": v(-48.23, -2.5) * mm, "end": v(-48.38, -2.5) * mm});
            skLineSegment(sketch, "E2473", {"start": v(-48.38, -2.5) * mm, "end": v(-48.54, -2.5) * mm});
            skLineSegment(sketch, "E2474", {"start": v(-48.54, -2.5) * mm, "end": v(-48.71, -2.52) * mm});
            skLineSegment(sketch, "E2475", {"start": v(-48.71, -2.52) * mm, "end": v(-48.87, -2.56) * mm});
            skLineSegment(sketch, "E2476", {"start": v(-48.87, -2.56) * mm, "end": v(-49.02, -2.64) * mm});
            skLineSegment(sketch, "E2477", {"start": v(-49.02, -2.64) * mm, "end": v(-49.13, -2.75) * mm});
            skLineSegment(sketch, "E2478", {"start": v(-49.13, -2.75) * mm, "end": v(-49.22, -2.9) * mm});
            skLineSegment(sketch, "E2479", {"start": v(-49.22, -2.9) * mm, "end": v(-49.26, -3.05) * mm});
            skLineSegment(sketch, "E2480", {"start": v(-49.26, -3.05) * mm, "end": v(-49.26, -3.21) * mm});
            skLineSegment(sketch, "E2481", {"start": v(-49.26, -3.21) * mm, "end": v(-49.22, -3.37) * mm});
            skLineSegment(sketch, "E2482", {"start": v(-49.22, -3.37) * mm, "end": v(-49.14, -3.52) * mm});
            skLineSegment(sketch, "E2483", {"start": v(-49.14, -3.52) * mm, "end": v(-49.03, -3.63) * mm});
            skLineSegment(sketch, "E2484", {"start": v(-49.03, -3.63) * mm, "end": v(-48.89, -3.72) * mm});
            skLineSegment(sketch, "E2485", {"start": v(-48.89, -3.72) * mm, "end": v(-48.73, -3.76) * mm});
            skLineSegment(sketch, "E2486", {"start": v(-48.73, -3.76) * mm, "end": v(-48.57, -3.76) * mm});
            skLineSegment(sketch, "E2487", {"start": v(-48.57, -3.76) * mm, "end": v(-48.42, -3.75) * mm});
            skLineSegment(sketch, "E2488", {"start": v(-48.42, -3.75) * mm, "end": v(-48.26, -3.74) * mm});
            skLineSegment(sketch, "E2489", {"start": v(-48.26, -3.74) * mm, "end": v(-48.1, -3.72) * mm});
            skLineSegment(sketch, "E2490", {"start": v(-48.1, -3.72) * mm, "end": v(-47.95, -3.71) * mm});
            skLineSegment(sketch, "E2491", {"start": v(-47.95, -3.71) * mm, "end": v(-47.78, -3.7) * mm});
            skLineSegment(sketch, "E2492", {"start": v(-47.78, -3.7) * mm, "end": v(-47.63, -3.69) * mm});
            skLineSegment(sketch, "E2493", {"start": v(-47.63, -3.69) * mm, "end": v(-47.47, -3.67) * mm});
            skLineSegment(sketch, "E2494", {"start": v(-47.47, -3.67) * mm, "end": v(-47.31, -3.66) * mm});
            skLineSegment(sketch, "E2495", {"start": v(-47.31, -3.66) * mm, "end": v(-47.15, -3.65) * mm});
            skLineSegment(sketch, "E2496", {"start": v(-47.15, -3.65) * mm, "end": v(-47, -3.64) * mm});
            skLineSegment(sketch, "E2497", {"start": v(-47, -3.64) * mm, "end": v(-46.84, -3.62) * mm});
            skLineSegment(sketch, "E2498", {"start": v(-46.84, -3.62) * mm, "end": v(-46.68, -3.61) * mm});
            skLineSegment(sketch, "E2499", {"start": v(-46.68, -3.61) * mm, "end": v(-46.56, -3.6) * mm});
            skLineSegment(sketch, "E2500", {"start": v(-46.56, -3.6) * mm, "end": v(-46.55, -3.76) * mm});
            skLineSegment(sketch, "E2501", {"start": v(-46.55, -3.76) * mm, "end": v(-46.53, -3.92) * mm});
            skLineSegment(sketch, "E2502", {"start": v(-46.53, -3.92) * mm, "end": v(-46.52, -4.07) * mm});
            skLineSegment(sketch, "E2503", {"start": v(-46.52, -4.07) * mm, "end": v(-46.5, -4.23) * mm});
            skLineSegment(sketch, "E2504", {"start": v(-46.5, -4.23) * mm, "end": v(-46.49, -4.39) * mm});
            skLineSegment(sketch, "E2505", {"start": v(-46.49, -4.39) * mm, "end": v(-46.47, -4.54) * mm});
            skLineSegment(sketch, "E2506", {"start": v(-46.47, -4.54) * mm, "end": v(-46.46, -4.7) * mm});
            skLineSegment(sketch, "E2507", {"start": v(-46.46, -4.7) * mm, "end": v(-46.44, -4.86) * mm});
            skLineSegment(sketch, "E2508", {"start": v(-46.44, -4.86) * mm, "end": v(-46.43, -5.01) * mm});
            skLineSegment(sketch, "E2509", {"start": v(-46.43, -5.01) * mm, "end": v(-46.4, -5.17) * mm});
            skLineSegment(sketch, "E2510", {"start": v(-46.4, -5.17) * mm, "end": v(-46.4, -5.33) * mm});
            skLineSegment(sketch, "E2511", {"start": v(-46.4, -5.33) * mm, "end": v(-46.39, -5.4) * mm});
            skLineSegment(sketch, "E2512", {"start": v(-46.39, -5.4) * mm, "end": v(-46.54, -5.42) * mm});
            skLineSegment(sketch, "E2513", {"start": v(-46.54, -5.42) * mm, "end": v(-46.7, -5.44) * mm});
            skLineSegment(sketch, "E2514", {"start": v(-46.7, -5.44) * mm, "end": v(-46.86, -5.46) * mm});
            skLineSegment(sketch, "E2515", {"start": v(-46.86, -5.46) * mm, "end": v(-47.02, -5.48) * mm});
            skLineSegment(sketch, "E2516", {"start": v(-47.02, -5.48) * mm, "end": v(-47.17, -5.5) * mm});
            skLineSegment(sketch, "E2517", {"start": v(-47.17, -5.5) * mm, "end": v(-47.33, -5.52) * mm});
            skLineSegment(sketch, "E2518", {"start": v(-47.33, -5.52) * mm, "end": v(-47.49, -5.54) * mm});
            skLineSegment(sketch, "E2519", {"start": v(-47.49, -5.54) * mm, "end": v(-47.64, -5.55) * mm});
            skLineSegment(sketch, "E2520", {"start": v(-47.64, -5.55) * mm, "end": v(-47.8, -5.57) * mm});
            skLineSegment(sketch, "E2521", {"start": v(-47.8, -5.57) * mm, "end": v(-47.96, -5.6) * mm});
            skLineSegment(sketch, "E2522", {"start": v(-47.96, -5.6) * mm, "end": v(-48.12, -5.61) * mm});
            skLineSegment(sketch, "E2523", {"start": v(-48.12, -5.61) * mm, "end": v(-48.28, -5.63) * mm});
            skLineSegment(sketch, "E2524", {"start": v(-48.28, -5.63) * mm, "end": v(-48.45, -5.65) * mm});
            skLineSegment(sketch, "E2525", {"start": v(-48.45, -5.65) * mm, "end": v(-48.6, -5.7) * mm});
            skLineSegment(sketch, "E2526", {"start": v(-48.6, -5.7) * mm, "end": v(-48.74, -5.79) * mm});
            skLineSegment(sketch, "E2527", {"start": v(-48.74, -5.79) * mm, "end": v(-48.85, -5.9) * mm});
            skLineSegment(sketch, "E2528", {"start": v(-48.85, -5.9) * mm, "end": v(-48.92, -6.06) * mm});
            skLineSegment(sketch, "E2529", {"start": v(-48.92, -6.06) * mm, "end": v(-48.96, -6.22) * mm});
            skLineSegment(sketch, "E2530", {"start": v(-48.96, -6.22) * mm, "end": v(-48.95, -6.38) * mm});
            skLineSegment(sketch, "E2531", {"start": v(-48.95, -6.38) * mm, "end": v(-48.9, -6.54) * mm});
            skLineSegment(sketch, "E2532", {"start": v(-48.9, -6.54) * mm, "end": v(-48.81, -6.67) * mm});
            skLineSegment(sketch, "E2533", {"start": v(-48.81, -6.67) * mm, "end": v(-48.69, -6.78) * mm});
            skLineSegment(sketch, "E2534", {"start": v(-48.69, -6.78) * mm, "end": v(-48.54, -6.86) * mm});
            skLineSegment(sketch, "E2535", {"start": v(-48.54, -6.86) * mm, "end": v(-48.38, -6.89) * mm});
            skLineSegment(sketch, "E2536", {"start": v(-48.38, -6.89) * mm, "end": v(-48.22, -6.88) * mm});
            skLineSegment(sketch, "E2537", {"start": v(-48.22, -6.88) * mm, "end": v(-48.07, -6.86) * mm});
            skLineSegment(sketch, "E2538", {"start": v(-48.07, -6.86) * mm, "end": v(-47.91, -6.84) * mm});
            skLineSegment(sketch, "E2539", {"start": v(-47.91, -6.84) * mm, "end": v(-47.76, -6.81) * mm});
            skLineSegment(sketch, "E2540", {"start": v(-47.76, -6.81) * mm, "end": v(-47.6, -6.8) * mm});
            skLineSegment(sketch, "E2541", {"start": v(-47.6, -6.8) * mm, "end": v(-47.44, -6.77) * mm});
            skLineSegment(sketch, "E2542", {"start": v(-47.44, -6.77) * mm, "end": v(-47.29, -6.75) * mm});
            skLineSegment(sketch, "E2543", {"start": v(-47.29, -6.75) * mm, "end": v(-47.13, -6.72) * mm});
            skLineSegment(sketch, "E2544", {"start": v(-47.13, -6.72) * mm, "end": v(-46.97, -6.7) * mm});
            skLineSegment(sketch, "E2545", {"start": v(-46.97, -6.7) * mm, "end": v(-46.82, -6.68) * mm});
            skLineSegment(sketch, "E2546", {"start": v(-46.82, -6.68) * mm, "end": v(-46.66, -6.65) * mm});
            skLineSegment(sketch, "E2547", {"start": v(-46.66, -6.65) * mm, "end": v(-46.5, -6.63) * mm});
            skLineSegment(sketch, "E2548", {"start": v(-46.5, -6.63) * mm, "end": v(-46.34, -6.6) * mm});
            skLineSegment(sketch, "E2549", {"start": v(-46.34, -6.6) * mm, "end": v(-46.23, -6.6) * mm});
            skLineSegment(sketch, "E2550", {"start": v(-46.23, -6.6) * mm, "end": v(-46.2, -6.75) * mm});
            skLineSegment(sketch, "E2551", {"start": v(-46.2, -6.75) * mm, "end": v(-46.18, -6.9) * mm});
            skLineSegment(sketch, "E2552", {"start": v(-46.18, -6.9) * mm, "end": v(-46.15, -7.06) * mm});
            skLineSegment(sketch, "E2553", {"start": v(-46.15, -7.06) * mm, "end": v(-46.13, -7.21) * mm});
            skLineSegment(sketch, "E2554", {"start": v(-46.13, -7.21) * mm, "end": v(-46.1, -7.37) * mm});
            skLineSegment(sketch, "E2555", {"start": v(-46.1, -7.37) * mm, "end": v(-46.08, -7.52) * mm});
            skLineSegment(sketch, "E2556", {"start": v(-46.08, -7.52) * mm, "end": v(-46.05, -7.68) * mm});
            skLineSegment(sketch, "E2557", {"start": v(-46.05, -7.68) * mm, "end": v(-46.03, -7.83) * mm});
            skLineSegment(sketch, "E2558", {"start": v(-46.03, -7.83) * mm, "end": v(-46, -7.99) * mm});
            skLineSegment(sketch, "E2559", {"start": v(-46, -7.99) * mm, "end": v(-45.97, -8.14) * mm});
            skLineSegment(sketch, "E2560", {"start": v(-45.97, -8.14) * mm, "end": v(-45.95, -8.3) * mm});
            skLineSegment(sketch, "E2561", {"start": v(-45.95, -8.3) * mm, "end": v(-45.94, -8.38) * mm});
            skLineSegment(sketch, "E2562", {"start": v(-45.94, -8.38) * mm, "end": v(-46.1, -8.4) * mm});
            skLineSegment(sketch, "E2563", {"start": v(-46.1, -8.4) * mm, "end": v(-46.24, -8.44) * mm});
            skLineSegment(sketch, "E2564", {"start": v(-46.24, -8.44) * mm, "end": v(-46.4, -8.47) * mm});
            skLineSegment(sketch, "E2565", {"start": v(-46.4, -8.47) * mm, "end": v(-46.56, -8.5) * mm});
            skLineSegment(sketch, "E2566", {"start": v(-46.56, -8.5) * mm, "end": v(-46.71, -8.52) * mm});
            skLineSegment(sketch, "E2567", {"start": v(-46.71, -8.52) * mm, "end": v(-46.87, -8.55) * mm});
            skLineSegment(sketch, "E2568", {"start": v(-46.87, -8.55) * mm, "end": v(-47.03, -8.58) * mm});
            skLineSegment(sketch, "E2569", {"start": v(-47.03, -8.58) * mm, "end": v(-47.18, -8.6) * mm});
            skLineSegment(sketch, "E2570", {"start": v(-47.18, -8.6) * mm, "end": v(-47.34, -8.64) * mm});
            skLineSegment(sketch, "E2571", {"start": v(-47.34, -8.64) * mm, "end": v(-47.5, -8.67) * mm});
            skLineSegment(sketch, "E2572", {"start": v(-47.5, -8.67) * mm, "end": v(-47.65, -8.7) * mm});
            skLineSegment(sketch, "E2573", {"start": v(-47.65, -8.7) * mm, "end": v(-47.8, -8.73) * mm});
            skLineSegment(sketch, "E2574", {"start": v(-47.8, -8.73) * mm, "end": v(-47.97, -8.76) * mm});
            skLineSegment(sketch, "E2575", {"start": v(-47.97, -8.76) * mm, "end": v(-48.13, -8.82) * mm});
            skLineSegment(sketch, "E2576", {"start": v(-48.13, -8.82) * mm, "end": v(-48.26, -8.92) * mm});
            skLineSegment(sketch, "E2577", {"start": v(-48.26, -8.92) * mm, "end": v(-48.36, -9.04) * mm});
            skLineSegment(sketch, "E2578", {"start": v(-48.36, -9.04) * mm, "end": v(-48.43, -9.2) * mm});
            skLineSegment(sketch, "E2579", {"start": v(-48.43, -9.2) * mm, "end": v(-48.45, -9.36) * mm});
            skLineSegment(sketch, "E2580", {"start": v(-48.45, -9.36) * mm, "end": v(-48.43, -9.52) * mm});
            skLineSegment(sketch, "E2581", {"start": v(-48.43, -9.52) * mm, "end": v(-48.37, -9.67) * mm});
            skLineSegment(sketch, "E2582", {"start": v(-48.37, -9.67) * mm, "end": v(-48.27, -9.8) * mm});
            skLineSegment(sketch, "E2583", {"start": v(-48.27, -9.8) * mm, "end": v(-48.14, -9.9) * mm});
            skLineSegment(sketch, "E2584", {"start": v(-48.14, -9.9) * mm, "end": v(-48, -9.97) * mm});
            skLineSegment(sketch, "E2585", {"start": v(-48, -9.97) * mm, "end": v(-47.83, -10) * mm});
            skLineSegment(sketch, "E2586", {"start": v(-47.83, -10) * mm, "end": v(-47.67, -9.97) * mm});
            skLineSegment(sketch, "E2587", {"start": v(-47.67, -9.97) * mm, "end": v(-47.52, -9.94) * mm});
            skLineSegment(sketch, "E2588", {"start": v(-47.52, -9.94) * mm, "end": v(-47.37, -9.9) * mm});
            skLineSegment(sketch, "E2589", {"start": v(-47.37, -9.9) * mm, "end": v(-47.21, -9.87) * mm});
            skLineSegment(sketch, "E2590", {"start": v(-47.21, -9.87) * mm, "end": v(-47.06, -9.84) * mm});
            skLineSegment(sketch, "E2591", {"start": v(-47.06, -9.84) * mm, "end": v(-46.9, -9.8) * mm});
            skLineSegment(sketch, "E2592", {"start": v(-46.9, -9.8) * mm, "end": v(-46.75, -9.77) * mm});
            skLineSegment(sketch, "E2593", {"start": v(-46.75, -9.77) * mm, "end": v(-46.6, -9.74) * mm});
            skLineSegment(sketch, "E2594", {"start": v(-46.6, -9.74) * mm, "end": v(-46.43, -9.7) * mm});
            skLineSegment(sketch, "E2595", {"start": v(-46.43, -9.7) * mm, "end": v(-46.28, -9.68) * mm});
            skLineSegment(sketch, "E2596", {"start": v(-46.28, -9.68) * mm, "end": v(-46.13, -9.64) * mm});
            skLineSegment(sketch, "E2597", {"start": v(-46.13, -9.64) * mm, "end": v(-45.97, -9.6) * mm});
            skLineSegment(sketch, "E2598", {"start": v(-45.97, -9.6) * mm, "end": v(-45.81, -9.58) * mm});
            skLineSegment(sketch, "E2599", {"start": v(-45.81, -9.58) * mm, "end": v(-45.7, -9.55) * mm});
            skLineSegment(sketch, "E2600", {"start": v(-45.7, -9.55) * mm, "end": v(-45.67, -9.7) * mm});
            skLineSegment(sketch, "E2601", {"start": v(-45.67, -9.7) * mm, "end": v(-45.63, -9.86) * mm});
            skLineSegment(sketch, "E2602", {"start": v(-45.63, -9.86) * mm, "end": v(-45.6, -10.01) * mm});
            skLineSegment(sketch, "E2603", {"start": v(-45.6, -10.01) * mm, "end": v(-45.56, -10.17) * mm});
            skLineSegment(sketch, "E2604", {"start": v(-45.56, -10.17) * mm, "end": v(-45.52, -10.32) * mm});
            skLineSegment(sketch, "E2605", {"start": v(-45.52, -10.32) * mm, "end": v(-45.49, -10.47) * mm});
            skLineSegment(sketch, "E2606", {"start": v(-45.49, -10.47) * mm, "end": v(-45.45, -10.63) * mm});
            skLineSegment(sketch, "E2607", {"start": v(-45.45, -10.63) * mm, "end": v(-45.42, -10.78) * mm});
            skLineSegment(sketch, "E2608", {"start": v(-45.42, -10.78) * mm, "end": v(-45.38, -10.93) * mm});
            skLineSegment(sketch, "E2609", {"start": v(-45.38, -10.93) * mm, "end": v(-45.34, -11.08) * mm});
            skLineSegment(sketch, "E2610", {"start": v(-45.34, -11.08) * mm, "end": v(-45.3, -11.24) * mm});
            skLineSegment(sketch, "E2611", {"start": v(-45.3, -11.24) * mm, "end": v(-45.3, -11.32) * mm});
            skLineSegment(sketch, "E2612", {"start": v(-45.3, -11.32) * mm, "end": v(-45.44, -11.35) * mm});
            skLineSegment(sketch, "E2613", {"start": v(-45.44, -11.35) * mm, "end": v(-45.6, -11.4) * mm});
            skLineSegment(sketch, "E2614", {"start": v(-45.6, -11.4) * mm, "end": v(-45.75, -11.43) * mm});
            skLineSegment(sketch, "E2615", {"start": v(-45.75, -11.43) * mm, "end": v(-45.9, -11.47) * mm});
            skLineSegment(sketch, "E2616", {"start": v(-45.9, -11.47) * mm, "end": v(-46.06, -11.51) * mm});
            skLineSegment(sketch, "E2617", {"start": v(-46.06, -11.51) * mm, "end": v(-46.21, -11.55) * mm});
            skLineSegment(sketch, "E2618", {"start": v(-46.21, -11.55) * mm, "end": v(-46.37, -11.59) * mm});
            skLineSegment(sketch, "E2619", {"start": v(-46.37, -11.59) * mm, "end": v(-46.52, -11.63) * mm});
            skLineSegment(sketch, "E2620", {"start": v(-46.52, -11.63) * mm, "end": v(-46.68, -11.67) * mm});
            skLineSegment(sketch, "E2621", {"start": v(-46.68, -11.67) * mm, "end": v(-46.83, -11.7) * mm});
            skLineSegment(sketch, "E2622", {"start": v(-46.83, -11.7) * mm, "end": v(-46.98, -11.75) * mm});
            skLineSegment(sketch, "E2623", {"start": v(-46.98, -11.75) * mm, "end": v(-47.14, -11.79) * mm});
            skLineSegment(sketch, "E2624", {"start": v(-47.14, -11.79) * mm, "end": v(-47.3, -11.83) * mm});
            skLineSegment(sketch, "E2625", {"start": v(-47.3, -11.83) * mm, "end": v(-47.45, -11.9) * mm});
            skLineSegment(sketch, "E2626", {"start": v(-47.45, -11.9) * mm, "end": v(-47.57, -12) * mm});
            skLineSegment(sketch, "E2627", {"start": v(-47.57, -12) * mm, "end": v(-47.67, -12.14) * mm});
            skLineSegment(sketch, "E2628", {"start": v(-47.67, -12.14) * mm, "end": v(-47.72, -12.3) * mm});
            skLineSegment(sketch, "E2629", {"start": v(-47.72, -12.3) * mm, "end": v(-47.73, -12.46) * mm});
            skLineSegment(sketch, "E2630", {"start": v(-47.73, -12.46) * mm, "end": v(-47.7, -12.62) * mm});
            skLineSegment(sketch, "E2631", {"start": v(-47.7, -12.62) * mm, "end": v(-47.63, -12.76) * mm});
            skLineSegment(sketch, "E2632", {"start": v(-47.63, -12.76) * mm, "end": v(-47.53, -12.89) * mm});
            skLineSegment(sketch, "E2633", {"start": v(-47.53, -12.89) * mm, "end": v(-47.4, -12.98) * mm});
            skLineSegment(sketch, "E2634", {"start": v(-47.4, -12.98) * mm, "end": v(-47.24, -13.04) * mm});
            skLineSegment(sketch, "E2635", {"start": v(-47.24, -13.04) * mm, "end": v(-47.07, -13.05) * mm});
            skLineSegment(sketch, "E2636", {"start": v(-47.07, -13.05) * mm, "end": v(-46.92, -13.02) * mm});
            skLineSegment(sketch, "E2637", {"start": v(-46.92, -13.02) * mm, "end": v(-46.77, -12.98) * mm});
            skLineSegment(sketch, "E2638", {"start": v(-46.77, -12.98) * mm, "end": v(-46.62, -12.93) * mm});
            skLineSegment(sketch, "E2639", {"start": v(-46.62, -12.93) * mm, "end": v(-46.47, -12.9) * mm});
            skLineSegment(sketch, "E2640", {"start": v(-46.47, -12.9) * mm, "end": v(-46.31, -12.85) * mm});
            skLineSegment(sketch, "E2641", {"start": v(-46.31, -12.85) * mm, "end": v(-46.16, -12.8) * mm});
            skLineSegment(sketch, "E2642", {"start": v(-46.16, -12.8) * mm, "end": v(-46, -12.76) * mm});
            skLineSegment(sketch, "E2643", {"start": v(-46, -12.76) * mm, "end": v(-45.86, -12.72) * mm});
            skLineSegment(sketch, "E2644", {"start": v(-45.86, -12.72) * mm, "end": v(-45.7, -12.68) * mm});
            skLineSegment(sketch, "E2645", {"start": v(-45.7, -12.68) * mm, "end": v(-45.55, -12.63) * mm});
            skLineSegment(sketch, "E2646", {"start": v(-45.55, -12.63) * mm, "end": v(-45.4, -12.6) * mm});
            skLineSegment(sketch, "E2647", {"start": v(-45.4, -12.6) * mm, "end": v(-45.24, -12.55) * mm});
            skLineSegment(sketch, "E2648", {"start": v(-45.24, -12.55) * mm, "end": v(-45.1, -12.5) * mm});
            skLineSegment(sketch, "E2649", {"start": v(-45.1, -12.5) * mm, "end": v(-44.98, -12.47) * mm});
            skLineSegment(sketch, "E2650", {"start": v(-44.98, -12.47) * mm, "end": v(-44.94, -12.62) * mm});
            skLineSegment(sketch, "E2651", {"start": v(-44.94, -12.62) * mm, "end": v(-44.89, -12.77) * mm});
            skLineSegment(sketch, "E2652", {"start": v(-44.89, -12.77) * mm, "end": v(-44.84, -12.92) * mm});
            skLineSegment(sketch, "E2653", {"start": v(-44.84, -12.92) * mm, "end": v(-44.8, -13.07) * mm});
            skLineSegment(sketch, "E2654", {"start": v(-44.8, -13.07) * mm, "end": v(-44.75, -13.23) * mm});
            skLineSegment(sketch, "E2655", {"start": v(-44.75, -13.23) * mm, "end": v(-44.7, -13.38) * mm});
            skLineSegment(sketch, "E2656", {"start": v(-44.7, -13.38) * mm, "end": v(-44.66, -13.53) * mm});
            skLineSegment(sketch, "E2657", {"start": v(-44.66, -13.53) * mm, "end": v(-44.62, -13.68) * mm});
            skLineSegment(sketch, "E2658", {"start": v(-44.62, -13.68) * mm, "end": v(-44.57, -13.83) * mm});
            skLineSegment(sketch, "E2659", {"start": v(-44.57, -13.83) * mm, "end": v(-44.52, -13.98) * mm});
            skLineSegment(sketch, "E2660", {"start": v(-44.52, -13.98) * mm, "end": v(-44.48, -14.13) * mm});
            skLineSegment(sketch, "E2661", {"start": v(-44.48, -14.13) * mm, "end": v(-44.46, -14.2) * mm});
            skLineSegment(sketch, "E2662", {"start": v(-44.46, -14.2) * mm, "end": v(-44.6, -14.25) * mm});
            skLineSegment(sketch, "E2663", {"start": v(-44.6, -14.25) * mm, "end": v(-44.75, -14.3) * mm});
            skLineSegment(sketch, "E2664", {"start": v(-44.75, -14.3) * mm, "end": v(-44.9, -14.35) * mm});
            skLineSegment(sketch, "E2665", {"start": v(-44.9, -14.35) * mm, "end": v(-45.06, -14.4) * mm});
            skLineSegment(sketch, "E2666", {"start": v(-45.06, -14.4) * mm, "end": v(-45.2, -14.45) * mm});
            skLineSegment(sketch, "E2667", {"start": v(-45.2, -14.45) * mm, "end": v(-45.36, -14.5) * mm});
            skLineSegment(sketch, "E2668", {"start": v(-45.36, -14.5) * mm, "end": v(-45.51, -14.55) * mm});
            skLineSegment(sketch, "E2669", {"start": v(-45.51, -14.55) * mm, "end": v(-45.66, -14.6) * mm});
            skLineSegment(sketch, "E2670", {"start": v(-45.66, -14.6) * mm, "end": v(-45.81, -14.65) * mm});
            skLineSegment(sketch, "E2671", {"start": v(-45.81, -14.65) * mm, "end": v(-45.96, -14.7) * mm});
            skLineSegment(sketch, "E2672", {"start": v(-45.96, -14.7) * mm, "end": v(-46.11, -14.74) * mm});
            skLineSegment(sketch, "E2673", {"start": v(-46.11, -14.74) * mm, "end": v(-46.27, -14.8) * mm});
            skLineSegment(sketch, "E2674", {"start": v(-46.27, -14.8) * mm, "end": v(-46.43, -14.85) * mm});
            skLineSegment(sketch, "E2675", {"start": v(-46.43, -14.85) * mm, "end": v(-46.57, -14.93) * mm});
            skLineSegment(sketch, "E2676", {"start": v(-46.57, -14.93) * mm, "end": v(-46.69, -15.04) * mm});
            skLineSegment(sketch, "E2677", {"start": v(-46.69, -15.04) * mm, "end": v(-46.77, -15.18) * mm});
            skLineSegment(sketch, "E2678", {"start": v(-46.77, -15.18) * mm, "end": v(-46.82, -15.34) * mm});
            skLineSegment(sketch, "E2679", {"start": v(-46.82, -15.34) * mm, "end": v(-46.82, -15.5) * mm});
            skLineSegment(sketch, "E2680", {"start": v(-46.82, -15.5) * mm, "end": v(-46.78, -15.66) * mm});
            skLineSegment(sketch, "E2681", {"start": v(-46.78, -15.66) * mm, "end": v(-46.7, -15.8) * mm});
            skLineSegment(sketch, "E2682", {"start": v(-46.7, -15.8) * mm, "end": v(-46.58, -15.92) * mm});
            skLineSegment(sketch, "E2683", {"start": v(-46.58, -15.92) * mm, "end": v(-46.44, -16) * mm});
            skLineSegment(sketch, "E2684", {"start": v(-46.44, -16) * mm, "end": v(-46.29, -16.05) * mm});
            skLineSegment(sketch, "E2685", {"start": v(-46.29, -16.05) * mm, "end": v(-46.12, -16.05) * mm});
            skLineSegment(sketch, "E2686", {"start": v(-46.12, -16.05) * mm, "end": v(-45.97, -16) * mm});
            skLineSegment(sketch, "E2687", {"start": v(-45.97, -16) * mm, "end": v(-45.82, -15.96) * mm});
            skLineSegment(sketch, "E2688", {"start": v(-45.82, -15.96) * mm, "end": v(-45.67, -15.9) * mm});
            skLineSegment(sketch, "E2689", {"start": v(-45.67, -15.9) * mm, "end": v(-45.53, -15.85) * mm});
            skLineSegment(sketch, "E2690", {"start": v(-45.53, -15.85) * mm, "end": v(-45.38, -15.8) * mm});
            skLineSegment(sketch, "E2691", {"start": v(-45.38, -15.8) * mm, "end": v(-45.22, -15.75) * mm});
            skLineSegment(sketch, "E2692", {"start": v(-45.22, -15.75) * mm, "end": v(-45.08, -15.7) * mm});
            skLineSegment(sketch, "E2693", {"start": v(-45.08, -15.7) * mm, "end": v(-44.93, -15.64) * mm});
            skLineSegment(sketch, "E2694", {"start": v(-44.93, -15.64) * mm, "end": v(-44.78, -15.59) * mm});
            skLineSegment(sketch, "E2695", {"start": v(-44.78, -15.59) * mm, "end": v(-44.63, -15.54) * mm});
            skLineSegment(sketch, "E2696", {"start": v(-44.63, -15.54) * mm, "end": v(-44.48, -15.48) * mm});
            skLineSegment(sketch, "E2697", {"start": v(-44.48, -15.48) * mm, "end": v(-44.33, -15.43) * mm});
            skLineSegment(sketch, "E2698", {"start": v(-44.33, -15.43) * mm, "end": v(-44.18, -15.38) * mm});
            skLineSegment(sketch, "E2699", {"start": v(-44.18, -15.38) * mm, "end": v(-44.07, -15.34) * mm});
            skLineSegment(sketch, "E2700", {"start": v(-44.07, -15.34) * mm, "end": v(-44.01, -15.49) * mm});
            skLineSegment(sketch, "E2701", {"start": v(-44.01, -15.49) * mm, "end": v(-43.96, -15.63) * mm});
            skLineSegment(sketch, "E2702", {"start": v(-43.96, -15.63) * mm, "end": v(-43.9, -15.78) * mm});
            skLineSegment(sketch, "E2703", {"start": v(-43.9, -15.78) * mm, "end": v(-43.85, -15.93) * mm});
            skLineSegment(sketch, "E2704", {"start": v(-43.85, -15.93) * mm, "end": v(-43.8, -16.08) * mm});
            skLineSegment(sketch, "E2705", {"start": v(-43.8, -16.08) * mm, "end": v(-43.74, -16.22) * mm});
            skLineSegment(sketch, "E2706", {"start": v(-43.74, -16.22) * mm, "end": v(-43.68, -16.37) * mm});
            skLineSegment(sketch, "E2707", {"start": v(-43.68, -16.37) * mm, "end": v(-43.63, -16.52) * mm});
            skLineSegment(sketch, "E2708", {"start": v(-43.63, -16.52) * mm, "end": v(-43.57, -16.66) * mm});
            skLineSegment(sketch, "E2709", {"start": v(-43.57, -16.66) * mm, "end": v(-43.52, -16.81) * mm});
            skLineSegment(sketch, "E2710", {"start": v(-43.52, -16.81) * mm, "end": v(-43.46, -16.96) * mm});
            skLineSegment(sketch, "E2711", {"start": v(-43.46, -16.96) * mm, "end": v(-43.43, -17.03) * mm});
            skLineSegment(sketch, "E2712", {"start": v(-43.43, -17.03) * mm, "end": v(-43.58, -17.1) * mm});
            skLineSegment(sketch, "E2713", {"start": v(-43.58, -17.1) * mm, "end": v(-43.72, -17.15) * mm});
            skLineSegment(sketch, "E2714", {"start": v(-43.72, -17.15) * mm, "end": v(-43.87, -17.21) * mm});
            skLineSegment(sketch, "E2715", {"start": v(-43.87, -17.21) * mm, "end": v(-44.02, -17.27) * mm});
            skLineSegment(sketch, "E2716", {"start": v(-44.02, -17.27) * mm, "end": v(-44.17, -17.33) * mm});
            skLineSegment(sketch, "E2717", {"start": v(-44.17, -17.33) * mm, "end": v(-44.32, -17.39) * mm});
            skLineSegment(sketch, "E2718", {"start": v(-44.32, -17.39) * mm, "end": v(-44.46, -17.44) * mm});
            skLineSegment(sketch, "E2719", {"start": v(-44.46, -17.44) * mm, "end": v(-44.6, -17.5) * mm});
            skLineSegment(sketch, "E2720", {"start": v(-44.6, -17.5) * mm, "end": v(-44.76, -17.56) * mm});
            skLineSegment(sketch, "E2721", {"start": v(-44.76, -17.56) * mm, "end": v(-44.9, -17.62) * mm});
            skLineSegment(sketch, "E2722", {"start": v(-44.9, -17.62) * mm, "end": v(-45.05, -17.68) * mm});
            skLineSegment(sketch, "E2723", {"start": v(-45.05, -17.68) * mm, "end": v(-45.2, -17.74) * mm});
            skLineSegment(sketch, "E2724", {"start": v(-45.2, -17.74) * mm, "end": v(-45.36, -17.8) * mm});
            skLineSegment(sketch, "E2725", {"start": v(-45.36, -17.8) * mm, "end": v(-45.5, -17.9) * mm});
            skLineSegment(sketch, "E2726", {"start": v(-45.5, -17.9) * mm, "end": v(-45.6, -18.01) * mm});
            skLineSegment(sketch, "E2727", {"start": v(-45.6, -18.01) * mm, "end": v(-45.68, -18.16) * mm});
            skLineSegment(sketch, "E2728", {"start": v(-45.68, -18.16) * mm, "end": v(-45.72, -18.32) * mm});
            skLineSegment(sketch, "E2729", {"start": v(-45.72, -18.32) * mm, "end": v(-45.7, -18.48) * mm});
            skLineSegment(sketch, "E2730", {"start": v(-45.7, -18.48) * mm, "end": v(-45.66, -18.64) * mm});
            skLineSegment(sketch, "E2731", {"start": v(-45.66, -18.64) * mm, "end": v(-45.57, -18.78) * mm});
            skLineSegment(sketch, "E2732", {"start": v(-45.57, -18.78) * mm, "end": v(-45.45, -18.89) * mm});
            skLineSegment(sketch, "E2733", {"start": v(-45.45, -18.89) * mm, "end": v(-45.3, -18.96) * mm});
            skLineSegment(sketch, "E2734", {"start": v(-45.3, -18.96) * mm, "end": v(-45.14, -19) * mm});
            skLineSegment(sketch, "E2735", {"start": v(-45.14, -19) * mm, "end": v(-44.98, -18.98) * mm});
            skLineSegment(sketch, "E2736", {"start": v(-44.98, -18.98) * mm, "end": v(-44.83, -18.93) * mm});
            skLineSegment(sketch, "E2737", {"start": v(-44.83, -18.93) * mm, "end": v(-44.68, -18.87) * mm});
            skLineSegment(sketch, "E2738", {"start": v(-44.68, -18.87) * mm, "end": v(-44.54, -18.81) * mm});
            skLineSegment(sketch, "E2739", {"start": v(-44.54, -18.81) * mm, "end": v(-44.4, -18.75) * mm});
            skLineSegment(sketch, "E2740", {"start": v(-44.4, -18.75) * mm, "end": v(-44.25, -18.69) * mm});
            skLineSegment(sketch, "E2741", {"start": v(-44.25, -18.69) * mm, "end": v(-44.1, -18.62) * mm});
            skLineSegment(sketch, "E2742", {"start": v(-44.1, -18.62) * mm, "end": v(-43.95, -18.56) * mm});
            skLineSegment(sketch, "E2743", {"start": v(-43.95, -18.56) * mm, "end": v(-43.81, -18.5) * mm});
            skLineSegment(sketch, "E2744", {"start": v(-43.81, -18.5) * mm, "end": v(-43.66, -18.44) * mm});
            skLineSegment(sketch, "E2745", {"start": v(-43.66, -18.44) * mm, "end": v(-43.52, -18.37) * mm});
            skLineSegment(sketch, "E2746", {"start": v(-43.52, -18.37) * mm, "end": v(-43.37, -18.31) * mm});
            skLineSegment(sketch, "E2747", {"start": v(-43.37, -18.31) * mm, "end": v(-43.22, -18.25) * mm});
            skLineSegment(sketch, "E2748", {"start": v(-43.22, -18.25) * mm, "end": v(-43.08, -18.19) * mm});
            skLineSegment(sketch, "E2749", {"start": v(-43.08, -18.19) * mm, "end": v(-42.97, -18.14) * mm});
            skLineSegment(sketch, "E2750", {"start": v(-42.97, -18.14) * mm, "end": v(-42.9, -18.28) * mm});
            skLineSegment(sketch, "E2751", {"start": v(-42.9, -18.28) * mm, "end": v(-42.84, -18.43) * mm});
            skLineSegment(sketch, "E2752", {"start": v(-42.84, -18.43) * mm, "end": v(-42.78, -18.57) * mm});
            skLineSegment(sketch, "E2753", {"start": v(-42.78, -18.57) * mm, "end": v(-42.71, -18.71) * mm});
            skLineSegment(sketch, "E2754", {"start": v(-42.71, -18.71) * mm, "end": v(-42.65, -18.86) * mm});
            skLineSegment(sketch, "E2755", {"start": v(-42.65, -18.86) * mm, "end": v(-42.58, -19) * mm});
            skLineSegment(sketch, "E2756", {"start": v(-42.58, -19) * mm, "end": v(-42.52, -19.14) * mm});
            skLineSegment(sketch, "E2757", {"start": v(-42.52, -19.14) * mm, "end": v(-42.46, -19.29) * mm});
            skLineSegment(sketch, "E2758", {"start": v(-42.46, -19.29) * mm, "end": v(-42.4, -19.43) * mm});
            skLineSegment(sketch, "E2759", {"start": v(-42.4, -19.43) * mm, "end": v(-42.33, -19.57) * mm});
            skLineSegment(sketch, "E2760", {"start": v(-42.33, -19.57) * mm, "end": v(-42.26, -19.72) * mm});
            skLineSegment(sketch, "E2761", {"start": v(-42.26, -19.72) * mm, "end": v(-42.23, -19.79) * mm});
            skLineSegment(sketch, "E2762", {"start": v(-42.23, -19.79) * mm, "end": v(-42.37, -19.86) * mm});
            skLineSegment(sketch, "E2763", {"start": v(-42.37, -19.86) * mm, "end": v(-42.51, -19.92) * mm});
            skLineSegment(sketch, "E2764", {"start": v(-42.51, -19.92) * mm, "end": v(-42.66, -20) * mm});
            skLineSegment(sketch, "E2765", {"start": v(-42.66, -20) * mm, "end": v(-42.8, -20.06) * mm});
            skLineSegment(sketch, "E2766", {"start": v(-42.8, -20.06) * mm, "end": v(-42.94, -20.13) * mm});
            skLineSegment(sketch, "E2767", {"start": v(-42.94, -20.13) * mm, "end": v(-43.09, -20.2) * mm});
            skLineSegment(sketch, "E2768", {"start": v(-43.09, -20.2) * mm, "end": v(-43.23, -20.27) * mm});
            skLineSegment(sketch, "E2769", {"start": v(-43.23, -20.27) * mm, "end": v(-43.37, -20.33) * mm});
            skLineSegment(sketch, "E2770", {"start": v(-43.37, -20.33) * mm, "end": v(-43.52, -20.4) * mm});
            skLineSegment(sketch, "E2771", {"start": v(-43.52, -20.4) * mm, "end": v(-43.66, -20.47) * mm});
            skLineSegment(sketch, "E2772", {"start": v(-43.66, -20.47) * mm, "end": v(-43.8, -20.54) * mm});
            skLineSegment(sketch, "E2773", {"start": v(-43.8, -20.54) * mm, "end": v(-43.95, -20.6) * mm});
            skLineSegment(sketch, "E2774", {"start": v(-43.95, -20.6) * mm, "end": v(-44.1, -20.68) * mm});
            skLineSegment(sketch, "E2775", {"start": v(-44.1, -20.68) * mm, "end": v(-44.23, -20.78) * mm});
            skLineSegment(sketch, "E2776", {"start": v(-44.23, -20.78) * mm, "end": v(-44.33, -20.9) * mm});
            skLineSegment(sketch, "E2777", {"start": v(-44.33, -20.9) * mm, "end": v(-44.4, -21.06) * mm});
            skLineSegment(sketch, "E2778", {"start": v(-44.4, -21.06) * mm, "end": v(-44.42, -21.22) * mm});
            skLineSegment(sketch, "E2779", {"start": v(-44.42, -21.22) * mm, "end": v(-44.4, -21.38) * mm});
            skLineSegment(sketch, "E2780", {"start": v(-44.4, -21.38) * mm, "end": v(-44.34, -21.54) * mm});
            skLineSegment(sketch, "E2781", {"start": v(-44.34, -21.54) * mm, "end": v(-44.24, -21.67) * mm});
            skLineSegment(sketch, "E2782", {"start": v(-44.24, -21.67) * mm, "end": v(-44.11, -21.77) * mm});
            skLineSegment(sketch, "E2783", {"start": v(-44.11, -21.77) * mm, "end": v(-43.96, -21.83) * mm});
            skLineSegment(sketch, "E2784", {"start": v(-43.96, -21.83) * mm, "end": v(-43.8, -21.86) * mm});
            skLineSegment(sketch, "E2785", {"start": v(-43.8, -21.86) * mm, "end": v(-43.64, -21.84) * mm});
            skLineSegment(sketch, "E2786", {"start": v(-43.64, -21.84) * mm, "end": v(-43.5, -21.77) * mm});
            skLineSegment(sketch, "E2787", {"start": v(-43.5, -21.77) * mm, "end": v(-43.35, -21.7) * mm});
            skLineSegment(sketch, "E2788", {"start": v(-43.35, -21.7) * mm, "end": v(-43.21, -21.63) * mm});
            skLineSegment(sketch, "E2789", {"start": v(-43.21, -21.63) * mm, "end": v(-43.07, -21.56) * mm});
            skLineSegment(sketch, "E2790", {"start": v(-43.07, -21.56) * mm, "end": v(-42.93, -21.5) * mm});
            skLineSegment(sketch, "E2791", {"start": v(-42.93, -21.5) * mm, "end": v(-42.79, -21.42) * mm});
            skLineSegment(sketch, "E2792", {"start": v(-42.79, -21.42) * mm, "end": v(-42.65, -21.35) * mm});
            skLineSegment(sketch, "E2793", {"start": v(-42.65, -21.35) * mm, "end": v(-42.5, -21.28) * mm});
            skLineSegment(sketch, "E2794", {"start": v(-42.5, -21.28) * mm, "end": v(-42.36, -21.2) * mm});
            skLineSegment(sketch, "E2795", {"start": v(-42.36, -21.2) * mm, "end": v(-42.22, -21.13) * mm});
            skLineSegment(sketch, "E2796", {"start": v(-42.22, -21.13) * mm, "end": v(-42.08, -21.06) * mm});
            skLineSegment(sketch, "E2797", {"start": v(-42.08, -21.06) * mm, "end": v(-41.94, -20.99) * mm});
            skLineSegment(sketch, "E2798", {"start": v(-41.94, -20.99) * mm, "end": v(-41.8, -20.92) * mm});
            skLineSegment(sketch, "E2799", {"start": v(-41.8, -20.92) * mm, "end": v(-41.7, -20.86) * mm});
            skLineSegment(sketch, "E2800", {"start": v(-41.7, -20.86) * mm, "end": v(-41.62, -21) * mm});
            skLineSegment(sketch, "E2801", {"start": v(-41.62, -21) * mm, "end": v(-41.55, -21.14) * mm});
            skLineSegment(sketch, "E2802", {"start": v(-41.55, -21.14) * mm, "end": v(-41.48, -21.28) * mm});
            skLineSegment(sketch, "E2803", {"start": v(-41.48, -21.28) * mm, "end": v(-41.4, -21.42) * mm});
            skLineSegment(sketch, "E2804", {"start": v(-41.4, -21.42) * mm, "end": v(-41.33, -21.56) * mm});
            skLineSegment(sketch, "E2805", {"start": v(-41.33, -21.56) * mm, "end": v(-41.25, -21.7) * mm});
            skLineSegment(sketch, "E2806", {"start": v(-41.25, -21.7) * mm, "end": v(-41.18, -21.83) * mm});
            skLineSegment(sketch, "E2807", {"start": v(-41.18, -21.83) * mm, "end": v(-41.1, -21.97) * mm});
            skLineSegment(sketch, "E2808", {"start": v(-41.1, -21.97) * mm, "end": v(-41.03, -22.11) * mm});
            skLineSegment(sketch, "E2809", {"start": v(-41.03, -22.11) * mm, "end": v(-40.96, -22.25) * mm});
            skLineSegment(sketch, "E2810", {"start": v(-40.96, -22.25) * mm, "end": v(-40.88, -22.39) * mm});
            skLineSegment(sketch, "E2811", {"start": v(-40.88, -22.39) * mm, "end": v(-40.84, -22.46) * mm});
            skLineSegment(sketch, "E2812", {"start": v(-40.84, -22.46) * mm, "end": v(-40.98, -22.54) * mm});
            skLineSegment(sketch, "E2813", {"start": v(-40.98, -22.54) * mm, "end": v(-41.12, -22.61) * mm});
            skLineSegment(sketch, "E2814", {"start": v(-41.12, -22.61) * mm, "end": v(-41.26, -22.7) * mm});
            skLineSegment(sketch, "E2815", {"start": v(-41.26, -22.7) * mm, "end": v(-41.4, -22.77) * mm});
            skLineSegment(sketch, "E2816", {"start": v(-41.4, -22.77) * mm, "end": v(-41.53, -22.85) * mm});
            skLineSegment(sketch, "E2817", {"start": v(-41.53, -22.85) * mm, "end": v(-41.68, -22.93) * mm});
            skLineSegment(sketch, "E2818", {"start": v(-41.68, -22.93) * mm, "end": v(-41.81, -23) * mm});
            skLineSegment(sketch, "E2819", {"start": v(-41.81, -23) * mm, "end": v(-41.95, -23.08) * mm});
            skLineSegment(sketch, "E2820", {"start": v(-41.95, -23.08) * mm, "end": v(-42.1, -23.16) * mm});
            skLineSegment(sketch, "E2821", {"start": v(-42.1, -23.16) * mm, "end": v(-42.23, -23.23) * mm});
            skLineSegment(sketch, "E2822", {"start": v(-42.23, -23.23) * mm, "end": v(-42.36, -23.31) * mm});
            skLineSegment(sketch, "E2823", {"start": v(-42.36, -23.31) * mm, "end": v(-42.5, -23.4) * mm});
            skLineSegment(sketch, "E2824", {"start": v(-42.5, -23.4) * mm, "end": v(-42.65, -23.47) * mm});
            skLineSegment(sketch, "E2825", {"start": v(-42.65, -23.47) * mm, "end": v(-42.78, -23.58) * mm});
            skLineSegment(sketch, "E2826", {"start": v(-42.78, -23.58) * mm, "end": v(-42.87, -23.71) * mm});
            skLineSegment(sketch, "E2827", {"start": v(-42.87, -23.71) * mm, "end": v(-42.93, -23.87) * mm});
            skLineSegment(sketch, "E2828", {"start": v(-42.93, -23.87) * mm, "end": v(-42.94, -24.03) * mm});
            skLineSegment(sketch, "E2829", {"start": v(-42.94, -24.03) * mm, "end": v(-42.91, -24.2) * mm});
            skLineSegment(sketch, "E2830", {"start": v(-42.91, -24.2) * mm, "end": v(-42.84, -24.34) * mm});
            skLineSegment(sketch, "E2831", {"start": v(-42.84, -24.34) * mm, "end": v(-42.73, -24.47) * mm});
            skLineSegment(sketch, "E2832", {"start": v(-42.73, -24.47) * mm, "end": v(-42.6, -24.56) * mm});
            skLineSegment(sketch, "E2833", {"start": v(-42.6, -24.56) * mm, "end": v(-42.44, -24.61) * mm});
            skLineSegment(sketch, "E2834", {"start": v(-42.44, -24.61) * mm, "end": v(-42.28, -24.62) * mm});
            skLineSegment(sketch, "E2835", {"start": v(-42.28, -24.62) * mm, "end": v(-42.12, -24.6) * mm});
            skLineSegment(sketch, "E2836", {"start": v(-42.12, -24.6) * mm, "end": v(-41.98, -24.52) * mm});
            skLineSegment(sketch, "E2837", {"start": v(-41.98, -24.52) * mm, "end": v(-41.84, -24.45) * mm});
            skLineSegment(sketch, "E2838", {"start": v(-41.84, -24.45) * mm, "end": v(-41.7, -24.37) * mm});
            skLineSegment(sketch, "E2839", {"start": v(-41.7, -24.37) * mm, "end": v(-41.57, -24.29) * mm});
            skLineSegment(sketch, "E2840", {"start": v(-41.57, -24.29) * mm, "end": v(-41.44, -24.2) * mm});
            skLineSegment(sketch, "E2841", {"start": v(-41.44, -24.2) * mm, "end": v(-41.3, -24.12) * mm});
            skLineSegment(sketch, "E2842", {"start": v(-41.3, -24.12) * mm, "end": v(-41.16, -24.04) * mm});
            skLineSegment(sketch, "E2843", {"start": v(-41.16, -24.04) * mm, "end": v(-41.03, -23.96) * mm});
            skLineSegment(sketch, "E2844", {"start": v(-41.03, -23.96) * mm, "end": v(-40.89, -23.88) * mm});
            skLineSegment(sketch, "E2845", {"start": v(-40.89, -23.88) * mm, "end": v(-40.75, -23.8) * mm});
            skLineSegment(sketch, "E2846", {"start": v(-40.75, -23.8) * mm, "end": v(-40.62, -23.72) * mm});
            skLineSegment(sketch, "E2847", {"start": v(-40.62, -23.72) * mm, "end": v(-40.48, -23.64) * mm});
            skLineSegment(sketch, "E2848", {"start": v(-40.48, -23.64) * mm, "end": v(-40.34, -23.56) * mm});
            skLineSegment(sketch, "E2849", {"start": v(-40.34, -23.56) * mm, "end": v(-40.25, -23.5) * mm});
            skLineSegment(sketch, "E2850", {"start": v(-40.25, -23.5) * mm, "end": v(-40.16, -23.63) * mm});
            skLineSegment(sketch, "E2851", {"start": v(-40.16, -23.63) * mm, "end": v(-40.08, -23.76) * mm});
            skLineSegment(sketch, "E2852", {"start": v(-40.08, -23.76) * mm, "end": v(-40, -23.9) * mm});
            skLineSegment(sketch, "E2853", {"start": v(-40, -23.9) * mm, "end": v(-39.91, -24.03) * mm});
            skLineSegment(sketch, "E2854", {"start": v(-39.91, -24.03) * mm, "end": v(-39.83, -24.16) * mm});
            skLineSegment(sketch, "E2855", {"start": v(-39.83, -24.16) * mm, "end": v(-39.75, -24.3) * mm});
            skLineSegment(sketch, "E2856", {"start": v(-39.75, -24.3) * mm, "end": v(-39.66, -24.43) * mm});
            skLineSegment(sketch, "E2857", {"start": v(-39.66, -24.43) * mm, "end": v(-39.58, -24.57) * mm});
            skLineSegment(sketch, "E2858", {"start": v(-39.58, -24.57) * mm, "end": v(-39.5, -24.7) * mm});
            skLineSegment(sketch, "E2859", {"start": v(-39.5, -24.7) * mm, "end": v(-39.41, -24.83) * mm});
            skLineSegment(sketch, "E2860", {"start": v(-39.41, -24.83) * mm, "end": v(-39.33, -24.97) * mm});
            skLineSegment(sketch, "E2861", {"start": v(-39.33, -24.97) * mm, "end": v(-39.29, -25.03) * mm});
            skLineSegment(sketch, "E2862", {"start": v(-39.29, -25.03) * mm, "end": v(-39.42, -25.12) * mm});
            skLineSegment(sketch, "E2863", {"start": v(-39.42, -25.12) * mm, "end": v(-39.55, -25.2) * mm});
            skLineSegment(sketch, "E2864", {"start": v(-39.55, -25.2) * mm, "end": v(-39.69, -25.3) * mm});
            skLineSegment(sketch, "E2865", {"start": v(-39.69, -25.3) * mm, "end": v(-39.82, -25.38) * mm});
            skLineSegment(sketch, "E2866", {"start": v(-39.82, -25.38) * mm, "end": v(-39.95, -25.46) * mm});
            skLineSegment(sketch, "E2867", {"start": v(-39.95, -25.46) * mm, "end": v(-40.09, -25.55) * mm});
            skLineSegment(sketch, "E2868", {"start": v(-40.09, -25.55) * mm, "end": v(-40.22, -25.64) * mm});
            skLineSegment(sketch, "E2869", {"start": v(-40.22, -25.64) * mm, "end": v(-40.35, -25.72) * mm});
            skLineSegment(sketch, "E2870", {"start": v(-40.35, -25.72) * mm, "end": v(-40.49, -25.81) * mm});
            skLineSegment(sketch, "E2871", {"start": v(-40.49, -25.81) * mm, "end": v(-40.62, -25.9) * mm});
            skLineSegment(sketch, "E2872", {"start": v(-40.62, -25.9) * mm, "end": v(-40.75, -25.98) * mm});
            skLineSegment(sketch, "E2873", {"start": v(-40.75, -25.98) * mm, "end": v(-40.89, -26.07) * mm});
            skLineSegment(sketch, "E2874", {"start": v(-40.89, -26.07) * mm, "end": v(-41.03, -26.16) * mm});
            skLineSegment(sketch, "E2875", {"start": v(-41.03, -26.16) * mm, "end": v(-41.15, -26.28) * mm});
            skLineSegment(sketch, "E2876", {"start": v(-41.15, -26.28) * mm, "end": v(-41.23, -26.42) * mm});
            skLineSegment(sketch, "E2877", {"start": v(-41.23, -26.42) * mm, "end": v(-41.28, -26.58) * mm});
            skLineSegment(sketch, "E2878", {"start": v(-41.28, -26.58) * mm, "end": v(-41.28, -26.74) * mm});
            skLineSegment(sketch, "E2879", {"start": v(-41.28, -26.74) * mm, "end": v(-41.24, -26.9) * mm});
            skLineSegment(sketch, "E2880", {"start": v(-41.24, -26.9) * mm, "end": v(-41.16, -27.04) * mm});
            skLineSegment(sketch, "E2881", {"start": v(-41.16, -27.04) * mm, "end": v(-41.04, -27.16) * mm});
            skLineSegment(sketch, "E2882", {"start": v(-41.04, -27.16) * mm, "end": v(-40.9, -27.24) * mm});
            skLineSegment(sketch, "E2883", {"start": v(-40.9, -27.24) * mm, "end": v(-40.74, -27.29) * mm});
            skLineSegment(sketch, "E2884", {"start": v(-40.74, -27.29) * mm, "end": v(-40.58, -27.29) * mm});
            skLineSegment(sketch, "E2885", {"start": v(-40.58, -27.29) * mm, "end": v(-40.42, -27.25) * mm});
            skLineSegment(sketch, "E2886", {"start": v(-40.42, -27.25) * mm, "end": v(-40.29, -27.17) * mm});
            skLineSegment(sketch, "E2887", {"start": v(-40.29, -27.17) * mm, "end": v(-40.15, -27.08) * mm});
            skLineSegment(sketch, "E2888", {"start": v(-40.15, -27.08) * mm, "end": v(-40.03, -27) * mm});
            skLineSegment(sketch, "E2889", {"start": v(-40.03, -27) * mm, "end": v(-39.9, -26.9) * mm});
            skLineSegment(sketch, "E2890", {"start": v(-39.9, -26.9) * mm, "end": v(-39.77, -26.81) * mm});
            skLineSegment(sketch, "E2891", {"start": v(-39.77, -26.81) * mm, "end": v(-39.63, -26.72) * mm});
            skLineSegment(sketch, "E2892", {"start": v(-39.63, -26.72) * mm, "end": v(-39.5, -26.63) * mm});
            skLineSegment(sketch, "E2893", {"start": v(-39.5, -26.63) * mm, "end": v(-39.37, -26.54) * mm});
            skLineSegment(sketch, "E2894", {"start": v(-39.37, -26.54) * mm, "end": v(-39.24, -26.45) * mm});
            skLineSegment(sketch, "E2895", {"start": v(-39.24, -26.45) * mm, "end": v(-39.11, -26.36) * mm});
            skLineSegment(sketch, "E2896", {"start": v(-39.11, -26.36) * mm, "end": v(-38.98, -26.28) * mm});
            skLineSegment(sketch, "E2897", {"start": v(-38.98, -26.28) * mm, "end": v(-38.85, -26.18) * mm});
            skLineSegment(sketch, "E2898", {"start": v(-38.85, -26.18) * mm, "end": v(-38.72, -26.1) * mm});
            skLineSegment(sketch, "E2899", {"start": v(-38.72, -26.1) * mm, "end": v(-38.62, -26.03) * mm});
            skLineSegment(sketch, "E2900", {"start": v(-38.62, -26.03) * mm, "end": v(-38.53, -26.16) * mm});
            skLineSegment(sketch, "E2901", {"start": v(-38.53, -26.16) * mm, "end": v(-38.44, -26.29) * mm});
            skLineSegment(sketch, "E2902", {"start": v(-38.44, -26.29) * mm, "end": v(-38.35, -26.41) * mm});
            skLineSegment(sketch, "E2903", {"start": v(-38.35, -26.41) * mm, "end": v(-38.26, -26.54) * mm});
            skLineSegment(sketch, "E2904", {"start": v(-38.26, -26.54) * mm, "end": v(-38.17, -26.67) * mm});
            skLineSegment(sketch, "E2905", {"start": v(-38.17, -26.67) * mm, "end": v(-38.07, -26.8) * mm});
            skLineSegment(sketch, "E2906", {"start": v(-38.07, -26.8) * mm, "end": v(-37.98, -26.92) * mm});
            skLineSegment(sketch, "E2907", {"start": v(-37.98, -26.92) * mm, "end": v(-37.9, -27.05) * mm});
            skLineSegment(sketch, "E2908", {"start": v(-37.9, -27.05) * mm, "end": v(-37.8, -27.18) * mm});
            skLineSegment(sketch, "E2909", {"start": v(-37.8, -27.18) * mm, "end": v(-37.7, -27.3) * mm});
            skLineSegment(sketch, "E2910", {"start": v(-37.7, -27.3) * mm, "end": v(-37.62, -27.44) * mm});
            skLineSegment(sketch, "E2911", {"start": v(-37.62, -27.44) * mm, "end": v(-37.57, -27.5) * mm});
            skLineSegment(sketch, "E2912", {"start": v(-37.57, -27.5) * mm, "end": v(-37.7, -27.6) * mm});
            skLineSegment(sketch, "E2913", {"start": v(-37.7, -27.6) * mm, "end": v(-37.82, -27.69) * mm});
            skLineSegment(sketch, "E2914", {"start": v(-37.82, -27.69) * mm, "end": v(-37.95, -27.79) * mm});
            skLineSegment(sketch, "E2915", {"start": v(-37.95, -27.79) * mm, "end": v(-38.08, -27.88) * mm});
            skLineSegment(sketch, "E2916", {"start": v(-38.08, -27.88) * mm, "end": v(-38.2, -27.97) * mm});
            skLineSegment(sketch, "E2917", {"start": v(-38.2, -27.97) * mm, "end": v(-38.33, -28.07) * mm});
            skLineSegment(sketch, "E2918", {"start": v(-38.33, -28.07) * mm, "end": v(-38.46, -28.17) * mm});
            skLineSegment(sketch, "E2919", {"start": v(-38.46, -28.17) * mm, "end": v(-38.58, -28.26) * mm});
            skLineSegment(sketch, "E2920", {"start": v(-38.58, -28.26) * mm, "end": v(-38.71, -28.36) * mm});
            skLineSegment(sketch, "E2921", {"start": v(-38.71, -28.36) * mm, "end": v(-38.84, -28.45) * mm});
            skLineSegment(sketch, "E2922", {"start": v(-38.84, -28.45) * mm, "end": v(-38.97, -28.54) * mm});
            skLineSegment(sketch, "E2923", {"start": v(-38.97, -28.54) * mm, "end": v(-39.1, -28.64) * mm});
            skLineSegment(sketch, "E2924", {"start": v(-39.1, -28.64) * mm, "end": v(-39.23, -28.74) * mm});
            skLineSegment(sketch, "E2925", {"start": v(-39.23, -28.74) * mm, "end": v(-39.34, -28.86) * mm});
            skLineSegment(sketch, "E2926", {"start": v(-39.34, -28.86) * mm, "end": v(-39.42, -29) * mm});
            skLineSegment(sketch, "E2927", {"start": v(-39.42, -29) * mm, "end": v(-39.45, -29.17) * mm});
            skLineSegment(sketch, "E2928", {"start": v(-39.45, -29.17) * mm, "end": v(-39.44, -29.33) * mm});
            skLineSegment(sketch, "E2929", {"start": v(-39.44, -29.33) * mm, "end": v(-39.4, -29.49) * mm});
            skLineSegment(sketch, "E2930", {"start": v(-39.4, -29.49) * mm, "end": v(-39.3, -29.63) * mm});
            skLineSegment(sketch, "E2931", {"start": v(-39.3, -29.63) * mm, "end": v(-39.18, -29.74) * mm});
            skLineSegment(sketch, "E2932", {"start": v(-39.18, -29.74) * mm, "end": v(-39.03, -29.81) * mm});
            skLineSegment(sketch, "E2933", {"start": v(-39.03, -29.81) * mm, "end": v(-38.87, -29.84) * mm});
            skLineSegment(sketch, "E2934", {"start": v(-38.87, -29.84) * mm, "end": v(-38.71, -29.84) * mm});
            skLineSegment(sketch, "E2935", {"start": v(-38.71, -29.84) * mm, "end": v(-38.55, -29.78) * mm});
            skLineSegment(sketch, "E2936", {"start": v(-38.55, -29.78) * mm, "end": v(-38.42, -29.7) * mm});
            skLineSegment(sketch, "E2937", {"start": v(-38.42, -29.7) * mm, "end": v(-38.3, -29.6) * mm});
            skLineSegment(sketch, "E2938", {"start": v(-38.3, -29.6) * mm, "end": v(-38.18, -29.5) * mm});
            skLineSegment(sketch, "E2939", {"start": v(-38.18, -29.5) * mm, "end": v(-38.05, -29.4) * mm});
            skLineSegment(sketch, "E2940", {"start": v(-38.05, -29.4) * mm, "end": v(-37.93, -29.3) * mm});
            skLineSegment(sketch, "E2941", {"start": v(-37.93, -29.3) * mm, "end": v(-37.8, -29.2) * mm});
            skLineSegment(sketch, "E2942", {"start": v(-37.8, -29.2) * mm, "end": v(-37.68, -29.11) * mm});
            skLineSegment(sketch, "E2943", {"start": v(-37.68, -29.11) * mm, "end": v(-37.56, -29.01) * mm});
            skLineSegment(sketch, "E2944", {"start": v(-37.56, -29.01) * mm, "end": v(-37.43, -28.91) * mm});
            skLineSegment(sketch, "E2945", {"start": v(-37.43, -28.91) * mm, "end": v(-37.3, -28.82) * mm});
            skLineSegment(sketch, "E2946", {"start": v(-37.3, -28.82) * mm, "end": v(-37.18, -28.72) * mm});
            skLineSegment(sketch, "E2947", {"start": v(-37.18, -28.72) * mm, "end": v(-37.05, -28.62) * mm});
            skLineSegment(sketch, "E2948", {"start": v(-37.05, -28.62) * mm, "end": v(-36.93, -28.52) * mm});
            skLineSegment(sketch, "E2949", {"start": v(-36.93, -28.52) * mm, "end": v(-36.84, -28.45) * mm});
            skLineSegment(sketch, "E2950", {"start": v(-36.84, -28.45) * mm, "end": v(-36.74, -28.57) * mm});
            skLineSegment(sketch, "E2951", {"start": v(-36.74, -28.57) * mm, "end": v(-36.64, -28.7) * mm});
            skLineSegment(sketch, "E2952", {"start": v(-36.64, -28.7) * mm, "end": v(-36.54, -28.82) * mm});
            skLineSegment(sketch, "E2953", {"start": v(-36.54, -28.82) * mm, "end": v(-36.44, -28.94) * mm});
            skLineSegment(sketch, "E2954", {"start": v(-36.44, -28.94) * mm, "end": v(-36.34, -29.06) * mm});
            skLineSegment(sketch, "E2955", {"start": v(-36.34, -29.06) * mm, "end": v(-36.24, -29.18) * mm});
            skLineSegment(sketch, "E2956", {"start": v(-36.24, -29.18) * mm, "end": v(-36.14, -29.3) * mm});
            skLineSegment(sketch, "E2957", {"start": v(-36.14, -29.3) * mm, "end": v(-36.04, -29.42) * mm});
            skLineSegment(sketch, "E2958", {"start": v(-36.04, -29.42) * mm, "end": v(-35.94, -29.55) * mm});
            skLineSegment(sketch, "E2959", {"start": v(-35.94, -29.55) * mm, "end": v(-35.84, -29.67) * mm});
            skLineSegment(sketch, "E2960", {"start": v(-35.84, -29.67) * mm, "end": v(-35.74, -29.79) * mm});
            skLineSegment(sketch, "E2961", {"start": v(-35.74, -29.79) * mm, "end": v(-35.7, -29.85) * mm});
            skLineSegment(sketch, "E2962", {"start": v(-35.7, -29.85) * mm, "end": v(-35.81, -29.95) * mm});
            skLineSegment(sketch, "E2963", {"start": v(-35.81, -29.95) * mm, "end": v(-35.93, -30.06) * mm});
            skLineSegment(sketch, "E2964", {"start": v(-35.93, -30.06) * mm, "end": v(-36.05, -30.16) * mm});
            skLineSegment(sketch, "E2965", {"start": v(-36.05, -30.16) * mm, "end": v(-36.17, -30.26) * mm});
            skLineSegment(sketch, "E2966", {"start": v(-36.17, -30.26) * mm, "end": v(-36.3, -30.36) * mm});
            skLineSegment(sketch, "E2967", {"start": v(-36.3, -30.36) * mm, "end": v(-36.42, -30.47) * mm});
            skLineSegment(sketch, "E2968", {"start": v(-36.42, -30.47) * mm, "end": v(-36.54, -30.57) * mm});
            skLineSegment(sketch, "E2969", {"start": v(-36.54, -30.57) * mm, "end": v(-36.66, -30.67) * mm});
            skLineSegment(sketch, "E2970", {"start": v(-36.66, -30.67) * mm, "end": v(-36.78, -30.78) * mm});
            skLineSegment(sketch, "E2971", {"start": v(-36.78, -30.78) * mm, "end": v(-36.9, -30.88) * mm});
            skLineSegment(sketch, "E2972", {"start": v(-36.9, -30.88) * mm, "end": v(-37.02, -30.98) * mm});
            skLineSegment(sketch, "E2973", {"start": v(-37.02, -30.98) * mm, "end": v(-37.14, -31.09) * mm});
            skLineSegment(sketch, "E2974", {"start": v(-37.14, -31.09) * mm, "end": v(-37.27, -31.2) * mm});
            skLineSegment(sketch, "E2975", {"start": v(-37.27, -31.2) * mm, "end": v(-37.37, -31.33) * mm});
            skLineSegment(sketch, "E2976", {"start": v(-37.37, -31.33) * mm, "end": v(-37.44, -31.48) * mm});
            skLineSegment(sketch, "E2977", {"start": v(-37.44, -31.48) * mm, "end": v(-37.46, -31.64) * mm});
            skLineSegment(sketch, "E2978", {"start": v(-37.46, -31.64) * mm, "end": v(-37.44, -31.8) * mm});
            skLineSegment(sketch, "E2979", {"start": v(-37.44, -31.8) * mm, "end": v(-37.38, -31.95) * mm});
            skLineSegment(sketch, "E2980", {"start": v(-37.38, -31.95) * mm, "end": v(-37.28, -32.09) * mm});
            skLineSegment(sketch, "E2981", {"start": v(-37.28, -32.09) * mm, "end": v(-37.15, -32.19) * mm});
            skLineSegment(sketch, "E2982", {"start": v(-37.15, -32.19) * mm, "end": v(-37, -32.25) * mm});
            skLineSegment(sketch, "E2983", {"start": v(-37, -32.25) * mm, "end": v(-36.84, -32.27) * mm});
            skLineSegment(sketch, "E2984", {"start": v(-36.84, -32.27) * mm, "end": v(-36.68, -32.25) * mm});
            skLineSegment(sketch, "E2985", {"start": v(-36.68, -32.25) * mm, "end": v(-36.53, -32.2) * mm});
            skLineSegment(sketch, "E2986", {"start": v(-36.53, -32.2) * mm, "end": v(-36.4, -32.1) * mm});
            skLineSegment(sketch, "E2987", {"start": v(-36.4, -32.1) * mm, "end": v(-36.28, -32) * mm});
            skLineSegment(sketch, "E2988", {"start": v(-36.28, -32) * mm, "end": v(-36.17, -31.89) * mm});
            skLineSegment(sketch, "E2989", {"start": v(-36.17, -31.89) * mm, "end": v(-36.05, -31.78) * mm});
            skLineSegment(sketch, "E2990", {"start": v(-36.05, -31.78) * mm, "end": v(-35.93, -31.68) * mm});
            skLineSegment(sketch, "E2991", {"start": v(-35.93, -31.68) * mm, "end": v(-35.81, -31.57) * mm});
            skLineSegment(sketch, "E2992", {"start": v(-35.81, -31.57) * mm, "end": v(-35.7, -31.47) * mm});
            skLineSegment(sketch, "E2993", {"start": v(-35.7, -31.47) * mm, "end": v(-35.58, -31.36) * mm});
            skLineSegment(sketch, "E2994", {"start": v(-35.58, -31.36) * mm, "end": v(-35.46, -31.25) * mm});
            skLineSegment(sketch, "E2995", {"start": v(-35.46, -31.25) * mm, "end": v(-35.34, -31.15) * mm});
            skLineSegment(sketch, "E2996", {"start": v(-35.34, -31.15) * mm, "end": v(-35.22, -31.04) * mm});
            skLineSegment(sketch, "E2997", {"start": v(-35.22, -31.04) * mm, "end": v(-35.1, -30.93) * mm});
            skLineSegment(sketch, "E2998", {"start": v(-35.1, -30.93) * mm, "end": v(-34.99, -30.83) * mm});
            skLineSegment(sketch, "E2999", {"start": v(-34.99, -30.83) * mm, "end": v(-34.9, -30.75) * mm});
            skLineSegment(sketch, "E3000", {"start": v(-34.9, -30.75) * mm, "end": v(-34.8, -30.87) * mm});
            skLineSegment(sketch, "E3001", {"start": v(-34.8, -30.87) * mm, "end": v(-34.69, -30.98) * mm});
            skLineSegment(sketch, "E3002", {"start": v(-34.69, -30.98) * mm, "end": v(-34.58, -31.1) * mm});
            skLineSegment(sketch, "E3003", {"start": v(-34.58, -31.1) * mm, "end": v(-34.47, -31.21) * mm});
            skLineSegment(sketch, "E3004", {"start": v(-34.47, -31.21) * mm, "end": v(-34.37, -31.33) * mm});
            skLineSegment(sketch, "E3005", {"start": v(-34.37, -31.33) * mm, "end": v(-34.26, -31.44) * mm});
            skLineSegment(sketch, "E3006", {"start": v(-34.26, -31.44) * mm, "end": v(-34.15, -31.55) * mm});
            skLineSegment(sketch, "E3007", {"start": v(-34.15, -31.55) * mm, "end": v(-34.04, -31.67) * mm});
            skLineSegment(sketch, "E3008", {"start": v(-34.04, -31.67) * mm, "end": v(-33.94, -31.78) * mm});
            skLineSegment(sketch, "E3009", {"start": v(-33.94, -31.78) * mm, "end": v(-33.83, -31.9) * mm});
            skLineSegment(sketch, "E3010", {"start": v(-33.83, -31.9) * mm, "end": v(-33.72, -32.01) * mm});
            skLineSegment(sketch, "E3011", {"start": v(-33.72, -32.01) * mm, "end": v(-33.67, -32.07) * mm});
            skLineSegment(sketch, "E3012", {"start": v(-33.67, -32.07) * mm, "end": v(-33.78, -32.18) * mm});
            skLineSegment(sketch, "E3013", {"start": v(-33.78, -32.18) * mm, "end": v(-33.9, -32.3) * mm});
            skLineSegment(sketch, "E3014", {"start": v(-33.9, -32.3) * mm, "end": v(-34, -32.4) * mm});
            skLineSegment(sketch, "E3015", {"start": v(-34, -32.4) * mm, "end": v(-34.12, -32.51) * mm});
            skLineSegment(sketch, "E3016", {"start": v(-34.12, -32.51) * mm, "end": v(-34.23, -32.62) * mm});
            skLineSegment(sketch, "E3017", {"start": v(-34.23, -32.62) * mm, "end": v(-34.35, -32.74) * mm});
            skLineSegment(sketch, "E3018", {"start": v(-34.35, -32.74) * mm, "end": v(-34.46, -32.85) * mm});
            skLineSegment(sketch, "E3019", {"start": v(-34.46, -32.85) * mm, "end": v(-34.57, -32.96) * mm});
            skLineSegment(sketch, "E3020", {"start": v(-34.57, -32.96) * mm, "end": v(-34.69, -33.07) * mm});
            skLineSegment(sketch, "E3021", {"start": v(-34.69, -33.07) * mm, "end": v(-34.8, -33.18) * mm});
            skLineSegment(sketch, "E3022", {"start": v(-34.8, -33.18) * mm, "end": v(-34.91, -33.29) * mm});
            skLineSegment(sketch, "E3023", {"start": v(-34.91, -33.29) * mm, "end": v(-35.03, -33.4) * mm});
            skLineSegment(sketch, "E3024", {"start": v(-35.03, -33.4) * mm, "end": v(-35.15, -33.52) * mm});
            skLineSegment(sketch, "E3025", {"start": v(-35.15, -33.52) * mm, "end": v(-35.24, -33.65) * mm});
            skLineSegment(sketch, "E3026", {"start": v(-35.24, -33.65) * mm, "end": v(-35.3, -33.8) * mm});
            skLineSegment(sketch, "E3027", {"start": v(-35.3, -33.8) * mm, "end": v(-35.31, -33.97) * mm});
            skLineSegment(sketch, "E3028", {"start": v(-35.31, -33.97) * mm, "end": v(-35.28, -34.13) * mm});
            skLineSegment(sketch, "E3029", {"start": v(-35.28, -34.13) * mm, "end": v(-35.21, -34.28) * mm});
            skLineSegment(sketch, "E3030", {"start": v(-35.21, -34.28) * mm, "end": v(-35.1, -34.4) * mm});
            skLineSegment(sketch, "E3031", {"start": v(-35.1, -34.4) * mm, "end": v(-34.97, -34.5) * mm});
            skLineSegment(sketch, "E3032", {"start": v(-34.97, -34.5) * mm, "end": v(-34.82, -34.55) * mm});
            skLineSegment(sketch, "E3033", {"start": v(-34.82, -34.55) * mm, "end": v(-34.65, -34.57) * mm});
            skLineSegment(sketch, "E3034", {"start": v(-34.65, -34.57) * mm, "end": v(-34.5, -34.54) * mm});
            skLineSegment(sketch, "E3035", {"start": v(-34.5, -34.54) * mm, "end": v(-34.34, -34.46) * mm});
            skLineSegment(sketch, "E3036", {"start": v(-34.34, -34.46) * mm, "end": v(-34.23, -34.36) * mm});
            skLineSegment(sketch, "E3037", {"start": v(-34.23, -34.36) * mm, "end": v(-34.11, -34.25) * mm});
            skLineSegment(sketch, "E3038", {"start": v(-34.11, -34.25) * mm, "end": v(-34, -34.14) * mm});
            skLineSegment(sketch, "E3039", {"start": v(-34, -34.14) * mm, "end": v(-33.9, -34.02) * mm});
            skLineSegment(sketch, "E3040", {"start": v(-33.9, -34.02) * mm, "end": v(-33.79, -33.91) * mm});
            skLineSegment(sketch, "E3041", {"start": v(-33.79, -33.91) * mm, "end": v(-33.67, -33.8) * mm});
            skLineSegment(sketch, "E3042", {"start": v(-33.67, -33.8) * mm, "end": v(-33.56, -33.68) * mm});
            skLineSegment(sketch, "E3043", {"start": v(-33.56, -33.68) * mm, "end": v(-33.45, -33.57) * mm});
            skLineSegment(sketch, "E3044", {"start": v(-33.45, -33.57) * mm, "end": v(-33.34, -33.46) * mm});
            skLineSegment(sketch, "E3045", {"start": v(-33.34, -33.46) * mm, "end": v(-33.23, -33.34) * mm});
            skLineSegment(sketch, "E3046", {"start": v(-33.23, -33.34) * mm, "end": v(-33.12, -33.23) * mm});
            skLineSegment(sketch, "E3047", {"start": v(-33.12, -33.23) * mm, "end": v(-33, -33.11) * mm});
            skLineSegment(sketch, "E3048", {"start": v(-33, -33.11) * mm, "end": v(-32.9, -33) * mm});
            skLineSegment(sketch, "E3049", {"start": v(-32.9, -33) * mm, "end": v(-32.82, -32.92) * mm});
            skLineSegment(sketch, "E3050", {"start": v(-32.82, -32.92) * mm, "end": v(-32.7, -33.03) * mm});
            skLineSegment(sketch, "E3051", {"start": v(-32.7, -33.03) * mm, "end": v(-32.59, -33.13) * mm});
            skLineSegment(sketch, "E3052", {"start": v(-32.59, -33.13) * mm, "end": v(-32.47, -33.24) * mm});
            skLineSegment(sketch, "E3053", {"start": v(-32.47, -33.24) * mm, "end": v(-32.36, -33.35) * mm});
            skLineSegment(sketch, "E3054", {"start": v(-32.36, -33.35) * mm, "end": v(-32.24, -33.46) * mm});
            skLineSegment(sketch, "E3055", {"start": v(-32.24, -33.46) * mm, "end": v(-32.13, -33.56) * mm});
            skLineSegment(sketch, "E3056", {"start": v(-32.13, -33.56) * mm, "end": v(-32.01, -33.67) * mm});
            skLineSegment(sketch, "E3057", {"start": v(-32.01, -33.67) * mm, "end": v(-31.9, -33.78) * mm});
            skLineSegment(sketch, "E3058", {"start": v(-31.9, -33.78) * mm, "end": v(-31.79, -33.89) * mm});
            skLineSegment(sketch, "E3059", {"start": v(-31.79, -33.89) * mm, "end": v(-31.67, -34) * mm});
            skLineSegment(sketch, "E3060", {"start": v(-31.67, -34) * mm, "end": v(-31.56, -34.1) * mm});
            skLineSegment(sketch, "E3061", {"start": v(-31.56, -34.1) * mm, "end": v(-31.5, -34.16) * mm});
            skLineSegment(sketch, "E3062", {"start": v(-31.5, -34.16) * mm, "end": v(-31.6, -34.27) * mm});
            skLineSegment(sketch, "E3063", {"start": v(-31.6, -34.27) * mm, "end": v(-31.7, -34.4) * mm});
            skLineSegment(sketch, "E3064", {"start": v(-31.7, -34.4) * mm, "end": v(-31.82, -34.51) * mm});
            skLineSegment(sketch, "E3065", {"start": v(-31.82, -34.51) * mm, "end": v(-31.92, -34.63) * mm});
            skLineSegment(sketch, "E3066", {"start": v(-31.92, -34.63) * mm, "end": v(-32.03, -34.74) * mm});
            skLineSegment(sketch, "E3067", {"start": v(-32.03, -34.74) * mm, "end": v(-32.13, -34.86) * mm});
            skLineSegment(sketch, "E3068", {"start": v(-32.13, -34.86) * mm, "end": v(-32.24, -34.98) * mm});
            skLineSegment(sketch, "E3069", {"start": v(-32.24, -34.98) * mm, "end": v(-32.34, -35.1) * mm});
            skLineSegment(sketch, "E3070", {"start": v(-32.34, -35.1) * mm, "end": v(-32.45, -35.22) * mm});
            skLineSegment(sketch, "E3071", {"start": v(-32.45, -35.22) * mm, "end": v(-32.56, -35.34) * mm});
            skLineSegment(sketch, "E3072", {"start": v(-32.56, -35.34) * mm, "end": v(-32.66, -35.45) * mm});
            skLineSegment(sketch, "E3073", {"start": v(-32.66, -35.45) * mm, "end": v(-32.77, -35.57) * mm});
            skLineSegment(sketch, "E3074", {"start": v(-32.77, -35.57) * mm, "end": v(-32.88, -35.7) * mm});
            skLineSegment(sketch, "E3075", {"start": v(-32.88, -35.7) * mm, "end": v(-32.97, -35.84) * mm});
            skLineSegment(sketch, "E3076", {"start": v(-32.97, -35.84) * mm, "end": v(-33.01, -36) * mm});
            skLineSegment(sketch, "E3077", {"start": v(-33.01, -36) * mm, "end": v(-33.02, -36.16) * mm});
            skLineSegment(sketch, "E3078", {"start": v(-33.02, -36.16) * mm, "end": v(-32.98, -36.32) * mm});
            skLineSegment(sketch, "E3079", {"start": v(-32.98, -36.32) * mm, "end": v(-32.9, -36.46) * mm});
            skLineSegment(sketch, "E3080", {"start": v(-32.9, -36.46) * mm, "end": v(-32.78, -36.58) * mm});
            skLineSegment(sketch, "E3081", {"start": v(-32.78, -36.58) * mm, "end": v(-32.64, -36.66) * mm});
            skLineSegment(sketch, "E3082", {"start": v(-32.64, -36.66) * mm, "end": v(-32.48, -36.7) * mm});
            skLineSegment(sketch, "E3083", {"start": v(-32.48, -36.7) * mm, "end": v(-32.32, -36.7) * mm});
            skLineSegment(sketch, "E3084", {"start": v(-32.32, -36.7) * mm, "end": v(-32.16, -36.67) * mm});
            skLineSegment(sketch, "E3085", {"start": v(-32.16, -36.67) * mm, "end": v(-32.02, -36.59) * mm});
            skLineSegment(sketch, "E3086", {"start": v(-32.02, -36.59) * mm, "end": v(-31.9, -36.48) * mm});
            skLineSegment(sketch, "E3087", {"start": v(-31.9, -36.48) * mm, "end": v(-31.8, -36.36) * mm});
            skLineSegment(sketch, "E3088", {"start": v(-31.8, -36.36) * mm, "end": v(-31.7, -36.24) * mm});
            skLineSegment(sketch, "E3089", {"start": v(-31.7, -36.24) * mm, "end": v(-31.6, -36.12) * mm});
            skLineSegment(sketch, "E3090", {"start": v(-31.6, -36.12) * mm, "end": v(-31.5, -36) * mm});
            skLineSegment(sketch, "E3091", {"start": v(-31.5, -36) * mm, "end": v(-31.4, -35.88) * mm});
            skLineSegment(sketch, "E3092", {"start": v(-31.4, -35.88) * mm, "end": v(-31.29, -35.76) * mm});
            skLineSegment(sketch, "E3093", {"start": v(-31.29, -35.76) * mm, "end": v(-31.19, -35.64) * mm});
            skLineSegment(sketch, "E3094", {"start": v(-31.19, -35.64) * mm, "end": v(-31.08, -35.52) * mm});
            skLineSegment(sketch, "E3095", {"start": v(-31.08, -35.52) * mm, "end": v(-30.98, -35.4) * mm});
            skLineSegment(sketch, "E3096", {"start": v(-30.98, -35.4) * mm, "end": v(-30.88, -35.28) * mm});
            skLineSegment(sketch, "E3097", {"start": v(-30.88, -35.28) * mm, "end": v(-30.77, -35.15) * mm});
            skLineSegment(sketch, "E3098", {"start": v(-30.77, -35.15) * mm, "end": v(-30.67, -35.03) * mm});
            skLineSegment(sketch, "E3099", {"start": v(-30.67, -35.03) * mm, "end": v(-30.6, -34.95) * mm});
            skLineSegment(sketch, "E3100", {"start": v(-30.6, -34.95) * mm, "end": v(-30.48, -35.05) * mm});
            skLineSegment(sketch, "E3101", {"start": v(-30.48, -35.05) * mm, "end": v(-30.35, -35.15) * mm});
            skLineSegment(sketch, "E3102", {"start": v(-30.35, -35.15) * mm, "end": v(-30.23, -35.25) * mm});
            skLineSegment(sketch, "E3103", {"start": v(-30.23, -35.25) * mm, "end": v(-30.11, -35.35) * mm});
            skLineSegment(sketch, "E3104", {"start": v(-30.11, -35.35) * mm, "end": v(-29.99, -35.45) * mm});
            skLineSegment(sketch, "E3105", {"start": v(-29.99, -35.45) * mm, "end": v(-29.87, -35.54) * mm});
            skLineSegment(sketch, "E3106", {"start": v(-29.87, -35.54) * mm, "end": v(-29.75, -35.64) * mm});
            skLineSegment(sketch, "E3107", {"start": v(-29.75, -35.64) * mm, "end": v(-29.62, -35.74) * mm});
            skLineSegment(sketch, "E3108", {"start": v(-29.62, -35.74) * mm, "end": v(-29.5, -35.84) * mm});
            skLineSegment(sketch, "E3109", {"start": v(-29.5, -35.84) * mm, "end": v(-29.38, -35.94) * mm});
            skLineSegment(sketch, "E3110", {"start": v(-29.38, -35.94) * mm, "end": v(-29.26, -36.04) * mm});
            skLineSegment(sketch, "E3111", {"start": v(-29.26, -36.04) * mm, "end": v(-29.2, -36.1) * mm});
            skLineSegment(sketch, "E3112", {"start": v(-29.2, -36.1) * mm, "end": v(-29.3, -36.22) * mm});
            skLineSegment(sketch, "E3113", {"start": v(-29.3, -36.22) * mm, "end": v(-29.4, -36.34) * mm});
            skLineSegment(sketch, "E3114", {"start": v(-29.4, -36.34) * mm, "end": v(-29.5, -36.47) * mm});
            skLineSegment(sketch, "E3115", {"start": v(-29.5, -36.47) * mm, "end": v(-29.59, -36.6) * mm});
            skLineSegment(sketch, "E3116", {"start": v(-29.59, -36.6) * mm, "end": v(-29.69, -36.72) * mm});
            skLineSegment(sketch, "E3117", {"start": v(-29.69, -36.72) * mm, "end": v(-29.79, -36.84) * mm});
            skLineSegment(sketch, "E3118", {"start": v(-29.79, -36.84) * mm, "end": v(-29.88, -36.97) * mm});
            skLineSegment(sketch, "E3119", {"start": v(-29.88, -36.97) * mm, "end": v(-29.98, -37.09) * mm});
            skLineSegment(sketch, "E3120", {"start": v(-29.98, -37.09) * mm, "end": v(-30.08, -37.22) * mm});
            skLineSegment(sketch, "E3121", {"start": v(-30.08, -37.22) * mm, "end": v(-30.18, -37.34) * mm});
            skLineSegment(sketch, "E3122", {"start": v(-30.18, -37.34) * mm, "end": v(-30.28, -37.46) * mm});
            skLineSegment(sketch, "E3123", {"start": v(-30.28, -37.46) * mm, "end": v(-30.38, -37.6) * mm});
            skLineSegment(sketch, "E3124", {"start": v(-30.38, -37.6) * mm, "end": v(-30.48, -37.72) * mm});
            skLineSegment(sketch, "E3125", {"start": v(-30.48, -37.72) * mm, "end": v(-30.56, -37.87) * mm});
            skLineSegment(sketch, "E3126", {"start": v(-30.56, -37.87) * mm, "end": v(-30.59, -38.03) * mm});
            skLineSegment(sketch, "E3127", {"start": v(-30.59, -38.03) * mm, "end": v(-30.58, -38.2) * mm});
            skLineSegment(sketch, "E3128", {"start": v(-30.58, -38.2) * mm, "end": v(-30.53, -38.35) * mm});
            skLineSegment(sketch, "E3129", {"start": v(-30.53, -38.35) * mm, "end": v(-30.44, -38.49) * mm});
            skLineSegment(sketch, "E3130", {"start": v(-30.44, -38.49) * mm, "end": v(-30.32, -38.6) * mm});
            skLineSegment(sketch, "E3131", {"start": v(-30.32, -38.6) * mm, "end": v(-30.17, -38.67) * mm});
            skLineSegment(sketch, "E3132", {"start": v(-30.17, -38.67) * mm, "end": v(-30.01, -38.7) * mm});
            skLineSegment(sketch, "E3133", {"start": v(-30.01, -38.7) * mm, "end": v(-29.85, -38.7) * mm});
            skLineSegment(sketch, "E3134", {"start": v(-29.85, -38.7) * mm, "end": v(-29.7, -38.64) * mm});
            skLineSegment(sketch, "E3135", {"start": v(-29.7, -38.64) * mm, "end": v(-29.56, -38.55) * mm});
            skLineSegment(sketch, "E3136", {"start": v(-29.56, -38.55) * mm, "end": v(-29.45, -38.44) * mm});
            skLineSegment(sketch, "E3137", {"start": v(-29.45, -38.44) * mm, "end": v(-29.36, -38.31) * mm});
            skLineSegment(sketch, "E3138", {"start": v(-29.36, -38.31) * mm, "end": v(-29.26, -38.19) * mm});
            skLineSegment(sketch, "E3139", {"start": v(-29.26, -38.19) * mm, "end": v(-29.17, -38.06) * mm});
            skLineSegment(sketch, "E3140", {"start": v(-29.17, -38.06) * mm, "end": v(-29.08, -37.93) * mm});
            skLineSegment(sketch, "E3141", {"start": v(-29.08, -37.93) * mm, "end": v(-28.98, -37.8) * mm});
            skLineSegment(sketch, "E3142", {"start": v(-28.98, -37.8) * mm, "end": v(-28.89, -37.68) * mm});
            skLineSegment(sketch, "E3143", {"start": v(-28.89, -37.68) * mm, "end": v(-28.8, -37.55) * mm});
            skLineSegment(sketch, "E3144", {"start": v(-28.8, -37.55) * mm, "end": v(-28.7, -37.42) * mm});
            skLineSegment(sketch, "E3145", {"start": v(-28.7, -37.42) * mm, "end": v(-28.6, -37.3) * mm});
            skLineSegment(sketch, "E3146", {"start": v(-28.6, -37.3) * mm, "end": v(-28.5, -37.17) * mm});
            skLineSegment(sketch, "E3147", {"start": v(-28.5, -37.17) * mm, "end": v(-28.4, -37.04) * mm});
            skLineSegment(sketch, "E3148", {"start": v(-28.4, -37.04) * mm, "end": v(-28.32, -36.92) * mm});
            skLineSegment(sketch, "E3149", {"start": v(-28.32, -36.92) * mm, "end": v(-28.25, -36.82) * mm});
            skLineSegment(sketch, "E3150", {"start": v(-28.25, -36.82) * mm, "end": v(-28.12, -36.92) * mm});
            skLineSegment(sketch, "E3151", {"start": v(-28.12, -36.92) * mm, "end": v(-28, -37) * mm});
            skLineSegment(sketch, "E3152", {"start": v(-28, -37) * mm, "end": v(-27.86, -37.1) * mm});
            skLineSegment(sketch, "E3153", {"start": v(-27.86, -37.1) * mm, "end": v(-27.74, -37.2) * mm});
            skLineSegment(sketch, "E3154", {"start": v(-27.74, -37.2) * mm, "end": v(-27.6, -37.28) * mm});
            skLineSegment(sketch, "E3155", {"start": v(-27.6, -37.28) * mm, "end": v(-27.48, -37.37) * mm});
            skLineSegment(sketch, "E3156", {"start": v(-27.48, -37.37) * mm, "end": v(-27.35, -37.47) * mm});
            skLineSegment(sketch, "E3157", {"start": v(-27.35, -37.47) * mm, "end": v(-27.22, -37.56) * mm});
            skLineSegment(sketch, "E3158", {"start": v(-27.22, -37.56) * mm, "end": v(-27.1, -37.65) * mm});
            skLineSegment(sketch, "E3159", {"start": v(-27.1, -37.65) * mm, "end": v(-26.97, -37.74) * mm});
            skLineSegment(sketch, "E3160", {"start": v(-26.97, -37.74) * mm, "end": v(-26.84, -37.83) * mm});
            skLineSegment(sketch, "E3161", {"start": v(-26.84, -37.83) * mm, "end": v(-26.78, -37.88) * mm});
            skLineSegment(sketch, "E3162", {"start": v(-26.78, -37.88) * mm, "end": v(-26.86, -38) * mm});
            skLineSegment(sketch, "E3163", {"start": v(-26.86, -38) * mm, "end": v(-26.95, -38.14) * mm});
            skLineSegment(sketch, "E3164", {"start": v(-26.95, -38.14) * mm, "end": v(-27.05, -38.27) * mm});
            skLineSegment(sketch, "E3165", {"start": v(-27.05, -38.27) * mm, "end": v(-27.13, -38.4) * mm});
            skLineSegment(sketch, "E3166", {"start": v(-27.13, -38.4) * mm, "end": v(-27.22, -38.53) * mm});
            skLineSegment(sketch, "E3167", {"start": v(-27.22, -38.53) * mm, "end": v(-27.31, -38.66) * mm});
            skLineSegment(sketch, "E3168", {"start": v(-27.31, -38.66) * mm, "end": v(-27.4, -38.8) * mm});
            skLineSegment(sketch, "E3169", {"start": v(-27.4, -38.8) * mm, "end": v(-27.5, -38.92) * mm});
            skLineSegment(sketch, "E3170", {"start": v(-27.5, -38.92) * mm, "end": v(-27.58, -39.06) * mm});
            skLineSegment(sketch, "E3171", {"start": v(-27.58, -39.06) * mm, "end": v(-27.67, -39.19) * mm});
            skLineSegment(sketch, "E3172", {"start": v(-27.67, -39.19) * mm, "end": v(-27.76, -39.31) * mm});
            skLineSegment(sketch, "E3173", {"start": v(-27.76, -39.31) * mm, "end": v(-27.85, -39.45) * mm});
            skLineSegment(sketch, "E3174", {"start": v(-27.85, -39.45) * mm, "end": v(-27.95, -39.59) * mm});
            skLineSegment(sketch, "E3175", {"start": v(-27.95, -39.59) * mm, "end": v(-28.01, -39.74) * mm});
            skLineSegment(sketch, "E3176", {"start": v(-28.01, -39.74) * mm, "end": v(-28.04, -39.9) * mm});
            skLineSegment(sketch, "E3177", {"start": v(-28.04, -39.9) * mm, "end": v(-28.02, -40.06) * mm});
            skLineSegment(sketch, "E3178", {"start": v(-28.02, -40.06) * mm, "end": v(-27.96, -40.22) * mm});
            skLineSegment(sketch, "E3179", {"start": v(-27.96, -40.22) * mm, "end": v(-27.86, -40.35) * mm});
            skLineSegment(sketch, "E3180", {"start": v(-27.86, -40.35) * mm, "end": v(-27.73, -40.45) * mm});
            skLineSegment(sketch, "E3181", {"start": v(-27.73, -40.45) * mm, "end": v(-27.58, -40.51) * mm});
            skLineSegment(sketch, "E3182", {"start": v(-27.58, -40.51) * mm, "end": v(-27.42, -40.54) * mm});
            skLineSegment(sketch, "E3183", {"start": v(-27.42, -40.54) * mm, "end": v(-27.26, -40.52) * mm});
            skLineSegment(sketch, "E3184", {"start": v(-27.26, -40.52) * mm, "end": v(-27.1, -40.46) * mm});
            skLineSegment(sketch, "E3185", {"start": v(-27.1, -40.46) * mm, "end": v(-26.97, -40.36) * mm});
            skLineSegment(sketch, "E3186", {"start": v(-26.97, -40.36) * mm, "end": v(-26.88, -40.23) * mm});
            skLineSegment(sketch, "E3187", {"start": v(-26.88, -40.23) * mm, "end": v(-26.8, -40.1) * mm});
            skLineSegment(sketch, "E3188", {"start": v(-26.8, -40.1) * mm, "end": v(-26.7, -39.97) * mm});
            skLineSegment(sketch, "E3189", {"start": v(-26.7, -39.97) * mm, "end": v(-26.62, -39.84) * mm});
            skLineSegment(sketch, "E3190", {"start": v(-26.62, -39.84) * mm, "end": v(-26.53, -39.7) * mm});
            skLineSegment(sketch, "E3191", {"start": v(-26.53, -39.7) * mm, "end": v(-26.45, -39.57) * mm});
            skLineSegment(sketch, "E3192", {"start": v(-26.45, -39.57) * mm, "end": v(-26.36, -39.44) * mm});
            skLineSegment(sketch, "E3193", {"start": v(-26.36, -39.44) * mm, "end": v(-26.28, -39.3) * mm});
            skLineSegment(sketch, "E3194", {"start": v(-26.28, -39.3) * mm, "end": v(-26.19, -39.17) * mm});
            skLineSegment(sketch, "E3195", {"start": v(-26.19, -39.17) * mm, "end": v(-26.1, -39.04) * mm});
            skLineSegment(sketch, "E3196", {"start": v(-26.1, -39.04) * mm, "end": v(-26.02, -38.9) * mm});
            skLineSegment(sketch, "E3197", {"start": v(-26.02, -38.9) * mm, "end": v(-25.93, -38.77) * mm});
            skLineSegment(sketch, "E3198", {"start": v(-25.93, -38.77) * mm, "end": v(-25.84, -38.64) * mm});
            skLineSegment(sketch, "E3199", {"start": v(-25.84, -38.64) * mm, "end": v(-25.78, -38.54) * mm});
            skLineSegment(sketch, "E3200", {"start": v(-25.78, -38.54) * mm, "end": v(-25.65, -38.63) * mm});
            skLineSegment(sketch, "E3201", {"start": v(-25.65, -38.63) * mm, "end": v(-25.51, -38.7) * mm});
            skLineSegment(sketch, "E3202", {"start": v(-25.51, -38.7) * mm, "end": v(-25.38, -38.8) * mm});
            skLineSegment(sketch, "E3203", {"start": v(-25.38, -38.8) * mm, "end": v(-25.25, -38.88) * mm});
            skLineSegment(sketch, "E3204", {"start": v(-25.25, -38.88) * mm, "end": v(-25.11, -38.96) * mm});
            skLineSegment(sketch, "E3205", {"start": v(-25.11, -38.96) * mm, "end": v(-24.98, -39.04) * mm});
            skLineSegment(sketch, "E3206", {"start": v(-24.98, -39.04) * mm, "end": v(-24.85, -39.12) * mm});
            skLineSegment(sketch, "E3207", {"start": v(-24.85, -39.12) * mm, "end": v(-24.71, -39.2) * mm});
            skLineSegment(sketch, "E3208", {"start": v(-24.71, -39.2) * mm, "end": v(-24.58, -39.3) * mm});
            skLineSegment(sketch, "E3209", {"start": v(-24.58, -39.3) * mm, "end": v(-24.44, -39.37) * mm});
            skLineSegment(sketch, "E3210", {"start": v(-24.44, -39.37) * mm, "end": v(-24.31, -39.46) * mm});
            skLineSegment(sketch, "E3211", {"start": v(-24.31, -39.46) * mm, "end": v(-24.24, -39.5) * mm});
            skLineSegment(sketch, "E3212", {"start": v(-24.24, -39.5) * mm, "end": v(-24.32, -39.63) * mm});
            skLineSegment(sketch, "E3213", {"start": v(-24.32, -39.63) * mm, "end": v(-24.4, -39.77) * mm});
            skLineSegment(sketch, "E3214", {"start": v(-24.4, -39.77) * mm, "end": v(-24.49, -39.9) * mm});
            skLineSegment(sketch, "E3215", {"start": v(-24.49, -39.9) * mm, "end": v(-24.57, -40.04) * mm});
            skLineSegment(sketch, "E3216", {"start": v(-24.57, -40.04) * mm, "end": v(-24.65, -40.18) * mm});
            skLineSegment(sketch, "E3217", {"start": v(-24.65, -40.18) * mm, "end": v(-24.73, -40.32) * mm});
            skLineSegment(sketch, "E3218", {"start": v(-24.73, -40.32) * mm, "end": v(-24.8, -40.45) * mm});
            skLineSegment(sketch, "E3219", {"start": v(-24.8, -40.45) * mm, "end": v(-24.9, -40.59) * mm});
            skLineSegment(sketch, "E3220", {"start": v(-24.9, -40.59) * mm, "end": v(-24.97, -40.73) * mm});
            skLineSegment(sketch, "E3221", {"start": v(-24.97, -40.73) * mm, "end": v(-25.05, -40.86) * mm});
            skLineSegment(sketch, "E3222", {"start": v(-25.05, -40.86) * mm, "end": v(-25.13, -41) * mm});
            skLineSegment(sketch, "E3223", {"start": v(-25.13, -41) * mm, "end": v(-25.22, -41.14) * mm});
            skLineSegment(sketch, "E3224", {"start": v(-25.22, -41.14) * mm, "end": v(-25.3, -41.28) * mm});
            skLineSegment(sketch, "E3225", {"start": v(-25.3, -41.28) * mm, "end": v(-25.36, -41.44) * mm});
            skLineSegment(sketch, "E3226", {"start": v(-25.36, -41.44) * mm, "end": v(-25.37, -41.6) * mm});
            skLineSegment(sketch, "E3227", {"start": v(-25.37, -41.6) * mm, "end": v(-25.34, -41.76) * mm});
            skLineSegment(sketch, "E3228", {"start": v(-25.34, -41.76) * mm, "end": v(-25.27, -41.9) * mm});
            skLineSegment(sketch, "E3229", {"start": v(-25.27, -41.9) * mm, "end": v(-25.16, -42.03) * mm});
            skLineSegment(sketch, "E3230", {"start": v(-25.16, -42.03) * mm, "end": v(-25.03, -42.13) * mm});
            skLineSegment(sketch, "E3231", {"start": v(-25.03, -42.13) * mm, "end": v(-24.88, -42.18) * mm});
            skLineSegment(sketch, "E3232", {"start": v(-24.88, -42.18) * mm, "end": v(-24.71, -42.2) * mm});
            skLineSegment(sketch, "E3233", {"start": v(-24.71, -42.2) * mm, "end": v(-24.55, -42.16) * mm});
            skLineSegment(sketch, "E3234", {"start": v(-24.55, -42.16) * mm, "end": v(-24.4, -42.1) * mm});
            skLineSegment(sketch, "E3235", {"start": v(-24.4, -42.1) * mm, "end": v(-24.28, -41.99) * mm});
            skLineSegment(sketch, "E3236", {"start": v(-24.28, -41.99) * mm, "end": v(-24.2, -41.85) * mm});
            skLineSegment(sketch, "E3237", {"start": v(-24.2, -41.85) * mm, "end": v(-24.11, -41.72) * mm});
            skLineSegment(sketch, "E3238", {"start": v(-24.11, -41.72) * mm, "end": v(-24.04, -41.58) * mm});
            skLineSegment(sketch, "E3239", {"start": v(-24.04, -41.58) * mm, "end": v(-23.96, -41.44) * mm});
            skLineSegment(sketch, "E3240", {"start": v(-23.96, -41.44) * mm, "end": v(-23.88, -41.3) * mm});
            skLineSegment(sketch, "E3241", {"start": v(-23.88, -41.3) * mm, "end": v(-23.8, -41.17) * mm});
            skLineSegment(sketch, "E3242", {"start": v(-23.8, -41.17) * mm, "end": v(-23.73, -41.03) * mm});
            skLineSegment(sketch, "E3243", {"start": v(-23.73, -41.03) * mm, "end": v(-23.65, -40.9) * mm});
            skLineSegment(sketch, "E3244", {"start": v(-23.65, -40.9) * mm, "end": v(-23.57, -40.75) * mm});
            skLineSegment(sketch, "E3245", {"start": v(-23.57, -40.75) * mm, "end": v(-23.5, -40.61) * mm});
            skLineSegment(sketch, "E3246", {"start": v(-23.5, -40.61) * mm, "end": v(-23.42, -40.48) * mm});
            skLineSegment(sketch, "E3247", {"start": v(-23.42, -40.48) * mm, "end": v(-23.34, -40.34) * mm});
            skLineSegment(sketch, "E3248", {"start": v(-23.34, -40.34) * mm, "end": v(-23.26, -40.2) * mm});
            skLineSegment(sketch, "E3249", {"start": v(-23.26, -40.2) * mm, "end": v(-23.2, -40.1) * mm});
            skLineSegment(sketch, "E3250", {"start": v(-23.2, -40.1) * mm, "end": v(-23.07, -40.17) * mm});
            skLineSegment(sketch, "E3251", {"start": v(-23.07, -40.17) * mm, "end": v(-22.93, -40.25) * mm});
            skLineSegment(sketch, "E3252", {"start": v(-22.93, -40.25) * mm, "end": v(-22.79, -40.32) * mm});
            skLineSegment(sketch, "E3253", {"start": v(-22.79, -40.32) * mm, "end": v(-22.65, -40.4) * mm});
            skLineSegment(sketch, "E3254", {"start": v(-22.65, -40.4) * mm, "end": v(-22.51, -40.47) * mm});
            skLineSegment(sketch, "E3255", {"start": v(-22.51, -40.47) * mm, "end": v(-22.37, -40.54) * mm});
            skLineSegment(sketch, "E3256", {"start": v(-22.37, -40.54) * mm, "end": v(-22.23, -40.62) * mm});
            skLineSegment(sketch, "E3257", {"start": v(-22.23, -40.62) * mm, "end": v(-22.1, -40.7) * mm});
            skLineSegment(sketch, "E3258", {"start": v(-22.1, -40.7) * mm, "end": v(-21.96, -40.77) * mm});
            skLineSegment(sketch, "E3259", {"start": v(-21.96, -40.77) * mm, "end": v(-21.82, -40.84) * mm});
            skLineSegment(sketch, "E3260", {"start": v(-21.82, -40.84) * mm, "end": v(-21.68, -40.91) * mm});
            skLineSegment(sketch, "E3261", {"start": v(-21.68, -40.91) * mm, "end": v(-21.6, -40.95) * mm});
            skLineSegment(sketch, "E3262", {"start": v(-21.6, -40.95) * mm, "end": v(-21.68, -41.1) * mm});
            skLineSegment(sketch, "E3263", {"start": v(-21.68, -41.1) * mm, "end": v(-21.75, -41.23) * mm});
            skLineSegment(sketch, "E3264", {"start": v(-21.75, -41.23) * mm, "end": v(-21.82, -41.38) * mm});
            skLineSegment(sketch, "E3265", {"start": v(-21.82, -41.38) * mm, "end": v(-21.9, -41.52) * mm});
            skLineSegment(sketch, "E3266", {"start": v(-21.9, -41.52) * mm, "end": v(-21.97, -41.66) * mm});
            skLineSegment(sketch, "E3267", {"start": v(-21.97, -41.66) * mm, "end": v(-22.04, -41.8) * mm});
            skLineSegment(sketch, "E3268", {"start": v(-22.04, -41.8) * mm, "end": v(-22.11, -41.94) * mm});
            skLineSegment(sketch, "E3269", {"start": v(-22.11, -41.94) * mm, "end": v(-22.18, -42.08) * mm});
            skLineSegment(sketch, "E3270", {"start": v(-22.18, -42.08) * mm, "end": v(-22.26, -42.22) * mm});
            skLineSegment(sketch, "E3271", {"start": v(-22.26, -42.22) * mm, "end": v(-22.33, -42.36) * mm});
            skLineSegment(sketch, "E3272", {"start": v(-22.33, -42.36) * mm, "end": v(-22.4, -42.5) * mm});
            skLineSegment(sketch, "E3273", {"start": v(-22.4, -42.5) * mm, "end": v(-22.47, -42.65) * mm});
            skLineSegment(sketch, "E3274", {"start": v(-22.47, -42.65) * mm, "end": v(-22.55, -42.8) * mm});
            skLineSegment(sketch, "E3275", {"start": v(-22.55, -42.8) * mm, "end": v(-22.6, -42.96) * mm});
            skLineSegment(sketch, "E3276", {"start": v(-22.6, -42.96) * mm, "end": v(-22.6, -43.12) * mm});
            skLineSegment(sketch, "E3277", {"start": v(-22.6, -43.12) * mm, "end": v(-22.56, -43.28) * mm});
            skLineSegment(sketch, "E3278", {"start": v(-22.56, -43.28) * mm, "end": v(-22.48, -43.42) * mm});
            skLineSegment(sketch, "E3279", {"start": v(-22.48, -43.42) * mm, "end": v(-22.36, -43.54) * mm});
            skLineSegment(sketch, "E3280", {"start": v(-22.36, -43.54) * mm, "end": v(-22.22, -43.62) * mm});
            skLineSegment(sketch, "E3281", {"start": v(-22.22, -43.62) * mm, "end": v(-22.06, -43.67) * mm});
            skLineSegment(sketch, "E3282", {"start": v(-22.06, -43.67) * mm, "end": v(-21.9, -43.67) * mm});
            skLineSegment(sketch, "E3283", {"start": v(-21.9, -43.67) * mm, "end": v(-21.74, -43.63) * mm});
            skLineSegment(sketch, "E3284", {"start": v(-21.74, -43.63) * mm, "end": v(-21.6, -43.55) * mm});
            skLineSegment(sketch, "E3285", {"start": v(-21.6, -43.55) * mm, "end": v(-21.48, -43.43) * mm});
            skLineSegment(sketch, "E3286", {"start": v(-21.48, -43.43) * mm, "end": v(-21.4, -43.3) * mm});
            skLineSegment(sketch, "E3287", {"start": v(-21.4, -43.3) * mm, "end": v(-21.33, -43.16) * mm});
            skLineSegment(sketch, "E3288", {"start": v(-21.33, -43.16) * mm, "end": v(-21.27, -43.02) * mm});
            skLineSegment(sketch, "E3289", {"start": v(-21.27, -43.02) * mm, "end": v(-21.2, -42.87) * mm});
            skLineSegment(sketch, "E3290", {"start": v(-21.2, -42.87) * mm, "end": v(-21.13, -42.73) * mm});
            skLineSegment(sketch, "E3291", {"start": v(-21.13, -42.73) * mm, "end": v(-21.06, -42.59) * mm});
            skLineSegment(sketch, "E3292", {"start": v(-21.06, -42.59) * mm, "end": v(-21, -42.44) * mm});
            skLineSegment(sketch, "E3293", {"start": v(-21, -42.44) * mm, "end": v(-20.93, -42.3) * mm});
            skLineSegment(sketch, "E3294", {"start": v(-20.93, -42.3) * mm, "end": v(-20.86, -42.16) * mm});
            skLineSegment(sketch, "E3295", {"start": v(-20.86, -42.16) * mm, "end": v(-20.79, -42.01) * mm});
            skLineSegment(sketch, "E3296", {"start": v(-20.79, -42.01) * mm, "end": v(-20.72, -41.87) * mm});
            skLineSegment(sketch, "E3297", {"start": v(-20.72, -41.87) * mm, "end": v(-20.65, -41.73) * mm});
            skLineSegment(sketch, "E3298", {"start": v(-20.65, -41.73) * mm, "end": v(-20.58, -41.59) * mm});
            skLineSegment(sketch, "E3299", {"start": v(-20.58, -41.59) * mm, "end": v(-20.53, -41.48) * mm});
            skLineSegment(sketch, "E3300", {"start": v(-20.53, -41.48) * mm, "end": v(-20.4, -41.55) * mm});
            skLineSegment(sketch, "E3301", {"start": v(-20.4, -41.55) * mm, "end": v(-20.25, -41.61) * mm});
            skLineSegment(sketch, "E3302", {"start": v(-20.25, -41.61) * mm, "end": v(-20.1, -41.68) * mm});
            skLineSegment(sketch, "E3303", {"start": v(-20.1, -41.68) * mm, "end": v(-19.96, -41.74) * mm});
            skLineSegment(sketch, "E3304", {"start": v(-19.96, -41.74) * mm, "end": v(-19.82, -41.8) * mm});
            skLineSegment(sketch, "E3305", {"start": v(-19.82, -41.8) * mm, "end": v(-19.68, -41.87) * mm});
            skLineSegment(sketch, "E3306", {"start": v(-19.68, -41.87) * mm, "end": v(-19.53, -41.94) * mm});
            skLineSegment(sketch, "E3307", {"start": v(-19.53, -41.94) * mm, "end": v(-19.39, -42) * mm});
            skLineSegment(sketch, "E3308", {"start": v(-19.39, -42) * mm, "end": v(-19.25, -42.07) * mm});
            skLineSegment(sketch, "E3309", {"start": v(-19.25, -42.07) * mm, "end": v(-19.1, -42.13) * mm});
            skLineSegment(sketch, "E3310", {"start": v(-19.1, -42.13) * mm, "end": v(-18.96, -42.2) * mm});
            skLineSegment(sketch, "E3311", {"start": v(-18.96, -42.2) * mm, "end": v(-18.89, -42.23) * mm});
            skLineSegment(sketch, "E3312", {"start": v(-18.89, -42.23) * mm, "end": v(-18.95, -42.37) * mm});
            skLineSegment(sketch, "E3313", {"start": v(-18.95, -42.37) * mm, "end": v(-19, -42.52) * mm});
            skLineSegment(sketch, "E3314", {"start": v(-19, -42.52) * mm, "end": v(-19.07, -42.67) * mm});
            skLineSegment(sketch, "E3315", {"start": v(-19.07, -42.67) * mm, "end": v(-19.14, -42.81) * mm});
            skLineSegment(sketch, "E3316", {"start": v(-19.14, -42.81) * mm, "end": v(-19.2, -42.96) * mm});
            skLineSegment(sketch, "E3317", {"start": v(-19.2, -42.96) * mm, "end": v(-19.26, -43.1) * mm});
            skLineSegment(sketch, "E3318", {"start": v(-19.26, -43.1) * mm, "end": v(-19.32, -43.25) * mm});
            skLineSegment(sketch, "E3319", {"start": v(-19.32, -43.25) * mm, "end": v(-19.39, -43.4) * mm});
            skLineSegment(sketch, "E3320", {"start": v(-19.39, -43.4) * mm, "end": v(-19.45, -43.54) * mm});
            skLineSegment(sketch, "E3321", {"start": v(-19.45, -43.54) * mm, "end": v(-19.51, -43.69) * mm});
            skLineSegment(sketch, "E3322", {"start": v(-19.51, -43.69) * mm, "end": v(-19.57, -43.83) * mm});
            skLineSegment(sketch, "E3323", {"start": v(-19.57, -43.83) * mm, "end": v(-19.64, -43.98) * mm});
            skLineSegment(sketch, "E3324", {"start": v(-19.64, -43.98) * mm, "end": v(-19.7, -44.13) * mm});
            skLineSegment(sketch, "E3325", {"start": v(-19.7, -44.13) * mm, "end": v(-19.74, -44.3) * mm});
            skLineSegment(sketch, "E3326", {"start": v(-19.74, -44.3) * mm, "end": v(-19.73, -44.46) * mm});
            skLineSegment(sketch, "E3327", {"start": v(-19.73, -44.46) * mm, "end": v(-19.68, -44.61) * mm});
            skLineSegment(sketch, "E3328", {"start": v(-19.68, -44.61) * mm, "end": v(-19.6, -44.75) * mm});
            skLineSegment(sketch, "E3329", {"start": v(-19.6, -44.75) * mm, "end": v(-19.47, -44.86) * mm});
            skLineSegment(sketch, "E3330", {"start": v(-19.47, -44.86) * mm, "end": v(-19.32, -44.94) * mm});
            skLineSegment(sketch, "E3331", {"start": v(-19.32, -44.94) * mm, "end": v(-19.16, -44.97) * mm});
            skLineSegment(sketch, "E3332", {"start": v(-19.16, -44.97) * mm, "end": v(-19, -44.96) * mm});
            skLineSegment(sketch, "E3333", {"start": v(-19, -44.96) * mm, "end": v(-18.84, -44.91) * mm});
            skLineSegment(sketch, "E3334", {"start": v(-18.84, -44.91) * mm, "end": v(-18.7, -44.82) * mm});
            skLineSegment(sketch, "E3335", {"start": v(-18.7, -44.82) * mm, "end": v(-18.6, -44.7) * mm});
            skLineSegment(sketch, "E3336", {"start": v(-18.6, -44.7) * mm, "end": v(-18.53, -44.56) * mm});
            skLineSegment(sketch, "E3337", {"start": v(-18.53, -44.56) * mm, "end": v(-18.47, -44.41) * mm});
            skLineSegment(sketch, "E3338", {"start": v(-18.47, -44.41) * mm, "end": v(-18.4, -44.27) * mm});
            skLineSegment(sketch, "E3339", {"start": v(-18.4, -44.27) * mm, "end": v(-18.35, -44.12) * mm});
            skLineSegment(sketch, "E3340", {"start": v(-18.35, -44.12) * mm, "end": v(-18.3, -43.97) * mm});
            skLineSegment(sketch, "E3341", {"start": v(-18.3, -43.97) * mm, "end": v(-18.23, -43.82) * mm});
            skLineSegment(sketch, "E3342", {"start": v(-18.23, -43.82) * mm, "end": v(-18.18, -43.68) * mm});
            skLineSegment(sketch, "E3343", {"start": v(-18.18, -43.68) * mm, "end": v(-18.12, -43.53) * mm});
            skLineSegment(sketch, "E3344", {"start": v(-18.12, -43.53) * mm, "end": v(-18.06, -43.38) * mm});
            skLineSegment(sketch, "E3345", {"start": v(-18.06, -43.38) * mm, "end": v(-18, -43.24) * mm});
            skLineSegment(sketch, "E3346", {"start": v(-18, -43.24) * mm, "end": v(-17.94, -43.09) * mm});
            skLineSegment(sketch, "E3347", {"start": v(-17.94, -43.09) * mm, "end": v(-17.88, -42.94) * mm});
            skLineSegment(sketch, "E3348", {"start": v(-17.88, -42.94) * mm, "end": v(-17.82, -42.8) * mm});
            skLineSegment(sketch, "E3349", {"start": v(-17.82, -42.8) * mm, "end": v(-17.78, -42.69) * mm});
            skLineSegment(sketch, "E3350", {"start": v(-17.78, -42.69) * mm, "end": v(-17.63, -42.74) * mm});
            skLineSegment(sketch, "E3351", {"start": v(-17.63, -42.74) * mm, "end": v(-17.49, -42.8) * mm});
            skLineSegment(sketch, "E3352", {"start": v(-17.49, -42.8) * mm, "end": v(-17.34, -42.85) * mm});
            skLineSegment(sketch, "E3353", {"start": v(-17.34, -42.85) * mm, "end": v(-17.2, -42.9) * mm});
            skLineSegment(sketch, "E3354", {"start": v(-17.2, -42.9) * mm, "end": v(-17.04, -42.96) * mm});
            skLineSegment(sketch, "E3355", {"start": v(-17.04, -42.96) * mm, "end": v(-16.9, -43.02) * mm});
            skLineSegment(sketch, "E3356", {"start": v(-16.9, -43.02) * mm, "end": v(-16.75, -43.07) * mm});
            skLineSegment(sketch, "E3357", {"start": v(-16.75, -43.07) * mm, "end": v(-16.6, -43.13) * mm});
            skLineSegment(sketch, "E3358", {"start": v(-16.6, -43.13) * mm, "end": v(-16.45, -43.19) * mm});
            skLineSegment(sketch, "E3359", {"start": v(-16.45, -43.19) * mm, "end": v(-16.3, -43.24) * mm});
            skLineSegment(sketch, "E3360", {"start": v(-16.3, -43.24) * mm, "end": v(-16.16, -43.3) * mm});
            skLineSegment(sketch, "E3361", {"start": v(-16.16, -43.3) * mm, "end": v(-16.09, -43.32) * mm});
            skLineSegment(sketch, "E3362", {"start": v(-16.09, -43.32) * mm, "end": v(-16.14, -43.47) * mm});
            skLineSegment(sketch, "E3363", {"start": v(-16.14, -43.47) * mm, "end": v(-16.2, -43.62) * mm});
            skLineSegment(sketch, "E3364", {"start": v(-16.2, -43.62) * mm, "end": v(-16.24, -43.77) * mm});
            skLineSegment(sketch, "E3365", {"start": v(-16.24, -43.77) * mm, "end": v(-16.3, -43.92) * mm});
            skLineSegment(sketch, "E3366", {"start": v(-16.3, -43.92) * mm, "end": v(-16.35, -44.07) * mm});
            skLineSegment(sketch, "E3367", {"start": v(-16.35, -44.07) * mm, "end": v(-16.4, -44.22) * mm});
            skLineSegment(sketch, "E3368", {"start": v(-16.4, -44.22) * mm, "end": v(-16.46, -44.37) * mm});
            skLineSegment(sketch, "E3369", {"start": v(-16.46, -44.37) * mm, "end": v(-16.5, -44.52) * mm});
            skLineSegment(sketch, "E3370", {"start": v(-16.5, -44.52) * mm, "end": v(-16.56, -44.67) * mm});
            skLineSegment(sketch, "E3371", {"start": v(-16.56, -44.67) * mm, "end": v(-16.61, -44.82) * mm});
            skLineSegment(sketch, "E3372", {"start": v(-16.61, -44.82) * mm, "end": v(-16.67, -44.97) * mm});
            skLineSegment(sketch, "E3373", {"start": v(-16.67, -44.97) * mm, "end": v(-16.72, -45.12) * mm});
            skLineSegment(sketch, "E3374", {"start": v(-16.72, -45.12) * mm, "end": v(-16.78, -45.28) * mm});
            skLineSegment(sketch, "E3375", {"start": v(-16.78, -45.28) * mm, "end": v(-16.8, -45.44) * mm});
            skLineSegment(sketch, "E3376", {"start": v(-16.8, -45.44) * mm, "end": v(-16.78, -45.6) * mm});
            skLineSegment(sketch, "E3377", {"start": v(-16.78, -45.6) * mm, "end": v(-16.72, -45.76) * mm});
            skLineSegment(sketch, "E3378", {"start": v(-16.72, -45.76) * mm, "end": v(-16.62, -45.89) * mm});
            skLineSegment(sketch, "E3379", {"start": v(-16.62, -45.89) * mm, "end": v(-16.5, -45.99) * mm});
            skLineSegment(sketch, "E3380", {"start": v(-16.5, -45.99) * mm, "end": v(-16.34, -46.05) * mm});
            skLineSegment(sketch, "E3381", {"start": v(-16.34, -46.05) * mm, "end": v(-16.18, -46.08) * mm});
            skLineSegment(sketch, "E3382", {"start": v(-16.18, -46.08) * mm, "end": v(-16.02, -46.06) * mm});
            skLineSegment(sketch, "E3383", {"start": v(-16.02, -46.06) * mm, "end": v(-15.87, -46) * mm});
            skLineSegment(sketch, "E3384", {"start": v(-15.87, -46) * mm, "end": v(-15.74, -45.9) * mm});
            skLineSegment(sketch, "E3385", {"start": v(-15.74, -45.9) * mm, "end": v(-15.64, -45.77) * mm});
            skLineSegment(sketch, "E3386", {"start": v(-15.64, -45.77) * mm, "end": v(-15.58, -45.62) * mm});
            skLineSegment(sketch, "E3387", {"start": v(-15.58, -45.62) * mm, "end": v(-15.53, -45.48) * mm});
            skLineSegment(sketch, "E3388", {"start": v(-15.53, -45.48) * mm, "end": v(-15.48, -45.33) * mm});
            skLineSegment(sketch, "E3389", {"start": v(-15.48, -45.33) * mm, "end": v(-15.43, -45.18) * mm});
            skLineSegment(sketch, "E3390", {"start": v(-15.43, -45.18) * mm, "end": v(-15.38, -45.03) * mm});
            skLineSegment(sketch, "E3391", {"start": v(-15.38, -45.03) * mm, "end": v(-15.33, -44.87) * mm});
            skLineSegment(sketch, "E3392", {"start": v(-15.33, -44.87) * mm, "end": v(-15.28, -44.72) * mm});
            skLineSegment(sketch, "E3393", {"start": v(-15.28, -44.72) * mm, "end": v(-15.23, -44.57) * mm});
            skLineSegment(sketch, "E3394", {"start": v(-15.23, -44.57) * mm, "end": v(-15.18, -44.42) * mm});
            skLineSegment(sketch, "E3395", {"start": v(-15.18, -44.42) * mm, "end": v(-15.13, -44.27) * mm});
            skLineSegment(sketch, "E3396", {"start": v(-15.13, -44.27) * mm, "end": v(-15.09, -44.12) * mm});
            skLineSegment(sketch, "E3397", {"start": v(-15.09, -44.12) * mm, "end": v(-15.04, -43.97) * mm});
            skLineSegment(sketch, "E3398", {"start": v(-15.04, -43.97) * mm, "end": v(-14.99, -43.82) * mm});
            skLineSegment(sketch, "E3399", {"start": v(-14.99, -43.82) * mm, "end": v(-14.95, -43.7) * mm});
            skLineSegment(sketch, "E3400", {"start": v(-14.95, -43.7) * mm, "end": v(-14.8, -43.76) * mm});
            skLineSegment(sketch, "E3401", {"start": v(-14.8, -43.76) * mm, "end": v(-14.65, -43.8) * mm});
            skLineSegment(sketch, "E3402", {"start": v(-14.65, -43.8) * mm, "end": v(-14.5, -43.85) * mm});
            skLineSegment(sketch, "E3403", {"start": v(-14.5, -43.85) * mm, "end": v(-14.35, -43.9) * mm});
            skLineSegment(sketch, "E3404", {"start": v(-14.35, -43.9) * mm, "end": v(-14.2, -43.94) * mm});
            skLineSegment(sketch, "E3405", {"start": v(-14.2, -43.94) * mm, "end": v(-14.05, -43.98) * mm});
            skLineSegment(sketch, "E3406", {"start": v(-14.05, -43.98) * mm, "end": v(-13.9, -44.03) * mm});
            skLineSegment(sketch, "E3407", {"start": v(-13.9, -44.03) * mm, "end": v(-13.75, -44.07) * mm});
            skLineSegment(sketch, "E3408", {"start": v(-13.75, -44.07) * mm, "end": v(-13.6, -44.12) * mm});
            skLineSegment(sketch, "E3409", {"start": v(-13.6, -44.12) * mm, "end": v(-13.45, -44.17) * mm});
            skLineSegment(sketch, "E3410", {"start": v(-13.45, -44.17) * mm, "end": v(-13.3, -44.21) * mm});
            skLineSegment(sketch, "E3411", {"start": v(-13.3, -44.21) * mm, "end": v(-13.22, -44.23) * mm});
            skLineSegment(sketch, "E3412", {"start": v(-13.22, -44.23) * mm, "end": v(-13.26, -44.39) * mm});
            skLineSegment(sketch, "E3413", {"start": v(-13.26, -44.39) * mm, "end": v(-13.3, -44.54) * mm});
            skLineSegment(sketch, "E3414", {"start": v(-13.3, -44.54) * mm, "end": v(-13.35, -44.7) * mm});
            skLineSegment(sketch, "E3415", {"start": v(-13.35, -44.7) * mm, "end": v(-13.4, -44.84) * mm});
            skLineSegment(sketch, "E3416", {"start": v(-13.4, -44.84) * mm, "end": v(-13.43, -45) * mm});
            skLineSegment(sketch, "E3417", {"start": v(-13.43, -45) * mm, "end": v(-13.48, -45.15) * mm});
            skLineSegment(sketch, "E3418", {"start": v(-13.48, -45.15) * mm, "end": v(-13.52, -45.3) * mm});
            skLineSegment(sketch, "E3419", {"start": v(-13.52, -45.3) * mm, "end": v(-13.56, -45.45) * mm});
            skLineSegment(sketch, "E3420", {"start": v(-13.56, -45.45) * mm, "end": v(-13.6, -45.6) * mm});
            skLineSegment(sketch, "E3421", {"start": v(-13.6, -45.6) * mm, "end": v(-13.65, -45.76) * mm});
            skLineSegment(sketch, "E3422", {"start": v(-13.65, -45.76) * mm, "end": v(-13.7, -45.91) * mm});
            skLineSegment(sketch, "E3423", {"start": v(-13.7, -45.91) * mm, "end": v(-13.74, -46.07) * mm});
            skLineSegment(sketch, "E3424", {"start": v(-13.74, -46.07) * mm, "end": v(-13.78, -46.23) * mm});
            skLineSegment(sketch, "E3425", {"start": v(-13.78, -46.23) * mm, "end": v(-13.8, -46.4) * mm});
            skLineSegment(sketch, "E3426", {"start": v(-13.8, -46.4) * mm, "end": v(-13.77, -46.56) * mm});
            skLineSegment(sketch, "E3427", {"start": v(-13.77, -46.56) * mm, "end": v(-13.7, -46.7) * mm});
            skLineSegment(sketch, "E3428", {"start": v(-13.7, -46.7) * mm, "end": v(-13.59, -46.83) * mm});
            skLineSegment(sketch, "E3429", {"start": v(-13.59, -46.83) * mm, "end": v(-13.45, -46.92) * mm});
            skLineSegment(sketch, "E3430", {"start": v(-13.45, -46.92) * mm, "end": v(-13.3, -46.98) * mm});
            skLineSegment(sketch, "E3431", {"start": v(-13.3, -46.98) * mm, "end": v(-13.14, -46.99) * mm});
            skLineSegment(sketch, "E3432", {"start": v(-13.14, -46.99) * mm, "end": v(-12.97, -46.96) * mm});
            skLineSegment(sketch, "E3433", {"start": v(-12.97, -46.96) * mm, "end": v(-12.83, -46.89) * mm});
            skLineSegment(sketch, "E3434", {"start": v(-12.83, -46.89) * mm, "end": v(-12.7, -46.78) * mm});
            skLineSegment(sketch, "E3435", {"start": v(-12.7, -46.78) * mm, "end": v(-12.61, -46.65) * mm});
            skLineSegment(sketch, "E3436", {"start": v(-12.61, -46.65) * mm, "end": v(-12.56, -46.5) * mm});
            skLineSegment(sketch, "E3437", {"start": v(-12.56, -46.5) * mm, "end": v(-12.52, -46.34) * mm});
            skLineSegment(sketch, "E3438", {"start": v(-12.52, -46.34) * mm, "end": v(-12.48, -46.2) * mm});
            skLineSegment(sketch, "E3439", {"start": v(-12.48, -46.2) * mm, "end": v(-12.44, -46.04) * mm});
            skLineSegment(sketch, "E3440", {"start": v(-12.44, -46.04) * mm, "end": v(-12.4, -45.89) * mm});
            skLineSegment(sketch, "E3441", {"start": v(-12.4, -45.89) * mm, "end": v(-12.36, -45.73) * mm});
            skLineSegment(sketch, "E3442", {"start": v(-12.36, -45.73) * mm, "end": v(-12.32, -45.58) * mm});
            skLineSegment(sketch, "E3443", {"start": v(-12.32, -45.58) * mm, "end": v(-12.29, -45.43) * mm});
            skLineSegment(sketch, "E3444", {"start": v(-12.29, -45.43) * mm, "end": v(-12.25, -45.27) * mm});
            skLineSegment(sketch, "E3445", {"start": v(-12.25, -45.27) * mm, "end": v(-12.2, -45.12) * mm});
            skLineSegment(sketch, "E3446", {"start": v(-12.2, -45.12) * mm, "end": v(-12.17, -44.97) * mm});
            skLineSegment(sketch, "E3447", {"start": v(-12.17, -44.97) * mm, "end": v(-12.13, -44.8) * mm});
            skLineSegment(sketch, "E3448", {"start": v(-12.13, -44.8) * mm, "end": v(-12.1, -44.66) * mm});
            skLineSegment(sketch, "E3449", {"start": v(-12.1, -44.66) * mm, "end": v(-12.06, -44.54) * mm});
            skLineSegment(sketch, "E3450", {"start": v(-12.06, -44.54) * mm, "end": v(-11.9, -44.58) * mm});
            skLineSegment(sketch, "E3451", {"start": v(-11.9, -44.58) * mm, "end": v(-11.76, -44.62) * mm});
            skLineSegment(sketch, "E3452", {"start": v(-11.76, -44.62) * mm, "end": v(-11.6, -44.65) * mm});
            skLineSegment(sketch, "E3453", {"start": v(-11.6, -44.65) * mm, "end": v(-11.45, -44.69) * mm});
            skLineSegment(sketch, "E3454", {"start": v(-11.45, -44.69) * mm, "end": v(-11.3, -44.72) * mm});
            skLineSegment(sketch, "E3455", {"start": v(-11.3, -44.72) * mm, "end": v(-11.14, -44.76) * mm});
            skLineSegment(sketch, "E3456", {"start": v(-11.14, -44.76) * mm, "end": v(-10.99, -44.8) * mm});
            skLineSegment(sketch, "E3457", {"start": v(-10.99, -44.8) * mm, "end": v(-10.84, -44.83) * mm});
            skLineSegment(sketch, "E3458", {"start": v(-10.84, -44.83) * mm, "end": v(-10.68, -44.87) * mm});
            skLineSegment(sketch, "E3459", {"start": v(-10.68, -44.87) * mm, "end": v(-10.53, -44.9) * mm});
            skLineSegment(sketch, "E3460", {"start": v(-10.53, -44.9) * mm, "end": v(-10.38, -44.94) * mm});
            skLineSegment(sketch, "E3461", {"start": v(-10.38, -44.94) * mm, "end": v(-10.3, -44.96) * mm});
            skLineSegment(sketch, "E3462", {"start": v(-10.3, -44.96) * mm, "end": v(-10.33, -45.1) * mm});
            skLineSegment(sketch, "E3463", {"start": v(-10.33, -45.1) * mm, "end": v(-10.36, -45.26) * mm});
            skLineSegment(sketch, "E3464", {"start": v(-10.36, -45.26) * mm, "end": v(-10.4, -45.42) * mm});
            skLineSegment(sketch, "E3465", {"start": v(-10.4, -45.42) * mm, "end": v(-10.43, -45.58) * mm});
            skLineSegment(sketch, "E3466", {"start": v(-10.43, -45.58) * mm, "end": v(-10.46, -45.73) * mm});
            skLineSegment(sketch, "E3467", {"start": v(-10.46, -45.73) * mm, "end": v(-10.5, -45.89) * mm});
            skLineSegment(sketch, "E3468", {"start": v(-10.5, -45.89) * mm, "end": v(-10.53, -46.04) * mm});
            skLineSegment(sketch, "E3469", {"start": v(-10.53, -46.04) * mm, "end": v(-10.56, -46.2) * mm});
            skLineSegment(sketch, "E3470", {"start": v(-10.56, -46.2) * mm, "end": v(-10.6, -46.35) * mm});
            skLineSegment(sketch, "E3471", {"start": v(-10.6, -46.35) * mm, "end": v(-10.63, -46.5) * mm});
            skLineSegment(sketch, "E3472", {"start": v(-10.63, -46.5) * mm, "end": v(-10.66, -46.66) * mm});
            skLineSegment(sketch, "E3473", {"start": v(-10.66, -46.66) * mm, "end": v(-10.7, -46.82) * mm});
            skLineSegment(sketch, "E3474", {"start": v(-10.7, -46.82) * mm, "end": v(-10.73, -46.98) * mm});
            skLineSegment(sketch, "E3475", {"start": v(-10.73, -46.98) * mm, "end": v(-10.73, -47.15) * mm});
            skLineSegment(sketch, "E3476", {"start": v(-10.73, -47.15) * mm, "end": v(-10.7, -47.3) * mm});
            skLineSegment(sketch, "E3477", {"start": v(-10.7, -47.3) * mm, "end": v(-10.61, -47.45) * mm});
            skLineSegment(sketch, "E3478", {"start": v(-10.61, -47.45) * mm, "end": v(-10.5, -47.57) * mm});
            skLineSegment(sketch, "E3479", {"start": v(-10.5, -47.57) * mm, "end": v(-10.36, -47.65) * mm});
            skLineSegment(sketch, "E3480", {"start": v(-10.36, -47.65) * mm, "end": v(-10.2, -47.7) * mm});
            skLineSegment(sketch, "E3481", {"start": v(-10.2, -47.7) * mm, "end": v(-10.04, -47.7) * mm});
            skLineSegment(sketch, "E3482", {"start": v(-10.04, -47.7) * mm, "end": v(-9.88, -47.66) * mm});
            skLineSegment(sketch, "E3483", {"start": v(-9.88, -47.66) * mm, "end": v(-9.73, -47.58) * mm});
            skLineSegment(sketch, "E3484", {"start": v(-9.73, -47.58) * mm, "end": v(-9.62, -47.46) * mm});
            skLineSegment(sketch, "E3485", {"start": v(-9.62, -47.46) * mm, "end": v(-9.53, -47.32) * mm});
            skLineSegment(sketch, "E3486", {"start": v(-9.53, -47.32) * mm, "end": v(-9.5, -47.17) * mm});
            skLineSegment(sketch, "E3487", {"start": v(-9.5, -47.17) * mm, "end": v(-9.46, -47.02) * mm});
            skLineSegment(sketch, "E3488", {"start": v(-9.46, -47.02) * mm, "end": v(-9.43, -46.86) * mm});
            skLineSegment(sketch, "E3489", {"start": v(-9.43, -46.86) * mm, "end": v(-9.4, -46.7) * mm});
            skLineSegment(sketch, "E3490", {"start": v(-9.4, -46.7) * mm, "end": v(-9.38, -46.55) * mm});
            skLineSegment(sketch, "E3491", {"start": v(-9.38, -46.55) * mm, "end": v(-9.35, -46.4) * mm});
            skLineSegment(sketch, "E3492", {"start": v(-9.35, -46.4) * mm, "end": v(-9.32, -46.24) * mm});
            skLineSegment(sketch, "E3493", {"start": v(-9.32, -46.24) * mm, "end": v(-9.3, -46.08) * mm});
            skLineSegment(sketch, "E3494", {"start": v(-9.3, -46.08) * mm, "end": v(-9.26, -45.93) * mm});
            skLineSegment(sketch, "E3495", {"start": v(-9.26, -45.93) * mm, "end": v(-9.23, -45.77) * mm});
            skLineSegment(sketch, "E3496", {"start": v(-9.23, -45.77) * mm, "end": v(-9.2, -45.62) * mm});
            skLineSegment(sketch, "E3497", {"start": v(-9.2, -45.62) * mm, "end": v(-9.17, -45.46) * mm});
            skLineSegment(sketch, "E3498", {"start": v(-9.17, -45.46) * mm, "end": v(-9.15, -45.3) * mm});
            skLineSegment(sketch, "E3499", {"start": v(-9.15, -45.3) * mm, "end": v(-9.12, -45.19) * mm});
            skLineSegment(sketch, "E3500", {"start": v(-9.12, -45.19) * mm, "end": v(-8.97, -45.22) * mm});
            skLineSegment(sketch, "E3501", {"start": v(-8.97, -45.22) * mm, "end": v(-8.81, -45.24) * mm});
            skLineSegment(sketch, "E3502", {"start": v(-8.81, -45.24) * mm, "end": v(-8.66, -45.27) * mm});
            skLineSegment(sketch, "E3503", {"start": v(-8.66, -45.27) * mm, "end": v(-8.5, -45.3) * mm});
            skLineSegment(sketch, "E3504", {"start": v(-8.5, -45.3) * mm, "end": v(-8.35, -45.32) * mm});
            skLineSegment(sketch, "E3505", {"start": v(-8.35, -45.32) * mm, "end": v(-8.2, -45.34) * mm});
            skLineSegment(sketch, "E3506", {"start": v(-8.2, -45.34) * mm, "end": v(-8.04, -45.37) * mm});
            skLineSegment(sketch, "E3507", {"start": v(-8.04, -45.37) * mm, "end": v(-7.88, -45.4) * mm});
            skLineSegment(sketch, "E3508", {"start": v(-7.88, -45.4) * mm, "end": v(-7.73, -45.42) * mm});
            skLineSegment(sketch, "E3509", {"start": v(-7.73, -45.42) * mm, "end": v(-7.57, -45.45) * mm});
            skLineSegment(sketch, "E3510", {"start": v(-7.57, -45.45) * mm, "end": v(-7.42, -45.47) * mm});
            skLineSegment(sketch, "E3511", {"start": v(-7.42, -45.47) * mm, "end": v(-7.34, -45.48) * mm});
            skLineSegment(sketch, "E3512", {"start": v(-7.34, -45.48) * mm, "end": v(-7.36, -45.64) * mm});
            skLineSegment(sketch, "E3513", {"start": v(-7.36, -45.64) * mm, "end": v(-7.38, -45.8) * mm});
            skLineSegment(sketch, "E3514", {"start": v(-7.38, -45.8) * mm, "end": v(-7.4, -45.96) * mm});
            skLineSegment(sketch, "E3515", {"start": v(-7.4, -45.96) * mm, "end": v(-7.43, -46.11) * mm});
            skLineSegment(sketch, "E3516", {"start": v(-7.43, -46.11) * mm, "end": v(-7.45, -46.27) * mm});
            skLineSegment(sketch, "E3517", {"start": v(-7.45, -46.27) * mm, "end": v(-7.47, -46.43) * mm});
            skLineSegment(sketch, "E3518", {"start": v(-7.47, -46.43) * mm, "end": v(-7.5, -46.58) * mm});
            skLineSegment(sketch, "E3519", {"start": v(-7.5, -46.58) * mm, "end": v(-7.52, -46.74) * mm});
            skLineSegment(sketch, "E3520", {"start": v(-7.52, -46.74) * mm, "end": v(-7.54, -46.9) * mm});
            skLineSegment(sketch, "E3521", {"start": v(-7.54, -46.9) * mm, "end": v(-7.57, -47.05) * mm});
            skLineSegment(sketch, "E3522", {"start": v(-7.57, -47.05) * mm, "end": v(-7.59, -47.2) * mm});
            skLineSegment(sketch, "E3523", {"start": v(-7.59, -47.2) * mm, "end": v(-7.61, -47.37) * mm});
            skLineSegment(sketch, "E3524", {"start": v(-7.61, -47.37) * mm, "end": v(-7.63, -47.54) * mm});
            skLineSegment(sketch, "E3525", {"start": v(-7.63, -47.54) * mm, "end": v(-7.63, -47.7) * mm});
            skLineSegment(sketch, "E3526", {"start": v(-7.63, -47.7) * mm, "end": v(-7.58, -47.86) * mm});
            skLineSegment(sketch, "E3527", {"start": v(-7.58, -47.86) * mm, "end": v(-7.49, -48) * mm});
            skLineSegment(sketch, "E3528", {"start": v(-7.49, -48) * mm, "end": v(-7.37, -48.1) * mm});
            skLineSegment(sketch, "E3529", {"start": v(-7.37, -48.1) * mm, "end": v(-7.22, -48.18) * mm});
            skLineSegment(sketch, "E3530", {"start": v(-7.22, -48.18) * mm, "end": v(-7.06, -48.21) * mm});
            skLineSegment(sketch, "E3531", {"start": v(-7.06, -48.21) * mm, "end": v(-6.9, -48.2) * mm});
            skLineSegment(sketch, "E3532", {"start": v(-6.9, -48.2) * mm, "end": v(-6.74, -48.15) * mm});
            skLineSegment(sketch, "E3533", {"start": v(-6.74, -48.15) * mm, "end": v(-6.6, -48.06) * mm});
            skLineSegment(sketch, "E3534", {"start": v(-6.6, -48.06) * mm, "end": v(-6.5, -47.94) * mm});
            skLineSegment(sketch, "E3535", {"start": v(-6.5, -47.94) * mm, "end": v(-6.42, -47.8) * mm});
            skLineSegment(sketch, "E3536", {"start": v(-6.42, -47.8) * mm, "end": v(-6.4, -47.64) * mm});
            skLineSegment(sketch, "E3537", {"start": v(-6.4, -47.64) * mm, "end": v(-6.37, -47.48) * mm});
            skLineSegment(sketch, "E3538", {"start": v(-6.37, -47.48) * mm, "end": v(-6.35, -47.33) * mm});
            skLineSegment(sketch, "E3539", {"start": v(-6.35, -47.33) * mm, "end": v(-6.33, -47.17) * mm});
            skLineSegment(sketch, "E3540", {"start": v(-6.33, -47.17) * mm, "end": v(-6.31, -47.02) * mm});
            skLineSegment(sketch, "E3541", {"start": v(-6.31, -47.02) * mm, "end": v(-6.3, -46.86) * mm});
            skLineSegment(sketch, "E3542", {"start": v(-6.3, -46.86) * mm, "end": v(-6.28, -46.7) * mm});
            skLineSegment(sketch, "E3543", {"start": v(-6.28, -46.7) * mm, "end": v(-6.26, -46.54) * mm});
            skLineSegment(sketch, "E3544", {"start": v(-6.26, -46.54) * mm, "end": v(-6.24, -46.38) * mm});
            skLineSegment(sketch, "E3545", {"start": v(-6.24, -46.38) * mm, "end": v(-6.22, -46.23) * mm});
            skLineSegment(sketch, "E3546", {"start": v(-6.22, -46.23) * mm, "end": v(-6.2, -46.07) * mm});
            skLineSegment(sketch, "E3547", {"start": v(-6.2, -46.07) * mm, "end": v(-6.18, -45.91) * mm});
            skLineSegment(sketch, "E3548", {"start": v(-6.18, -45.91) * mm, "end": v(-6.16, -45.75) * mm});
            skLineSegment(sketch, "E3549", {"start": v(-6.16, -45.75) * mm, "end": v(-6.15, -45.64) * mm});
            skLineSegment(sketch, "E3550", {"start": v(-6.15, -45.64) * mm, "end": v(-6, -45.66) * mm});
            skLineSegment(sketch, "E3551", {"start": v(-6, -45.66) * mm, "end": v(-5.84, -45.67) * mm});
            skLineSegment(sketch, "E3552", {"start": v(-5.84, -45.67) * mm, "end": v(-5.68, -45.69) * mm});
            skLineSegment(sketch, "E3553", {"start": v(-5.68, -45.69) * mm, "end": v(-5.52, -45.7) * mm});
            skLineSegment(sketch, "E3554", {"start": v(-5.52, -45.7) * mm, "end": v(-5.37, -45.72) * mm});
            skLineSegment(sketch, "E3555", {"start": v(-5.37, -45.72) * mm, "end": v(-5.21, -45.73) * mm});
            skLineSegment(sketch, "E3556", {"start": v(-5.21, -45.73) * mm, "end": v(-5.06, -45.75) * mm});
            skLineSegment(sketch, "E3557", {"start": v(-5.06, -45.75) * mm, "end": v(-4.9, -45.76) * mm});
            skLineSegment(sketch, "E3558", {"start": v(-4.9, -45.76) * mm, "end": v(-4.74, -45.78) * mm});
            skLineSegment(sketch, "E3559", {"start": v(-4.74, -45.78) * mm, "end": v(-4.59, -45.8) * mm});
            skLineSegment(sketch, "E3560", {"start": v(-4.59, -45.8) * mm, "end": v(-4.43, -45.81) * mm});
            skLineSegment(sketch, "E3561", {"start": v(-4.43, -45.81) * mm, "end": v(-4.35, -45.82) * mm});
            skLineSegment(sketch, "E3562", {"start": v(-4.35, -45.82) * mm, "end": v(-4.36, -45.98) * mm});
            skLineSegment(sketch, "E3563", {"start": v(-4.36, -45.98) * mm, "end": v(-4.37, -46.13) * mm});
            skLineSegment(sketch, "E3564", {"start": v(-4.37, -46.13) * mm, "end": v(-4.39, -46.3) * mm});
            skLineSegment(sketch, "E3565", {"start": v(-4.39, -46.3) * mm, "end": v(-4.4, -46.45) * mm});
            skLineSegment(sketch, "E3566", {"start": v(-4.4, -46.45) * mm, "end": v(-4.41, -46.6) * mm});
            skLineSegment(sketch, "E3567", {"start": v(-4.41, -46.6) * mm, "end": v(-4.42, -46.77) * mm});
            skLineSegment(sketch, "E3568", {"start": v(-4.42, -46.77) * mm, "end": v(-4.44, -46.92) * mm});
            skLineSegment(sketch, "E3569", {"start": v(-4.44, -46.92) * mm, "end": v(-4.45, -47.08) * mm});
            skLineSegment(sketch, "E3570", {"start": v(-4.45, -47.08) * mm, "end": v(-4.46, -47.24) * mm});
            skLineSegment(sketch, "E3571", {"start": v(-4.46, -47.24) * mm, "end": v(-4.47, -47.4) * mm});
            skLineSegment(sketch, "E3572", {"start": v(-4.47, -47.4) * mm, "end": v(-4.49, -47.56) * mm});
            skLineSegment(sketch, "E3573", {"start": v(-4.49, -47.56) * mm, "end": v(-4.5, -47.72) * mm});
            skLineSegment(sketch, "E3574", {"start": v(-4.5, -47.72) * mm, "end": v(-4.51, -47.89) * mm});
            skLineSegment(sketch, "E3575", {"start": v(-4.51, -47.89) * mm, "end": v(-4.5, -48.05) * mm});
            skLineSegment(sketch, "E3576", {"start": v(-4.5, -48.05) * mm, "end": v(-4.43, -48.2) * mm});
            skLineSegment(sketch, "E3577", {"start": v(-4.43, -48.2) * mm, "end": v(-4.33, -48.33) * mm});
            skLineSegment(sketch, "E3578", {"start": v(-4.33, -48.33) * mm, "end": v(-4.2, -48.43) * mm});
            skLineSegment(sketch, "E3579", {"start": v(-4.2, -48.43) * mm, "end": v(-4.06, -48.5) * mm});
            skLineSegment(sketch, "E3580", {"start": v(-4.06, -48.5) * mm, "end": v(-3.9, -48.52) * mm});
            skLineSegment(sketch, "E3581", {"start": v(-3.9, -48.52) * mm, "end": v(-3.73, -48.5) * mm});
            skLineSegment(sketch, "E3582", {"start": v(-3.73, -48.5) * mm, "end": v(-3.58, -48.44) * mm});
            skLineSegment(sketch, "E3583", {"start": v(-3.58, -48.44) * mm, "end": v(-3.45, -48.34) * mm});
            skLineSegment(sketch, "E3584", {"start": v(-3.45, -48.34) * mm, "end": v(-3.35, -48.21) * mm});
            skLineSegment(sketch, "E3585", {"start": v(-3.35, -48.21) * mm, "end": v(-3.28, -48.06) * mm});
            skLineSegment(sketch, "E3586", {"start": v(-3.28, -48.06) * mm, "end": v(-3.26, -47.9) * mm});
            skLineSegment(sketch, "E3587", {"start": v(-3.26, -47.9) * mm, "end": v(-3.25, -47.75) * mm});
            skLineSegment(sketch, "E3588", {"start": v(-3.25, -47.75) * mm, "end": v(-3.24, -47.6) * mm});
            skLineSegment(sketch, "E3589", {"start": v(-3.24, -47.6) * mm, "end": v(-3.24, -47.44) * mm});
            skLineSegment(sketch, "E3590", {"start": v(-3.24, -47.44) * mm, "end": v(-3.23, -47.28) * mm});
            skLineSegment(sketch, "E3591", {"start": v(-3.23, -47.28) * mm, "end": v(-3.22, -47.12) * mm});
            skLineSegment(sketch, "E3592", {"start": v(-3.22, -47.12) * mm, "end": v(-3.21, -46.96) * mm});
            skLineSegment(sketch, "E3593", {"start": v(-3.21, -46.96) * mm, "end": v(-3.2, -46.8) * mm});
            skLineSegment(sketch, "E3594", {"start": v(-3.2, -46.8) * mm, "end": v(-3.2, -46.64) * mm});
            skLineSegment(sketch, "E3595", {"start": v(-3.2, -46.64) * mm, "end": v(-3.19, -46.49) * mm});
            skLineSegment(sketch, "E3596", {"start": v(-3.19, -46.49) * mm, "end": v(-3.18, -46.33) * mm});
            skLineSegment(sketch, "E3597", {"start": v(-3.18, -46.33) * mm, "end": v(-3.17, -46.17) * mm});
            skLineSegment(sketch, "E3598", {"start": v(-3.17, -46.17) * mm, "end": v(-3.16, -46.01) * mm});
            skLineSegment(sketch, "E3599", {"start": v(-3.16, -46.01) * mm, "end": v(-3.15, -45.9) * mm});
            skLineSegment(sketch, "E3600", {"start": v(-3.15, -45.9) * mm, "end": v(-3, -45.9) * mm});
            skLineSegment(sketch, "E3601", {"start": v(-3, -45.9) * mm, "end": v(-2.84, -45.9) * mm});
            skLineSegment(sketch, "E3602", {"start": v(-2.84, -45.9) * mm, "end": v(-2.68, -45.91) * mm});
            skLineSegment(sketch, "E3603", {"start": v(-2.68, -45.91) * mm, "end": v(-2.53, -45.92) * mm});
            skLineSegment(sketch, "E3604", {"start": v(-2.53, -45.92) * mm, "end": v(-2.37, -45.92) * mm});
            skLineSegment(sketch, "E3605", {"start": v(-2.37, -45.92) * mm, "end": v(-2.21, -45.93) * mm});
            skLineSegment(sketch, "E3606", {"start": v(-2.21, -45.93) * mm, "end": v(-2.05, -45.93) * mm});
            skLineSegment(sketch, "E3607", {"start": v(-2.05, -45.93) * mm, "end": v(-1.9, -45.94) * mm});
            skLineSegment(sketch, "E3608", {"start": v(-1.9, -45.94) * mm, "end": v(-1.74, -45.94) * mm});
            skLineSegment(sketch, "E3609", {"start": v(-1.74, -45.94) * mm, "end": v(-1.58, -45.95) * mm});
            skLineSegment(sketch, "E3610", {"start": v(-1.58, -45.95) * mm, "end": v(-1.43, -45.95) * mm});
            skLineSegment(sketch, "E3611", {"start": v(-1.43, -45.95) * mm, "end": v(-1.34, -45.96) * mm});
            skLineSegment(sketch, "E3612", {"start": v(-1.34, -45.96) * mm, "end": v(-1.35, -46.11) * mm});
            skLineSegment(sketch, "E3613", {"start": v(-1.35, -46.11) * mm, "end": v(-1.35, -46.27) * mm});
            skLineSegment(sketch, "E3614", {"start": v(-1.35, -46.27) * mm, "end": v(-1.35, -46.43) * mm});
            skLineSegment(sketch, "E3615", {"start": v(-1.35, -46.43) * mm, "end": v(-1.35, -46.59) * mm});
            skLineSegment(sketch, "E3616", {"start": v(-1.35, -46.59) * mm, "end": v(-1.36, -46.75) * mm});
            skLineSegment(sketch, "E3617", {"start": v(-1.36, -46.75) * mm, "end": v(-1.36, -46.9) * mm});
            skLineSegment(sketch, "E3618", {"start": v(-1.36, -46.9) * mm, "end": v(-1.36, -47.07) * mm});
            skLineSegment(sketch, "E3619", {"start": v(-1.36, -47.07) * mm, "end": v(-1.36, -47.22) * mm});
            skLineSegment(sketch, "E3620", {"start": v(-1.36, -47.22) * mm, "end": v(-1.36, -47.38) * mm});
            skLineSegment(sketch, "E3621", {"start": v(-1.36, -47.38) * mm, "end": v(-1.37, -47.54) * mm});
            skLineSegment(sketch, "E3622", {"start": v(-1.37, -47.54) * mm, "end": v(-1.37, -47.7) * mm});
            skLineSegment(sketch, "E3623", {"start": v(-1.37, -47.7) * mm, "end": v(-1.37, -47.86) * mm});
            skLineSegment(sketch, "E3624", {"start": v(-1.37, -47.86) * mm, "end": v(-1.37, -48.03) * mm});
            skLineSegment(sketch, "E3625", {"start": v(-1.37, -48.03) * mm, "end": v(-1.34, -48.2) * mm});
            skLineSegment(sketch, "E3626", {"start": v(-1.34, -48.2) * mm, "end": v(-1.27, -48.34) * mm});
            skLineSegment(sketch, "E3627", {"start": v(-1.27, -48.34) * mm, "end": v(-1.17, -48.46) * mm});
            skLineSegment(sketch, "E3628", {"start": v(-1.17, -48.46) * mm, "end": v(-1.03, -48.56) * mm});
            skLineSegment(sketch, "E3629", {"start": v(-1.03, -48.56) * mm, "end": v(-0.88, -48.61) * mm});
            skLineSegment(sketch, "E3630", {"start": v(-0.88, -48.61) * mm, "end": v(-0.71, -48.62) * mm});
            skLineSegment(sketch, "E3631", {"start": v(-0.71, -48.62) * mm, "end": v(-0.55, -48.6) * mm});
            skLineSegment(sketch, "E3632", {"start": v(-0.55, -48.6) * mm, "end": v(-0.4, -48.52) * mm});
            skLineSegment(sketch, "E3633", {"start": v(-0.4, -48.52) * mm, "end": v(-0.28, -48.42) * mm});
            skLineSegment(sketch, "E3634", {"start": v(-0.28, -48.42) * mm, "end": v(-0.19, -48.28) * mm});
            skLineSegment(sketch, "E3635", {"start": v(-0.19, -48.28) * mm, "end": v(-0.13, -48.13) * mm});
            skLineSegment(sketch, "E3636", {"start": v(-0.13, -48.13) * mm, "end": v(-0.12, -47.97) * mm});
            skLineSegment(sketch, "E3637", {"start": v(-0.12, -47.97) * mm, "end": v(-0.12, -47.81) * mm});
            skLineSegment(sketch, "E3638", {"start": v(-0.12, -47.81) * mm, "end": v(-0.13, -47.66) * mm});
            skLineSegment(sketch, "E3639", {"start": v(-0.13, -47.66) * mm, "end": v(-0.13, -47.5) * mm});
            skLineSegment(sketch, "E3640", {"start": v(-0.13, -47.5) * mm, "end": v(-0.13, -47.34) * mm});
            skLineSegment(sketch, "E3641", {"start": v(-0.13, -47.34) * mm, "end": v(-0.13, -47.18) * mm});
            skLineSegment(sketch, "E3642", {"start": v(-0.13, -47.18) * mm, "end": v(-0.13, -47.02) * mm});
            skLineSegment(sketch, "E3643", {"start": v(-0.13, -47.02) * mm, "end": v(-0.14, -46.87) * mm});
            skLineSegment(sketch, "E3644", {"start": v(-0.14, -46.87) * mm, "end": v(-0.14, -46.7) * mm});
            skLineSegment(sketch, "E3645", {"start": v(-0.14, -46.7) * mm, "end": v(-0.14, -46.55) * mm});
            skLineSegment(sketch, "E3646", {"start": v(-0.14, -46.55) * mm, "end": v(-0.14, -46.39) * mm});
            skLineSegment(sketch, "E3647", {"start": v(-0.14, -46.39) * mm, "end": v(-0.14, -46.23) * mm});
            skLineSegment(sketch, "E3648", {"start": v(-0.14, -46.23) * mm, "end": v(-0.15, -46.07) * mm});
            skLineSegment(sketch, "E3649", {"start": v(-0.15, -46.07) * mm, "end": v(-0.15, -45.96) * mm});
            skLineSegment(sketch, "E3650", {"start": v(-0.15, -45.96) * mm, "end": v(0, -45.95) * mm});
            skLineSegment(sketch, "E3651", {"start": v(0, -45.95) * mm, "end": v(0.17, -45.95) * mm});
            skLineSegment(sketch, "E3652", {"start": v(0.17, -45.95) * mm, "end": v(0.32, -45.94) * mm});
            skLineSegment(sketch, "E3653", {"start": v(0.32, -45.94) * mm, "end": v(0.48, -45.94) * mm});
            skLineSegment(sketch, "E3654", {"start": v(0.48, -45.94) * mm, "end": v(0.64, -45.93) * mm});
            skLineSegment(sketch, "E3655", {"start": v(0.64, -45.93) * mm, "end": v(0.8, -45.92) * mm});
            skLineSegment(sketch, "E3656", {"start": v(0.8, -45.92) * mm, "end": v(0.95, -45.92) * mm});
            skLineSegment(sketch, "E3657", {"start": v(0.95, -45.92) * mm, "end": v(1.1, -45.91) * mm});
            skLineSegment(sketch, "E3658", {"start": v(1.1, -45.91) * mm, "end": v(1.27, -45.9) * mm});
            skLineSegment(sketch, "E3659", {"start": v(1.27, -45.9) * mm, "end": v(1.42, -45.9) * mm});
            skLineSegment(sketch, "E3660", {"start": v(1.42, -45.9) * mm, "end": v(1.58, -45.9) * mm});
            skLineSegment(sketch, "E3661", {"start": v(1.58, -45.9) * mm, "end": v(1.66, -45.9) * mm});
            skLineSegment(sketch, "E3662", {"start": v(1.66, -45.9) * mm, "end": v(1.67, -46.05) * mm});
            skLineSegment(sketch, "E3663", {"start": v(1.67, -46.05) * mm, "end": v(1.68, -46.21) * mm});
            skLineSegment(sketch, "E3664", {"start": v(1.68, -46.21) * mm, "end": v(1.69, -46.37) * mm});
            skLineSegment(sketch, "E3665", {"start": v(1.69, -46.37) * mm, "end": v(1.7, -46.53) * mm});
            skLineSegment(sketch, "E3666", {"start": v(1.7, -46.53) * mm, "end": v(1.7, -46.69) * mm});
            skLineSegment(sketch, "E3667", {"start": v(1.7, -46.69) * mm, "end": v(1.71, -46.85) * mm});
            skLineSegment(sketch, "E3668", {"start": v(1.71, -46.85) * mm, "end": v(1.72, -47) * mm});
            skLineSegment(sketch, "E3669", {"start": v(1.72, -47) * mm, "end": v(1.73, -47.16) * mm});
            skLineSegment(sketch, "E3670", {"start": v(1.73, -47.16) * mm, "end": v(1.74, -47.32) * mm});
            skLineSegment(sketch, "E3671", {"start": v(1.74, -47.32) * mm, "end": v(1.75, -47.48) * mm});
            skLineSegment(sketch, "E3672", {"start": v(1.75, -47.48) * mm, "end": v(1.75, -47.64) * mm});
            skLineSegment(sketch, "E3673", {"start": v(1.75, -47.64) * mm, "end": v(1.76, -47.8) * mm});
            skLineSegment(sketch, "E3674", {"start": v(1.76, -47.8) * mm, "end": v(1.77, -47.97) * mm});
            skLineSegment(sketch, "E3675", {"start": v(1.77, -47.97) * mm, "end": v(1.81, -48.13) * mm});
            skLineSegment(sketch, "E3676", {"start": v(1.81, -48.13) * mm, "end": v(1.9, -48.27) * mm});
            skLineSegment(sketch, "E3677", {"start": v(1.9, -48.27) * mm, "end": v(2, -48.39) * mm});
            skLineSegment(sketch, "E3678", {"start": v(2, -48.39) * mm, "end": v(2.15, -48.47) * mm});
            skLineSegment(sketch, "E3679", {"start": v(2.15, -48.47) * mm, "end": v(2.3, -48.52) * mm});
            skLineSegment(sketch, "E3680", {"start": v(2.3, -48.52) * mm, "end": v(2.47, -48.52) * mm});
            skLineSegment(sketch, "E3681", {"start": v(2.47, -48.52) * mm, "end": v(2.63, -48.48) * mm});
            skLineSegment(sketch, "E3682", {"start": v(2.63, -48.48) * mm, "end": v(2.77, -48.4) * mm});
            skLineSegment(sketch, "E3683", {"start": v(2.77, -48.4) * mm, "end": v(2.89, -48.28) * mm});
            skLineSegment(sketch, "E3684", {"start": v(2.89, -48.28) * mm, "end": v(2.97, -48.14) * mm});
            skLineSegment(sketch, "E3685", {"start": v(2.97, -48.14) * mm, "end": v(3.01, -47.98) * mm});
            skLineSegment(sketch, "E3686", {"start": v(3.01, -47.98) * mm, "end": v(3.01, -47.83) * mm});
            skLineSegment(sketch, "E3687", {"start": v(3.01, -47.83) * mm, "end": v(3, -47.67) * mm});
            skLineSegment(sketch, "E3688", {"start": v(3, -47.67) * mm, "end": v(3, -47.51) * mm});
            skLineSegment(sketch, "E3689", {"start": v(3, -47.51) * mm, "end": v(2.98, -47.36) * mm});
            skLineSegment(sketch, "E3690", {"start": v(2.98, -47.36) * mm, "end": v(2.97, -47.2) * mm});
            skLineSegment(sketch, "E3691", {"start": v(2.97, -47.2) * mm, "end": v(2.95, -47.04) * mm});
            skLineSegment(sketch, "E3692", {"start": v(2.95, -47.04) * mm, "end": v(2.94, -46.88) * mm});
            skLineSegment(sketch, "E3693", {"start": v(2.94, -46.88) * mm, "end": v(2.93, -46.73) * mm});
            skLineSegment(sketch, "E3694", {"start": v(2.93, -46.73) * mm, "end": v(2.92, -46.56) * mm});
            skLineSegment(sketch, "E3695", {"start": v(2.92, -46.56) * mm, "end": v(2.9, -46.4) * mm});
            skLineSegment(sketch, "E3696", {"start": v(2.9, -46.4) * mm, "end": v(2.9, -46.25) * mm});
            skLineSegment(sketch, "E3697", {"start": v(2.9, -46.25) * mm, "end": v(2.88, -46.09) * mm});
            skLineSegment(sketch, "E3698", {"start": v(2.88, -46.09) * mm, "end": v(2.87, -45.93) * mm});
            skLineSegment(sketch, "E3699", {"start": v(2.87, -45.93) * mm, "end": v(2.86, -45.82) * mm});
            skLineSegment(sketch, "E3700", {"start": v(2.86, -45.82) * mm, "end": v(3.01, -45.8) * mm});
            skLineSegment(sketch, "E3701", {"start": v(3.01, -45.8) * mm, "end": v(3.17, -45.79) * mm});
            skLineSegment(sketch, "E3702", {"start": v(3.17, -45.79) * mm, "end": v(3.33, -45.77) * mm});
            skLineSegment(sketch, "E3703", {"start": v(3.33, -45.77) * mm, "end": v(3.48, -45.76) * mm});
            skLineSegment(sketch, "E3704", {"start": v(3.48, -45.76) * mm, "end": v(3.64, -45.74) * mm});
            skLineSegment(sketch, "E3705", {"start": v(3.64, -45.74) * mm, "end": v(3.8, -45.73) * mm});
            skLineSegment(sketch, "E3706", {"start": v(3.8, -45.73) * mm, "end": v(3.95, -45.71) * mm});
            skLineSegment(sketch, "E3707", {"start": v(3.95, -45.71) * mm, "end": v(4.1, -45.7) * mm});
            skLineSegment(sketch, "E3708", {"start": v(4.1, -45.7) * mm, "end": v(4.27, -45.68) * mm});
            skLineSegment(sketch, "E3709", {"start": v(4.27, -45.68) * mm, "end": v(4.42, -45.66) * mm});
            skLineSegment(sketch, "E3710", {"start": v(4.42, -45.66) * mm, "end": v(4.58, -45.65) * mm});
            skLineSegment(sketch, "E3711", {"start": v(4.58, -45.65) * mm, "end": v(4.66, -45.64) * mm});
            skLineSegment(sketch, "E3712", {"start": v(4.66, -45.64) * mm, "end": v(4.68, -45.8) * mm});
            skLineSegment(sketch, "E3713", {"start": v(4.68, -45.8) * mm, "end": v(4.7, -45.95) * mm});
            skLineSegment(sketch, "E3714", {"start": v(4.7, -45.95) * mm, "end": v(4.71, -46.11) * mm});
            skLineSegment(sketch, "E3715", {"start": v(4.71, -46.11) * mm, "end": v(4.73, -46.27) * mm});
            skLineSegment(sketch, "E3716", {"start": v(4.73, -46.27) * mm, "end": v(4.75, -46.43) * mm});
            skLineSegment(sketch, "E3717", {"start": v(4.75, -46.43) * mm, "end": v(4.77, -46.59) * mm});
            skLineSegment(sketch, "E3718", {"start": v(4.77, -46.59) * mm, "end": v(4.79, -46.74) * mm});
            skLineSegment(sketch, "E3719", {"start": v(4.79, -46.74) * mm, "end": v(4.8, -46.9) * mm});
            skLineSegment(sketch, "E3720", {"start": v(4.8, -46.9) * mm, "end": v(4.83, -47.06) * mm});
            skLineSegment(sketch, "E3721", {"start": v(4.83, -47.06) * mm, "end": v(4.84, -47.22) * mm});
            skLineSegment(sketch, "E3722", {"start": v(4.84, -47.22) * mm, "end": v(4.86, -47.37) * mm});
            skLineSegment(sketch, "E3723", {"start": v(4.86, -47.37) * mm, "end": v(4.88, -47.53) * mm});
            skLineSegment(sketch, "E3724", {"start": v(4.88, -47.53) * mm, "end": v(4.9, -47.7) * mm});
            skLineSegment(sketch, "E3725", {"start": v(4.9, -47.7) * mm, "end": v(4.95, -47.86) * mm});
            skLineSegment(sketch, "E3726", {"start": v(4.95, -47.86) * mm, "end": v(5.04, -48) * mm});
            skLineSegment(sketch, "E3727", {"start": v(5.04, -48) * mm, "end": v(5.16, -48.1) * mm});
            skLineSegment(sketch, "E3728", {"start": v(5.16, -48.1) * mm, "end": v(5.3, -48.18) * mm});
            skLineSegment(sketch, "E3729", {"start": v(5.3, -48.18) * mm, "end": v(5.47, -48.21) * mm});
            skLineSegment(sketch, "E3730", {"start": v(5.47, -48.21) * mm, "end": v(5.63, -48.2) * mm});
            skLineSegment(sketch, "E3731", {"start": v(5.63, -48.2) * mm, "end": v(5.79, -48.15) * mm});
            skLineSegment(sketch, "E3732", {"start": v(5.79, -48.15) * mm, "end": v(5.93, -48.06) * mm});
            skLineSegment(sketch, "E3733", {"start": v(5.93, -48.06) * mm, "end": v(6.04, -47.94) * mm});
            skLineSegment(sketch, "E3734", {"start": v(6.04, -47.94) * mm, "end": v(6.1, -47.8) * mm});
            skLineSegment(sketch, "E3735", {"start": v(6.1, -47.8) * mm, "end": v(6.14, -47.64) * mm});
            skLineSegment(sketch, "E3736", {"start": v(6.14, -47.64) * mm, "end": v(6.13, -47.48) * mm});
            skLineSegment(sketch, "E3737", {"start": v(6.13, -47.48) * mm, "end": v(6.11, -47.32) * mm});
            skLineSegment(sketch, "E3738", {"start": v(6.11, -47.32) * mm, "end": v(6.09, -47.17) * mm});
            skLineSegment(sketch, "E3739", {"start": v(6.09, -47.17) * mm, "end": v(6.07, -47.01) * mm});
            skLineSegment(sketch, "E3740", {"start": v(6.07, -47.01) * mm, "end": v(6.04, -46.86) * mm});
            skLineSegment(sketch, "E3741", {"start": v(6.04, -46.86) * mm, "end": v(6.02, -46.7) * mm});
            skLineSegment(sketch, "E3742", {"start": v(6.02, -46.7) * mm, "end": v(6, -46.54) * mm});
            skLineSegment(sketch, "E3743", {"start": v(6, -46.54) * mm, "end": v(5.98, -46.38) * mm});
            skLineSegment(sketch, "E3744", {"start": v(5.98, -46.38) * mm, "end": v(5.95, -46.23) * mm});
            skLineSegment(sketch, "E3745", {"start": v(5.95, -46.23) * mm, "end": v(5.93, -46.07) * mm});
            skLineSegment(sketch, "E3746", {"start": v(5.93, -46.07) * mm, "end": v(5.9, -45.91) * mm});
            skLineSegment(sketch, "E3747", {"start": v(5.9, -45.91) * mm, "end": v(5.88, -45.75) * mm});
            skLineSegment(sketch, "E3748", {"start": v(5.88, -45.75) * mm, "end": v(5.86, -45.6) * mm});
            skLineSegment(sketch, "E3749", {"start": v(5.86, -45.6) * mm, "end": v(5.85, -45.48) * mm});
            skLineSegment(sketch, "E3750", {"start": v(5.85, -45.48) * mm, "end": v(6, -45.46) * mm});
            skLineSegment(sketch, "E3751", {"start": v(6, -45.46) * mm, "end": v(6.16, -45.43) * mm});
            skLineSegment(sketch, "E3752", {"start": v(6.16, -45.43) * mm, "end": v(6.31, -45.4) * mm});
            skLineSegment(sketch, "E3753", {"start": v(6.31, -45.4) * mm, "end": v(6.47, -45.38) * mm});
            skLineSegment(sketch, "E3754", {"start": v(6.47, -45.38) * mm, "end": v(6.62, -45.36) * mm});
            skLineSegment(sketch, "E3755", {"start": v(6.62, -45.36) * mm, "end": v(6.78, -45.33) * mm});
            skLineSegment(sketch, "E3756", {"start": v(6.78, -45.33) * mm, "end": v(6.93, -45.3) * mm});
            skLineSegment(sketch, "E3757", {"start": v(6.93, -45.3) * mm, "end": v(7.09, -45.28) * mm});
            skLineSegment(sketch, "E3758", {"start": v(7.09, -45.28) * mm, "end": v(7.24, -45.25) * mm});
            skLineSegment(sketch, "E3759", {"start": v(7.24, -45.25) * mm, "end": v(7.4, -45.23) * mm});
            skLineSegment(sketch, "E3760", {"start": v(7.4, -45.23) * mm, "end": v(7.55, -45.2) * mm});
            skLineSegment(sketch, "E3761", {"start": v(7.55, -45.2) * mm, "end": v(7.63, -45.19) * mm});
            skLineSegment(sketch, "E3762", {"start": v(7.63, -45.19) * mm, "end": v(7.66, -45.34) * mm});
            skLineSegment(sketch, "E3763", {"start": v(7.66, -45.34) * mm, "end": v(7.69, -45.5) * mm});
            skLineSegment(sketch, "E3764", {"start": v(7.69, -45.5) * mm, "end": v(7.72, -45.66) * mm});
            skLineSegment(sketch, "E3765", {"start": v(7.72, -45.66) * mm, "end": v(7.75, -45.81) * mm});
            skLineSegment(sketch, "E3766", {"start": v(7.75, -45.81) * mm, "end": v(7.78, -45.97) * mm});
            skLineSegment(sketch, "E3767", {"start": v(7.78, -45.97) * mm, "end": v(7.8, -46.13) * mm});
            skLineSegment(sketch, "E3768", {"start": v(7.8, -46.13) * mm, "end": v(7.83, -46.28) * mm});
            skLineSegment(sketch, "E3769", {"start": v(7.83, -46.28) * mm, "end": v(7.86, -46.44) * mm});
            skLineSegment(sketch, "E3770", {"start": v(7.86, -46.44) * mm, "end": v(7.9, -46.6) * mm});
            skLineSegment(sketch, "E3771", {"start": v(7.9, -46.6) * mm, "end": v(7.92, -46.75) * mm});
            skLineSegment(sketch, "E3772", {"start": v(7.92, -46.75) * mm, "end": v(7.95, -46.9) * mm});
            skLineSegment(sketch, "E3773", {"start": v(7.95, -46.9) * mm, "end": v(7.98, -47.06) * mm});
            skLineSegment(sketch, "E3774", {"start": v(7.98, -47.06) * mm, "end": v(8.01, -47.23) * mm});
            skLineSegment(sketch, "E3775", {"start": v(8.01, -47.23) * mm, "end": v(8.07, -47.38) * mm});
            skLineSegment(sketch, "E3776", {"start": v(8.07, -47.38) * mm, "end": v(8.17, -47.51) * mm});
            skLineSegment(sketch, "E3777", {"start": v(8.17, -47.51) * mm, "end": v(8.3, -47.61) * mm});
            skLineSegment(sketch, "E3778", {"start": v(8.3, -47.61) * mm, "end": v(8.45, -47.68) * mm});
            skLineSegment(sketch, "E3779", {"start": v(8.45, -47.68) * mm, "end": v(8.6, -47.7) * mm});
            skLineSegment(sketch, "E3780", {"start": v(8.6, -47.7) * mm, "end": v(8.77, -47.68) * mm});
            skLineSegment(sketch, "E3781", {"start": v(8.77, -47.68) * mm, "end": v(8.92, -47.62) * mm});
            skLineSegment(sketch, "E3782", {"start": v(8.92, -47.62) * mm, "end": v(9.06, -47.52) * mm});
            skLineSegment(sketch, "E3783", {"start": v(9.06, -47.52) * mm, "end": v(9.16, -47.4) * mm});
            skLineSegment(sketch, "E3784", {"start": v(9.16, -47.4) * mm, "end": v(9.22, -47.25) * mm});
            skLineSegment(sketch, "E3785", {"start": v(9.22, -47.25) * mm, "end": v(9.24, -47.08) * mm});
            skLineSegment(sketch, "E3786", {"start": v(9.24, -47.08) * mm, "end": v(9.22, -46.93) * mm});
            skLineSegment(sketch, "E3787", {"start": v(9.22, -46.93) * mm, "end": v(9.2, -46.77) * mm});
            skLineSegment(sketch, "E3788", {"start": v(9.2, -46.77) * mm, "end": v(9.16, -46.62) * mm});
            skLineSegment(sketch, "E3789", {"start": v(9.16, -46.62) * mm, "end": v(9.13, -46.47) * mm});
            skLineSegment(sketch, "E3790", {"start": v(9.13, -46.47) * mm, "end": v(9.1, -46.31) * mm});
            skLineSegment(sketch, "E3791", {"start": v(9.1, -46.31) * mm, "end": v(9.06, -46.15) * mm});
            skLineSegment(sketch, "E3792", {"start": v(9.06, -46.15) * mm, "end": v(9.03, -46) * mm});
            skLineSegment(sketch, "E3793", {"start": v(9.03, -46) * mm, "end": v(9, -45.85) * mm});
            skLineSegment(sketch, "E3794", {"start": v(9, -45.85) * mm, "end": v(8.96, -45.69) * mm});
            skLineSegment(sketch, "E3795", {"start": v(8.96, -45.69) * mm, "end": v(8.93, -45.53) * mm});
            skLineSegment(sketch, "E3796", {"start": v(8.93, -45.53) * mm, "end": v(8.9, -45.38) * mm});
            skLineSegment(sketch, "E3797", {"start": v(8.9, -45.38) * mm, "end": v(8.86, -45.22) * mm});
            skLineSegment(sketch, "E3798", {"start": v(8.86, -45.22) * mm, "end": v(8.83, -45.07) * mm});
            skLineSegment(sketch, "E3799", {"start": v(8.83, -45.07) * mm, "end": v(8.8, -44.96) * mm});
            skLineSegment(sketch, "E3800", {"start": v(8.8, -44.96) * mm, "end": v(8.96, -44.92) * mm});
            skLineSegment(sketch, "E3801", {"start": v(8.96, -44.92) * mm, "end": v(9.11, -44.88) * mm});
            skLineSegment(sketch, "E3802", {"start": v(9.11, -44.88) * mm, "end": v(9.27, -44.85) * mm});
            skLineSegment(sketch, "E3803", {"start": v(9.27, -44.85) * mm, "end": v(9.42, -44.81) * mm});
            skLineSegment(sketch, "E3804", {"start": v(9.42, -44.81) * mm, "end": v(9.57, -44.78) * mm});
            skLineSegment(sketch, "E3805", {"start": v(9.57, -44.78) * mm, "end": v(9.73, -44.74) * mm});
            skLineSegment(sketch, "E3806", {"start": v(9.73, -44.74) * mm, "end": v(9.88, -44.7) * mm});
            skLineSegment(sketch, "E3807", {"start": v(9.88, -44.7) * mm, "end": v(10.03, -44.67) * mm});
            skLineSegment(sketch, "E3808", {"start": v(10.03, -44.67) * mm, "end": v(10.18, -44.63) * mm});
            skLineSegment(sketch, "E3809", {"start": v(10.18, -44.63) * mm, "end": v(10.34, -44.6) * mm});
            skLineSegment(sketch, "E3810", {"start": v(10.34, -44.6) * mm, "end": v(10.5, -44.56) * mm});
            skLineSegment(sketch, "E3811", {"start": v(10.5, -44.56) * mm, "end": v(10.57, -44.54) * mm});
            skLineSegment(sketch, "E3812", {"start": v(10.57, -44.54) * mm, "end": v(10.6, -44.7) * mm});
            skLineSegment(sketch, "E3813", {"start": v(10.6, -44.7) * mm, "end": v(10.65, -44.85) * mm});
            skLineSegment(sketch, "E3814", {"start": v(10.65, -44.85) * mm, "end": v(10.69, -45) * mm});
            skLineSegment(sketch, "E3815", {"start": v(10.69, -45) * mm, "end": v(10.73, -45.16) * mm});
            skLineSegment(sketch, "E3816", {"start": v(10.73, -45.16) * mm, "end": v(10.76, -45.31) * mm});
            skLineSegment(sketch, "E3817", {"start": v(10.76, -45.31) * mm, "end": v(10.8, -45.47) * mm});
            skLineSegment(sketch, "E3818", {"start": v(10.8, -45.47) * mm, "end": v(10.84, -45.62) * mm});
            skLineSegment(sketch, "E3819", {"start": v(10.84, -45.62) * mm, "end": v(10.88, -45.77) * mm});
            skLineSegment(sketch, "E3820", {"start": v(10.88, -45.77) * mm, "end": v(10.92, -45.93) * mm});
            skLineSegment(sketch, "E3821", {"start": v(10.92, -45.93) * mm, "end": v(10.96, -46.08) * mm});
            skLineSegment(sketch, "E3822", {"start": v(10.96, -46.08) * mm, "end": v(11, -46.23) * mm});
            skLineSegment(sketch, "E3823", {"start": v(11, -46.23) * mm, "end": v(11.04, -46.4) * mm});
            skLineSegment(sketch, "E3824", {"start": v(11.04, -46.4) * mm, "end": v(11.08, -46.55) * mm});
            skLineSegment(sketch, "E3825", {"start": v(11.08, -46.55) * mm, "end": v(11.15, -46.7) * mm});
            skLineSegment(sketch, "E3826", {"start": v(11.15, -46.7) * mm, "end": v(11.26, -46.83) * mm});
            skLineSegment(sketch, "E3827", {"start": v(11.26, -46.83) * mm, "end": v(11.4, -46.92) * mm});
            skLineSegment(sketch, "E3828", {"start": v(11.4, -46.92) * mm, "end": v(11.55, -46.98) * mm});
            skLineSegment(sketch, "E3829", {"start": v(11.55, -46.98) * mm, "end": v(11.7, -46.99) * mm});
            skLineSegment(sketch, "E3830", {"start": v(11.7, -46.99) * mm, "end": v(11.87, -46.96) * mm});
            skLineSegment(sketch, "E3831", {"start": v(11.87, -46.96) * mm, "end": v(12.02, -46.89) * mm});
            skLineSegment(sketch, "E3832", {"start": v(12.02, -46.89) * mm, "end": v(12.14, -46.78) * mm});
            skLineSegment(sketch, "E3833", {"start": v(12.14, -46.78) * mm, "end": v(12.24, -46.65) * mm});
            skLineSegment(sketch, "E3834", {"start": v(12.24, -46.65) * mm, "end": v(12.29, -46.5) * mm});
            skLineSegment(sketch, "E3835", {"start": v(12.29, -46.5) * mm, "end": v(12.3, -46.33) * mm});
            skLineSegment(sketch, "E3836", {"start": v(12.3, -46.33) * mm, "end": v(12.27, -46.17) * mm});
            skLineSegment(sketch, "E3837", {"start": v(12.27, -46.17) * mm, "end": v(12.23, -46.02) * mm});
            skLineSegment(sketch, "E3838", {"start": v(12.23, -46.02) * mm, "end": v(12.19, -45.87) * mm});
            skLineSegment(sketch, "E3839", {"start": v(12.19, -45.87) * mm, "end": v(12.14, -45.72) * mm});
            skLineSegment(sketch, "E3840", {"start": v(12.14, -45.72) * mm, "end": v(12.1, -45.57) * mm});
            skLineSegment(sketch, "E3841", {"start": v(12.1, -45.57) * mm, "end": v(12.06, -45.41) * mm});
            skLineSegment(sketch, "E3842", {"start": v(12.06, -45.41) * mm, "end": v(12.02, -45.26) * mm});
            skLineSegment(sketch, "E3843", {"start": v(12.02, -45.26) * mm, "end": v(11.97, -45.11) * mm});
            skLineSegment(sketch, "E3844", {"start": v(11.97, -45.11) * mm, "end": v(11.93, -44.96) * mm});
            skLineSegment(sketch, "E3845", {"start": v(11.93, -44.96) * mm, "end": v(11.89, -44.8) * mm});
            skLineSegment(sketch, "E3846", {"start": v(11.89, -44.8) * mm, "end": v(11.84, -44.65) * mm});
            skLineSegment(sketch, "E3847", {"start": v(11.84, -44.65) * mm, "end": v(11.8, -44.5) * mm});
            skLineSegment(sketch, "E3848", {"start": v(11.8, -44.5) * mm, "end": v(11.76, -44.35) * mm});
            skLineSegment(sketch, "E3849", {"start": v(11.76, -44.35) * mm, "end": v(11.73, -44.23) * mm});
            skLineSegment(sketch, "E3850", {"start": v(11.73, -44.23) * mm, "end": v(11.88, -44.19) * mm});
            skLineSegment(sketch, "E3851", {"start": v(11.88, -44.19) * mm, "end": v(12.03, -44.14) * mm});
            skLineSegment(sketch, "E3852", {"start": v(12.03, -44.14) * mm, "end": v(12.18, -44.1) * mm});
            skLineSegment(sketch, "E3853", {"start": v(12.18, -44.1) * mm, "end": v(12.33, -44.05) * mm});
            skLineSegment(sketch, "E3854", {"start": v(12.33, -44.05) * mm, "end": v(12.48, -44) * mm});
            skLineSegment(sketch, "E3855", {"start": v(12.48, -44) * mm, "end": v(12.63, -43.96) * mm});
            skLineSegment(sketch, "E3856", {"start": v(12.63, -43.96) * mm, "end": v(12.78, -43.92) * mm});
            skLineSegment(sketch, "E3857", {"start": v(12.78, -43.92) * mm, "end": v(12.93, -43.87) * mm});
            skLineSegment(sketch, "E3858", {"start": v(12.93, -43.87) * mm, "end": v(13.08, -43.82) * mm});
            skLineSegment(sketch, "E3859", {"start": v(13.08, -43.82) * mm, "end": v(13.23, -43.78) * mm});
            skLineSegment(sketch, "E3860", {"start": v(13.23, -43.78) * mm, "end": v(13.38, -43.73) * mm});
            skLineSegment(sketch, "E3861", {"start": v(13.38, -43.73) * mm, "end": v(13.46, -43.7) * mm});
            skLineSegment(sketch, "E3862", {"start": v(13.46, -43.7) * mm, "end": v(13.5, -43.86) * mm});
            skLineSegment(sketch, "E3863", {"start": v(13.5, -43.86) * mm, "end": v(13.56, -44) * mm});
            skLineSegment(sketch, "E3864", {"start": v(13.56, -44) * mm, "end": v(13.6, -44.16) * mm});
            skLineSegment(sketch, "E3865", {"start": v(13.6, -44.16) * mm, "end": v(13.65, -44.31) * mm});
            skLineSegment(sketch, "E3866", {"start": v(13.65, -44.31) * mm, "end": v(13.7, -44.46) * mm});
            skLineSegment(sketch, "E3867", {"start": v(13.7, -44.46) * mm, "end": v(13.75, -44.62) * mm});
            skLineSegment(sketch, "E3868", {"start": v(13.75, -44.62) * mm, "end": v(13.8, -44.76) * mm});
            skLineSegment(sketch, "E3869", {"start": v(13.8, -44.76) * mm, "end": v(13.85, -44.91) * mm});
            skLineSegment(sketch, "E3870", {"start": v(13.85, -44.91) * mm, "end": v(13.9, -45.07) * mm});
            skLineSegment(sketch, "E3871", {"start": v(13.9, -45.07) * mm, "end": v(13.95, -45.22) * mm});
            skLineSegment(sketch, "E3872", {"start": v(13.95, -45.22) * mm, "end": v(14, -45.37) * mm});
            skLineSegment(sketch, "E3873", {"start": v(14, -45.37) * mm, "end": v(14.05, -45.52) * mm});
            skLineSegment(sketch, "E3874", {"start": v(14.05, -45.52) * mm, "end": v(14.1, -45.68) * mm});
            skLineSegment(sketch, "E3875", {"start": v(14.1, -45.68) * mm, "end": v(14.18, -45.82) * mm});
            skLineSegment(sketch, "E3876", {"start": v(14.18, -45.82) * mm, "end": v(14.3, -45.94) * mm});
            skLineSegment(sketch, "E3877", {"start": v(14.3, -45.94) * mm, "end": v(14.43, -46.03) * mm});
            skLineSegment(sketch, "E3878", {"start": v(14.43, -46.03) * mm, "end": v(14.6, -46.07) * mm});
            skLineSegment(sketch, "E3879", {"start": v(14.6, -46.07) * mm, "end": v(14.76, -46.07) * mm});
            skLineSegment(sketch, "E3880", {"start": v(14.76, -46.07) * mm, "end": v(14.91, -46.03) * mm});
            skLineSegment(sketch, "E3881", {"start": v(14.91, -46.03) * mm, "end": v(15.06, -45.95) * mm});
            skLineSegment(sketch, "E3882", {"start": v(15.06, -45.95) * mm, "end": v(15.17, -45.84) * mm});
            skLineSegment(sketch, "E3883", {"start": v(15.17, -45.84) * mm, "end": v(15.26, -45.7) * mm});
            skLineSegment(sketch, "E3884", {"start": v(15.26, -45.7) * mm, "end": v(15.3, -45.54) * mm});
            skLineSegment(sketch, "E3885", {"start": v(15.3, -45.54) * mm, "end": v(15.3, -45.38) * mm});
            skLineSegment(sketch, "E3886", {"start": v(15.3, -45.38) * mm, "end": v(15.26, -45.22) * mm});
            skLineSegment(sketch, "E3887", {"start": v(15.26, -45.22) * mm, "end": v(15.21, -45.08) * mm});
            skLineSegment(sketch, "E3888", {"start": v(15.21, -45.08) * mm, "end": v(15.16, -44.93) * mm});
            skLineSegment(sketch, "E3889", {"start": v(15.16, -44.93) * mm, "end": v(15.1, -44.78) * mm});
            skLineSegment(sketch, "E3890", {"start": v(15.1, -44.78) * mm, "end": v(15.06, -44.63) * mm});
            skLineSegment(sketch, "E3891", {"start": v(15.06, -44.63) * mm, "end": v(15, -44.48) * mm});
            skLineSegment(sketch, "E3892", {"start": v(15, -44.48) * mm, "end": v(14.95, -44.33) * mm});
            skLineSegment(sketch, "E3893", {"start": v(14.95, -44.33) * mm, "end": v(14.9, -44.18) * mm});
            skLineSegment(sketch, "E3894", {"start": v(14.9, -44.18) * mm, "end": v(14.84, -44.03) * mm});
            skLineSegment(sketch, "E3895", {"start": v(14.84, -44.03) * mm, "end": v(14.79, -43.88) * mm});
            skLineSegment(sketch, "E3896", {"start": v(14.79, -43.88) * mm, "end": v(14.74, -43.73) * mm});
            skLineSegment(sketch, "E3897", {"start": v(14.74, -43.73) * mm, "end": v(14.68, -43.58) * mm});
            skLineSegment(sketch, "E3898", {"start": v(14.68, -43.58) * mm, "end": v(14.63, -43.43) * mm});
            skLineSegment(sketch, "E3899", {"start": v(14.63, -43.43) * mm, "end": v(14.6, -43.32) * mm});
            skLineSegment(sketch, "E3900", {"start": v(14.6, -43.32) * mm, "end": v(14.74, -43.27) * mm});
            skLineSegment(sketch, "E3901", {"start": v(14.74, -43.27) * mm, "end": v(14.89, -43.21) * mm});
            skLineSegment(sketch, "E3902", {"start": v(14.89, -43.21) * mm, "end": v(15.03, -43.16) * mm});
            skLineSegment(sketch, "E3903", {"start": v(15.03, -43.16) * mm, "end": v(15.18, -43.1) * mm});
            skLineSegment(sketch, "E3904", {"start": v(15.18, -43.1) * mm, "end": v(15.33, -43.05) * mm});
            skLineSegment(sketch, "E3905", {"start": v(15.33, -43.05) * mm, "end": v(15.48, -43) * mm});
            skLineSegment(sketch, "E3906", {"start": v(15.48, -43) * mm, "end": v(15.62, -42.94) * mm});
            skLineSegment(sketch, "E3907", {"start": v(15.62, -42.94) * mm, "end": v(15.77, -42.88) * mm});
            skLineSegment(sketch, "E3908", {"start": v(15.77, -42.88) * mm, "end": v(15.92, -42.83) * mm});
            skLineSegment(sketch, "E3909", {"start": v(15.92, -42.83) * mm, "end": v(16.06, -42.77) * mm});
            skLineSegment(sketch, "E3910", {"start": v(16.06, -42.77) * mm, "end": v(16.21, -42.72) * mm});
            skLineSegment(sketch, "E3911", {"start": v(16.21, -42.72) * mm, "end": v(16.29, -42.69) * mm});
            skLineSegment(sketch, "E3912", {"start": v(16.29, -42.69) * mm, "end": v(16.35, -42.83) * mm});
            skLineSegment(sketch, "E3913", {"start": v(16.35, -42.83) * mm, "end": v(16.4, -42.98) * mm});
            skLineSegment(sketch, "E3914", {"start": v(16.4, -42.98) * mm, "end": v(16.46, -43.13) * mm});
            skLineSegment(sketch, "E3915", {"start": v(16.46, -43.13) * mm, "end": v(16.52, -43.28) * mm});
            skLineSegment(sketch, "E3916", {"start": v(16.52, -43.28) * mm, "end": v(16.58, -43.42) * mm});
            skLineSegment(sketch, "E3917", {"start": v(16.58, -43.42) * mm, "end": v(16.64, -43.57) * mm});
            skLineSegment(sketch, "E3918", {"start": v(16.64, -43.57) * mm, "end": v(16.7, -43.72) * mm});
            skLineSegment(sketch, "E3919", {"start": v(16.7, -43.72) * mm, "end": v(16.76, -43.86) * mm});
            skLineSegment(sketch, "E3920", {"start": v(16.76, -43.86) * mm, "end": v(16.82, -44.01) * mm});
            skLineSegment(sketch, "E3921", {"start": v(16.82, -44.01) * mm, "end": v(16.87, -44.16) * mm});
            skLineSegment(sketch, "E3922", {"start": v(16.87, -44.16) * mm, "end": v(16.93, -44.3) * mm});
            skLineSegment(sketch, "E3923", {"start": v(16.93, -44.3) * mm, "end": v(17, -44.46) * mm});
            skLineSegment(sketch, "E3924", {"start": v(17, -44.46) * mm, "end": v(17.06, -44.61) * mm});
            skLineSegment(sketch, "E3925", {"start": v(17.06, -44.61) * mm, "end": v(17.14, -44.75) * mm});
            skLineSegment(sketch, "E3926", {"start": v(17.14, -44.75) * mm, "end": v(17.27, -44.86) * mm});
            skLineSegment(sketch, "E3927", {"start": v(17.27, -44.86) * mm, "end": v(17.41, -44.94) * mm});
            skLineSegment(sketch, "E3928", {"start": v(17.41, -44.94) * mm, "end": v(17.57, -44.97) * mm});
            skLineSegment(sketch, "E3929", {"start": v(17.57, -44.97) * mm, "end": v(17.74, -44.96) * mm});
            skLineSegment(sketch, "E3930", {"start": v(17.74, -44.96) * mm, "end": v(17.9, -44.91) * mm});
            skLineSegment(sketch, "E3931", {"start": v(17.9, -44.91) * mm, "end": v(18.03, -44.82) * mm});
            skLineSegment(sketch, "E3932", {"start": v(18.03, -44.82) * mm, "end": v(18.14, -44.7) * mm});
            skLineSegment(sketch, "E3933", {"start": v(18.14, -44.7) * mm, "end": v(18.21, -44.55) * mm});
            skLineSegment(sketch, "E3934", {"start": v(18.21, -44.55) * mm, "end": v(18.25, -44.4) * mm});
            skLineSegment(sketch, "E3935", {"start": v(18.25, -44.4) * mm, "end": v(18.24, -44.23) * mm});
            skLineSegment(sketch, "E3936", {"start": v(18.24, -44.23) * mm, "end": v(18.19, -44.08) * mm});
            skLineSegment(sketch, "E3937", {"start": v(18.19, -44.08) * mm, "end": v(18.13, -43.93) * mm});
            skLineSegment(sketch, "E3938", {"start": v(18.13, -43.93) * mm, "end": v(18.06, -43.8) * mm});
            skLineSegment(sketch, "E3939", {"start": v(18.06, -43.8) * mm, "end": v(18, -43.65) * mm});
            skLineSegment(sketch, "E3940", {"start": v(18, -43.65) * mm, "end": v(17.94, -43.5) * mm});
            skLineSegment(sketch, "E3941", {"start": v(17.94, -43.5) * mm, "end": v(17.88, -43.35) * mm});
            skLineSegment(sketch, "E3942", {"start": v(17.88, -43.35) * mm, "end": v(17.81, -43.2) * mm});
            skLineSegment(sketch, "E3943", {"start": v(17.81, -43.2) * mm, "end": v(17.75, -43.06) * mm});
            skLineSegment(sketch, "E3944", {"start": v(17.75, -43.06) * mm, "end": v(17.69, -42.92) * mm});
            skLineSegment(sketch, "E3945", {"start": v(17.69, -42.92) * mm, "end": v(17.63, -42.77) * mm});
            skLineSegment(sketch, "E3946", {"start": v(17.63, -42.77) * mm, "end": v(17.56, -42.63) * mm});
            skLineSegment(sketch, "E3947", {"start": v(17.56, -42.63) * mm, "end": v(17.5, -42.48) * mm});
            skLineSegment(sketch, "E3948", {"start": v(17.5, -42.48) * mm, "end": v(17.44, -42.33) * mm});
            skLineSegment(sketch, "E3949", {"start": v(17.44, -42.33) * mm, "end": v(17.4, -42.23) * mm});
            skLineSegment(sketch, "E3950", {"start": v(17.4, -42.23) * mm, "end": v(17.54, -42.16) * mm});
            skLineSegment(sketch, "E3951", {"start": v(17.54, -42.16) * mm, "end": v(17.68, -42.1) * mm});
            skLineSegment(sketch, "E3952", {"start": v(17.68, -42.1) * mm, "end": v(17.82, -42.03) * mm});
            skLineSegment(sketch, "E3953", {"start": v(17.82, -42.03) * mm, "end": v(17.97, -41.97) * mm});
            skLineSegment(sketch, "E3954", {"start": v(17.97, -41.97) * mm, "end": v(18.1, -41.9) * mm});
            skLineSegment(sketch, "E3955", {"start": v(18.1, -41.9) * mm, "end": v(18.25, -41.84) * mm});
            skLineSegment(sketch, "E3956", {"start": v(18.25, -41.84) * mm, "end": v(18.4, -41.77) * mm});
            skLineSegment(sketch, "E3957", {"start": v(18.4, -41.77) * mm, "end": v(18.54, -41.7) * mm});
            skLineSegment(sketch, "E3958", {"start": v(18.54, -41.7) * mm, "end": v(18.68, -41.64) * mm});
            skLineSegment(sketch, "E3959", {"start": v(18.68, -41.64) * mm, "end": v(18.83, -41.58) * mm});
            skLineSegment(sketch, "E3960", {"start": v(18.83, -41.58) * mm, "end": v(18.97, -41.51) * mm});
            skLineSegment(sketch, "E3961", {"start": v(18.97, -41.51) * mm, "end": v(19.04, -41.48) * mm});
            skLineSegment(sketch, "E3962", {"start": v(19.04, -41.48) * mm, "end": v(19.11, -41.62) * mm});
            skLineSegment(sketch, "E3963", {"start": v(19.11, -41.62) * mm, "end": v(19.18, -41.77) * mm});
            skLineSegment(sketch, "E3964", {"start": v(19.18, -41.77) * mm, "end": v(19.25, -41.91) * mm});
            skLineSegment(sketch, "E3965", {"start": v(19.25, -41.91) * mm, "end": v(19.32, -42.05) * mm});
            skLineSegment(sketch, "E3966", {"start": v(19.32, -42.05) * mm, "end": v(19.38, -42.2) * mm});
            skLineSegment(sketch, "E3967", {"start": v(19.38, -42.2) * mm, "end": v(19.45, -42.34) * mm});
            skLineSegment(sketch, "E3968", {"start": v(19.45, -42.34) * mm, "end": v(19.52, -42.48) * mm});
            skLineSegment(sketch, "E3969", {"start": v(19.52, -42.48) * mm, "end": v(19.59, -42.62) * mm});
            skLineSegment(sketch, "E3970", {"start": v(19.59, -42.62) * mm, "end": v(19.66, -42.77) * mm});
            skLineSegment(sketch, "E3971", {"start": v(19.66, -42.77) * mm, "end": v(19.73, -42.91) * mm});
            skLineSegment(sketch, "E3972", {"start": v(19.73, -42.91) * mm, "end": v(19.8, -43.05) * mm});
            skLineSegment(sketch, "E3973", {"start": v(19.8, -43.05) * mm, "end": v(19.86, -43.2) * mm});
            skLineSegment(sketch, "E3974", {"start": v(19.86, -43.2) * mm, "end": v(19.94, -43.35) * mm});
            skLineSegment(sketch, "E3975", {"start": v(19.94, -43.35) * mm, "end": v(20.03, -43.48) * mm});
            skLineSegment(sketch, "E3976", {"start": v(20.03, -43.48) * mm, "end": v(20.16, -43.59) * mm});
            skLineSegment(sketch, "E3977", {"start": v(20.16, -43.59) * mm, "end": v(20.31, -43.65) * mm});
            skLineSegment(sketch, "E3978", {"start": v(20.31, -43.65) * mm, "end": v(20.47, -43.68) * mm});
            skLineSegment(sketch, "E3979", {"start": v(20.47, -43.68) * mm, "end": v(20.64, -43.66) * mm});
            skLineSegment(sketch, "E3980", {"start": v(20.64, -43.66) * mm, "end": v(20.79, -43.6) * mm});
            skLineSegment(sketch, "E3981", {"start": v(20.79, -43.6) * mm, "end": v(20.92, -43.5) * mm});
            skLineSegment(sketch, "E3982", {"start": v(20.92, -43.5) * mm, "end": v(21.02, -43.37) * mm});
            skLineSegment(sketch, "E3983", {"start": v(21.02, -43.37) * mm, "end": v(21.09, -43.22) * mm});
            skLineSegment(sketch, "E3984", {"start": v(21.09, -43.22) * mm, "end": v(21.1, -43.06) * mm});
            skLineSegment(sketch, "E3985", {"start": v(21.1, -43.06) * mm, "end": v(21.09, -42.9) * mm});
            skLineSegment(sketch, "E3986", {"start": v(21.09, -42.9) * mm, "end": v(21.03, -42.75) * mm});
            skLineSegment(sketch, "E3987", {"start": v(21.03, -42.75) * mm, "end": v(20.96, -42.6) * mm});
            skLineSegment(sketch, "E3988", {"start": v(20.96, -42.6) * mm, "end": v(20.89, -42.47) * mm});
            skLineSegment(sketch, "E3989", {"start": v(20.89, -42.47) * mm, "end": v(20.82, -42.33) * mm});
            skLineSegment(sketch, "E3990", {"start": v(20.82, -42.33) * mm, "end": v(20.75, -42.19) * mm});
            skLineSegment(sketch, "E3991", {"start": v(20.75, -42.19) * mm, "end": v(20.67, -42.04) * mm});
            skLineSegment(sketch, "E3992", {"start": v(20.67, -42.04) * mm, "end": v(20.6, -41.9) * mm});
            skLineSegment(sketch, "E3993", {"start": v(20.6, -41.9) * mm, "end": v(20.53, -41.76) * mm});
            skLineSegment(sketch, "E3994", {"start": v(20.53, -41.76) * mm, "end": v(20.46, -41.62) * mm});
            skLineSegment(sketch, "E3995", {"start": v(20.46, -41.62) * mm, "end": v(20.38, -41.48) * mm});
            skLineSegment(sketch, "E3996", {"start": v(20.38, -41.48) * mm, "end": v(20.31, -41.34) * mm});
            skLineSegment(sketch, "E3997", {"start": v(20.31, -41.34) * mm, "end": v(20.24, -41.2) * mm});
            skLineSegment(sketch, "E3998", {"start": v(20.24, -41.2) * mm, "end": v(20.17, -41.05) * mm});
            skLineSegment(sketch, "E3999", {"start": v(20.17, -41.05) * mm, "end": v(20.12, -40.95) * mm});
            skLineSegment(sketch, "E4000", {"start": v(20.12, -40.95) * mm, "end": v(20.25, -40.88) * mm});
            skLineSegment(sketch, "E4001", {"start": v(20.25, -40.88) * mm, "end": v(20.4, -40.8) * mm});
            skLineSegment(sketch, "E4002", {"start": v(20.4, -40.8) * mm, "end": v(20.53, -40.73) * mm});
            skLineSegment(sketch, "E4003", {"start": v(20.53, -40.73) * mm, "end": v(20.67, -40.66) * mm});
            skLineSegment(sketch, "E4004", {"start": v(20.67, -40.66) * mm, "end": v(20.8, -40.58) * mm});
            skLineSegment(sketch, "E4005", {"start": v(20.8, -40.58) * mm, "end": v(20.95, -40.5) * mm});
            skLineSegment(sketch, "E4006", {"start": v(20.95, -40.5) * mm, "end": v(21.09, -40.43) * mm});
            skLineSegment(sketch, "E4007", {"start": v(21.09, -40.43) * mm, "end": v(21.23, -40.36) * mm});
            skLineSegment(sketch, "E4008", {"start": v(21.23, -40.36) * mm, "end": v(21.36, -40.28) * mm});
            skLineSegment(sketch, "E4009", {"start": v(21.36, -40.28) * mm, "end": v(21.5, -40.21) * mm});
            skLineSegment(sketch, "E4010", {"start": v(21.5, -40.21) * mm, "end": v(21.64, -40.14) * mm});
            skLineSegment(sketch, "E4011", {"start": v(21.64, -40.14) * mm, "end": v(21.71, -40.1) * mm});
            skLineSegment(sketch, "E4012", {"start": v(21.71, -40.1) * mm, "end": v(21.79, -40.24) * mm});
            skLineSegment(sketch, "E4013", {"start": v(21.79, -40.24) * mm, "end": v(21.87, -40.37) * mm});
            skLineSegment(sketch, "E4014", {"start": v(21.87, -40.37) * mm, "end": v(21.95, -40.51) * mm});
            skLineSegment(sketch, "E4015", {"start": v(21.95, -40.51) * mm, "end": v(22.02, -40.65) * mm});
            skLineSegment(sketch, "E4016", {"start": v(22.02, -40.65) * mm, "end": v(22.1, -40.79) * mm});
            skLineSegment(sketch, "E4017", {"start": v(22.1, -40.79) * mm, "end": v(22.18, -40.93) * mm});
            skLineSegment(sketch, "E4018", {"start": v(22.18, -40.93) * mm, "end": v(22.26, -41.07) * mm});
            skLineSegment(sketch, "E4019", {"start": v(22.26, -41.07) * mm, "end": v(22.33, -41.2) * mm});
            skLineSegment(sketch, "E4020", {"start": v(22.33, -41.2) * mm, "end": v(22.41, -41.34) * mm});
            skLineSegment(sketch, "E4021", {"start": v(22.41, -41.34) * mm, "end": v(22.49, -41.48) * mm});
            skLineSegment(sketch, "E4022", {"start": v(22.49, -41.48) * mm, "end": v(22.56, -41.62) * mm});
            skLineSegment(sketch, "E4023", {"start": v(22.56, -41.62) * mm, "end": v(22.64, -41.76) * mm});
            skLineSegment(sketch, "E4024", {"start": v(22.64, -41.76) * mm, "end": v(22.73, -41.9) * mm});
            skLineSegment(sketch, "E4025", {"start": v(22.73, -41.9) * mm, "end": v(22.83, -42.03) * mm});
            skLineSegment(sketch, "E4026", {"start": v(22.83, -42.03) * mm, "end": v(22.97, -42.13) * mm});
            skLineSegment(sketch, "E4027", {"start": v(22.97, -42.13) * mm, "end": v(23.12, -42.18) * mm});
            skLineSegment(sketch, "E4028", {"start": v(23.12, -42.18) * mm, "end": v(23.29, -42.2) * mm});
            skLineSegment(sketch, "E4029", {"start": v(23.29, -42.2) * mm, "end": v(23.45, -42.16) * mm});
            skLineSegment(sketch, "E4030", {"start": v(23.45, -42.16) * mm, "end": v(23.6, -42.1) * mm});
            skLineSegment(sketch, "E4031", {"start": v(23.6, -42.1) * mm, "end": v(23.72, -41.99) * mm});
            skLineSegment(sketch, "E4032", {"start": v(23.72, -41.99) * mm, "end": v(23.81, -41.85) * mm});
            skLineSegment(sketch, "E4033", {"start": v(23.81, -41.85) * mm, "end": v(23.87, -41.7) * mm});
            skLineSegment(sketch, "E4034", {"start": v(23.87, -41.7) * mm, "end": v(23.88, -41.53) * mm});
            skLineSegment(sketch, "E4035", {"start": v(23.88, -41.53) * mm, "end": v(23.85, -41.37) * mm});
            skLineSegment(sketch, "E4036", {"start": v(23.85, -41.37) * mm, "end": v(23.78, -41.23) * mm});
            skLineSegment(sketch, "E4037", {"start": v(23.78, -41.23) * mm, "end": v(23.7, -41.1) * mm});
            skLineSegment(sketch, "E4038", {"start": v(23.7, -41.1) * mm, "end": v(23.62, -40.96) * mm});
            skLineSegment(sketch, "E4039", {"start": v(23.62, -40.96) * mm, "end": v(23.54, -40.83) * mm});
            skLineSegment(sketch, "E4040", {"start": v(23.54, -40.83) * mm, "end": v(23.46, -40.7) * mm});
            skLineSegment(sketch, "E4041", {"start": v(23.46, -40.7) * mm, "end": v(23.38, -40.55) * mm});
            skLineSegment(sketch, "E4042", {"start": v(23.38, -40.55) * mm, "end": v(23.3, -40.42) * mm});
            skLineSegment(sketch, "E4043", {"start": v(23.3, -40.42) * mm, "end": v(23.22, -40.28) * mm});
            skLineSegment(sketch, "E4044", {"start": v(23.22, -40.28) * mm, "end": v(23.13, -40.14) * mm});
            skLineSegment(sketch, "E4045", {"start": v(23.13, -40.14) * mm, "end": v(23.05, -40) * mm});
            skLineSegment(sketch, "E4046", {"start": v(23.05, -40) * mm, "end": v(22.97, -39.87) * mm});
            skLineSegment(sketch, "E4047", {"start": v(22.97, -39.87) * mm, "end": v(22.89, -39.73) * mm});
            skLineSegment(sketch, "E4048", {"start": v(22.89, -39.73) * mm, "end": v(22.8, -39.6) * mm});
            skLineSegment(sketch, "E4049", {"start": v(22.8, -39.6) * mm, "end": v(22.75, -39.5) * mm});
            skLineSegment(sketch, "E4050", {"start": v(22.75, -39.5) * mm, "end": v(22.88, -39.42) * mm});
            skLineSegment(sketch, "E4051", {"start": v(22.88, -39.42) * mm, "end": v(23.02, -39.33) * mm});
            skLineSegment(sketch, "E4052", {"start": v(23.02, -39.33) * mm, "end": v(23.15, -39.25) * mm});
            skLineSegment(sketch, "E4053", {"start": v(23.15, -39.25) * mm, "end": v(23.28, -39.17) * mm});
            skLineSegment(sketch, "E4054", {"start": v(23.28, -39.17) * mm, "end": v(23.42, -39.08) * mm});
            skLineSegment(sketch, "E4055", {"start": v(23.42, -39.08) * mm, "end": v(23.55, -39) * mm});
            skLineSegment(sketch, "E4056", {"start": v(23.55, -39) * mm, "end": v(23.68, -38.92) * mm});
            skLineSegment(sketch, "E4057", {"start": v(23.68, -38.92) * mm, "end": v(23.82, -38.84) * mm});
            skLineSegment(sketch, "E4058", {"start": v(23.82, -38.84) * mm, "end": v(23.95, -38.75) * mm});
            skLineSegment(sketch, "E4059", {"start": v(23.95, -38.75) * mm, "end": v(24.09, -38.67) * mm});
            skLineSegment(sketch, "E4060", {"start": v(24.09, -38.67) * mm, "end": v(24.22, -38.59) * mm});
            skLineSegment(sketch, "E4061", {"start": v(24.22, -38.59) * mm, "end": v(24.29, -38.54) * mm});
            skLineSegment(sketch, "E4062", {"start": v(24.29, -38.54) * mm, "end": v(24.37, -38.68) * mm});
            skLineSegment(sketch, "E4063", {"start": v(24.37, -38.68) * mm, "end": v(24.46, -38.8) * mm});
            skLineSegment(sketch, "E4064", {"start": v(24.46, -38.8) * mm, "end": v(24.55, -38.94) * mm});
            skLineSegment(sketch, "E4065", {"start": v(24.55, -38.94) * mm, "end": v(24.63, -39.07) * mm});
            skLineSegment(sketch, "E4066", {"start": v(24.63, -39.07) * mm, "end": v(24.72, -39.2) * mm});
            skLineSegment(sketch, "E4067", {"start": v(24.72, -39.2) * mm, "end": v(24.8, -39.34) * mm});
            skLineSegment(sketch, "E4068", {"start": v(24.8, -39.34) * mm, "end": v(24.9, -39.47) * mm});
            skLineSegment(sketch, "E4069", {"start": v(24.9, -39.47) * mm, "end": v(24.98, -39.6) * mm});
            skLineSegment(sketch, "E4070", {"start": v(24.98, -39.6) * mm, "end": v(25.07, -39.74) * mm});
            skLineSegment(sketch, "E4071", {"start": v(25.07, -39.74) * mm, "end": v(25.15, -39.87) * mm});
            skLineSegment(sketch, "E4072", {"start": v(25.15, -39.87) * mm, "end": v(25.24, -40) * mm});
            skLineSegment(sketch, "E4073", {"start": v(25.24, -40) * mm, "end": v(25.32, -40.14) * mm});
            skLineSegment(sketch, "E4074", {"start": v(25.32, -40.14) * mm, "end": v(25.42, -40.28) * mm});
            skLineSegment(sketch, "E4075", {"start": v(25.42, -40.28) * mm, "end": v(25.53, -40.4) * mm});
            skLineSegment(sketch, "E4076", {"start": v(25.53, -40.4) * mm, "end": v(25.67, -40.48) * mm});
            skLineSegment(sketch, "E4077", {"start": v(25.67, -40.48) * mm, "end": v(25.83, -40.53) * mm});
            skLineSegment(sketch, "E4078", {"start": v(25.83, -40.53) * mm, "end": v(26, -40.53) * mm});
            skLineSegment(sketch, "E4079", {"start": v(26, -40.53) * mm, "end": v(26.15, -40.5) * mm});
            skLineSegment(sketch, "E4080", {"start": v(26.15, -40.5) * mm, "end": v(26.3, -40.41) * mm});
            skLineSegment(sketch, "E4081", {"start": v(26.3, -40.41) * mm, "end": v(26.41, -40.3) * mm});
            skLineSegment(sketch, "E4082", {"start": v(26.41, -40.3) * mm, "end": v(26.5, -40.16) * mm});
            skLineSegment(sketch, "E4083", {"start": v(26.5, -40.16) * mm, "end": v(26.54, -40) * mm});
            skLineSegment(sketch, "E4084", {"start": v(26.54, -40) * mm, "end": v(26.54, -39.83) * mm});
            skLineSegment(sketch, "E4085", {"start": v(26.54, -39.83) * mm, "end": v(26.5, -39.68) * mm});
            skLineSegment(sketch, "E4086", {"start": v(26.5, -39.68) * mm, "end": v(26.42, -39.54) * mm});
            skLineSegment(sketch, "E4087", {"start": v(26.42, -39.54) * mm, "end": v(26.33, -39.4) * mm});
            skLineSegment(sketch, "E4088", {"start": v(26.33, -39.4) * mm, "end": v(26.25, -39.28) * mm});
            skLineSegment(sketch, "E4089", {"start": v(26.25, -39.28) * mm, "end": v(26.16, -39.15) * mm});
            skLineSegment(sketch, "E4090", {"start": v(26.16, -39.15) * mm, "end": v(26.07, -39.02) * mm});
            skLineSegment(sketch, "E4091", {"start": v(26.07, -39.02) * mm, "end": v(25.98, -38.89) * mm});
            skLineSegment(sketch, "E4092", {"start": v(25.98, -38.89) * mm, "end": v(25.89, -38.76) * mm});
            skLineSegment(sketch, "E4093", {"start": v(25.89, -38.76) * mm, "end": v(25.8, -38.63) * mm});
            skLineSegment(sketch, "E4094", {"start": v(25.8, -38.63) * mm, "end": v(25.7, -38.5) * mm});
            skLineSegment(sketch, "E4095", {"start": v(25.7, -38.5) * mm, "end": v(25.62, -38.37) * mm});
            skLineSegment(sketch, "E4096", {"start": v(25.62, -38.37) * mm, "end": v(25.53, -38.24) * mm});
            skLineSegment(sketch, "E4097", {"start": v(25.53, -38.24) * mm, "end": v(25.44, -38.1) * mm});
            skLineSegment(sketch, "E4098", {"start": v(25.44, -38.1) * mm, "end": v(25.35, -37.97) * mm});
            skLineSegment(sketch, "E4099", {"start": v(25.35, -37.97) * mm, "end": v(25.28, -37.88) * mm});
            skLineSegment(sketch, "E4100", {"start": v(25.28, -37.88) * mm, "end": v(25.41, -37.79) * mm});
            skLineSegment(sketch, "E4101", {"start": v(25.41, -37.79) * mm, "end": v(25.54, -37.7) * mm});
            skLineSegment(sketch, "E4102", {"start": v(25.54, -37.7) * mm, "end": v(25.67, -37.6) * mm});
            skLineSegment(sketch, "E4103", {"start": v(25.67, -37.6) * mm, "end": v(25.8, -37.51) * mm});
            skLineSegment(sketch, "E4104", {"start": v(25.8, -37.51) * mm, "end": v(25.92, -37.42) * mm});
            skLineSegment(sketch, "E4105", {"start": v(25.92, -37.42) * mm, "end": v(26.05, -37.33) * mm});
            skLineSegment(sketch, "E4106", {"start": v(26.05, -37.33) * mm, "end": v(26.18, -37.24) * mm});
            skLineSegment(sketch, "E4107", {"start": v(26.18, -37.24) * mm, "end": v(26.3, -37.15) * mm});
            skLineSegment(sketch, "E4108", {"start": v(26.3, -37.15) * mm, "end": v(26.43, -37.05) * mm});
            skLineSegment(sketch, "E4109", {"start": v(26.43, -37.05) * mm, "end": v(26.56, -36.96) * mm});
            skLineSegment(sketch, "E4110", {"start": v(26.56, -36.96) * mm, "end": v(26.69, -36.87) * mm});
            skLineSegment(sketch, "E4111", {"start": v(26.69, -36.87) * mm, "end": v(26.75, -36.82) * mm});
            skLineSegment(sketch, "E4112", {"start": v(26.75, -36.82) * mm, "end": v(26.85, -36.95) * mm});
            skLineSegment(sketch, "E4113", {"start": v(26.85, -36.95) * mm, "end": v(26.94, -37.08) * mm});
            skLineSegment(sketch, "E4114", {"start": v(26.94, -37.08) * mm, "end": v(27.04, -37.2) * mm});
            skLineSegment(sketch, "E4115", {"start": v(27.04, -37.2) * mm, "end": v(27.13, -37.33) * mm});
            skLineSegment(sketch, "E4116", {"start": v(27.13, -37.33) * mm, "end": v(27.23, -37.46) * mm});
            skLineSegment(sketch, "E4117", {"start": v(27.23, -37.46) * mm, "end": v(27.32, -37.59) * mm});
            skLineSegment(sketch, "E4118", {"start": v(27.32, -37.59) * mm, "end": v(27.42, -37.71) * mm});
            skLineSegment(sketch, "E4119", {"start": v(27.42, -37.71) * mm, "end": v(27.51, -37.84) * mm});
            skLineSegment(sketch, "E4120", {"start": v(27.51, -37.84) * mm, "end": v(27.6, -37.97) * mm});
            skLineSegment(sketch, "E4121", {"start": v(27.6, -37.97) * mm, "end": v(27.7, -38.1) * mm});
            skLineSegment(sketch, "E4122", {"start": v(27.7, -38.1) * mm, "end": v(27.8, -38.22) * mm});
            skLineSegment(sketch, "E4123", {"start": v(27.8, -38.22) * mm, "end": v(27.9, -38.35) * mm});
            skLineSegment(sketch, "E4124", {"start": v(27.9, -38.35) * mm, "end": v(28, -38.48) * mm});
            skLineSegment(sketch, "E4125", {"start": v(28, -38.48) * mm, "end": v(28.12, -38.6) * mm});
            skLineSegment(sketch, "E4126", {"start": v(28.12, -38.6) * mm, "end": v(28.26, -38.67) * mm});
            skLineSegment(sketch, "E4127", {"start": v(28.26, -38.67) * mm, "end": v(28.42, -38.7) * mm});
            skLineSegment(sketch, "E4128", {"start": v(28.42, -38.7) * mm, "end": v(28.59, -38.7) * mm});
            skLineSegment(sketch, "E4129", {"start": v(28.59, -38.7) * mm, "end": v(28.74, -38.65) * mm});
            skLineSegment(sketch, "E4130", {"start": v(28.74, -38.65) * mm, "end": v(28.88, -38.56) * mm});
            skLineSegment(sketch, "E4131", {"start": v(28.88, -38.56) * mm, "end": v(28.99, -38.43) * mm});
            skLineSegment(sketch, "E4132", {"start": v(28.99, -38.43) * mm, "end": v(29.06, -38.29) * mm});
            skLineSegment(sketch, "E4133", {"start": v(29.06, -38.29) * mm, "end": v(29.1, -38.13) * mm});
            skLineSegment(sketch, "E4134", {"start": v(29.1, -38.13) * mm, "end": v(29.09, -37.96) * mm});
            skLineSegment(sketch, "E4135", {"start": v(29.09, -37.96) * mm, "end": v(29.04, -37.8) * mm});
            skLineSegment(sketch, "E4136", {"start": v(29.04, -37.8) * mm, "end": v(28.95, -37.68) * mm});
            skLineSegment(sketch, "E4137", {"start": v(28.95, -37.68) * mm, "end": v(28.85, -37.55) * mm});
            skLineSegment(sketch, "E4138", {"start": v(28.85, -37.55) * mm, "end": v(28.76, -37.43) * mm});
            skLineSegment(sketch, "E4139", {"start": v(28.76, -37.43) * mm, "end": v(28.66, -37.3) * mm});
            skLineSegment(sketch, "E4140", {"start": v(28.66, -37.3) * mm, "end": v(28.56, -37.18) * mm});
            skLineSegment(sketch, "E4141", {"start": v(28.56, -37.18) * mm, "end": v(28.46, -37.06) * mm});
            skLineSegment(sketch, "E4142", {"start": v(28.46, -37.06) * mm, "end": v(28.37, -36.93) * mm});
            skLineSegment(sketch, "E4143", {"start": v(28.37, -36.93) * mm, "end": v(28.27, -36.8) * mm});
            skLineSegment(sketch, "E4144", {"start": v(28.27, -36.8) * mm, "end": v(28.17, -36.68) * mm});
            skLineSegment(sketch, "E4145", {"start": v(28.17, -36.68) * mm, "end": v(28.07, -36.56) * mm});
            skLineSegment(sketch, "E4146", {"start": v(28.07, -36.56) * mm, "end": v(27.97, -36.44) * mm});
            skLineSegment(sketch, "E4147", {"start": v(27.97, -36.44) * mm, "end": v(27.87, -36.3) * mm});
            skLineSegment(sketch, "E4148", {"start": v(27.87, -36.3) * mm, "end": v(27.78, -36.19) * mm});
            skLineSegment(sketch, "E4149", {"start": v(27.78, -36.19) * mm, "end": v(27.7, -36.1) * mm});
            skLineSegment(sketch, "E4150", {"start": v(27.7, -36.1) * mm, "end": v(27.83, -36) * mm});
            skLineSegment(sketch, "E4151", {"start": v(27.83, -36) * mm, "end": v(27.95, -35.9) * mm});
            skLineSegment(sketch, "E4152", {"start": v(27.95, -35.9) * mm, "end": v(28.07, -35.8) * mm});
            skLineSegment(sketch, "E4153", {"start": v(28.07, -35.8) * mm, "end": v(28.2, -35.7) * mm});
            skLineSegment(sketch, "E4154", {"start": v(28.2, -35.7) * mm, "end": v(28.31, -35.6) * mm});
            skLineSegment(sketch, "E4155", {"start": v(28.31, -35.6) * mm, "end": v(28.43, -35.5) * mm});
            skLineSegment(sketch, "E4156", {"start": v(28.43, -35.5) * mm, "end": v(28.56, -35.4) * mm});
            skLineSegment(sketch, "E4157", {"start": v(28.56, -35.4) * mm, "end": v(28.68, -35.3) * mm});
            skLineSegment(sketch, "E4158", {"start": v(28.68, -35.3) * mm, "end": v(28.8, -35.2) * mm});
            skLineSegment(sketch, "E4159", {"start": v(28.8, -35.2) * mm, "end": v(28.92, -35.1) * mm});
            skLineSegment(sketch, "E4160", {"start": v(28.92, -35.1) * mm, "end": v(29.04, -35) * mm});
            skLineSegment(sketch, "E4161", {"start": v(29.04, -35) * mm, "end": v(29.1, -34.95) * mm});
            skLineSegment(sketch, "E4162", {"start": v(29.1, -34.95) * mm, "end": v(29.2, -35.07) * mm});
            skLineSegment(sketch, "E4163", {"start": v(29.2, -35.07) * mm, "end": v(29.3, -35.19) * mm});
            skLineSegment(sketch, "E4164", {"start": v(29.3, -35.19) * mm, "end": v(29.41, -35.3) * mm});
            skLineSegment(sketch, "E4165", {"start": v(29.41, -35.3) * mm, "end": v(29.52, -35.43) * mm});
            skLineSegment(sketch, "E4166", {"start": v(29.52, -35.43) * mm, "end": v(29.62, -35.55) * mm});
            skLineSegment(sketch, "E4167", {"start": v(29.62, -35.55) * mm, "end": v(29.72, -35.67) * mm});
            skLineSegment(sketch, "E4168", {"start": v(29.72, -35.67) * mm, "end": v(29.82, -35.79) * mm});
            skLineSegment(sketch, "E4169", {"start": v(29.82, -35.79) * mm, "end": v(29.93, -35.9) * mm});
            skLineSegment(sketch, "E4170", {"start": v(29.93, -35.9) * mm, "end": v(30.03, -36.03) * mm});
            skLineSegment(sketch, "E4171", {"start": v(30.03, -36.03) * mm, "end": v(30.13, -36.15) * mm});
            skLineSegment(sketch, "E4172", {"start": v(30.13, -36.15) * mm, "end": v(30.24, -36.27) * mm});
            skLineSegment(sketch, "E4173", {"start": v(30.24, -36.27) * mm, "end": v(30.34, -36.4) * mm});
            skLineSegment(sketch, "E4174", {"start": v(30.34, -36.4) * mm, "end": v(30.45, -36.52) * mm});
            skLineSegment(sketch, "E4175", {"start": v(30.45, -36.52) * mm, "end": v(30.58, -36.62) * mm});
            skLineSegment(sketch, "E4176", {"start": v(30.58, -36.62) * mm, "end": v(30.73, -36.69) * mm});
            skLineSegment(sketch, "E4177", {"start": v(30.73, -36.69) * mm, "end": v(30.9, -36.71) * mm});
            skLineSegment(sketch, "E4178", {"start": v(30.9, -36.71) * mm, "end": v(31.05, -36.7) * mm});
            skLineSegment(sketch, "E4179", {"start": v(31.05, -36.7) * mm, "end": v(31.2, -36.63) * mm});
            skLineSegment(sketch, "E4180", {"start": v(31.2, -36.63) * mm, "end": v(31.34, -36.54) * mm});
            skLineSegment(sketch, "E4181", {"start": v(31.34, -36.54) * mm, "end": v(31.44, -36.4) * mm});
            skLineSegment(sketch, "E4182", {"start": v(31.44, -36.4) * mm, "end": v(31.5, -36.26) * mm});
            skLineSegment(sketch, "E4183", {"start": v(31.5, -36.26) * mm, "end": v(31.53, -36.1) * mm});
            skLineSegment(sketch, "E4184", {"start": v(31.53, -36.1) * mm, "end": v(31.5, -35.93) * mm});
            skLineSegment(sketch, "E4185", {"start": v(31.5, -35.93) * mm, "end": v(31.45, -35.78) * mm});
            skLineSegment(sketch, "E4186", {"start": v(31.45, -35.78) * mm, "end": v(31.35, -35.66) * mm});
            skLineSegment(sketch, "E4187", {"start": v(31.35, -35.66) * mm, "end": v(31.25, -35.54) * mm});
            skLineSegment(sketch, "E4188", {"start": v(31.25, -35.54) * mm, "end": v(31.14, -35.42) * mm});
            skLineSegment(sketch, "E4189", {"start": v(31.14, -35.42) * mm, "end": v(31.04, -35.3) * mm});
            skLineSegment(sketch, "E4190", {"start": v(31.04, -35.3) * mm, "end": v(30.93, -35.19) * mm});
            skLineSegment(sketch, "E4191", {"start": v(30.93, -35.19) * mm, "end": v(30.82, -35.07) * mm});
            skLineSegment(sketch, "E4192", {"start": v(30.82, -35.07) * mm, "end": v(30.72, -34.95) * mm});
            skLineSegment(sketch, "E4193", {"start": v(30.72, -34.95) * mm, "end": v(30.61, -34.83) * mm});
            skLineSegment(sketch, "E4194", {"start": v(30.61, -34.83) * mm, "end": v(30.5, -34.71) * mm});
            skLineSegment(sketch, "E4195", {"start": v(30.5, -34.71) * mm, "end": v(30.4, -34.6) * mm});
            skLineSegment(sketch, "E4196", {"start": v(30.4, -34.6) * mm, "end": v(30.3, -34.48) * mm});
            skLineSegment(sketch, "E4197", {"start": v(30.3, -34.48) * mm, "end": v(30.19, -34.36) * mm});
            skLineSegment(sketch, "E4198", {"start": v(30.19, -34.36) * mm, "end": v(30.08, -34.24) * mm});
            skLineSegment(sketch, "E4199", {"start": v(30.08, -34.24) * mm, "end": v(30, -34.16) * mm});
            skLineSegment(sketch, "E4200", {"start": v(30, -34.16) * mm, "end": v(30.12, -34.05) * mm});
            skLineSegment(sketch, "E4201", {"start": v(30.12, -34.05) * mm, "end": v(30.23, -33.94) * mm});
            skLineSegment(sketch, "E4202", {"start": v(30.23, -33.94) * mm, "end": v(30.35, -33.83) * mm});
            skLineSegment(sketch, "E4203", {"start": v(30.35, -33.83) * mm, "end": v(30.46, -33.73) * mm});
            skLineSegment(sketch, "E4204", {"start": v(30.46, -33.73) * mm, "end": v(30.58, -33.62) * mm});
            skLineSegment(sketch, "E4205", {"start": v(30.58, -33.62) * mm, "end": v(30.7, -33.51) * mm});
            skLineSegment(sketch, "E4206", {"start": v(30.7, -33.51) * mm, "end": v(30.8, -33.4) * mm});
            skLineSegment(sketch, "E4207", {"start": v(30.8, -33.4) * mm, "end": v(30.92, -33.3) * mm});
            skLineSegment(sketch, "E4208", {"start": v(30.92, -33.3) * mm, "end": v(31.04, -33.19) * mm});
            skLineSegment(sketch, "E4209", {"start": v(31.04, -33.19) * mm, "end": v(31.15, -33.08) * mm});
            skLineSegment(sketch, "E4210", {"start": v(31.15, -33.08) * mm, "end": v(31.27, -32.97) * mm});
            skLineSegment(sketch, "E4211", {"start": v(31.27, -32.97) * mm, "end": v(31.33, -32.92) * mm});
            skLineSegment(sketch, "E4212", {"start": v(31.33, -32.92) * mm, "end": v(31.44, -33.03) * mm});
            skLineSegment(sketch, "E4213", {"start": v(31.44, -33.03) * mm, "end": v(31.55, -33.14) * mm});
            skLineSegment(sketch, "E4214", {"start": v(31.55, -33.14) * mm, "end": v(31.66, -33.26) * mm});
            skLineSegment(sketch, "E4215", {"start": v(31.66, -33.26) * mm, "end": v(31.77, -33.37) * mm});
            skLineSegment(sketch, "E4216", {"start": v(31.77, -33.37) * mm, "end": v(31.88, -33.49) * mm});
            skLineSegment(sketch, "E4217", {"start": v(31.88, -33.49) * mm, "end": v(32, -33.6) * mm});
            skLineSegment(sketch, "E4218", {"start": v(32, -33.6) * mm, "end": v(32.1, -33.71) * mm});
            skLineSegment(sketch, "E4219", {"start": v(32.1, -33.71) * mm, "end": v(32.2, -33.83) * mm});
            skLineSegment(sketch, "E4220", {"start": v(32.2, -33.83) * mm, "end": v(32.32, -33.94) * mm});
            skLineSegment(sketch, "E4221", {"start": v(32.32, -33.94) * mm, "end": v(32.43, -34.05) * mm});
            skLineSegment(sketch, "E4222", {"start": v(32.43, -34.05) * mm, "end": v(32.54, -34.17) * mm});
            skLineSegment(sketch, "E4223", {"start": v(32.54, -34.17) * mm, "end": v(32.65, -34.28) * mm});
            skLineSegment(sketch, "E4224", {"start": v(32.65, -34.28) * mm, "end": v(32.77, -34.4) * mm});
            skLineSegment(sketch, "E4225", {"start": v(32.77, -34.4) * mm, "end": v(32.9, -34.5) * mm});
            skLineSegment(sketch, "E4226", {"start": v(32.9, -34.5) * mm, "end": v(33.06, -34.55) * mm});
            skLineSegment(sketch, "E4227", {"start": v(33.06, -34.55) * mm, "end": v(33.23, -34.57) * mm});
            skLineSegment(sketch, "E4228", {"start": v(33.23, -34.57) * mm, "end": v(33.39, -34.54) * mm});
            skLineSegment(sketch, "E4229", {"start": v(33.39, -34.54) * mm, "end": v(33.53, -34.47) * mm});
            skLineSegment(sketch, "E4230", {"start": v(33.53, -34.47) * mm, "end": v(33.66, -34.36) * mm});
            skLineSegment(sketch, "E4231", {"start": v(33.66, -34.36) * mm, "end": v(33.75, -34.22) * mm});
            skLineSegment(sketch, "E4232", {"start": v(33.75, -34.22) * mm, "end": v(33.8, -34.07) * mm});
            skLineSegment(sketch, "E4233", {"start": v(33.8, -34.07) * mm, "end": v(33.82, -33.9) * mm});
            skLineSegment(sketch, "E4234", {"start": v(33.82, -33.9) * mm, "end": v(33.79, -33.75) * mm});
            skLineSegment(sketch, "E4235", {"start": v(33.79, -33.75) * mm, "end": v(33.72, -33.6) * mm});
            skLineSegment(sketch, "E4236", {"start": v(33.72, -33.6) * mm, "end": v(33.61, -33.48) * mm});
            skLineSegment(sketch, "E4237", {"start": v(33.61, -33.48) * mm, "end": v(33.5, -33.37) * mm});
            skLineSegment(sketch, "E4238", {"start": v(33.5, -33.37) * mm, "end": v(33.4, -33.26) * mm});
            skLineSegment(sketch, "E4239", {"start": v(33.4, -33.26) * mm, "end": v(33.28, -33.15) * mm});
            skLineSegment(sketch, "E4240", {"start": v(33.28, -33.15) * mm, "end": v(33.17, -33.04) * mm});
            skLineSegment(sketch, "E4241", {"start": v(33.17, -33.04) * mm, "end": v(33.05, -32.93) * mm});
            skLineSegment(sketch, "E4242", {"start": v(33.05, -32.93) * mm, "end": v(32.94, -32.82) * mm});
            skLineSegment(sketch, "E4243", {"start": v(32.94, -32.82) * mm, "end": v(32.82, -32.7) * mm});
            skLineSegment(sketch, "E4244", {"start": v(32.82, -32.7) * mm, "end": v(32.7, -32.6) * mm});
            skLineSegment(sketch, "E4245", {"start": v(32.7, -32.6) * mm, "end": v(32.6, -32.48) * mm});
            skLineSegment(sketch, "E4246", {"start": v(32.6, -32.48) * mm, "end": v(32.48, -32.38) * mm});
            skLineSegment(sketch, "E4247", {"start": v(32.48, -32.38) * mm, "end": v(32.37, -32.26) * mm});
            skLineSegment(sketch, "E4248", {"start": v(32.37, -32.26) * mm, "end": v(32.25, -32.15) * mm});
            skLineSegment(sketch, "E4249", {"start": v(32.25, -32.15) * mm, "end": v(32.17, -32.07) * mm});
            skLineSegment(sketch, "E4250", {"start": v(32.17, -32.07) * mm, "end": v(32.28, -31.96) * mm});
            skLineSegment(sketch, "E4251", {"start": v(32.28, -31.96) * mm, "end": v(32.39, -31.84) * mm});
            skLineSegment(sketch, "E4252", {"start": v(32.39, -31.84) * mm, "end": v(32.5, -31.73) * mm});
            skLineSegment(sketch, "E4253", {"start": v(32.5, -31.73) * mm, "end": v(32.6, -31.61) * mm});
            skLineSegment(sketch, "E4254", {"start": v(32.6, -31.61) * mm, "end": v(32.71, -31.5) * mm});
            skLineSegment(sketch, "E4255", {"start": v(32.71, -31.5) * mm, "end": v(32.82, -31.38) * mm});
            skLineSegment(sketch, "E4256", {"start": v(32.82, -31.38) * mm, "end": v(32.93, -31.27) * mm});
            skLineSegment(sketch, "E4257", {"start": v(32.93, -31.27) * mm, "end": v(33.03, -31.15) * mm});
            skLineSegment(sketch, "E4258", {"start": v(33.03, -31.15) * mm, "end": v(33.14, -31.04) * mm});
            skLineSegment(sketch, "E4259", {"start": v(33.14, -31.04) * mm, "end": v(33.25, -30.92) * mm});
            skLineSegment(sketch, "E4260", {"start": v(33.25, -30.92) * mm, "end": v(33.36, -30.8) * mm});
            skLineSegment(sketch, "E4261", {"start": v(33.36, -30.8) * mm, "end": v(33.41, -30.75) * mm});
            skLineSegment(sketch, "E4262", {"start": v(33.41, -30.75) * mm, "end": v(33.53, -30.86) * mm});
            skLineSegment(sketch, "E4263", {"start": v(33.53, -30.86) * mm, "end": v(33.64, -30.96) * mm});
            skLineSegment(sketch, "E4264", {"start": v(33.64, -30.96) * mm, "end": v(33.76, -31.07) * mm});
            skLineSegment(sketch, "E4265", {"start": v(33.76, -31.07) * mm, "end": v(33.88, -31.17) * mm});
            skLineSegment(sketch, "E4266", {"start": v(33.88, -31.17) * mm, "end": v(34, -31.28) * mm});
            skLineSegment(sketch, "E4267", {"start": v(34, -31.28) * mm, "end": v(34.12, -31.39) * mm});
            skLineSegment(sketch, "E4268", {"start": v(34.12, -31.39) * mm, "end": v(34.23, -31.5) * mm});
            skLineSegment(sketch, "E4269", {"start": v(34.23, -31.5) * mm, "end": v(34.35, -31.6) * mm});
            skLineSegment(sketch, "E4270", {"start": v(34.35, -31.6) * mm, "end": v(34.47, -31.7) * mm});
            skLineSegment(sketch, "E4271", {"start": v(34.47, -31.7) * mm, "end": v(34.59, -31.81) * mm});
            skLineSegment(sketch, "E4272", {"start": v(34.59, -31.81) * mm, "end": v(34.7, -31.92) * mm});
            skLineSegment(sketch, "E4273", {"start": v(34.7, -31.92) * mm, "end": v(34.83, -32.03) * mm});
            skLineSegment(sketch, "E4274", {"start": v(34.83, -32.03) * mm, "end": v(34.95, -32.14) * mm});
            skLineSegment(sketch, "E4275", {"start": v(34.95, -32.14) * mm, "end": v(35.1, -32.22) * mm});
            skLineSegment(sketch, "E4276", {"start": v(35.1, -32.22) * mm, "end": v(35.25, -32.27) * mm});
            skLineSegment(sketch, "E4277", {"start": v(35.25, -32.27) * mm, "end": v(35.41, -32.27) * mm});
            skLineSegment(sketch, "E4278", {"start": v(35.41, -32.27) * mm, "end": v(35.57, -32.23) * mm});
            skLineSegment(sketch, "E4279", {"start": v(35.57, -32.23) * mm, "end": v(35.72, -32.15) * mm});
            skLineSegment(sketch, "E4280", {"start": v(35.72, -32.15) * mm, "end": v(35.83, -32.04) * mm});
            skLineSegment(sketch, "E4281", {"start": v(35.83, -32.04) * mm, "end": v(35.92, -31.9) * mm});
            skLineSegment(sketch, "E4282", {"start": v(35.92, -31.9) * mm, "end": v(35.96, -31.74) * mm});
            skLineSegment(sketch, "E4283", {"start": v(35.96, -31.74) * mm, "end": v(35.96, -31.57) * mm});
            skLineSegment(sketch, "E4284", {"start": v(35.96, -31.57) * mm, "end": v(35.92, -31.41) * mm});
            skLineSegment(sketch, "E4285", {"start": v(35.92, -31.41) * mm, "end": v(35.84, -31.27) * mm});
            skLineSegment(sketch, "E4286", {"start": v(35.84, -31.27) * mm, "end": v(35.73, -31.16) * mm});
            skLineSegment(sketch, "E4287", {"start": v(35.73, -31.16) * mm, "end": v(35.61, -31.06) * mm});
            skLineSegment(sketch, "E4288", {"start": v(35.61, -31.06) * mm, "end": v(35.5, -30.96) * mm});
            skLineSegment(sketch, "E4289", {"start": v(35.5, -30.96) * mm, "end": v(35.37, -30.85) * mm});
            skLineSegment(sketch, "E4290", {"start": v(35.37, -30.85) * mm, "end": v(35.25, -30.75) * mm});
            skLineSegment(sketch, "E4291", {"start": v(35.25, -30.75) * mm, "end": v(35.13, -30.65) * mm});
            skLineSegment(sketch, "E4292", {"start": v(35.13, -30.65) * mm, "end": v(35.01, -30.54) * mm});
            skLineSegment(sketch, "E4293", {"start": v(35.01, -30.54) * mm, "end": v(34.9, -30.44) * mm});
            skLineSegment(sketch, "E4294", {"start": v(34.9, -30.44) * mm, "end": v(34.77, -30.34) * mm});
            skLineSegment(sketch, "E4295", {"start": v(34.77, -30.34) * mm, "end": v(34.65, -30.23) * mm});
            skLineSegment(sketch, "E4296", {"start": v(34.65, -30.23) * mm, "end": v(34.53, -30.13) * mm});
            skLineSegment(sketch, "E4297", {"start": v(34.53, -30.13) * mm, "end": v(34.4, -30.03) * mm});
            skLineSegment(sketch, "E4298", {"start": v(34.4, -30.03) * mm, "end": v(34.29, -29.93) * mm});
            skLineSegment(sketch, "E4299", {"start": v(34.29, -29.93) * mm, "end": v(34.2, -29.85) * mm});
            skLineSegment(sketch, "E4300", {"start": v(34.2, -29.85) * mm, "end": v(34.3, -29.73) * mm});
            skLineSegment(sketch, "E4301", {"start": v(34.3, -29.73) * mm, "end": v(34.4, -29.6) * mm});
            skLineSegment(sketch, "E4302", {"start": v(34.4, -29.6) * mm, "end": v(34.5, -29.49) * mm});
            skLineSegment(sketch, "E4303", {"start": v(34.5, -29.49) * mm, "end": v(34.6, -29.36) * mm});
            skLineSegment(sketch, "E4304", {"start": v(34.6, -29.36) * mm, "end": v(34.7, -29.24) * mm});
            skLineSegment(sketch, "E4305", {"start": v(34.7, -29.24) * mm, "end": v(34.8, -29.12) * mm});
            skLineSegment(sketch, "E4306", {"start": v(34.8, -29.12) * mm, "end": v(34.9, -29) * mm});
            skLineSegment(sketch, "E4307", {"start": v(34.9, -29) * mm, "end": v(35, -28.88) * mm});
            skLineSegment(sketch, "E4308", {"start": v(35, -28.88) * mm, "end": v(35.1, -28.76) * mm});
            skLineSegment(sketch, "E4309", {"start": v(35.1, -28.76) * mm, "end": v(35.2, -28.64) * mm});
            skLineSegment(sketch, "E4310", {"start": v(35.2, -28.64) * mm, "end": v(35.3, -28.51) * mm});
            skLineSegment(sketch, "E4311", {"start": v(35.3, -28.51) * mm, "end": v(35.35, -28.45) * mm});
            skLineSegment(sketch, "E4312", {"start": v(35.35, -28.45) * mm, "end": v(35.47, -28.55) * mm});
            skLineSegment(sketch, "E4313", {"start": v(35.47, -28.55) * mm, "end": v(35.6, -28.65) * mm});
            skLineSegment(sketch, "E4314", {"start": v(35.6, -28.65) * mm, "end": v(35.72, -28.75) * mm});
            skLineSegment(sketch, "E4315", {"start": v(35.72, -28.75) * mm, "end": v(35.85, -28.84) * mm});
            skLineSegment(sketch, "E4316", {"start": v(35.85, -28.84) * mm, "end": v(35.97, -28.94) * mm});
            skLineSegment(sketch, "E4317", {"start": v(35.97, -28.94) * mm, "end": v(36.1, -29.04) * mm});
            skLineSegment(sketch, "E4318", {"start": v(36.1, -29.04) * mm, "end": v(36.22, -29.14) * mm});
            skLineSegment(sketch, "E4319", {"start": v(36.22, -29.14) * mm, "end": v(36.34, -29.24) * mm});
            skLineSegment(sketch, "E4320", {"start": v(36.34, -29.24) * mm, "end": v(36.47, -29.34) * mm});
            skLineSegment(sketch, "E4321", {"start": v(36.47, -29.34) * mm, "end": v(36.6, -29.43) * mm});
            skLineSegment(sketch, "E4322", {"start": v(36.6, -29.43) * mm, "end": v(36.72, -29.53) * mm});
            skLineSegment(sketch, "E4323", {"start": v(36.72, -29.53) * mm, "end": v(36.84, -29.63) * mm});
            skLineSegment(sketch, "E4324", {"start": v(36.84, -29.63) * mm, "end": v(36.98, -29.73) * mm});
            skLineSegment(sketch, "E4325", {"start": v(36.98, -29.73) * mm, "end": v(37.12, -29.8) * mm});
            skLineSegment(sketch, "E4326", {"start": v(37.12, -29.8) * mm, "end": v(37.28, -29.84) * mm});
            skLineSegment(sketch, "E4327", {"start": v(37.28, -29.84) * mm, "end": v(37.45, -29.84) * mm});
            skLineSegment(sketch, "E4328", {"start": v(37.45, -29.84) * mm, "end": v(37.6, -29.79) * mm});
            skLineSegment(sketch, "E4329", {"start": v(37.6, -29.79) * mm, "end": v(37.74, -29.7) * mm});
            skLineSegment(sketch, "E4330", {"start": v(37.74, -29.7) * mm, "end": v(37.85, -29.57) * mm});
            skLineSegment(sketch, "E4331", {"start": v(37.85, -29.57) * mm, "end": v(37.92, -29.43) * mm});
            skLineSegment(sketch, "E4332", {"start": v(37.92, -29.43) * mm, "end": v(37.96, -29.27) * mm});
            skLineSegment(sketch, "E4333", {"start": v(37.96, -29.27) * mm, "end": v(37.95, -29.1) * mm});
            skLineSegment(sketch, "E4334", {"start": v(37.95, -29.1) * mm, "end": v(37.9, -28.95) * mm});
            skLineSegment(sketch, "E4335", {"start": v(37.9, -28.95) * mm, "end": v(37.8, -28.81) * mm});
            skLineSegment(sketch, "E4336", {"start": v(37.8, -28.81) * mm, "end": v(37.69, -28.7) * mm});
            skLineSegment(sketch, "E4337", {"start": v(37.69, -28.7) * mm, "end": v(37.56, -28.61) * mm});
            skLineSegment(sketch, "E4338", {"start": v(37.56, -28.61) * mm, "end": v(37.44, -28.52) * mm});
            skLineSegment(sketch, "E4339", {"start": v(37.44, -28.52) * mm, "end": v(37.31, -28.42) * mm});
            skLineSegment(sketch, "E4340", {"start": v(37.31, -28.42) * mm, "end": v(37.19, -28.33) * mm});
            skLineSegment(sketch, "E4341", {"start": v(37.19, -28.33) * mm, "end": v(37.06, -28.23) * mm});
            skLineSegment(sketch, "E4342", {"start": v(37.06, -28.23) * mm, "end": v(36.93, -28.14) * mm});
            skLineSegment(sketch, "E4343", {"start": v(36.93, -28.14) * mm, "end": v(36.8, -28.05) * mm});
            skLineSegment(sketch, "E4344", {"start": v(36.8, -28.05) * mm, "end": v(36.68, -27.95) * mm});
            skLineSegment(sketch, "E4345", {"start": v(36.68, -27.95) * mm, "end": v(36.55, -27.85) * mm});
            skLineSegment(sketch, "E4346", {"start": v(36.55, -27.85) * mm, "end": v(36.42, -27.76) * mm});
            skLineSegment(sketch, "E4347", {"start": v(36.42, -27.76) * mm, "end": v(36.3, -27.66) * mm});
            skLineSegment(sketch, "E4348", {"start": v(36.3, -27.66) * mm, "end": v(36.17, -27.57) * mm});
            skLineSegment(sketch, "E4349", {"start": v(36.17, -27.57) * mm, "end": v(36.08, -27.5) * mm});
            skLineSegment(sketch, "E4350", {"start": v(36.08, -27.5) * mm, "end": v(36.17, -27.37) * mm});
            skLineSegment(sketch, "E4351", {"start": v(36.17, -27.37) * mm, "end": v(36.26, -27.25) * mm});
            skLineSegment(sketch, "E4352", {"start": v(36.26, -27.25) * mm, "end": v(36.35, -27.12) * mm});
            skLineSegment(sketch, "E4353", {"start": v(36.35, -27.12) * mm, "end": v(36.44, -26.99) * mm});
            skLineSegment(sketch, "E4354", {"start": v(36.44, -26.99) * mm, "end": v(36.54, -26.86) * mm});
            skLineSegment(sketch, "E4355", {"start": v(36.54, -26.86) * mm, "end": v(36.63, -26.73) * mm});
            skLineSegment(sketch, "E4356", {"start": v(36.63, -26.73) * mm, "end": v(36.72, -26.6) * mm});
            skLineSegment(sketch, "E4357", {"start": v(36.72, -26.6) * mm, "end": v(36.8, -26.48) * mm});
            skLineSegment(sketch, "E4358", {"start": v(36.8, -26.48) * mm, "end": v(36.9, -26.35) * mm});
            skLineSegment(sketch, "E4359", {"start": v(36.9, -26.35) * mm, "end": v(37, -26.22) * mm});
            skLineSegment(sketch, "E4360", {"start": v(37, -26.22) * mm, "end": v(37.08, -26.1) * mm});
            skLineSegment(sketch, "E4361", {"start": v(37.08, -26.1) * mm, "end": v(37.13, -26.03) * mm});
            skLineSegment(sketch, "E4362", {"start": v(37.13, -26.03) * mm, "end": v(37.26, -26.12) * mm});
            skLineSegment(sketch, "E4363", {"start": v(37.26, -26.12) * mm, "end": v(37.4, -26.2) * mm});
            skLineSegment(sketch, "E4364", {"start": v(37.4, -26.2) * mm, "end": v(37.52, -26.3) * mm});
            skLineSegment(sketch, "E4365", {"start": v(37.52, -26.3) * mm, "end": v(37.65, -26.39) * mm});
            skLineSegment(sketch, "E4366", {"start": v(37.65, -26.39) * mm, "end": v(37.78, -26.48) * mm});
            skLineSegment(sketch, "E4367", {"start": v(37.78, -26.48) * mm, "end": v(37.92, -26.57) * mm});
            skLineSegment(sketch, "E4368", {"start": v(37.92, -26.57) * mm, "end": v(38.05, -26.66) * mm});
            skLineSegment(sketch, "E4369", {"start": v(38.05, -26.66) * mm, "end": v(38.18, -26.75) * mm});
            skLineSegment(sketch, "E4370", {"start": v(38.18, -26.75) * mm, "end": v(38.3, -26.84) * mm});
            skLineSegment(sketch, "E4371", {"start": v(38.3, -26.84) * mm, "end": v(38.44, -26.93) * mm});
            skLineSegment(sketch, "E4372", {"start": v(38.44, -26.93) * mm, "end": v(38.57, -27.02) * mm});
            skLineSegment(sketch, "E4373", {"start": v(38.57, -27.02) * mm, "end": v(38.7, -27.1) * mm});
            skLineSegment(sketch, "E4374", {"start": v(38.7, -27.1) * mm, "end": v(38.84, -27.2) * mm});
            skLineSegment(sketch, "E4375", {"start": v(38.84, -27.2) * mm, "end": v(39, -27.27) * mm});
            skLineSegment(sketch, "E4376", {"start": v(39, -27.27) * mm, "end": v(39.15, -27.3) * mm});
            skLineSegment(sketch, "E4377", {"start": v(39.15, -27.3) * mm, "end": v(39.32, -27.27) * mm});
            skLineSegment(sketch, "E4378", {"start": v(39.32, -27.27) * mm, "end": v(39.47, -27.21) * mm});
            skLineSegment(sketch, "E4379", {"start": v(39.47, -27.21) * mm, "end": v(39.6, -27.12) * mm});
            skLineSegment(sketch, "E4380", {"start": v(39.6, -27.12) * mm, "end": v(39.7, -26.99) * mm});
            skLineSegment(sketch, "E4381", {"start": v(39.7, -26.99) * mm, "end": v(39.77, -26.84) * mm});
            skLineSegment(sketch, "E4382", {"start": v(39.77, -26.84) * mm, "end": v(39.79, -26.67) * mm});
            skLineSegment(sketch, "E4383", {"start": v(39.79, -26.67) * mm, "end": v(39.77, -26.51) * mm});
            skLineSegment(sketch, "E4384", {"start": v(39.77, -26.51) * mm, "end": v(39.7, -26.36) * mm});
            skLineSegment(sketch, "E4385", {"start": v(39.7, -26.36) * mm, "end": v(39.6, -26.23) * mm});
            skLineSegment(sketch, "E4386", {"start": v(39.6, -26.23) * mm, "end": v(39.48, -26.13) * mm});
            skLineSegment(sketch, "E4387", {"start": v(39.48, -26.13) * mm, "end": v(39.35, -26.05) * mm});
            skLineSegment(sketch, "E4388", {"start": v(39.35, -26.05) * mm, "end": v(39.22, -25.96) * mm});
            skLineSegment(sketch, "E4389", {"start": v(39.22, -25.96) * mm, "end": v(39.1, -25.87) * mm});
            skLineSegment(sketch, "E4390", {"start": v(39.1, -25.87) * mm, "end": v(38.96, -25.79) * mm});
            skLineSegment(sketch, "E4391", {"start": v(38.96, -25.79) * mm, "end": v(38.82, -25.7) * mm});
            skLineSegment(sketch, "E4392", {"start": v(38.82, -25.7) * mm, "end": v(38.7, -25.62) * mm});
            skLineSegment(sketch, "E4393", {"start": v(38.7, -25.62) * mm, "end": v(38.56, -25.53) * mm});
            skLineSegment(sketch, "E4394", {"start": v(38.56, -25.53) * mm, "end": v(38.42, -25.44) * mm});
            skLineSegment(sketch, "E4395", {"start": v(38.42, -25.44) * mm, "end": v(38.3, -25.36) * mm});
            skLineSegment(sketch, "E4396", {"start": v(38.3, -25.36) * mm, "end": v(38.16, -25.27) * mm});
            skLineSegment(sketch, "E4397", {"start": v(38.16, -25.27) * mm, "end": v(38.03, -25.18) * mm});
            skLineSegment(sketch, "E4398", {"start": v(38.03, -25.18) * mm, "end": v(37.9, -25.1) * mm});
            skLineSegment(sketch, "E4399", {"start": v(37.9, -25.1) * mm, "end": v(37.8, -25.03) * mm});
            skLineSegment(sketch, "E4400", {"start": v(37.8, -25.03) * mm, "end": v(37.88, -24.9) * mm});
            skLineSegment(sketch, "E4401", {"start": v(37.88, -24.9) * mm, "end": v(37.96, -24.77) * mm});
            skLineSegment(sketch, "E4402", {"start": v(37.96, -24.77) * mm, "end": v(38.05, -24.63) * mm});
            skLineSegment(sketch, "E4403", {"start": v(38.05, -24.63) * mm, "end": v(38.13, -24.5) * mm});
            skLineSegment(sketch, "E4404", {"start": v(38.13, -24.5) * mm, "end": v(38.21, -24.37) * mm});
            skLineSegment(sketch, "E4405", {"start": v(38.21, -24.37) * mm, "end": v(38.3, -24.23) * mm});
            skLineSegment(sketch, "E4406", {"start": v(38.3, -24.23) * mm, "end": v(38.38, -24.1) * mm});
            skLineSegment(sketch, "E4407", {"start": v(38.38, -24.1) * mm, "end": v(38.46, -23.97) * mm});
            skLineSegment(sketch, "E4408", {"start": v(38.46, -23.97) * mm, "end": v(38.54, -23.83) * mm});
            skLineSegment(sketch, "E4409", {"start": v(38.54, -23.83) * mm, "end": v(38.63, -23.7) * mm});
            skLineSegment(sketch, "E4410", {"start": v(38.63, -23.7) * mm, "end": v(38.71, -23.56) * mm});
            skLineSegment(sketch, "E4411", {"start": v(38.71, -23.56) * mm, "end": v(38.75, -23.5) * mm});
            skLineSegment(sketch, "E4412", {"start": v(38.75, -23.5) * mm, "end": v(38.89, -23.58) * mm});
            skLineSegment(sketch, "E4413", {"start": v(38.89, -23.58) * mm, "end": v(39.02, -23.66) * mm});
            skLineSegment(sketch, "E4414", {"start": v(39.02, -23.66) * mm, "end": v(39.16, -23.74) * mm});
            skLineSegment(sketch, "E4415", {"start": v(39.16, -23.74) * mm, "end": v(39.3, -23.82) * mm});
            skLineSegment(sketch, "E4416", {"start": v(39.3, -23.82) * mm, "end": v(39.43, -23.9) * mm});
            skLineSegment(sketch, "E4417", {"start": v(39.43, -23.9) * mm, "end": v(39.57, -23.98) * mm});
            skLineSegment(sketch, "E4418", {"start": v(39.57, -23.98) * mm, "end": v(39.7, -24.06) * mm});
            skLineSegment(sketch, "E4419", {"start": v(39.7, -24.06) * mm, "end": v(39.84, -24.14) * mm});
            skLineSegment(sketch, "E4420", {"start": v(39.84, -24.14) * mm, "end": v(39.98, -24.23) * mm});
            skLineSegment(sketch, "E4421", {"start": v(39.98, -24.23) * mm, "end": v(40.12, -24.3) * mm});
            skLineSegment(sketch, "E4422", {"start": v(40.12, -24.3) * mm, "end": v(40.25, -24.39) * mm});
            skLineSegment(sketch, "E4423", {"start": v(40.25, -24.39) * mm, "end": v(40.39, -24.47) * mm});
            skLineSegment(sketch, "E4424", {"start": v(40.39, -24.47) * mm, "end": v(40.54, -24.56) * mm});
            skLineSegment(sketch, "E4425", {"start": v(40.54, -24.56) * mm, "end": v(40.69, -24.61) * mm});
            skLineSegment(sketch, "E4426", {"start": v(40.69, -24.61) * mm, "end": v(40.85, -24.62) * mm});
            skLineSegment(sketch, "E4427", {"start": v(40.85, -24.62) * mm, "end": v(41.01, -24.6) * mm});
            skLineSegment(sketch, "E4428", {"start": v(41.01, -24.6) * mm, "end": v(41.16, -24.53) * mm});
            skLineSegment(sketch, "E4429", {"start": v(41.16, -24.53) * mm, "end": v(41.29, -24.42) * mm});
            skLineSegment(sketch, "E4430", {"start": v(41.29, -24.42) * mm, "end": v(41.38, -24.28) * mm});
            skLineSegment(sketch, "E4431", {"start": v(41.38, -24.28) * mm, "end": v(41.43, -24.13) * mm});
            skLineSegment(sketch, "E4432", {"start": v(41.43, -24.13) * mm, "end": v(41.45, -23.97) * mm});
            skLineSegment(sketch, "E4433", {"start": v(41.45, -23.97) * mm, "end": v(41.42, -23.8) * mm});
            skLineSegment(sketch, "E4434", {"start": v(41.42, -23.8) * mm, "end": v(41.35, -23.66) * mm});
            skLineSegment(sketch, "E4435", {"start": v(41.35, -23.66) * mm, "end": v(41.24, -23.53) * mm});
            skLineSegment(sketch, "E4436", {"start": v(41.24, -23.53) * mm, "end": v(41.1, -23.45) * mm});
            skLineSegment(sketch, "E4437", {"start": v(41.1, -23.45) * mm, "end": v(40.97, -23.37) * mm});
            skLineSegment(sketch, "E4438", {"start": v(40.97, -23.37) * mm, "end": v(40.84, -23.3) * mm});
            skLineSegment(sketch, "E4439", {"start": v(40.84, -23.3) * mm, "end": v(40.7, -23.21) * mm});
            skLineSegment(sketch, "E4440", {"start": v(40.7, -23.21) * mm, "end": v(40.56, -23.14) * mm});
            skLineSegment(sketch, "E4441", {"start": v(40.56, -23.14) * mm, "end": v(40.42, -23.06) * mm});
            skLineSegment(sketch, "E4442", {"start": v(40.42, -23.06) * mm, "end": v(40.28, -22.98) * mm});
            skLineSegment(sketch, "E4443", {"start": v(40.28, -22.98) * mm, "end": v(40.15, -22.9) * mm});
            skLineSegment(sketch, "E4444", {"start": v(40.15, -22.9) * mm, "end": v(40, -22.83) * mm});
            skLineSegment(sketch, "E4445", {"start": v(40, -22.83) * mm, "end": v(39.87, -22.75) * mm});
            skLineSegment(sketch, "E4446", {"start": v(39.87, -22.75) * mm, "end": v(39.73, -22.67) * mm});
            skLineSegment(sketch, "E4447", {"start": v(39.73, -22.67) * mm, "end": v(39.59, -22.6) * mm});
            skLineSegment(sketch, "E4448", {"start": v(39.59, -22.6) * mm, "end": v(39.45, -22.52) * mm});
            skLineSegment(sketch, "E4449", {"start": v(39.45, -22.52) * mm, "end": v(39.35, -22.46) * mm});
            skLineSegment(sketch, "E4450", {"start": v(39.35, -22.46) * mm, "end": v(39.43, -22.32) * mm});
            skLineSegment(sketch, "E4451", {"start": v(39.43, -22.32) * mm, "end": v(39.5, -22.18) * mm});
            skLineSegment(sketch, "E4452", {"start": v(39.5, -22.18) * mm, "end": v(39.57, -22.04) * mm});
            skLineSegment(sketch, "E4453", {"start": v(39.57, -22.04) * mm, "end": v(39.65, -21.9) * mm});
            skLineSegment(sketch, "E4454", {"start": v(39.65, -21.9) * mm, "end": v(39.72, -21.77) * mm});
            skLineSegment(sketch, "E4455", {"start": v(39.72, -21.77) * mm, "end": v(39.8, -21.63) * mm});
            skLineSegment(sketch, "E4456", {"start": v(39.8, -21.63) * mm, "end": v(39.87, -21.49) * mm});
            skLineSegment(sketch, "E4457", {"start": v(39.87, -21.49) * mm, "end": v(39.94, -21.35) * mm});
            skLineSegment(sketch, "E4458", {"start": v(39.94, -21.35) * mm, "end": v(40.02, -21.21) * mm});
            skLineSegment(sketch, "E4459", {"start": v(40.02, -21.21) * mm, "end": v(40.1, -21.07) * mm});
            skLineSegment(sketch, "E4460", {"start": v(40.1, -21.07) * mm, "end": v(40.17, -20.93) * mm});
            skLineSegment(sketch, "E4461", {"start": v(40.17, -20.93) * mm, "end": v(40.2, -20.86) * mm});
            skLineSegment(sketch, "E4462", {"start": v(40.2, -20.86) * mm, "end": v(40.35, -20.93) * mm});
            skLineSegment(sketch, "E4463", {"start": v(40.35, -20.93) * mm, "end": v(40.49, -21) * mm});
            skLineSegment(sketch, "E4464", {"start": v(40.49, -21) * mm, "end": v(40.63, -21.08) * mm});
            skLineSegment(sketch, "E4465", {"start": v(40.63, -21.08) * mm, "end": v(40.77, -21.15) * mm});
            skLineSegment(sketch, "E4466", {"start": v(40.77, -21.15) * mm, "end": v(40.9, -21.22) * mm});
            skLineSegment(sketch, "E4467", {"start": v(40.9, -21.22) * mm, "end": v(41.05, -21.3) * mm});
            skLineSegment(sketch, "E4468", {"start": v(41.05, -21.3) * mm, "end": v(41.2, -21.37) * mm});
            skLineSegment(sketch, "E4469", {"start": v(41.2, -21.37) * mm, "end": v(41.33, -21.44) * mm});
            skLineSegment(sketch, "E4470", {"start": v(41.33, -21.44) * mm, "end": v(41.48, -21.51) * mm});
            skLineSegment(sketch, "E4471", {"start": v(41.48, -21.51) * mm, "end": v(41.62, -21.58) * mm});
            skLineSegment(sketch, "E4472", {"start": v(41.62, -21.58) * mm, "end": v(41.76, -21.65) * mm});
            skLineSegment(sketch, "E4473", {"start": v(41.76, -21.65) * mm, "end": v(41.9, -21.73) * mm});
            skLineSegment(sketch, "E4474", {"start": v(41.9, -21.73) * mm, "end": v(42.05, -21.8) * mm});
            skLineSegment(sketch, "E4475", {"start": v(42.05, -21.8) * mm, "end": v(42.21, -21.85) * mm});
            skLineSegment(sketch, "E4476", {"start": v(42.21, -21.85) * mm, "end": v(42.37, -21.85) * mm});
            skLineSegment(sketch, "E4477", {"start": v(42.37, -21.85) * mm, "end": v(42.53, -21.81) * mm});
            skLineSegment(sketch, "E4478", {"start": v(42.53, -21.81) * mm, "end": v(42.68, -21.73) * mm});
            skLineSegment(sketch, "E4479", {"start": v(42.68, -21.73) * mm, "end": v(42.8, -21.62) * mm});
            skLineSegment(sketch, "E4480", {"start": v(42.8, -21.62) * mm, "end": v(42.88, -21.48) * mm});
            skLineSegment(sketch, "E4481", {"start": v(42.88, -21.48) * mm, "end": v(42.92, -21.32) * mm});
            skLineSegment(sketch, "E4482", {"start": v(42.92, -21.32) * mm, "end": v(42.92, -21.16) * mm});
            skLineSegment(sketch, "E4483", {"start": v(42.92, -21.16) * mm, "end": v(42.88, -21) * mm});
            skLineSegment(sketch, "E4484", {"start": v(42.88, -21) * mm, "end": v(42.8, -20.85) * mm});
            skLineSegment(sketch, "E4485", {"start": v(42.8, -20.85) * mm, "end": v(42.69, -20.74) * mm});
            skLineSegment(sketch, "E4486", {"start": v(42.69, -20.74) * mm, "end": v(42.55, -20.66) * mm});
            skLineSegment(sketch, "E4487", {"start": v(42.55, -20.66) * mm, "end": v(42.41, -20.59) * mm});
            skLineSegment(sketch, "E4488", {"start": v(42.41, -20.59) * mm, "end": v(42.27, -20.52) * mm});
            skLineSegment(sketch, "E4489", {"start": v(42.27, -20.52) * mm, "end": v(42.13, -20.45) * mm});
            skLineSegment(sketch, "E4490", {"start": v(42.13, -20.45) * mm, "end": v(41.99, -20.39) * mm});
            skLineSegment(sketch, "E4491", {"start": v(41.99, -20.39) * mm, "end": v(41.84, -20.32) * mm});
            skLineSegment(sketch, "E4492", {"start": v(41.84, -20.32) * mm, "end": v(41.7, -20.25) * mm});
            skLineSegment(sketch, "E4493", {"start": v(41.7, -20.25) * mm, "end": v(41.56, -20.18) * mm});
            skLineSegment(sketch, "E4494", {"start": v(41.56, -20.18) * mm, "end": v(41.41, -20.11) * mm});
            skLineSegment(sketch, "E4495", {"start": v(41.41, -20.11) * mm, "end": v(41.27, -20.04) * mm});
            skLineSegment(sketch, "E4496", {"start": v(41.27, -20.04) * mm, "end": v(41.13, -19.98) * mm});
            skLineSegment(sketch, "E4497", {"start": v(41.13, -19.98) * mm, "end": v(40.98, -19.9) * mm});
            skLineSegment(sketch, "E4498", {"start": v(40.98, -19.9) * mm, "end": v(40.84, -19.84) * mm});
            skLineSegment(sketch, "E4499", {"start": v(40.84, -19.84) * mm, "end": v(40.73, -19.79) * mm});
            skLineSegment(sketch, "E4500", {"start": v(40.73, -19.79) * mm, "end": v(40.8, -19.65) * mm});
            skLineSegment(sketch, "E4501", {"start": v(40.8, -19.65) * mm, "end": v(40.86, -19.5) * mm});
            skLineSegment(sketch, "E4502", {"start": v(40.86, -19.5) * mm, "end": v(40.93, -19.36) * mm});
            skLineSegment(sketch, "E4503", {"start": v(40.93, -19.36) * mm, "end": v(41, -19.22) * mm});
            skLineSegment(sketch, "E4504", {"start": v(41, -19.22) * mm, "end": v(41.06, -19.07) * mm});
            skLineSegment(sketch, "E4505", {"start": v(41.06, -19.07) * mm, "end": v(41.12, -18.93) * mm});
            skLineSegment(sketch, "E4506", {"start": v(41.12, -18.93) * mm, "end": v(41.19, -18.79) * mm});
            skLineSegment(sketch, "E4507", {"start": v(41.19, -18.79) * mm, "end": v(41.25, -18.64) * mm});
            skLineSegment(sketch, "E4508", {"start": v(41.25, -18.64) * mm, "end": v(41.32, -18.5) * mm});
            skLineSegment(sketch, "E4509", {"start": v(41.32, -18.5) * mm, "end": v(41.38, -18.36) * mm});
            skLineSegment(sketch, "E4510", {"start": v(41.38, -18.36) * mm, "end": v(41.45, -18.21) * mm});
            skLineSegment(sketch, "E4511", {"start": v(41.45, -18.21) * mm, "end": v(41.48, -18.14) * mm});
            skLineSegment(sketch, "E4512", {"start": v(41.48, -18.14) * mm, "end": v(41.63, -18.2) * mm});
            skLineSegment(sketch, "E4513", {"start": v(41.63, -18.2) * mm, "end": v(41.77, -18.26) * mm});
            skLineSegment(sketch, "E4514", {"start": v(41.77, -18.26) * mm, "end": v(41.92, -18.33) * mm});
            skLineSegment(sketch, "E4515", {"start": v(41.92, -18.33) * mm, "end": v(42.06, -18.39) * mm});
            skLineSegment(sketch, "E4516", {"start": v(42.06, -18.39) * mm, "end": v(42.2, -18.45) * mm});
            skLineSegment(sketch, "E4517", {"start": v(42.2, -18.45) * mm, "end": v(42.36, -18.52) * mm});
            skLineSegment(sketch, "E4518", {"start": v(42.36, -18.52) * mm, "end": v(42.5, -18.58) * mm});
            skLineSegment(sketch, "E4519", {"start": v(42.5, -18.58) * mm, "end": v(42.65, -18.64) * mm});
            skLineSegment(sketch, "E4520", {"start": v(42.65, -18.64) * mm, "end": v(42.8, -18.7) * mm});
            skLineSegment(sketch, "E4521", {"start": v(42.8, -18.7) * mm, "end": v(42.94, -18.77) * mm});
            skLineSegment(sketch, "E4522", {"start": v(42.94, -18.77) * mm, "end": v(43.08, -18.83) * mm});
            skLineSegment(sketch, "E4523", {"start": v(43.08, -18.83) * mm, "end": v(43.23, -18.9) * mm});
            skLineSegment(sketch, "E4524", {"start": v(43.23, -18.9) * mm, "end": v(43.39, -18.96) * mm});
            skLineSegment(sketch, "E4525", {"start": v(43.39, -18.96) * mm, "end": v(43.55, -19) * mm});
            skLineSegment(sketch, "E4526", {"start": v(43.55, -19) * mm, "end": v(43.71, -18.98) * mm});
            skLineSegment(sketch, "E4527", {"start": v(43.71, -18.98) * mm, "end": v(43.87, -18.93) * mm});
            skLineSegment(sketch, "E4528", {"start": v(43.87, -18.93) * mm, "end": v(44, -18.85) * mm});
            skLineSegment(sketch, "E4529", {"start": v(44, -18.85) * mm, "end": v(44.11, -18.72) * mm});
            skLineSegment(sketch, "E4530", {"start": v(44.11, -18.72) * mm, "end": v(44.19, -18.58) * mm});
            skLineSegment(sketch, "E4531", {"start": v(44.19, -18.58) * mm, "end": v(44.22, -18.42) * mm});
            skLineSegment(sketch, "E4532", {"start": v(44.22, -18.42) * mm, "end": v(44.21, -18.25) * mm});
            skLineSegment(sketch, "E4533", {"start": v(44.21, -18.25) * mm, "end": v(44.16, -18.1) * mm});
            skLineSegment(sketch, "E4534", {"start": v(44.16, -18.1) * mm, "end": v(44.07, -17.96) * mm});
            skLineSegment(sketch, "E4535", {"start": v(44.07, -17.96) * mm, "end": v(43.95, -17.85) * mm});
            skLineSegment(sketch, "E4536", {"start": v(43.95, -17.85) * mm, "end": v(43.8, -17.78) * mm});
            skLineSegment(sketch, "E4537", {"start": v(43.8, -17.78) * mm, "end": v(43.66, -17.72) * mm});
            skLineSegment(sketch, "E4538", {"start": v(43.66, -17.72) * mm, "end": v(43.52, -17.66) * mm});
            skLineSegment(sketch, "E4539", {"start": v(43.52, -17.66) * mm, "end": v(43.37, -17.6) * mm});
            skLineSegment(sketch, "E4540", {"start": v(43.37, -17.6) * mm, "end": v(43.23, -17.55) * mm});
            skLineSegment(sketch, "E4541", {"start": v(43.23, -17.55) * mm, "end": v(43.08, -17.49) * mm});
            skLineSegment(sketch, "E4542", {"start": v(43.08, -17.49) * mm, "end": v(42.93, -17.43) * mm});
            skLineSegment(sketch, "E4543", {"start": v(42.93, -17.43) * mm, "end": v(42.79, -17.37) * mm});
            skLineSegment(sketch, "E4544", {"start": v(42.79, -17.37) * mm, "end": v(42.64, -17.31) * mm});
            skLineSegment(sketch, "E4545", {"start": v(42.64, -17.31) * mm, "end": v(42.49, -17.25) * mm});
            skLineSegment(sketch, "E4546", {"start": v(42.49, -17.25) * mm, "end": v(42.34, -17.2) * mm});
            skLineSegment(sketch, "E4547", {"start": v(42.34, -17.2) * mm, "end": v(42.2, -17.13) * mm});
            skLineSegment(sketch, "E4548", {"start": v(42.2, -17.13) * mm, "end": v(42.05, -17.08) * mm});
            skLineSegment(sketch, "E4549", {"start": v(42.05, -17.08) * mm, "end": v(41.94, -17.03) * mm});
            skLineSegment(sketch, "E4550", {"start": v(41.94, -17.03) * mm, "end": v(42, -16.89) * mm});
            skLineSegment(sketch, "E4551", {"start": v(42, -16.89) * mm, "end": v(42.05, -16.74) * mm});
            skLineSegment(sketch, "E4552", {"start": v(42.05, -16.74) * mm, "end": v(42.1, -16.6) * mm});
            skLineSegment(sketch, "E4553", {"start": v(42.1, -16.6) * mm, "end": v(42.16, -16.44) * mm});
            skLineSegment(sketch, "E4554", {"start": v(42.16, -16.44) * mm, "end": v(42.22, -16.3) * mm});
            skLineSegment(sketch, "E4555", {"start": v(42.22, -16.3) * mm, "end": v(42.27, -16.15) * mm});
            skLineSegment(sketch, "E4556", {"start": v(42.27, -16.15) * mm, "end": v(42.33, -16) * mm});
            skLineSegment(sketch, "E4557", {"start": v(42.33, -16) * mm, "end": v(42.38, -15.86) * mm});
            skLineSegment(sketch, "E4558", {"start": v(42.38, -15.86) * mm, "end": v(42.44, -15.7) * mm});
            skLineSegment(sketch, "E4559", {"start": v(42.44, -15.7) * mm, "end": v(42.5, -15.56) * mm});
            skLineSegment(sketch, "E4560", {"start": v(42.5, -15.56) * mm, "end": v(42.55, -15.41) * mm});
            skLineSegment(sketch, "E4561", {"start": v(42.55, -15.41) * mm, "end": v(42.58, -15.34) * mm});
            skLineSegment(sketch, "E4562", {"start": v(42.58, -15.34) * mm, "end": v(42.73, -15.4) * mm});
            skLineSegment(sketch, "E4563", {"start": v(42.73, -15.4) * mm, "end": v(42.87, -15.44) * mm});
            skLineSegment(sketch, "E4564", {"start": v(42.87, -15.44) * mm, "end": v(43.03, -15.5) * mm});
            skLineSegment(sketch, "E4565", {"start": v(43.03, -15.5) * mm, "end": v(43.17, -15.55) * mm});
            skLineSegment(sketch, "E4566", {"start": v(43.17, -15.55) * mm, "end": v(43.32, -15.6) * mm});
            skLineSegment(sketch, "E4567", {"start": v(43.32, -15.6) * mm, "end": v(43.48, -15.66) * mm});
            skLineSegment(sketch, "E4568", {"start": v(43.48, -15.66) * mm, "end": v(43.62, -15.7) * mm});
            skLineSegment(sketch, "E4569", {"start": v(43.62, -15.7) * mm, "end": v(43.77, -15.76) * mm});
            skLineSegment(sketch, "E4570", {"start": v(43.77, -15.76) * mm, "end": v(43.92, -15.82) * mm});
            skLineSegment(sketch, "E4571", {"start": v(43.92, -15.82) * mm, "end": v(44.07, -15.87) * mm});
            skLineSegment(sketch, "E4572", {"start": v(44.07, -15.87) * mm, "end": v(44.22, -15.92) * mm});
            skLineSegment(sketch, "E4573", {"start": v(44.22, -15.92) * mm, "end": v(44.37, -15.97) * mm});
            skLineSegment(sketch, "E4574", {"start": v(44.37, -15.97) * mm, "end": v(44.53, -16.03) * mm});
            skLineSegment(sketch, "E4575", {"start": v(44.53, -16.03) * mm, "end": v(44.7, -16.05) * mm});
            skLineSegment(sketch, "E4576", {"start": v(44.7, -16.05) * mm, "end": v(44.86, -16.04) * mm});
            skLineSegment(sketch, "E4577", {"start": v(44.86, -16.04) * mm, "end": v(45.01, -15.98) * mm});
            skLineSegment(sketch, "E4578", {"start": v(45.01, -15.98) * mm, "end": v(45.14, -15.88) * mm});
            skLineSegment(sketch, "E4579", {"start": v(45.14, -15.88) * mm, "end": v(45.24, -15.75) * mm});
            skLineSegment(sketch, "E4580", {"start": v(45.24, -15.75) * mm, "end": v(45.3, -15.6) * mm});
            skLineSegment(sketch, "E4581", {"start": v(45.3, -15.6) * mm, "end": v(45.33, -15.44) * mm});
            skLineSegment(sketch, "E4582", {"start": v(45.33, -15.44) * mm, "end": v(45.31, -15.27) * mm});
            skLineSegment(sketch, "E4583", {"start": v(45.31, -15.27) * mm, "end": v(45.25, -15.12) * mm});
            skLineSegment(sketch, "E4584", {"start": v(45.25, -15.12) * mm, "end": v(45.15, -15) * mm});
            skLineSegment(sketch, "E4585", {"start": v(45.15, -15) * mm, "end": v(45.02, -14.9) * mm});
            skLineSegment(sketch, "E4586", {"start": v(45.02, -14.9) * mm, "end": v(44.88, -14.83) * mm});
            skLineSegment(sketch, "E4587", {"start": v(44.88, -14.83) * mm, "end": v(44.73, -14.78) * mm});
            skLineSegment(sketch, "E4588", {"start": v(44.73, -14.78) * mm, "end": v(44.58, -14.73) * mm});
            skLineSegment(sketch, "E4589", {"start": v(44.58, -14.73) * mm, "end": v(44.43, -14.68) * mm});
            skLineSegment(sketch, "E4590", {"start": v(44.43, -14.68) * mm, "end": v(44.28, -14.63) * mm});
            skLineSegment(sketch, "E4591", {"start": v(44.28, -14.63) * mm, "end": v(44.13, -14.58) * mm});
            skLineSegment(sketch, "E4592", {"start": v(44.13, -14.58) * mm, "end": v(43.98, -14.54) * mm});
            skLineSegment(sketch, "E4593", {"start": v(43.98, -14.54) * mm, "end": v(43.83, -14.49) * mm});
            skLineSegment(sketch, "E4594", {"start": v(43.83, -14.49) * mm, "end": v(43.67, -14.44) * mm});
            skLineSegment(sketch, "E4595", {"start": v(43.67, -14.44) * mm, "end": v(43.52, -14.39) * mm});
            skLineSegment(sketch, "E4596", {"start": v(43.52, -14.39) * mm, "end": v(43.38, -14.34) * mm});
            skLineSegment(sketch, "E4597", {"start": v(43.38, -14.34) * mm, "end": v(43.22, -14.29) * mm});
            skLineSegment(sketch, "E4598", {"start": v(43.22, -14.29) * mm, "end": v(43.07, -14.24) * mm});
            skLineSegment(sketch, "E4599", {"start": v(43.07, -14.24) * mm, "end": v(42.96, -14.2) * mm});
            skLineSegment(sketch, "E4600", {"start": v(42.96, -14.2) * mm, "end": v(43, -14.05) * mm});
            skLineSegment(sketch, "E4601", {"start": v(43, -14.05) * mm, "end": v(43.05, -13.9) * mm});
            skLineSegment(sketch, "E4602", {"start": v(43.05, -13.9) * mm, "end": v(43.1, -13.75) * mm});
            skLineSegment(sketch, "E4603", {"start": v(43.1, -13.75) * mm, "end": v(43.15, -13.6) * mm});
            skLineSegment(sketch, "E4604", {"start": v(43.15, -13.6) * mm, "end": v(43.2, -13.45) * mm});
            skLineSegment(sketch, "E4605", {"start": v(43.2, -13.45) * mm, "end": v(43.24, -13.3) * mm});
            skLineSegment(sketch, "E4606", {"start": v(43.24, -13.3) * mm, "end": v(43.28, -13.15) * mm});
            skLineSegment(sketch, "E4607", {"start": v(43.28, -13.15) * mm, "end": v(43.33, -13) * mm});
            skLineSegment(sketch, "E4608", {"start": v(43.33, -13) * mm, "end": v(43.37, -12.85) * mm});
            skLineSegment(sketch, "E4609", {"start": v(43.37, -12.85) * mm, "end": v(43.42, -12.7) * mm});
            skLineSegment(sketch, "E4610", {"start": v(43.42, -12.7) * mm, "end": v(43.46, -12.55) * mm});
            skLineSegment(sketch, "E4611", {"start": v(43.46, -12.55) * mm, "end": v(43.49, -12.47) * mm});
            skLineSegment(sketch, "E4612", {"start": v(43.49, -12.47) * mm, "end": v(43.64, -12.52) * mm});
            skLineSegment(sketch, "E4613", {"start": v(43.64, -12.52) * mm, "end": v(43.8, -12.56) * mm});
            skLineSegment(sketch, "E4614", {"start": v(43.8, -12.56) * mm, "end": v(43.95, -12.6) * mm});
            skLineSegment(sketch, "E4615", {"start": v(43.95, -12.6) * mm, "end": v(44.1, -12.64) * mm});
            skLineSegment(sketch, "E4616", {"start": v(44.1, -12.64) * mm, "end": v(44.25, -12.69) * mm});
            skLineSegment(sketch, "E4617", {"start": v(44.25, -12.69) * mm, "end": v(44.4, -12.73) * mm});
            skLineSegment(sketch, "E4618", {"start": v(44.4, -12.73) * mm, "end": v(44.56, -12.77) * mm});
            skLineSegment(sketch, "E4619", {"start": v(44.56, -12.77) * mm, "end": v(44.7, -12.82) * mm});
            skLineSegment(sketch, "E4620", {"start": v(44.7, -12.82) * mm, "end": v(44.86, -12.86) * mm});
            skLineSegment(sketch, "E4621", {"start": v(44.86, -12.86) * mm, "end": v(45.01, -12.9) * mm});
            skLineSegment(sketch, "E4622", {"start": v(45.01, -12.9) * mm, "end": v(45.17, -12.95) * mm});
            skLineSegment(sketch, "E4623", {"start": v(45.17, -12.95) * mm, "end": v(45.32, -12.99) * mm});
            skLineSegment(sketch, "E4624", {"start": v(45.32, -12.99) * mm, "end": v(45.48, -13.03) * mm});
            skLineSegment(sketch, "E4625", {"start": v(45.48, -13.03) * mm, "end": v(45.65, -13.05) * mm});
            skLineSegment(sketch, "E4626", {"start": v(45.65, -13.05) * mm, "end": v(45.8, -13.02) * mm});
            skLineSegment(sketch, "E4627", {"start": v(45.8, -13.02) * mm, "end": v(45.96, -12.95) * mm});
            skLineSegment(sketch, "E4628", {"start": v(45.96, -12.95) * mm, "end": v(46.08, -12.84) * mm});
            skLineSegment(sketch, "E4629", {"start": v(46.08, -12.84) * mm, "end": v(46.17, -12.7) * mm});
            skLineSegment(sketch, "E4630", {"start": v(46.17, -12.7) * mm, "end": v(46.23, -12.55) * mm});
            skLineSegment(sketch, "E4631", {"start": v(46.23, -12.55) * mm, "end": v(46.24, -12.4) * mm});
            skLineSegment(sketch, "E4632", {"start": v(46.24, -12.4) * mm, "end": v(46.21, -12.23) * mm});
            skLineSegment(sketch, "E4633", {"start": v(46.21, -12.23) * mm, "end": v(46.14, -12.08) * mm});
            skLineSegment(sketch, "E4634", {"start": v(46.14, -12.08) * mm, "end": v(46.03, -11.96) * mm});
            skLineSegment(sketch, "E4635", {"start": v(46.03, -11.96) * mm, "end": v(45.9, -11.86) * mm});
            skLineSegment(sketch, "E4636", {"start": v(45.9, -11.86) * mm, "end": v(45.75, -11.82) * mm});
            skLineSegment(sketch, "E4637", {"start": v(45.75, -11.82) * mm, "end": v(45.6, -11.77) * mm});
            skLineSegment(sketch, "E4638", {"start": v(45.6, -11.77) * mm, "end": v(45.45, -11.73) * mm});
            skLineSegment(sketch, "E4639", {"start": v(45.45, -11.73) * mm, "end": v(45.3, -11.7) * mm});
            skLineSegment(sketch, "E4640", {"start": v(45.3, -11.7) * mm, "end": v(45.14, -11.66) * mm});
            skLineSegment(sketch, "E4641", {"start": v(45.14, -11.66) * mm, "end": v(44.98, -11.62) * mm});
            skLineSegment(sketch, "E4642", {"start": v(44.98, -11.62) * mm, "end": v(44.83, -11.58) * mm});
            skLineSegment(sketch, "E4643", {"start": v(44.83, -11.58) * mm, "end": v(44.68, -11.54) * mm});
            skLineSegment(sketch, "E4644", {"start": v(44.68, -11.54) * mm, "end": v(44.52, -11.5) * mm});
            skLineSegment(sketch, "E4645", {"start": v(44.52, -11.5) * mm, "end": v(44.37, -11.46) * mm});
            skLineSegment(sketch, "E4646", {"start": v(44.37, -11.46) * mm, "end": v(44.22, -11.42) * mm});
            skLineSegment(sketch, "E4647", {"start": v(44.22, -11.42) * mm, "end": v(44.06, -11.38) * mm});
            skLineSegment(sketch, "E4648", {"start": v(44.06, -11.38) * mm, "end": v(43.9, -11.34) * mm});
            skLineSegment(sketch, "E4649", {"start": v(43.9, -11.34) * mm, "end": v(43.8, -11.32) * mm});
            skLineSegment(sketch, "E4650", {"start": v(43.8, -11.32) * mm, "end": v(43.83, -11.16) * mm});
            skLineSegment(sketch, "E4651", {"start": v(43.83, -11.16) * mm, "end": v(43.87, -11) * mm});
            skLineSegment(sketch, "E4652", {"start": v(43.87, -11) * mm, "end": v(43.9, -10.86) * mm});
            skLineSegment(sketch, "E4653", {"start": v(43.9, -10.86) * mm, "end": v(43.94, -10.7) * mm});
            skLineSegment(sketch, "E4654", {"start": v(43.94, -10.7) * mm, "end": v(43.98, -10.55) * mm});
            skLineSegment(sketch, "E4655", {"start": v(43.98, -10.55) * mm, "end": v(44.01, -10.4) * mm});
            skLineSegment(sketch, "E4656", {"start": v(44.01, -10.4) * mm, "end": v(44.05, -10.24) * mm});
            skLineSegment(sketch, "E4657", {"start": v(44.05, -10.24) * mm, "end": v(44.08, -10.1) * mm});
            skLineSegment(sketch, "E4658", {"start": v(44.08, -10.1) * mm, "end": v(44.12, -9.94) * mm});
            skLineSegment(sketch, "E4659", {"start": v(44.12, -9.94) * mm, "end": v(44.16, -9.78) * mm});
            skLineSegment(sketch, "E4660", {"start": v(44.16, -9.78) * mm, "end": v(44.2, -9.63) * mm});
            skLineSegment(sketch, "E4661", {"start": v(44.2, -9.63) * mm, "end": v(44.2, -9.55) * mm});
            skLineSegment(sketch, "E4662", {"start": v(44.2, -9.55) * mm, "end": v(44.36, -9.59) * mm});
            skLineSegment(sketch, "E4663", {"start": v(44.36, -9.59) * mm, "end": v(44.52, -9.62) * mm});
            skLineSegment(sketch, "E4664", {"start": v(44.52, -9.62) * mm, "end": v(44.68, -9.65) * mm});
            skLineSegment(sketch, "E4665", {"start": v(44.68, -9.65) * mm, "end": v(44.83, -9.68) * mm});
            skLineSegment(sketch, "E4666", {"start": v(44.83, -9.68) * mm, "end": v(44.98, -9.72) * mm});
            skLineSegment(sketch, "E4667", {"start": v(44.98, -9.72) * mm, "end": v(45.14, -9.75) * mm});
            skLineSegment(sketch, "E4668", {"start": v(45.14, -9.75) * mm, "end": v(45.3, -9.78) * mm});
            skLineSegment(sketch, "E4669", {"start": v(45.3, -9.78) * mm, "end": v(45.45, -9.82) * mm});
            skLineSegment(sketch, "E4670", {"start": v(45.45, -9.82) * mm, "end": v(45.6, -9.85) * mm});
            skLineSegment(sketch, "E4671", {"start": v(45.6, -9.85) * mm, "end": v(45.76, -9.88) * mm});
            skLineSegment(sketch, "E4672", {"start": v(45.76, -9.88) * mm, "end": v(45.91, -9.92) * mm});
            skLineSegment(sketch, "E4673", {"start": v(45.91, -9.92) * mm, "end": v(46.07, -9.95) * mm});
            skLineSegment(sketch, "E4674", {"start": v(46.07, -9.95) * mm, "end": v(46.24, -9.98) * mm});
            skLineSegment(sketch, "E4675", {"start": v(46.24, -9.98) * mm, "end": v(46.4, -9.99) * mm});
            skLineSegment(sketch, "E4676", {"start": v(46.4, -9.99) * mm, "end": v(46.56, -9.95) * mm});
            skLineSegment(sketch, "E4677", {"start": v(46.56, -9.95) * mm, "end": v(46.7, -9.87) * mm});
            skLineSegment(sketch, "E4678", {"start": v(46.7, -9.87) * mm, "end": v(46.82, -9.75) * mm});
            skLineSegment(sketch, "E4679", {"start": v(46.82, -9.75) * mm, "end": v(46.9, -9.61) * mm});
            skLineSegment(sketch, "E4680", {"start": v(46.9, -9.61) * mm, "end": v(46.95, -9.45) * mm});
            skLineSegment(sketch, "E4681", {"start": v(46.95, -9.45) * mm, "end": v(46.95, -9.3) * mm});
            skLineSegment(sketch, "E4682", {"start": v(46.95, -9.3) * mm, "end": v(46.91, -9.13) * mm});
            skLineSegment(sketch, "E4683", {"start": v(46.91, -9.13) * mm, "end": v(46.83, -8.99) * mm});
            skLineSegment(sketch, "E4684", {"start": v(46.83, -8.99) * mm, "end": v(46.72, -8.87) * mm});
            skLineSegment(sketch, "E4685", {"start": v(46.72, -8.87) * mm, "end": v(46.57, -8.79) * mm});
            skLineSegment(sketch, "E4686", {"start": v(46.57, -8.79) * mm, "end": v(46.42, -8.75) * mm});
            skLineSegment(sketch, "E4687", {"start": v(46.42, -8.75) * mm, "end": v(46.27, -8.72) * mm});
            skLineSegment(sketch, "E4688", {"start": v(46.27, -8.72) * mm, "end": v(46.11, -8.69) * mm});
            skLineSegment(sketch, "E4689", {"start": v(46.11, -8.69) * mm, "end": v(45.96, -8.66) * mm});
            skLineSegment(sketch, "E4690", {"start": v(45.96, -8.66) * mm, "end": v(45.8, -8.63) * mm});
            skLineSegment(sketch, "E4691", {"start": v(45.8, -8.63) * mm, "end": v(45.65, -8.6) * mm});
            skLineSegment(sketch, "E4692", {"start": v(45.65, -8.6) * mm, "end": v(45.5, -8.57) * mm});
            skLineSegment(sketch, "E4693", {"start": v(45.5, -8.57) * mm, "end": v(45.34, -8.54) * mm});
            skLineSegment(sketch, "E4694", {"start": v(45.34, -8.54) * mm, "end": v(45.18, -8.52) * mm});
            skLineSegment(sketch, "E4695", {"start": v(45.18, -8.52) * mm, "end": v(45.02, -8.49) * mm});
            skLineSegment(sketch, "E4696", {"start": v(45.02, -8.49) * mm, "end": v(44.87, -8.46) * mm});
            skLineSegment(sketch, "E4697", {"start": v(44.87, -8.46) * mm, "end": v(44.71, -8.43) * mm});
            skLineSegment(sketch, "E4698", {"start": v(44.71, -8.43) * mm, "end": v(44.56, -8.4) * mm});
            skLineSegment(sketch, "E4699", {"start": v(44.56, -8.4) * mm, "end": v(44.44, -8.38) * mm});
            skLineSegment(sketch, "E4700", {"start": v(44.44, -8.38) * mm, "end": v(44.47, -8.22) * mm});
            skLineSegment(sketch, "E4701", {"start": v(44.47, -8.22) * mm, "end": v(44.5, -8.07) * mm});
            skLineSegment(sketch, "E4702", {"start": v(44.5, -8.07) * mm, "end": v(44.52, -7.91) * mm});
            skLineSegment(sketch, "E4703", {"start": v(44.52, -7.91) * mm, "end": v(44.55, -7.76) * mm});
            skLineSegment(sketch, "E4704", {"start": v(44.55, -7.76) * mm, "end": v(44.57, -7.6) * mm});
            skLineSegment(sketch, "E4705", {"start": v(44.57, -7.6) * mm, "end": v(44.6, -7.45) * mm});
            skLineSegment(sketch, "E4706", {"start": v(44.6, -7.45) * mm, "end": v(44.62, -7.3) * mm});
            skLineSegment(sketch, "E4707", {"start": v(44.62, -7.3) * mm, "end": v(44.65, -7.14) * mm});
            skLineSegment(sketch, "E4708", {"start": v(44.65, -7.14) * mm, "end": v(44.67, -6.98) * mm});
            skLineSegment(sketch, "E4709", {"start": v(44.67, -6.98) * mm, "end": v(44.7, -6.83) * mm});
            skLineSegment(sketch, "E4710", {"start": v(44.7, -6.83) * mm, "end": v(44.72, -6.67) * mm});
            skLineSegment(sketch, "E4711", {"start": v(44.72, -6.67) * mm, "end": v(44.74, -6.6) * mm});
            skLineSegment(sketch, "E4712", {"start": v(44.74, -6.6) * mm, "end": v(44.9, -6.61) * mm});
            skLineSegment(sketch, "E4713", {"start": v(44.9, -6.61) * mm, "end": v(45.05, -6.64) * mm});
            skLineSegment(sketch, "E4714", {"start": v(45.05, -6.64) * mm, "end": v(45.2, -6.66) * mm});
            skLineSegment(sketch, "E4715", {"start": v(45.2, -6.66) * mm, "end": v(45.36, -6.68) * mm});
            skLineSegment(sketch, "E4716", {"start": v(45.36, -6.68) * mm, "end": v(45.52, -6.7) * mm});
            skLineSegment(sketch, "E4717", {"start": v(45.52, -6.7) * mm, "end": v(45.68, -6.73) * mm});
            skLineSegment(sketch, "E4718", {"start": v(45.68, -6.73) * mm, "end": v(45.84, -6.75) * mm});
            skLineSegment(sketch, "E4719", {"start": v(45.84, -6.75) * mm, "end": v(46, -6.77) * mm});
            skLineSegment(sketch, "E4720", {"start": v(46, -6.77) * mm, "end": v(46.15, -6.8) * mm});
            skLineSegment(sketch, "E4721", {"start": v(46.15, -6.8) * mm, "end": v(46.3, -6.82) * mm});
            skLineSegment(sketch, "E4722", {"start": v(46.3, -6.82) * mm, "end": v(46.46, -6.84) * mm});
            skLineSegment(sketch, "E4723", {"start": v(46.46, -6.84) * mm, "end": v(46.62, -6.87) * mm});
            skLineSegment(sketch, "E4724", {"start": v(46.62, -6.87) * mm, "end": v(46.8, -6.89) * mm});
            skLineSegment(sketch, "E4725", {"start": v(46.8, -6.89) * mm, "end": v(46.95, -6.88) * mm});
            skLineSegment(sketch, "E4726", {"start": v(46.95, -6.88) * mm, "end": v(47.1, -6.83) * mm});
            skLineSegment(sketch, "E4727", {"start": v(47.1, -6.83) * mm, "end": v(47.25, -6.74) * mm});
            skLineSegment(sketch, "E4728", {"start": v(47.25, -6.74) * mm, "end": v(47.36, -6.62) * mm});
            skLineSegment(sketch, "E4729", {"start": v(47.36, -6.62) * mm, "end": v(47.43, -6.47) * mm});
            skLineSegment(sketch, "E4730", {"start": v(47.43, -6.47) * mm, "end": v(47.47, -6.31) * mm});
            skLineSegment(sketch, "E4731", {"start": v(47.47, -6.31) * mm, "end": v(47.46, -6.15) * mm});
            skLineSegment(sketch, "E4732", {"start": v(47.46, -6.15) * mm, "end": v(47.4, -6) * mm});
            skLineSegment(sketch, "E4733", {"start": v(47.4, -6) * mm, "end": v(47.32, -5.86) * mm});
            skLineSegment(sketch, "E4734", {"start": v(47.32, -5.86) * mm, "end": v(47.2, -5.75) * mm});
            skLineSegment(sketch, "E4735", {"start": v(47.2, -5.75) * mm, "end": v(47.05, -5.68) * mm});
            skLineSegment(sketch, "E4736", {"start": v(47.05, -5.68) * mm, "end": v(46.9, -5.65) * mm});
            skLineSegment(sketch, "E4737", {"start": v(46.9, -5.65) * mm, "end": v(46.74, -5.62) * mm});
            skLineSegment(sketch, "E4738", {"start": v(46.74, -5.62) * mm, "end": v(46.58, -5.6) * mm});
            skLineSegment(sketch, "E4739", {"start": v(46.58, -5.6) * mm, "end": v(46.43, -5.59) * mm});
            skLineSegment(sketch, "E4740", {"start": v(46.43, -5.59) * mm, "end": v(46.27, -5.57) * mm});
            skLineSegment(sketch, "E4741", {"start": v(46.27, -5.57) * mm, "end": v(46.11, -5.55) * mm});
            skLineSegment(sketch, "E4742", {"start": v(46.11, -5.55) * mm, "end": v(45.95, -5.53) * mm});
            skLineSegment(sketch, "E4743", {"start": v(45.95, -5.53) * mm, "end": v(45.8, -5.51) * mm});
            skLineSegment(sketch, "E4744", {"start": v(45.8, -5.51) * mm, "end": v(45.64, -5.5) * mm});
            skLineSegment(sketch, "E4745", {"start": v(45.64, -5.5) * mm, "end": v(45.48, -5.47) * mm});
            skLineSegment(sketch, "E4746", {"start": v(45.48, -5.47) * mm, "end": v(45.32, -5.46) * mm});
            skLineSegment(sketch, "E4747", {"start": v(45.32, -5.46) * mm, "end": v(45.16, -5.44) * mm});
            skLineSegment(sketch, "E4748", {"start": v(45.16, -5.44) * mm, "end": v(45, -5.42) * mm});
            skLineSegment(sketch, "E4749", {"start": v(45, -5.42) * mm, "end": v(44.9, -5.4) * mm});
            skLineSegment(sketch, "E4750", {"start": v(44.9, -5.4) * mm, "end": v(44.9, -5.25) * mm});
            skLineSegment(sketch, "E4751", {"start": v(44.9, -5.25) * mm, "end": v(44.92, -5.1) * mm});
            skLineSegment(sketch, "E4752", {"start": v(44.92, -5.1) * mm, "end": v(44.94, -4.94) * mm});
            skLineSegment(sketch, "E4753", {"start": v(44.94, -4.94) * mm, "end": v(44.96, -4.78) * mm});
            skLineSegment(sketch, "E4754", {"start": v(44.96, -4.78) * mm, "end": v(44.97, -4.62) * mm});
            skLineSegment(sketch, "E4755", {"start": v(44.97, -4.62) * mm, "end": v(44.99, -4.47) * mm});
            skLineSegment(sketch, "E4756", {"start": v(44.99, -4.47) * mm, "end": v(45, -4.3) * mm});
            skLineSegment(sketch, "E4757", {"start": v(45, -4.3) * mm, "end": v(45.02, -4.15) * mm});
            skLineSegment(sketch, "E4758", {"start": v(45.02, -4.15) * mm, "end": v(45.03, -4) * mm});
            skLineSegment(sketch, "E4759", {"start": v(45.03, -4) * mm, "end": v(45.05, -3.84) * mm});
            skLineSegment(sketch, "E4760", {"start": v(45.05, -3.84) * mm, "end": v(45.06, -3.68) * mm});
            skLineSegment(sketch, "E4761", {"start": v(45.06, -3.68) * mm, "end": v(45.07, -3.6) * mm});
            skLineSegment(sketch, "E4762", {"start": v(45.07, -3.6) * mm, "end": v(45.23, -3.62) * mm});
            skLineSegment(sketch, "E4763", {"start": v(45.23, -3.62) * mm, "end": v(45.39, -3.63) * mm});
            skLineSegment(sketch, "E4764", {"start": v(45.39, -3.63) * mm, "end": v(45.55, -3.64) * mm});
            skLineSegment(sketch, "E4765", {"start": v(45.55, -3.64) * mm, "end": v(45.7, -3.65) * mm});
            skLineSegment(sketch, "E4766", {"start": v(45.7, -3.65) * mm, "end": v(45.86, -3.67) * mm});
            skLineSegment(sketch, "E4767", {"start": v(45.86, -3.67) * mm, "end": v(46.02, -3.68) * mm});
            skLineSegment(sketch, "E4768", {"start": v(46.02, -3.68) * mm, "end": v(46.18, -3.7) * mm});
            skLineSegment(sketch, "E4769", {"start": v(46.18, -3.7) * mm, "end": v(46.33, -3.7) * mm});
            skLineSegment(sketch, "E4770", {"start": v(46.33, -3.7) * mm, "end": v(46.5, -3.72) * mm});
            skLineSegment(sketch, "E4771", {"start": v(46.5, -3.72) * mm, "end": v(46.65, -3.73) * mm});
            skLineSegment(sketch, "E4772", {"start": v(46.65, -3.73) * mm, "end": v(46.8, -3.74) * mm});
            skLineSegment(sketch, "E4773", {"start": v(46.8, -3.74) * mm, "end": v(46.97, -3.75) * mm});
            skLineSegment(sketch, "E4774", {"start": v(46.97, -3.75) * mm, "end": v(47.14, -3.76) * mm});
            skLineSegment(sketch, "E4775", {"start": v(47.14, -3.76) * mm, "end": v(47.3, -3.75) * mm});
            skLineSegment(sketch, "E4776", {"start": v(47.3, -3.75) * mm, "end": v(47.45, -3.69) * mm});
            skLineSegment(sketch, "E4777", {"start": v(47.45, -3.69) * mm, "end": v(47.59, -3.59) * mm});
            skLineSegment(sketch, "E4778", {"start": v(47.59, -3.59) * mm, "end": v(47.69, -3.46) * mm});
            skLineSegment(sketch, "E4779", {"start": v(47.69, -3.46) * mm, "end": v(47.75, -3.3) * mm});
            skLineSegment(sketch, "E4780", {"start": v(47.75, -3.3) * mm, "end": v(47.78, -3.15) * mm});
            skLineSegment(sketch, "E4781", {"start": v(47.78, -3.15) * mm, "end": v(47.76, -2.99) * mm});
            skLineSegment(sketch, "E4782", {"start": v(47.76, -2.99) * mm, "end": v(47.7, -2.83) * mm});
            skLineSegment(sketch, "E4783", {"start": v(47.7, -2.83) * mm, "end": v(47.6, -2.7) * mm});
            skLineSegment(sketch, "E4784", {"start": v(47.6, -2.7) * mm, "end": v(47.47, -2.6) * mm});
            skLineSegment(sketch, "E4785", {"start": v(47.47, -2.6) * mm, "end": v(47.32, -2.54) * mm});
            skLineSegment(sketch, "E4786", {"start": v(47.32, -2.54) * mm, "end": v(47.16, -2.52) * mm});
            skLineSegment(sketch, "E4787", {"start": v(47.16, -2.52) * mm, "end": v(47, -2.5) * mm});
            skLineSegment(sketch, "E4788", {"start": v(47, -2.5) * mm, "end": v(46.85, -2.5) * mm});
            skLineSegment(sketch, "E4789", {"start": v(46.85, -2.5) * mm, "end": v(46.7, -2.49) * mm});
            skLineSegment(sketch, "E4790", {"start": v(46.7, -2.49) * mm, "end": v(46.53, -2.48) * mm});
            skLineSegment(sketch, "E4791", {"start": v(46.53, -2.48) * mm, "end": v(46.37, -2.47) * mm});
            skLineSegment(sketch, "E4792", {"start": v(46.37, -2.47) * mm, "end": v(46.22, -2.46) * mm});
            skLineSegment(sketch, "E4793", {"start": v(46.22, -2.46) * mm, "end": v(46.06, -2.46) * mm});
            skLineSegment(sketch, "E4794", {"start": v(46.06, -2.46) * mm, "end": v(45.9, -2.45) * mm});
            skLineSegment(sketch, "E4795", {"start": v(45.9, -2.45) * mm, "end": v(45.74, -2.44) * mm});
            skLineSegment(sketch, "E4796", {"start": v(45.74, -2.44) * mm, "end": v(45.58, -2.43) * mm});
            skLineSegment(sketch, "E4797", {"start": v(45.58, -2.43) * mm, "end": v(45.42, -2.42) * mm});
            skLineSegment(sketch, "E4798", {"start": v(45.42, -2.42) * mm, "end": v(45.26, -2.41) * mm});
            skLineSegment(sketch, "E4799", {"start": v(45.26, -2.41) * mm, "end": v(45.15, -2.4) * mm});
            skLineSegment(sketch, "E4800", {"start": v(45.15, -2.4) * mm, "end": v(45.16, -2.25) * mm});
            skLineSegment(sketch, "E4801", {"start": v(45.16, -2.25) * mm, "end": v(45.16, -2.1) * mm});
            skLineSegment(sketch, "E4802", {"start": v(45.16, -2.1) * mm, "end": v(45.17, -1.94) * mm});
            skLineSegment(sketch, "E4803", {"start": v(45.17, -1.94) * mm, "end": v(45.17, -1.78) * mm});
            skLineSegment(sketch, "E4804", {"start": v(45.17, -1.78) * mm, "end": v(45.18, -1.62) * mm});
            skLineSegment(sketch, "E4805", {"start": v(45.18, -1.62) * mm, "end": v(45.18, -1.47) * mm});
            skLineSegment(sketch, "E4806", {"start": v(45.18, -1.47) * mm, "end": v(45.19, -1.3) * mm});
            skLineSegment(sketch, "E4807", {"start": v(45.19, -1.3) * mm, "end": v(45.2, -1.15) * mm});
            skLineSegment(sketch, "E4808", {"start": v(45.2, -1.15) * mm, "end": v(45.2, -1) * mm});
            skLineSegment(sketch, "E4809", {"start": v(45.2, -1) * mm, "end": v(45.2, -0.84) * mm});
            skLineSegment(sketch, "E4810", {"start": v(45.2, -0.84) * mm, "end": v(45.2, -0.68) * mm});
            skLineSegment(sketch, "E4811", {"start": v(45.2, -0.68) * mm, "end": v(45.2, -0.6) * mm});
            skLineSegment(sketch, "E4812", {"start": v(-5.64, 3.1) * mm, "end": v(-5.44, 3.4) * mm});
            skLineSegment(sketch, "E4813", {"start": v(-5.44, 3.4) * mm, "end": v(-5.21, 3.7) * mm});
            skLineSegment(sketch, "E4814", {"start": v(-5.21, 3.7) * mm, "end": v(-4.97, 3.97) * mm});
            skLineSegment(sketch, "E4815", {"start": v(-4.97, 3.97) * mm, "end": v(-4.71, 4.22) * mm});
            skLineSegment(sketch, "E4816", {"start": v(-4.71, 4.22) * mm, "end": v(-4.44, 4.47) * mm});
            skLineSegment(sketch, "E4817", {"start": v(-4.44, 4.47) * mm, "end": v(-4.15, 4.69) * mm});
            skLineSegment(sketch, "E4818", {"start": v(-4.15, 4.69) * mm, "end": v(-3.85, 4.9) * mm});
            skLineSegment(sketch, "E4819", {"start": v(-3.85, 4.9) * mm, "end": v(-3.54, 5.08) * mm});
            skLineSegment(sketch, "E4820", {"start": v(-3.54, 5.08) * mm, "end": v(-3.26, 5.22) * mm});
            skLineSegment(sketch, "E4821", {"start": v(-3.26, 5.22) * mm, "end": v(-3.37, 5.42) * mm});
            skLineSegment(sketch, "E4822", {"start": v(-3.37, 5.42) * mm, "end": v(-3.65, 5.99) * mm});
            skLineSegment(sketch, "E4823", {"start": v(-3.65, 5.99) * mm, "end": v(-3.93, 6.56) * mm});
            skLineSegment(sketch, "E4824", {"start": v(-3.93, 6.56) * mm, "end": v(-4.2, 7.13) * mm});
            skLineSegment(sketch, "E4825", {"start": v(-4.2, 7.13) * mm, "end": v(-4.45, 7.7) * mm});
            skLineSegment(sketch, "E4826", {"start": v(-4.45, 7.7) * mm, "end": v(-4.7, 8.27) * mm});
            skLineSegment(sketch, "E4827", {"start": v(-4.7, 8.27) * mm, "end": v(-4.93, 8.85) * mm});
            skLineSegment(sketch, "E4828", {"start": v(-4.93, 8.85) * mm, "end": v(-5.16, 9.42) * mm});
            skLineSegment(sketch, "E4829", {"start": v(-5.16, 9.42) * mm, "end": v(-5.38, 10) * mm});
            skLineSegment(sketch, "E4830", {"start": v(-5.38, 10) * mm, "end": v(-5.6, 10.57) * mm});
            skLineSegment(sketch, "E4831", {"start": v(-5.6, 10.57) * mm, "end": v(-5.8, 11.14) * mm});
            skLineSegment(sketch, "E4832", {"start": v(-5.8, 11.14) * mm, "end": v(-5.98, 11.72) * mm});
            skLineSegment(sketch, "E4833", {"start": v(-5.98, 11.72) * mm, "end": v(-6.17, 12.3) * mm});
            skLineSegment(sketch, "E4834", {"start": v(-6.17, 12.3) * mm, "end": v(-6.34, 12.87) * mm});
            skLineSegment(sketch, "E4835", {"start": v(-6.34, 12.87) * mm, "end": v(-6.5, 13.45) * mm});
            skLineSegment(sketch, "E4836", {"start": v(-6.5, 13.45) * mm, "end": v(-6.66, 14.02) * mm});
            skLineSegment(sketch, "E4837", {"start": v(-6.66, 14.02) * mm, "end": v(-6.8, 14.6) * mm});
            skLineSegment(sketch, "E4838", {"start": v(-6.8, 14.6) * mm, "end": v(-6.94, 15.18) * mm});
            skLineSegment(sketch, "E4839", {"start": v(-6.94, 15.18) * mm, "end": v(-7.07, 15.76) * mm});
            skLineSegment(sketch, "E4840", {"start": v(-7.07, 15.76) * mm, "end": v(-7.19, 16.34) * mm});
            skLineSegment(sketch, "E4841", {"start": v(-7.19, 16.34) * mm, "end": v(-7.3, 16.92) * mm});
            skLineSegment(sketch, "E4842", {"start": v(-7.3, 16.92) * mm, "end": v(-7.4, 17.5) * mm});
            skLineSegment(sketch, "E4843", {"start": v(-7.4, 17.5) * mm, "end": v(-7.48, 18.08) * mm});
            skLineSegment(sketch, "E4844", {"start": v(-7.48, 18.08) * mm, "end": v(-7.57, 18.66) * mm});
            skLineSegment(sketch, "E4845", {"start": v(-7.57, 18.66) * mm, "end": v(-7.64, 19.25) * mm});
            skLineSegment(sketch, "E4846", {"start": v(-7.64, 19.25) * mm, "end": v(-7.7, 19.83) * mm});
            skLineSegment(sketch, "E4847", {"start": v(-7.7, 19.83) * mm, "end": v(-7.75, 20.41) * mm});
            skLineSegment(sketch, "E4848", {"start": v(-7.75, 20.41) * mm, "end": v(-7.8, 21) * mm});
            skLineSegment(sketch, "E4849", {"start": v(-7.8, 21) * mm, "end": v(-7.83, 21.58) * mm});
            skLineSegment(sketch, "E4850", {"start": v(-7.83, 21.58) * mm, "end": v(-7.85, 22.16) * mm});
            skLineSegment(sketch, "E4851", {"start": v(-7.85, 22.16) * mm, "end": v(-7.86, 22.75) * mm});
            skLineSegment(sketch, "E4852", {"start": v(-7.86, 22.75) * mm, "end": v(-7.87, 23.34) * mm});
            skLineSegment(sketch, "E4853", {"start": v(-7.87, 23.34) * mm, "end": v(-7.86, 23.93) * mm});
            skLineSegment(sketch, "E4854", {"start": v(-7.86, 23.93) * mm, "end": v(-7.85, 24.52) * mm});
            skLineSegment(sketch, "E4855", {"start": v(-7.85, 24.52) * mm, "end": v(-7.82, 25.12) * mm});
            skLineSegment(sketch, "E4856", {"start": v(-7.82, 25.12) * mm, "end": v(-7.8, 25.7) * mm});
            skLineSegment(sketch, "E4857", {"start": v(-7.8, 25.7) * mm, "end": v(-7.75, 26.3) * mm});
            skLineSegment(sketch, "E4858", {"start": v(-7.75, 26.3) * mm, "end": v(-7.7, 26.9) * mm});
            skLineSegment(sketch, "E4859", {"start": v(-7.7, 26.9) * mm, "end": v(-7.63, 27.48) * mm});
            skLineSegment(sketch, "E4860", {"start": v(-7.63, 27.48) * mm, "end": v(-7.56, 28.07) * mm});
            skLineSegment(sketch, "E4861", {"start": v(-7.56, 28.07) * mm, "end": v(-7.47, 28.66) * mm});
            skLineSegment(sketch, "E4862", {"start": v(-7.47, 28.66) * mm, "end": v(-7.38, 29.25) * mm});
            skLineSegment(sketch, "E4863", {"start": v(-7.38, 29.25) * mm, "end": v(-7.28, 29.84) * mm});
            skLineSegment(sketch, "E4864", {"start": v(-7.28, 29.84) * mm, "end": v(-7.17, 30.43) * mm});
            skLineSegment(sketch, "E4865", {"start": v(-7.17, 30.43) * mm, "end": v(-7.05, 31.02) * mm});
            skLineSegment(sketch, "E4866", {"start": v(-7.05, 31.02) * mm, "end": v(-6.92, 31.6) * mm});
            skLineSegment(sketch, "E4867", {"start": v(-6.92, 31.6) * mm, "end": v(-6.77, 32.2) * mm});
            skLineSegment(sketch, "E4868", {"start": v(-6.77, 32.2) * mm, "end": v(-6.62, 32.78) * mm});
            skLineSegment(sketch, "E4869", {"start": v(-6.62, 32.78) * mm, "end": v(-6.47, 33.37) * mm});
            skLineSegment(sketch, "E4870", {"start": v(-6.47, 33.37) * mm, "end": v(-6.3, 33.95) * mm});
            skLineSegment(sketch, "E4871", {"start": v(-6.3, 33.95) * mm, "end": v(-6.12, 34.53) * mm});
            skLineSegment(sketch, "E4872", {"start": v(-6.12, 34.53) * mm, "end": v(-5.93, 35.12) * mm});
            skLineSegment(sketch, "E4873", {"start": v(-5.93, 35.12) * mm, "end": v(-5.73, 35.7) * mm});
            skLineSegment(sketch, "E4874", {"start": v(-5.73, 35.7) * mm, "end": v(-5.53, 36.28) * mm});
            skLineSegment(sketch, "E4875", {"start": v(-5.53, 36.28) * mm, "end": v(-5.3, 36.87) * mm});
            skLineSegment(sketch, "E4876", {"start": v(-5.3, 36.87) * mm, "end": v(-5.08, 37.45) * mm});
            skLineSegment(sketch, "E4877", {"start": v(-5.08, 37.45) * mm, "end": v(-4.85, 38.03) * mm});
            skLineSegment(sketch, "E4878", {"start": v(-4.85, 38.03) * mm, "end": v(-4.6, 38.6) * mm});
            skLineSegment(sketch, "E4879", {"start": v(-4.6, 38.6) * mm, "end": v(-4.35, 39.19) * mm});
            skLineSegment(sketch, "E4880", {"start": v(-4.35, 39.19) * mm, "end": v(-4.09, 39.77) * mm});
            skLineSegment(sketch, "E4881", {"start": v(-4.09, 39.77) * mm, "end": v(-3.81, 40.35) * mm});
            skLineSegment(sketch, "E4882", {"start": v(-3.81, 40.35) * mm, "end": v(-3.53, 40.93) * mm});
            skLineSegment(sketch, "E4883", {"start": v(-3.53, 40.93) * mm, "end": v(-3.35, 41.28) * mm});
            skLineSegment(sketch, "E4884", {"start": v(-3.35, 41.28) * mm, "end": v(-5.93, 41.03) * mm});
            skLineSegment(sketch, "E4885", {"start": v(-5.93, 41.03) * mm, "end": v(-8.5, 40.63) * mm});
            skLineSegment(sketch, "E4886", {"start": v(-8.5, 40.63) * mm, "end": v(-11.03, 40.06) * mm});
            skLineSegment(sketch, "E4887", {"start": v(-11.03, 40.06) * mm, "end": v(-13.53, 39.34) * mm});
            skLineSegment(sketch, "E4888", {"start": v(-13.53, 39.34) * mm, "end": v(-15.97, 38.46) * mm});
            skLineSegment(sketch, "E4889", {"start": v(-15.97, 38.46) * mm, "end": v(-18.36, 37.42) * mm});
            skLineSegment(sketch, "E4890", {"start": v(-18.36, 37.42) * mm, "end": v(-20.67, 36.24) * mm});
            skLineSegment(sketch, "E4891", {"start": v(-20.67, 36.24) * mm, "end": v(-22.9, 34.92) * mm});
            skLineSegment(sketch, "E4892", {"start": v(-22.9, 34.92) * mm, "end": v(-25.06, 33.46) * mm});
            skLineSegment(sketch, "E4893", {"start": v(-25.06, 33.46) * mm, "end": v(-27.11, 31.87) * mm});
            skLineSegment(sketch, "E4894", {"start": v(-27.11, 31.87) * mm, "end": v(-29.06, 30.15) * mm});
            skLineSegment(sketch, "E4895", {"start": v(-29.06, 30.15) * mm, "end": v(-30.9, 28.31) * mm});
            skLineSegment(sketch, "E4896", {"start": v(-30.9, 28.31) * mm, "end": v(-32.62, 26.36) * mm});
            skLineSegment(sketch, "E4897", {"start": v(-32.62, 26.36) * mm, "end": v(-34.2, 24.31) * mm});
            skLineSegment(sketch, "E4898", {"start": v(-34.2, 24.31) * mm, "end": v(-35.67, 22.16) * mm});
            skLineSegment(sketch, "E4899", {"start": v(-35.67, 22.16) * mm, "end": v(-37, 19.93) * mm});
            skLineSegment(sketch, "E4900", {"start": v(-37, 19.93) * mm, "end": v(-38.17, 17.61) * mm});
            skLineSegment(sketch, "E4901", {"start": v(-38.17, 17.61) * mm, "end": v(-39.2, 15.23) * mm});
            skLineSegment(sketch, "E4902", {"start": v(-39.2, 15.23) * mm, "end": v(-40.08, 12.78) * mm});
            skLineSegment(sketch, "E4903", {"start": v(-40.08, 12.78) * mm, "end": v(-40.8, 10.29) * mm});
            skLineSegment(sketch, "E4904", {"start": v(-40.8, 10.29) * mm, "end": v(-41.37, 7.75) * mm});
            skLineSegment(sketch, "E4905", {"start": v(-41.37, 7.75) * mm, "end": v(-41.78, 5.18) * mm});
            skLineSegment(sketch, "E4906", {"start": v(-41.78, 5.18) * mm, "end": v(-42, 2.95) * mm});
            skLineSegment(sketch, "E4907", {"start": v(-42, 2.95) * mm, "end": v(-41.67, 3.1) * mm});
            skLineSegment(sketch, "E4908", {"start": v(-41.67, 3.1) * mm, "end": v(-41.1, 3.34) * mm});
            skLineSegment(sketch, "E4909", {"start": v(-41.1, 3.34) * mm, "end": v(-40.52, 3.57) * mm});
            skLineSegment(sketch, "E4910", {"start": v(-40.52, 3.57) * mm, "end": v(-39.94, 3.8) * mm});
            skLineSegment(sketch, "E4911", {"start": v(-39.94, 3.8) * mm, "end": v(-39.36, 4.01) * mm});
            skLineSegment(sketch, "E4912", {"start": v(-39.36, 4.01) * mm, "end": v(-38.78, 4.22) * mm});
            skLineSegment(sketch, "E4913", {"start": v(-38.78, 4.22) * mm, "end": v(-38.2, 4.43) * mm});
            skLineSegment(sketch, "E4914", {"start": v(-38.2, 4.43) * mm, "end": v(-37.61, 4.62) * mm});
            skLineSegment(sketch, "E4915", {"start": v(-37.61, 4.62) * mm, "end": v(-37.03, 4.8) * mm});
            skLineSegment(sketch, "E4916", {"start": v(-37.03, 4.8) * mm, "end": v(-36.45, 4.98) * mm});
            skLineSegment(sketch, "E4917", {"start": v(-36.45, 4.98) * mm, "end": v(-35.87, 5.15) * mm});
            skLineSegment(sketch, "E4918", {"start": v(-35.87, 5.15) * mm, "end": v(-35.28, 5.32) * mm});
            skLineSegment(sketch, "E4919", {"start": v(-35.28, 5.32) * mm, "end": v(-34.7, 5.47) * mm});
            skLineSegment(sketch, "E4920", {"start": v(-34.7, 5.47) * mm, "end": v(-34.11, 5.61) * mm});
            skLineSegment(sketch, "E4921", {"start": v(-34.11, 5.61) * mm, "end": v(-33.53, 5.75) * mm});
            skLineSegment(sketch, "E4922", {"start": v(-33.53, 5.75) * mm, "end": v(-32.94, 5.88) * mm});
            skLineSegment(sketch, "E4923", {"start": v(-32.94, 5.88) * mm, "end": v(-32.35, 6) * mm});
            skLineSegment(sketch, "E4924", {"start": v(-32.35, 6) * mm, "end": v(-31.77, 6.11) * mm});
            skLineSegment(sketch, "E4925", {"start": v(-31.77, 6.11) * mm, "end": v(-31.18, 6.22) * mm});
            skLineSegment(sketch, "E4926", {"start": v(-31.18, 6.22) * mm, "end": v(-30.59, 6.31) * mm});
            skLineSegment(sketch, "E4927", {"start": v(-30.59, 6.31) * mm, "end": v(-30, 6.4) * mm});
            skLineSegment(sketch, "E4928", {"start": v(-30, 6.4) * mm, "end": v(-29.41, 6.48) * mm});
            skLineSegment(sketch, "E4929", {"start": v(-29.41, 6.48) * mm, "end": v(-28.82, 6.55) * mm});
            skLineSegment(sketch, "E4930", {"start": v(-28.82, 6.55) * mm, "end": v(-28.23, 6.61) * mm});
            skLineSegment(sketch, "E4931", {"start": v(-28.23, 6.61) * mm, "end": v(-27.64, 6.67) * mm});
            skLineSegment(sketch, "E4932", {"start": v(-27.64, 6.67) * mm, "end": v(-27.05, 6.71) * mm});
            skLineSegment(sketch, "E4933", {"start": v(-27.05, 6.71) * mm, "end": v(-26.46, 6.75) * mm});
            skLineSegment(sketch, "E4934", {"start": v(-26.46, 6.75) * mm, "end": v(-25.86, 6.78) * mm});
            skLineSegment(sketch, "E4935", {"start": v(-25.86, 6.78) * mm, "end": v(-25.27, 6.8) * mm});
            skLineSegment(sketch, "E4936", {"start": v(-25.27, 6.8) * mm, "end": v(-24.68, 6.82) * mm});
            skLineSegment(sketch, "E4937", {"start": v(-24.68, 6.82) * mm, "end": v(-24.08, 6.82) * mm});
            skLineSegment(sketch, "E4938", {"start": v(-24.08, 6.82) * mm, "end": v(-23.5, 6.82) * mm});
            skLineSegment(sketch, "E4939", {"start": v(-23.5, 6.82) * mm, "end": v(-22.91, 6.8) * mm});
            skLineSegment(sketch, "E4940", {"start": v(-22.91, 6.8) * mm, "end": v(-22.33, 6.78) * mm});
            skLineSegment(sketch, "E4941", {"start": v(-22.33, 6.78) * mm, "end": v(-21.74, 6.75) * mm});
            skLineSegment(sketch, "E4942", {"start": v(-21.74, 6.75) * mm, "end": v(-21.16, 6.72) * mm});
            skLineSegment(sketch, "E4943", {"start": v(-21.16, 6.72) * mm, "end": v(-20.57, 6.67) * mm});
            skLineSegment(sketch, "E4944", {"start": v(-20.57, 6.67) * mm, "end": v(-20, 6.62) * mm});
            skLineSegment(sketch, "E4945", {"start": v(-20, 6.62) * mm, "end": v(-19.4, 6.56) * mm});
            skLineSegment(sketch, "E4946", {"start": v(-19.4, 6.56) * mm, "end": v(-18.83, 6.49) * mm});
            skLineSegment(sketch, "E4947", {"start": v(-18.83, 6.49) * mm, "end": v(-18.25, 6.41) * mm});
            skLineSegment(sketch, "E4948", {"start": v(-18.25, 6.41) * mm, "end": v(-17.67, 6.33) * mm});
            skLineSegment(sketch, "E4949", {"start": v(-17.67, 6.33) * mm, "end": v(-17.09, 6.23) * mm});
            skLineSegment(sketch, "E4950", {"start": v(-17.09, 6.23) * mm, "end": v(-16.5, 6.13) * mm});
            skLineSegment(sketch, "E4951", {"start": v(-16.5, 6.13) * mm, "end": v(-15.93, 6.02) * mm});
            skLineSegment(sketch, "E4952", {"start": v(-15.93, 6.02) * mm, "end": v(-15.35, 5.9) * mm});
            skLineSegment(sketch, "E4953", {"start": v(-15.35, 5.9) * mm, "end": v(-14.77, 5.78) * mm});
            skLineSegment(sketch, "E4954", {"start": v(-14.77, 5.78) * mm, "end": v(-14.2, 5.65) * mm});
            skLineSegment(sketch, "E4955", {"start": v(-14.2, 5.65) * mm, "end": v(-13.62, 5.5) * mm});
            skLineSegment(sketch, "E4956", {"start": v(-13.62, 5.5) * mm, "end": v(-13.04, 5.36) * mm});
            skLineSegment(sketch, "E4957", {"start": v(-13.04, 5.36) * mm, "end": v(-12.46, 5.2) * mm});
            skLineSegment(sketch, "E4958", {"start": v(-12.46, 5.2) * mm, "end": v(-11.89, 5.04) * mm});
            skLineSegment(sketch, "E4959", {"start": v(-11.89, 5.04) * mm, "end": v(-11.31, 4.86) * mm});
            skLineSegment(sketch, "E4960", {"start": v(-11.31, 4.86) * mm, "end": v(-10.74, 4.68) * mm});
            skLineSegment(sketch, "E4961", {"start": v(-10.74, 4.68) * mm, "end": v(-10.17, 4.5) * mm});
            skLineSegment(sketch, "E4962", {"start": v(-10.17, 4.5) * mm, "end": v(-9.6, 4.3) * mm});
            skLineSegment(sketch, "E4963", {"start": v(-9.6, 4.3) * mm, "end": v(-9.02, 4.1) * mm});
            skLineSegment(sketch, "E4964", {"start": v(-9.02, 4.1) * mm, "end": v(-8.45, 3.88) * mm});
            skLineSegment(sketch, "E4965", {"start": v(-8.45, 3.88) * mm, "end": v(-7.88, 3.66) * mm});
            skLineSegment(sketch, "E4966", {"start": v(-7.88, 3.66) * mm, "end": v(-7.3, 3.43) * mm});
            skLineSegment(sketch, "E4967", {"start": v(-7.3, 3.43) * mm, "end": v(-6.74, 3.2) * mm});
            skLineSegment(sketch, "E4968", {"start": v(-6.74, 3.2) * mm, "end": v(-6.17, 2.95) * mm});
            skLineSegment(sketch, "E4969", {"start": v(-6.17, 2.95) * mm, "end": v(-5.82, 2.8) * mm});
            skLineSegment(sketch, "E4970", {"start": v(-5.82, 2.8) * mm, "end": v(-5.64, 3.1) * mm});
            skLineSegment(sketch, "E4971", {"start": v(4.67, 2.62) * mm, "end": v(5.24, 2.9) * mm});
            skLineSegment(sketch, "E4972", {"start": v(5.24, 2.9) * mm, "end": v(5.81, 3.18) * mm});
            skLineSegment(sketch, "E4973", {"start": v(5.81, 3.18) * mm, "end": v(6.38, 3.44) * mm});
            skLineSegment(sketch, "E4974", {"start": v(6.38, 3.44) * mm, "end": v(6.96, 3.7) * mm});
            skLineSegment(sketch, "E4975", {"start": v(6.96, 3.7) * mm, "end": v(7.53, 3.95) * mm});
            skLineSegment(sketch, "E4976", {"start": v(7.53, 3.95) * mm, "end": v(8.1, 4.18) * mm});
            skLineSegment(sketch, "E4977", {"start": v(8.1, 4.18) * mm, "end": v(8.67, 4.41) * mm});
            skLineSegment(sketch, "E4978", {"start": v(8.67, 4.41) * mm, "end": v(9.25, 4.63) * mm});
            skLineSegment(sketch, "E4979", {"start": v(9.25, 4.63) * mm, "end": v(9.82, 4.84) * mm});
            skLineSegment(sketch, "E4980", {"start": v(9.82, 4.84) * mm, "end": v(10.4, 5.04) * mm});
            skLineSegment(sketch, "E4981", {"start": v(10.4, 5.04) * mm, "end": v(10.97, 5.24) * mm});
            skLineSegment(sketch, "E4982", {"start": v(10.97, 5.24) * mm, "end": v(11.55, 5.42) * mm});
            skLineSegment(sketch, "E4983", {"start": v(11.55, 5.42) * mm, "end": v(12.12, 5.6) * mm});
            skLineSegment(sketch, "E4984", {"start": v(12.12, 5.6) * mm, "end": v(12.7, 5.76) * mm});
            skLineSegment(sketch, "E4985", {"start": v(12.7, 5.76) * mm, "end": v(13.28, 5.91) * mm});
            skLineSegment(sketch, "E4986", {"start": v(13.28, 5.91) * mm, "end": v(13.86, 6.06) * mm});
            skLineSegment(sketch, "E4987", {"start": v(13.86, 6.06) * mm, "end": v(14.43, 6.2) * mm});
            skLineSegment(sketch, "E4988", {"start": v(14.43, 6.2) * mm, "end": v(15.01, 6.32) * mm});
            skLineSegment(sketch, "E4989", {"start": v(15.01, 6.32) * mm, "end": v(15.6, 6.44) * mm});
            skLineSegment(sketch, "E4990", {"start": v(15.6, 6.44) * mm, "end": v(16.17, 6.55) * mm});
            skLineSegment(sketch, "E4991", {"start": v(16.17, 6.55) * mm, "end": v(16.75, 6.65) * mm});
            skLineSegment(sketch, "E4992", {"start": v(16.75, 6.65) * mm, "end": v(17.34, 6.74) * mm});
            skLineSegment(sketch, "E4993", {"start": v(17.34, 6.74) * mm, "end": v(17.92, 6.82) * mm});
            skLineSegment(sketch, "E4994", {"start": v(17.92, 6.82) * mm, "end": v(18.5, 6.89) * mm});
            skLineSegment(sketch, "E4995", {"start": v(18.5, 6.89) * mm, "end": v(19.08, 6.95) * mm});
            skLineSegment(sketch, "E4996", {"start": v(19.08, 6.95) * mm, "end": v(19.67, 7) * mm});
            skLineSegment(sketch, "E4997", {"start": v(19.67, 7) * mm, "end": v(20.25, 7.05) * mm});
            skLineSegment(sketch, "E4998", {"start": v(20.25, 7.05) * mm, "end": v(20.83, 7.08) * mm});
            skLineSegment(sketch, "E4999", {"start": v(20.83, 7.08) * mm, "end": v(21.42, 7.1) * mm});
            skLineSegment(sketch, "E5000", {"start": v(21.42, 7.1) * mm, "end": v(22, 7.12) * mm});
            skLineSegment(sketch, "E5001", {"start": v(22, 7.12) * mm, "end": v(22.59, 7.12) * mm});
            skLineSegment(sketch, "E5002", {"start": v(22.59, 7.12) * mm, "end": v(23.18, 7.12) * mm});
            skLineSegment(sketch, "E5003", {"start": v(23.18, 7.12) * mm, "end": v(23.78, 7.1) * mm});
            skLineSegment(sketch, "E5004", {"start": v(23.78, 7.1) * mm, "end": v(24.37, 7.08) * mm});
            skLineSegment(sketch, "E5005", {"start": v(24.37, 7.08) * mm, "end": v(24.96, 7.04) * mm});
            skLineSegment(sketch, "E5006", {"start": v(24.96, 7.04) * mm, "end": v(25.56, 7) * mm});
            skLineSegment(sketch, "E5007", {"start": v(25.56, 7) * mm, "end": v(26.15, 6.95) * mm});
            skLineSegment(sketch, "E5008", {"start": v(26.15, 6.95) * mm, "end": v(26.74, 6.88) * mm});
            skLineSegment(sketch, "E5009", {"start": v(26.74, 6.88) * mm, "end": v(27.33, 6.8) * mm});
            skLineSegment(sketch, "E5010", {"start": v(27.33, 6.8) * mm, "end": v(27.92, 6.73) * mm});
            skLineSegment(sketch, "E5011", {"start": v(27.92, 6.73) * mm, "end": v(28.5, 6.63) * mm});
            skLineSegment(sketch, "E5012", {"start": v(28.5, 6.63) * mm, "end": v(29.1, 6.53) * mm});
            skLineSegment(sketch, "E5013", {"start": v(29.1, 6.53) * mm, "end": v(29.69, 6.42) * mm});
            skLineSegment(sketch, "E5014", {"start": v(29.69, 6.42) * mm, "end": v(30.27, 6.3) * mm});
            skLineSegment(sketch, "E5015", {"start": v(30.27, 6.3) * mm, "end": v(30.86, 6.17) * mm});
            skLineSegment(sketch, "E5016", {"start": v(30.86, 6.17) * mm, "end": v(31.45, 6.03) * mm});
            skLineSegment(sketch, "E5017", {"start": v(31.45, 6.03) * mm, "end": v(32.03, 5.88) * mm});
            skLineSegment(sketch, "E5018", {"start": v(32.03, 5.88) * mm, "end": v(32.62, 5.72) * mm});
            skLineSegment(sketch, "E5019", {"start": v(32.62, 5.72) * mm, "end": v(33.2, 5.55) * mm});
            skLineSegment(sketch, "E5020", {"start": v(33.2, 5.55) * mm, "end": v(33.79, 5.37) * mm});
            skLineSegment(sketch, "E5021", {"start": v(33.79, 5.37) * mm, "end": v(34.37, 5.18) * mm});
            skLineSegment(sketch, "E5022", {"start": v(34.37, 5.18) * mm, "end": v(34.96, 4.99) * mm});
            skLineSegment(sketch, "E5023", {"start": v(34.96, 4.99) * mm, "end": v(35.54, 4.78) * mm});
            skLineSegment(sketch, "E5024", {"start": v(35.54, 4.78) * mm, "end": v(36.12, 4.56) * mm});
            skLineSegment(sketch, "E5025", {"start": v(36.12, 4.56) * mm, "end": v(36.7, 4.34) * mm});
            skLineSegment(sketch, "E5026", {"start": v(36.7, 4.34) * mm, "end": v(37.28, 4.1) * mm});
            skLineSegment(sketch, "E5027", {"start": v(37.28, 4.1) * mm, "end": v(37.86, 3.86) * mm});
            skLineSegment(sketch, "E5028", {"start": v(37.86, 3.86) * mm, "end": v(38.44, 3.6) * mm});
            skLineSegment(sketch, "E5029", {"start": v(38.44, 3.6) * mm, "end": v(39.02, 3.34) * mm});
            skLineSegment(sketch, "E5030", {"start": v(39.02, 3.34) * mm, "end": v(39.6, 3.07) * mm});
            skLineSegment(sketch, "E5031", {"start": v(39.6, 3.07) * mm, "end": v(40.18, 2.78) * mm});
            skLineSegment(sketch, "E5032", {"start": v(40.18, 2.78) * mm, "end": v(40.53, 2.6) * mm});
            skLineSegment(sketch, "E5033", {"start": v(40.53, 2.6) * mm, "end": v(40.29, 5.18) * mm});
            skLineSegment(sketch, "E5034", {"start": v(40.29, 5.18) * mm, "end": v(39.88, 7.75) * mm});
            skLineSegment(sketch, "E5035", {"start": v(39.88, 7.75) * mm, "end": v(39.32, 10.29) * mm});
            skLineSegment(sketch, "E5036", {"start": v(39.32, 10.29) * mm, "end": v(38.6, 12.78) * mm});
            skLineSegment(sketch, "E5037", {"start": v(38.6, 12.78) * mm, "end": v(37.71, 15.23) * mm});
            skLineSegment(sketch, "E5038", {"start": v(37.71, 15.23) * mm, "end": v(36.68, 17.61) * mm});
            skLineSegment(sketch, "E5039", {"start": v(36.68, 17.61) * mm, "end": v(35.5, 19.93) * mm});
            skLineSegment(sketch, "E5040", {"start": v(35.5, 19.93) * mm, "end": v(34.18, 22.16) * mm});
            skLineSegment(sketch, "E5041", {"start": v(34.18, 22.16) * mm, "end": v(32.72, 24.31) * mm});
            skLineSegment(sketch, "E5042", {"start": v(32.72, 24.31) * mm, "end": v(31.12, 26.36) * mm});
            skLineSegment(sketch, "E5043", {"start": v(31.12, 26.36) * mm, "end": v(29.4, 28.31) * mm});
            skLineSegment(sketch, "E5044", {"start": v(29.4, 28.31) * mm, "end": v(27.57, 30.15) * mm});
            skLineSegment(sketch, "E5045", {"start": v(27.57, 30.15) * mm, "end": v(25.62, 31.87) * mm});
            skLineSegment(sketch, "E5046", {"start": v(25.62, 31.87) * mm, "end": v(23.57, 33.46) * mm});
            skLineSegment(sketch, "E5047", {"start": v(23.57, 33.46) * mm, "end": v(21.42, 34.92) * mm});
            skLineSegment(sketch, "E5048", {"start": v(21.42, 34.92) * mm, "end": v(19.18, 36.24) * mm});
            skLineSegment(sketch, "E5049", {"start": v(19.18, 36.24) * mm, "end": v(16.86, 37.42) * mm});
            skLineSegment(sketch, "E5050", {"start": v(16.86, 37.42) * mm, "end": v(14.48, 38.46) * mm});
            skLineSegment(sketch, "E5051", {"start": v(14.48, 38.46) * mm, "end": v(12.03, 39.34) * mm});
            skLineSegment(sketch, "E5052", {"start": v(12.03, 39.34) * mm, "end": v(9.54, 40.06) * mm});
            skLineSegment(sketch, "E5053", {"start": v(9.54, 40.06) * mm, "end": v(7, 40.63) * mm});
            skLineSegment(sketch, "E5054", {"start": v(7, 40.63) * mm, "end": v(4.44, 41.03) * mm});
            skLineSegment(sketch, "E5055", {"start": v(4.44, 41.03) * mm, "end": v(2.2, 41.25) * mm});
            skLineSegment(sketch, "E5056", {"start": v(2.2, 41.25) * mm, "end": v(2.35, 40.93) * mm});
            skLineSegment(sketch, "E5057", {"start": v(2.35, 40.93) * mm, "end": v(2.59, 40.35) * mm});
            skLineSegment(sketch, "E5058", {"start": v(2.59, 40.35) * mm, "end": v(2.82, 39.77) * mm});
            skLineSegment(sketch, "E5059", {"start": v(2.82, 39.77) * mm, "end": v(3.05, 39.19) * mm});
            skLineSegment(sketch, "E5060", {"start": v(3.05, 39.19) * mm, "end": v(3.27, 38.6) * mm});
            skLineSegment(sketch, "E5061", {"start": v(3.27, 38.6) * mm, "end": v(3.48, 38.03) * mm});
            skLineSegment(sketch, "E5062", {"start": v(3.48, 38.03) * mm, "end": v(3.68, 37.45) * mm});
            skLineSegment(sketch, "E5063", {"start": v(3.68, 37.45) * mm, "end": v(3.87, 36.87) * mm});
            skLineSegment(sketch, "E5064", {"start": v(3.87, 36.87) * mm, "end": v(4.06, 36.28) * mm});
            skLineSegment(sketch, "E5065", {"start": v(4.06, 36.28) * mm, "end": v(4.24, 35.7) * mm});
            skLineSegment(sketch, "E5066", {"start": v(4.24, 35.7) * mm, "end": v(4.4, 35.12) * mm});
            skLineSegment(sketch, "E5067", {"start": v(4.4, 35.12) * mm, "end": v(4.57, 34.53) * mm});
            skLineSegment(sketch, "E5068", {"start": v(4.57, 34.53) * mm, "end": v(4.72, 33.95) * mm});
            skLineSegment(sketch, "E5069", {"start": v(4.72, 33.95) * mm, "end": v(4.87, 33.37) * mm});
            skLineSegment(sketch, "E5070", {"start": v(4.87, 33.37) * mm, "end": v(5, 32.78) * mm});
            skLineSegment(sketch, "E5071", {"start": v(5, 32.78) * mm, "end": v(5.13, 32.2) * mm});
            skLineSegment(sketch, "E5072", {"start": v(5.13, 32.2) * mm, "end": v(5.25, 31.6) * mm});
            skLineSegment(sketch, "E5073", {"start": v(5.25, 31.6) * mm, "end": v(5.37, 31.02) * mm});
            skLineSegment(sketch, "E5074", {"start": v(5.37, 31.02) * mm, "end": v(5.47, 30.43) * mm});
            skLineSegment(sketch, "E5075", {"start": v(5.47, 30.43) * mm, "end": v(5.57, 29.84) * mm});
            skLineSegment(sketch, "E5076", {"start": v(5.57, 29.84) * mm, "end": v(5.66, 29.25) * mm});
            skLineSegment(sketch, "E5077", {"start": v(5.66, 29.25) * mm, "end": v(5.73, 28.66) * mm});
            skLineSegment(sketch, "E5078", {"start": v(5.73, 28.66) * mm, "end": v(5.8, 28.07) * mm});
            skLineSegment(sketch, "E5079", {"start": v(5.8, 28.07) * mm, "end": v(5.87, 27.48) * mm});
            skLineSegment(sketch, "E5080", {"start": v(5.87, 27.48) * mm, "end": v(5.92, 26.9) * mm});
            skLineSegment(sketch, "E5081", {"start": v(5.92, 26.9) * mm, "end": v(5.97, 26.3) * mm});
            skLineSegment(sketch, "E5082", {"start": v(5.97, 26.3) * mm, "end": v(6, 25.7) * mm});
            skLineSegment(sketch, "E5083", {"start": v(6, 25.7) * mm, "end": v(6.04, 25.12) * mm});
            skLineSegment(sketch, "E5084", {"start": v(6.04, 25.12) * mm, "end": v(6.06, 24.52) * mm});
            skLineSegment(sketch, "E5085", {"start": v(6.06, 24.52) * mm, "end": v(6.07, 23.93) * mm});
            skLineSegment(sketch, "E5086", {"start": v(6.07, 23.93) * mm, "end": v(6.07, 23.34) * mm});
            skLineSegment(sketch, "E5087", {"start": v(6.07, 23.34) * mm, "end": v(6.07, 22.75) * mm});
            skLineSegment(sketch, "E5088", {"start": v(6.07, 22.75) * mm, "end": v(6.06, 22.16) * mm});
            skLineSegment(sketch, "E5089", {"start": v(6.06, 22.16) * mm, "end": v(6.04, 21.58) * mm});
            skLineSegment(sketch, "E5090", {"start": v(6.04, 21.58) * mm, "end": v(6, 21) * mm});
            skLineSegment(sketch, "E5091", {"start": v(6, 21) * mm, "end": v(5.97, 20.41) * mm});
            skLineSegment(sketch, "E5092", {"start": v(5.97, 20.41) * mm, "end": v(5.93, 19.83) * mm});
            skLineSegment(sketch, "E5093", {"start": v(5.93, 19.83) * mm, "end": v(5.87, 19.25) * mm});
            skLineSegment(sketch, "E5094", {"start": v(5.87, 19.25) * mm, "end": v(5.81, 18.66) * mm});
            skLineSegment(sketch, "E5095", {"start": v(5.81, 18.66) * mm, "end": v(5.74, 18.08) * mm});
            skLineSegment(sketch, "E5096", {"start": v(5.74, 18.08) * mm, "end": v(5.67, 17.5) * mm});
            skLineSegment(sketch, "E5097", {"start": v(5.67, 17.5) * mm, "end": v(5.58, 16.92) * mm});
            skLineSegment(sketch, "E5098", {"start": v(5.58, 16.92) * mm, "end": v(5.49, 16.34) * mm});
            skLineSegment(sketch, "E5099", {"start": v(5.49, 16.34) * mm, "end": v(5.39, 15.76) * mm});
            skLineSegment(sketch, "E5100", {"start": v(5.39, 15.76) * mm, "end": v(5.28, 15.18) * mm});
            skLineSegment(sketch, "E5101", {"start": v(5.28, 15.18) * mm, "end": v(5.16, 14.6) * mm});
            skLineSegment(sketch, "E5102", {"start": v(5.16, 14.6) * mm, "end": v(5.04, 14.02) * mm});
            skLineSegment(sketch, "E5103", {"start": v(5.04, 14.02) * mm, "end": v(4.9, 13.45) * mm});
            skLineSegment(sketch, "E5104", {"start": v(4.9, 13.45) * mm, "end": v(4.76, 12.87) * mm});
            skLineSegment(sketch, "E5105", {"start": v(4.76, 12.87) * mm, "end": v(4.61, 12.3) * mm});
            skLineSegment(sketch, "E5106", {"start": v(4.61, 12.3) * mm, "end": v(4.45, 11.72) * mm});
            skLineSegment(sketch, "E5107", {"start": v(4.45, 11.72) * mm, "end": v(4.29, 11.14) * mm});
            skLineSegment(sketch, "E5108", {"start": v(4.29, 11.14) * mm, "end": v(4.12, 10.57) * mm});
            skLineSegment(sketch, "E5109", {"start": v(4.12, 10.57) * mm, "end": v(3.94, 10) * mm});
            skLineSegment(sketch, "E5110", {"start": v(3.94, 10) * mm, "end": v(3.75, 9.42) * mm});
            skLineSegment(sketch, "E5111", {"start": v(3.75, 9.42) * mm, "end": v(3.55, 8.85) * mm});
            skLineSegment(sketch, "E5112", {"start": v(3.55, 8.85) * mm, "end": v(3.35, 8.27) * mm});
            skLineSegment(sketch, "E5113", {"start": v(3.35, 8.27) * mm, "end": v(3.13, 7.7) * mm});
            skLineSegment(sketch, "E5114", {"start": v(3.13, 7.7) * mm, "end": v(2.91, 7.13) * mm});
            skLineSegment(sketch, "E5115", {"start": v(2.91, 7.13) * mm, "end": v(2.69, 6.56) * mm});
            skLineSegment(sketch, "E5116", {"start": v(2.69, 6.56) * mm, "end": v(2.45, 5.99) * mm});
            skLineSegment(sketch, "E5117", {"start": v(2.45, 5.99) * mm, "end": v(2.2, 5.42) * mm});
            skLineSegment(sketch, "E5118", {"start": v(2.2, 5.42) * mm, "end": v(2.05, 5.07) * mm});
            skLineSegment(sketch, "E5119", {"start": v(2.05, 5.07) * mm, "end": v(2.36, 4.9) * mm});
            skLineSegment(sketch, "E5120", {"start": v(2.36, 4.9) * mm, "end": v(2.66, 4.69) * mm});
            skLineSegment(sketch, "E5121", {"start": v(2.66, 4.69) * mm, "end": v(2.95, 4.47) * mm});
            skLineSegment(sketch, "E5122", {"start": v(2.95, 4.47) * mm, "end": v(3.22, 4.22) * mm});
            skLineSegment(sketch, "E5123", {"start": v(3.22, 4.22) * mm, "end": v(3.48, 3.97) * mm});
            skLineSegment(sketch, "E5124", {"start": v(3.48, 3.97) * mm, "end": v(3.72, 3.7) * mm});
            skLineSegment(sketch, "E5125", {"start": v(3.72, 3.7) * mm, "end": v(3.94, 3.4) * mm});
            skLineSegment(sketch, "E5126", {"start": v(3.94, 3.4) * mm, "end": v(4.15, 3.1) * mm});
            skLineSegment(sketch, "E5127", {"start": v(4.15, 3.1) * mm, "end": v(4.33, 2.8) * mm});
            skLineSegment(sketch, "E5128", {"start": v(4.33, 2.8) * mm, "end": v(4.47, 2.52) * mm});
            skLineSegment(sketch, "E5129", {"start": v(4.47, 2.52) * mm, "end": v(4.67, 2.62) * mm});
            skLineSegment(sketch, "E5130", {"start": v(0.2, 14.22) * mm, "end": v(0.34, 14.52) * mm});
            skLineSegment(sketch, "E5131", {"start": v(0.34, 14.52) * mm, "end": v(0.47, 14.83) * mm});
            skLineSegment(sketch, "E5132", {"start": v(0.47, 14.83) * mm, "end": v(0.6, 15.13) * mm});
            skLineSegment(sketch, "E5133", {"start": v(0.6, 15.13) * mm, "end": v(0.72, 15.44) * mm});
            skLineSegment(sketch, "E5134", {"start": v(0.72, 15.44) * mm, "end": v(0.83, 15.74) * mm});
            skLineSegment(sketch, "E5135", {"start": v(0.83, 15.74) * mm, "end": v(0.95, 16.05) * mm});
            skLineSegment(sketch, "E5136", {"start": v(0.95, 16.05) * mm, "end": v(1.05, 16.35) * mm});
            skLineSegment(sketch, "E5137", {"start": v(1.05, 16.35) * mm, "end": v(1.16, 16.66) * mm});
            skLineSegment(sketch, "E5138", {"start": v(1.16, 16.66) * mm, "end": v(1.26, 16.96) * mm});
            skLineSegment(sketch, "E5139", {"start": v(1.26, 16.96) * mm, "end": v(1.35, 17.27) * mm});
            skLineSegment(sketch, "E5140", {"start": v(1.35, 17.27) * mm, "end": v(1.44, 17.58) * mm});
            skLineSegment(sketch, "E5141", {"start": v(1.44, 17.58) * mm, "end": v(1.53, 17.88) * mm});
            skLineSegment(sketch, "E5142", {"start": v(1.53, 17.88) * mm, "end": v(1.6, 18.2) * mm});
            skLineSegment(sketch, "E5143", {"start": v(1.6, 18.2) * mm, "end": v(1.68, 18.5) * mm});
            skLineSegment(sketch, "E5144", {"start": v(1.68, 18.5) * mm, "end": v(1.76, 18.8) * mm});
            skLineSegment(sketch, "E5145", {"start": v(1.76, 18.8) * mm, "end": v(1.82, 19.11) * mm});
            skLineSegment(sketch, "E5146", {"start": v(1.82, 19.11) * mm, "end": v(1.88, 19.42) * mm});
            skLineSegment(sketch, "E5147", {"start": v(1.88, 19.42) * mm, "end": v(1.94, 19.73) * mm});
            skLineSegment(sketch, "E5148", {"start": v(1.94, 19.73) * mm, "end": v(2, 20.04) * mm});
            skLineSegment(sketch, "E5149", {"start": v(2, 20.04) * mm, "end": v(2.04, 20.34) * mm});
            skLineSegment(sketch, "E5150", {"start": v(2.04, 20.34) * mm, "end": v(2.09, 20.65) * mm});
            skLineSegment(sketch, "E5151", {"start": v(2.09, 20.65) * mm, "end": v(2.13, 20.96) * mm});
            skLineSegment(sketch, "E5152", {"start": v(2.13, 20.96) * mm, "end": v(2.16, 21.27) * mm});
            skLineSegment(sketch, "E5153", {"start": v(2.16, 21.27) * mm, "end": v(2.2, 21.58) * mm});
            skLineSegment(sketch, "E5154", {"start": v(2.2, 21.58) * mm, "end": v(2.22, 21.89) * mm});
            skLineSegment(sketch, "E5155", {"start": v(2.22, 21.89) * mm, "end": v(2.24, 22.2) * mm});
            skLineSegment(sketch, "E5156", {"start": v(2.24, 22.2) * mm, "end": v(2.26, 22.5) * mm});
            skLineSegment(sketch, "E5157", {"start": v(2.26, 22.5) * mm, "end": v(2.27, 22.82) * mm});
            skLineSegment(sketch, "E5158", {"start": v(2.27, 22.82) * mm, "end": v(2.27, 23.13) * mm});
            skLineSegment(sketch, "E5159", {"start": v(2.27, 23.13) * mm, "end": v(2.28, 23.44) * mm});
            skLineSegment(sketch, "E5160", {"start": v(2.28, 23.44) * mm, "end": v(2.27, 23.76) * mm});
            skLineSegment(sketch, "E5161", {"start": v(2.27, 23.76) * mm, "end": v(2.27, 24.07) * mm});
            skLineSegment(sketch, "E5162", {"start": v(2.27, 24.07) * mm, "end": v(2.26, 24.39) * mm});
            skLineSegment(sketch, "E5163", {"start": v(2.26, 24.39) * mm, "end": v(2.24, 24.7) * mm});
            skLineSegment(sketch, "E5164", {"start": v(2.24, 24.7) * mm, "end": v(2.22, 25.01) * mm});
            skLineSegment(sketch, "E5165", {"start": v(2.22, 25.01) * mm, "end": v(2.2, 25.33) * mm});
            skLineSegment(sketch, "E5166", {"start": v(2.2, 25.33) * mm, "end": v(2.16, 25.64) * mm});
            skLineSegment(sketch, "E5167", {"start": v(2.16, 25.64) * mm, "end": v(2.12, 25.95) * mm});
            skLineSegment(sketch, "E5168", {"start": v(2.12, 25.95) * mm, "end": v(2.08, 26.27) * mm});
            skLineSegment(sketch, "E5169", {"start": v(2.08, 26.27) * mm, "end": v(2.04, 26.58) * mm});
            skLineSegment(sketch, "E5170", {"start": v(2.04, 26.58) * mm, "end": v(1.99, 26.9) * mm});
            skLineSegment(sketch, "E5171", {"start": v(1.99, 26.9) * mm, "end": v(1.93, 27.2) * mm});
            skLineSegment(sketch, "E5172", {"start": v(1.93, 27.2) * mm, "end": v(1.87, 27.52) * mm});
            skLineSegment(sketch, "E5173", {"start": v(1.87, 27.52) * mm, "end": v(1.8, 27.83) * mm});
            skLineSegment(sketch, "E5174", {"start": v(1.8, 27.83) * mm, "end": v(1.74, 28.14) * mm});
            skLineSegment(sketch, "E5175", {"start": v(1.74, 28.14) * mm, "end": v(1.67, 28.45) * mm});
            skLineSegment(sketch, "E5176", {"start": v(1.67, 28.45) * mm, "end": v(1.59, 28.76) * mm});
            skLineSegment(sketch, "E5177", {"start": v(1.59, 28.76) * mm, "end": v(1.5, 29.08) * mm});
            skLineSegment(sketch, "E5178", {"start": v(1.5, 29.08) * mm, "end": v(1.42, 29.39) * mm});
            skLineSegment(sketch, "E5179", {"start": v(1.42, 29.39) * mm, "end": v(1.32, 29.7) * mm});
            skLineSegment(sketch, "E5180", {"start": v(1.32, 29.7) * mm, "end": v(1.23, 30) * mm});
            skLineSegment(sketch, "E5181", {"start": v(1.23, 30) * mm, "end": v(1.13, 30.32) * mm});
            skLineSegment(sketch, "E5182", {"start": v(1.13, 30.32) * mm, "end": v(1.02, 30.63) * mm});
            skLineSegment(sketch, "E5183", {"start": v(1.02, 30.63) * mm, "end": v(0.9, 30.94) * mm});
            skLineSegment(sketch, "E5184", {"start": v(0.9, 30.94) * mm, "end": v(0.8, 31.25) * mm});
            skLineSegment(sketch, "E5185", {"start": v(0.8, 31.25) * mm, "end": v(0.67, 31.56) * mm});
            skLineSegment(sketch, "E5186", {"start": v(0.67, 31.56) * mm, "end": v(0.55, 31.87) * mm});
            skLineSegment(sketch, "E5187", {"start": v(0.55, 31.87) * mm, "end": v(0.42, 32.18) * mm});
            skLineSegment(sketch, "E5188", {"start": v(0.42, 32.18) * mm, "end": v(0.28, 32.49) * mm});
            skLineSegment(sketch, "E5189", {"start": v(0.28, 32.49) * mm, "end": v(0.14, 32.8) * mm});
            skLineSegment(sketch, "E5190", {"start": v(0.14, 32.8) * mm, "end": v(0.12, 32.83) * mm});
            skLineSegment(sketch, "E5191", {"start": v(0.12, 32.83) * mm, "end": v(-1.38, 32.83) * mm});
            skLineSegment(sketch, "E5192", {"start": v(-1.38, 32.83) * mm, "end": v(-1.43, 32.74) * mm});
            skLineSegment(sketch, "E5193", {"start": v(-1.43, 32.74) * mm, "end": v(-1.59, 32.44) * mm});
            skLineSegment(sketch, "E5194", {"start": v(-1.59, 32.44) * mm, "end": v(-1.75, 32.13) * mm});
            skLineSegment(sketch, "E5195", {"start": v(-1.75, 32.13) * mm, "end": v(-1.9, 31.82) * mm});
            skLineSegment(sketch, "E5196", {"start": v(-1.9, 31.82) * mm, "end": v(-2.04, 31.51) * mm});
            skLineSegment(sketch, "E5197", {"start": v(-2.04, 31.51) * mm, "end": v(-2.18, 31.2) * mm});
            skLineSegment(sketch, "E5198", {"start": v(-2.18, 31.2) * mm, "end": v(-2.32, 30.9) * mm});
            skLineSegment(sketch, "E5199", {"start": v(-2.32, 30.9) * mm, "end": v(-2.45, 30.58) * mm});
            skLineSegment(sketch, "E5200", {"start": v(-2.45, 30.58) * mm, "end": v(-2.57, 30.28) * mm});
            skLineSegment(sketch, "E5201", {"start": v(-2.57, 30.28) * mm, "end": v(-2.69, 29.97) * mm});
            skLineSegment(sketch, "E5202", {"start": v(-2.69, 29.97) * mm, "end": v(-2.8, 29.66) * mm});
            skLineSegment(sketch, "E5203", {"start": v(-2.8, 29.66) * mm, "end": v(-2.9, 29.35) * mm});
            skLineSegment(sketch, "E5204", {"start": v(-2.9, 29.35) * mm, "end": v(-3, 29.04) * mm});
            skLineSegment(sketch, "E5205", {"start": v(-3, 29.04) * mm, "end": v(-3.1, 28.73) * mm});
            skLineSegment(sketch, "E5206", {"start": v(-3.1, 28.73) * mm, "end": v(-3.2, 28.42) * mm});
            skLineSegment(sketch, "E5207", {"start": v(-3.2, 28.42) * mm, "end": v(-3.28, 28.1) * mm});
            skLineSegment(sketch, "E5208", {"start": v(-3.28, 28.1) * mm, "end": v(-3.36, 27.8) * mm});
            skLineSegment(sketch, "E5209", {"start": v(-3.36, 27.8) * mm, "end": v(-3.44, 27.49) * mm});
            skLineSegment(sketch, "E5210", {"start": v(-3.44, 27.49) * mm, "end": v(-3.5, 27.18) * mm});
            skLineSegment(sketch, "E5211", {"start": v(-3.5, 27.18) * mm, "end": v(-3.57, 26.87) * mm});
            skLineSegment(sketch, "E5212", {"start": v(-3.57, 26.87) * mm, "end": v(-3.63, 26.56) * mm});
            skLineSegment(sketch, "E5213", {"start": v(-3.63, 26.56) * mm, "end": v(-3.68, 26.25) * mm});
            skLineSegment(sketch, "E5214", {"start": v(-3.68, 26.25) * mm, "end": v(-3.72, 25.94) * mm});
            skLineSegment(sketch, "E5215", {"start": v(-3.72, 25.94) * mm, "end": v(-3.77, 25.63) * mm});
            skLineSegment(sketch, "E5216", {"start": v(-3.77, 25.63) * mm, "end": v(-3.8, 25.31) * mm});
            skLineSegment(sketch, "E5217", {"start": v(-3.8, 25.31) * mm, "end": v(-3.83, 25) * mm});
            skLineSegment(sketch, "E5218", {"start": v(-3.83, 25) * mm, "end": v(-3.86, 24.7) * mm});
            skLineSegment(sketch, "E5219", {"start": v(-3.86, 24.7) * mm, "end": v(-3.88, 24.38) * mm});
            skLineSegment(sketch, "E5220", {"start": v(-3.88, 24.38) * mm, "end": v(-3.9, 24.07) * mm});
            skLineSegment(sketch, "E5221", {"start": v(-3.9, 24.07) * mm, "end": v(-3.9, 23.75) * mm});
            skLineSegment(sketch, "E5222", {"start": v(-3.9, 23.75) * mm, "end": v(-3.9, 23.44) * mm});
            skLineSegment(sketch, "E5223", {"start": v(-3.9, 23.44) * mm, "end": v(-3.9, 23.13) * mm});
            skLineSegment(sketch, "E5224", {"start": v(-3.9, 23.13) * mm, "end": v(-3.9, 22.82) * mm});
            skLineSegment(sketch, "E5225", {"start": v(-3.9, 22.82) * mm, "end": v(-3.88, 22.52) * mm});
            skLineSegment(sketch, "E5226", {"start": v(-3.88, 22.52) * mm, "end": v(-3.86, 22.2) * mm});
            skLineSegment(sketch, "E5227", {"start": v(-3.86, 22.2) * mm, "end": v(-3.83, 21.9) * mm});
            skLineSegment(sketch, "E5228", {"start": v(-3.83, 21.9) * mm, "end": v(-3.8, 21.6) * mm});
            skLineSegment(sketch, "E5229", {"start": v(-3.8, 21.6) * mm, "end": v(-3.77, 21.29) * mm});
            skLineSegment(sketch, "E5230", {"start": v(-3.77, 21.29) * mm, "end": v(-3.73, 20.98) * mm});
            skLineSegment(sketch, "E5231", {"start": v(-3.73, 20.98) * mm, "end": v(-3.68, 20.67) * mm});
            skLineSegment(sketch, "E5232", {"start": v(-3.68, 20.67) * mm, "end": v(-3.63, 20.37) * mm});
            skLineSegment(sketch, "E5233", {"start": v(-3.63, 20.37) * mm, "end": v(-3.58, 20.06) * mm});
            skLineSegment(sketch, "E5234", {"start": v(-3.58, 20.06) * mm, "end": v(-3.52, 19.75) * mm});
            skLineSegment(sketch, "E5235", {"start": v(-3.52, 19.75) * mm, "end": v(-3.45, 19.45) * mm});
            skLineSegment(sketch, "E5236", {"start": v(-3.45, 19.45) * mm, "end": v(-3.38, 19.14) * mm});
            skLineSegment(sketch, "E5237", {"start": v(-3.38, 19.14) * mm, "end": v(-3.3, 18.84) * mm});
            skLineSegment(sketch, "E5238", {"start": v(-3.3, 18.84) * mm, "end": v(-3.22, 18.53) * mm});
            skLineSegment(sketch, "E5239", {"start": v(-3.22, 18.53) * mm, "end": v(-3.13, 18.23) * mm});
            skLineSegment(sketch, "E5240", {"start": v(-3.13, 18.23) * mm, "end": v(-3.03, 17.92) * mm});
            skLineSegment(sketch, "E5241", {"start": v(-3.03, 17.92) * mm, "end": v(-2.93, 17.62) * mm});
            skLineSegment(sketch, "E5242", {"start": v(-2.93, 17.62) * mm, "end": v(-2.83, 17.31) * mm});
            skLineSegment(sketch, "E5243", {"start": v(-2.83, 17.31) * mm, "end": v(-2.72, 17) * mm});
            skLineSegment(sketch, "E5244", {"start": v(-2.72, 17) * mm, "end": v(-2.6, 16.7) * mm});
            skLineSegment(sketch, "E5245", {"start": v(-2.6, 16.7) * mm, "end": v(-2.49, 16.4) * mm});
            skLineSegment(sketch, "E5246", {"start": v(-2.49, 16.4) * mm, "end": v(-2.36, 16.1) * mm});
            skLineSegment(sketch, "E5247", {"start": v(-2.36, 16.1) * mm, "end": v(-2.23, 15.79) * mm});
            skLineSegment(sketch, "E5248", {"start": v(-2.23, 15.79) * mm, "end": v(-2.1, 15.48) * mm});
            skLineSegment(sketch, "E5249", {"start": v(-2.1, 15.48) * mm, "end": v(-1.95, 15.18) * mm});
            skLineSegment(sketch, "E5250", {"start": v(-1.95, 15.18) * mm, "end": v(-1.8, 14.87) * mm});
            skLineSegment(sketch, "E5251", {"start": v(-1.8, 14.87) * mm, "end": v(-1.65, 14.57) * mm});
            skLineSegment(sketch, "E5252", {"start": v(-1.65, 14.57) * mm, "end": v(-1.5, 14.27) * mm});
            skLineSegment(sketch, "E5253", {"start": v(-1.5, 14.27) * mm, "end": v(-1.46, 14.2) * mm});
            skLineSegment(sketch, "E5254", {"start": v(-1.46, 14.2) * mm, "end": v(0.19, 14.2) * mm});
            skLineSegment(sketch, "E5255", {"start": v(0.19, 14.2) * mm, "end": v(0.2, 14.22) * mm});
            skLineSegment(sketch, "E5256", {"start": v(23, -3.02) * mm, "end": v(23.32, -3.01) * mm});
            skLineSegment(sketch, "E5257", {"start": v(23.32, -3.01) * mm, "end": v(23.64, -3) * mm});
            skLineSegment(sketch, "E5258", {"start": v(23.64, -3) * mm, "end": v(23.95, -2.99) * mm});
            skLineSegment(sketch, "E5259", {"start": v(23.95, -2.99) * mm, "end": v(24.27, -2.96) * mm});
            skLineSegment(sketch, "E5260", {"start": v(24.27, -2.96) * mm, "end": v(24.58, -2.94) * mm});
            skLineSegment(sketch, "E5261", {"start": v(24.58, -2.94) * mm, "end": v(24.9, -2.9) * mm});
            skLineSegment(sketch, "E5262", {"start": v(24.9, -2.9) * mm, "end": v(25.2, -2.87) * mm});
            skLineSegment(sketch, "E5263", {"start": v(25.2, -2.87) * mm, "end": v(25.52, -2.83) * mm});
            skLineSegment(sketch, "E5264", {"start": v(25.52, -2.83) * mm, "end": v(25.83, -2.78) * mm});
            skLineSegment(sketch, "E5265", {"start": v(25.83, -2.78) * mm, "end": v(26.15, -2.73) * mm});
            skLineSegment(sketch, "E5266", {"start": v(26.15, -2.73) * mm, "end": v(26.46, -2.68) * mm});
            skLineSegment(sketch, "E5267", {"start": v(26.46, -2.68) * mm, "end": v(26.77, -2.62) * mm});
            skLineSegment(sketch, "E5268", {"start": v(26.77, -2.62) * mm, "end": v(27.08, -2.56) * mm});
            skLineSegment(sketch, "E5269", {"start": v(27.08, -2.56) * mm, "end": v(27.4, -2.49) * mm});
            skLineSegment(sketch, "E5270", {"start": v(27.4, -2.49) * mm, "end": v(27.7, -2.41) * mm});
            skLineSegment(sketch, "E5271", {"start": v(27.7, -2.41) * mm, "end": v(28.02, -2.33) * mm});
            skLineSegment(sketch, "E5272", {"start": v(28.02, -2.33) * mm, "end": v(28.33, -2.25) * mm});
            skLineSegment(sketch, "E5273", {"start": v(28.33, -2.25) * mm, "end": v(28.64, -2.16) * mm});
            skLineSegment(sketch, "E5274", {"start": v(28.64, -2.16) * mm, "end": v(28.95, -2.07) * mm});
            skLineSegment(sketch, "E5275", {"start": v(28.95, -2.07) * mm, "end": v(29.26, -1.97) * mm});
            skLineSegment(sketch, "E5276", {"start": v(29.26, -1.97) * mm, "end": v(29.57, -1.87) * mm});
            skLineSegment(sketch, "E5277", {"start": v(29.57, -1.87) * mm, "end": v(29.88, -1.77) * mm});
            skLineSegment(sketch, "E5278", {"start": v(29.88, -1.77) * mm, "end": v(30.2, -1.65) * mm});
            skLineSegment(sketch, "E5279", {"start": v(30.2, -1.65) * mm, "end": v(30.5, -1.54) * mm});
            skLineSegment(sketch, "E5280", {"start": v(30.5, -1.54) * mm, "end": v(30.81, -1.42) * mm});
            skLineSegment(sketch, "E5281", {"start": v(30.81, -1.42) * mm, "end": v(31.12, -1.3) * mm});
            skLineSegment(sketch, "E5282", {"start": v(31.12, -1.3) * mm, "end": v(31.43, -1.16) * mm});
            skLineSegment(sketch, "E5283", {"start": v(31.43, -1.16) * mm, "end": v(31.74, -1.03) * mm});
            skLineSegment(sketch, "E5284", {"start": v(31.74, -1.03) * mm, "end": v(32.05, -0.89) * mm});
            skLineSegment(sketch, "E5285", {"start": v(32.05, -0.89) * mm, "end": v(32.09, -0.87) * mm});
            skLineSegment(sketch, "E5286", {"start": v(32.09, -0.87) * mm, "end": v(32.09, 0.63) * mm});
            skLineSegment(sketch, "E5287", {"start": v(32.09, 0.63) * mm, "end": v(32, 0.68) * mm});
            skLineSegment(sketch, "E5288", {"start": v(32, 0.68) * mm, "end": v(31.7, 0.84) * mm});
            skLineSegment(sketch, "E5289", {"start": v(31.7, 0.84) * mm, "end": v(31.38, 1) * mm});
            skLineSegment(sketch, "E5290", {"start": v(31.38, 1) * mm, "end": v(31.07, 1.15) * mm});
            skLineSegment(sketch, "E5291", {"start": v(31.07, 1.15) * mm, "end": v(30.77, 1.3) * mm});
            skLineSegment(sketch, "E5292", {"start": v(30.77, 1.3) * mm, "end": v(30.46, 1.44) * mm});
            skLineSegment(sketch, "E5293", {"start": v(30.46, 1.44) * mm, "end": v(30.15, 1.57) * mm});
            skLineSegment(sketch, "E5294", {"start": v(30.15, 1.57) * mm, "end": v(29.84, 1.7) * mm});
            skLineSegment(sketch, "E5295", {"start": v(29.84, 1.7) * mm, "end": v(29.53, 1.82) * mm});
            skLineSegment(sketch, "E5296", {"start": v(29.53, 1.82) * mm, "end": v(29.22, 1.94) * mm});
            skLineSegment(sketch, "E5297", {"start": v(29.22, 1.94) * mm, "end": v(28.91, 2.05) * mm});
            skLineSegment(sketch, "E5298", {"start": v(28.91, 2.05) * mm, "end": v(28.6, 2.16) * mm});
            skLineSegment(sketch, "E5299", {"start": v(28.6, 2.16) * mm, "end": v(28.3, 2.26) * mm});
            skLineSegment(sketch, "E5300", {"start": v(28.3, 2.26) * mm, "end": v(27.98, 2.36) * mm});
            skLineSegment(sketch, "E5301", {"start": v(27.98, 2.36) * mm, "end": v(27.67, 2.45) * mm});
            skLineSegment(sketch, "E5302", {"start": v(27.67, 2.45) * mm, "end": v(27.36, 2.53) * mm});
            skLineSegment(sketch, "E5303", {"start": v(27.36, 2.53) * mm, "end": v(27.05, 2.61) * mm});
            skLineSegment(sketch, "E5304", {"start": v(27.05, 2.61) * mm, "end": v(26.74, 2.69) * mm});
            skLineSegment(sketch, "E5305", {"start": v(26.74, 2.69) * mm, "end": v(26.43, 2.76) * mm});
            skLineSegment(sketch, "E5306", {"start": v(26.43, 2.76) * mm, "end": v(26.12, 2.82) * mm});
            skLineSegment(sketch, "E5307", {"start": v(26.12, 2.82) * mm, "end": v(25.81, 2.88) * mm});
            skLineSegment(sketch, "E5308", {"start": v(25.81, 2.88) * mm, "end": v(25.5, 2.93) * mm});
            skLineSegment(sketch, "E5309", {"start": v(25.5, 2.93) * mm, "end": v(25.2, 2.98) * mm});
            skLineSegment(sketch, "E5310", {"start": v(25.2, 2.98) * mm, "end": v(24.88, 3.02) * mm});
            skLineSegment(sketch, "E5311", {"start": v(24.88, 3.02) * mm, "end": v(24.57, 3.06) * mm});
            skLineSegment(sketch, "E5312", {"start": v(24.57, 3.06) * mm, "end": v(24.26, 3.09) * mm});
            skLineSegment(sketch, "E5313", {"start": v(24.26, 3.09) * mm, "end": v(23.94, 3.11) * mm});
            skLineSegment(sketch, "E5314", {"start": v(23.94, 3.11) * mm, "end": v(23.63, 3.13) * mm});
            skLineSegment(sketch, "E5315", {"start": v(23.63, 3.13) * mm, "end": v(23.32, 3.14) * mm});
            skLineSegment(sketch, "E5316", {"start": v(23.32, 3.14) * mm, "end": v(23, 3.15) * mm});
            skLineSegment(sketch, "E5317", {"start": v(23, 3.15) * mm, "end": v(22.7, 3.16) * mm});
            skLineSegment(sketch, "E5318", {"start": v(22.7, 3.16) * mm, "end": v(22.39, 3.15) * mm});
            skLineSegment(sketch, "E5319", {"start": v(22.39, 3.15) * mm, "end": v(22.08, 3.14) * mm});
            skLineSegment(sketch, "E5320", {"start": v(22.08, 3.14) * mm, "end": v(21.77, 3.13) * mm});
            skLineSegment(sketch, "E5321", {"start": v(21.77, 3.13) * mm, "end": v(21.46, 3.11) * mm});
            skLineSegment(sketch, "E5322", {"start": v(21.46, 3.11) * mm, "end": v(21.16, 3.09) * mm});
            skLineSegment(sketch, "E5323", {"start": v(21.16, 3.09) * mm, "end": v(20.85, 3.06) * mm});
            skLineSegment(sketch, "E5324", {"start": v(20.85, 3.06) * mm, "end": v(20.54, 3.02) * mm});
            skLineSegment(sketch, "E5325", {"start": v(20.54, 3.02) * mm, "end": v(20.23, 2.98) * mm});
            skLineSegment(sketch, "E5326", {"start": v(20.23, 2.98) * mm, "end": v(19.93, 2.94) * mm});
            skLineSegment(sketch, "E5327", {"start": v(19.93, 2.94) * mm, "end": v(19.62, 2.89) * mm});
            skLineSegment(sketch, "E5328", {"start": v(19.62, 2.89) * mm, "end": v(19.31, 2.83) * mm});
            skLineSegment(sketch, "E5329", {"start": v(19.31, 2.83) * mm, "end": v(19, 2.77) * mm});
            skLineSegment(sketch, "E5330", {"start": v(19, 2.77) * mm, "end": v(18.7, 2.7) * mm});
            skLineSegment(sketch, "E5331", {"start": v(18.7, 2.7) * mm, "end": v(18.4, 2.63) * mm});
            skLineSegment(sketch, "E5332", {"start": v(18.4, 2.63) * mm, "end": v(18.1, 2.55) * mm});
            skLineSegment(sketch, "E5333", {"start": v(18.1, 2.55) * mm, "end": v(17.79, 2.47) * mm});
            skLineSegment(sketch, "E5334", {"start": v(17.79, 2.47) * mm, "end": v(17.48, 2.38) * mm});
            skLineSegment(sketch, "E5335", {"start": v(17.48, 2.38) * mm, "end": v(17.18, 2.29) * mm});
            skLineSegment(sketch, "E5336", {"start": v(17.18, 2.29) * mm, "end": v(16.87, 2.19) * mm});
            skLineSegment(sketch, "E5337", {"start": v(16.87, 2.19) * mm, "end": v(16.56, 2.08) * mm});
            skLineSegment(sketch, "E5338", {"start": v(16.56, 2.08) * mm, "end": v(16.26, 1.97) * mm});
            skLineSegment(sketch, "E5339", {"start": v(16.26, 1.97) * mm, "end": v(15.96, 1.86) * mm});
            skLineSegment(sketch, "E5340", {"start": v(15.96, 1.86) * mm, "end": v(15.65, 1.74) * mm});
            skLineSegment(sketch, "E5341", {"start": v(15.65, 1.74) * mm, "end": v(15.35, 1.61) * mm});
            skLineSegment(sketch, "E5342", {"start": v(15.35, 1.61) * mm, "end": v(15.04, 1.48) * mm});
            skLineSegment(sketch, "E5343", {"start": v(15.04, 1.48) * mm, "end": v(14.74, 1.35) * mm});
            skLineSegment(sketch, "E5344", {"start": v(14.74, 1.35) * mm, "end": v(14.43, 1.2) * mm});
            skLineSegment(sketch, "E5345", {"start": v(14.43, 1.2) * mm, "end": v(14.13, 1.06) * mm});
            skLineSegment(sketch, "E5346", {"start": v(14.13, 1.06) * mm, "end": v(13.82, 0.9) * mm});
            skLineSegment(sketch, "E5347", {"start": v(13.82, 0.9) * mm, "end": v(13.52, 0.75) * mm});
            skLineSegment(sketch, "E5348", {"start": v(13.52, 0.75) * mm, "end": v(13.45, 0.7) * mm});
            skLineSegment(sketch, "E5349", {"start": v(13.45, 0.7) * mm, "end": v(13.45, -0.94) * mm});
            skLineSegment(sketch, "E5350", {"start": v(13.45, -0.94) * mm, "end": v(13.47, -0.95) * mm});
            skLineSegment(sketch, "E5351", {"start": v(13.47, -0.95) * mm, "end": v(13.77, -1.08) * mm});
            skLineSegment(sketch, "E5352", {"start": v(13.77, -1.08) * mm, "end": v(14.08, -1.21) * mm});
            skLineSegment(sketch, "E5353", {"start": v(14.08, -1.21) * mm, "end": v(14.38, -1.34) * mm});
            skLineSegment(sketch, "E5354", {"start": v(14.38, -1.34) * mm, "end": v(14.69, -1.46) * mm});
            skLineSegment(sketch, "E5355", {"start": v(14.69, -1.46) * mm, "end": v(15, -1.58) * mm});
            skLineSegment(sketch, "E5356", {"start": v(15, -1.58) * mm, "end": v(15.3, -1.7) * mm});
            skLineSegment(sketch, "E5357", {"start": v(15.3, -1.7) * mm, "end": v(15.6, -1.8) * mm});
            skLineSegment(sketch, "E5358", {"start": v(15.6, -1.8) * mm, "end": v(15.91, -1.9) * mm});
            skLineSegment(sketch, "E5359", {"start": v(15.91, -1.9) * mm, "end": v(16.22, -2) * mm});
            skLineSegment(sketch, "E5360", {"start": v(16.22, -2) * mm, "end": v(16.53, -2.1) * mm});
            skLineSegment(sketch, "E5361", {"start": v(16.53, -2.1) * mm, "end": v(16.83, -2.19) * mm});
            skLineSegment(sketch, "E5362", {"start": v(16.83, -2.19) * mm, "end": v(17.14, -2.27) * mm});
            skLineSegment(sketch, "E5363", {"start": v(17.14, -2.27) * mm, "end": v(17.45, -2.35) * mm});
            skLineSegment(sketch, "E5364", {"start": v(17.45, -2.35) * mm, "end": v(17.75, -2.43) * mm});
            skLineSegment(sketch, "E5365", {"start": v(17.75, -2.43) * mm, "end": v(18.06, -2.5) * mm});
            skLineSegment(sketch, "E5366", {"start": v(18.06, -2.5) * mm, "end": v(18.37, -2.57) * mm});
            skLineSegment(sketch, "E5367", {"start": v(18.37, -2.57) * mm, "end": v(18.67, -2.63) * mm});
            skLineSegment(sketch, "E5368", {"start": v(18.67, -2.63) * mm, "end": v(18.98, -2.69) * mm});
            skLineSegment(sketch, "E5369", {"start": v(18.98, -2.69) * mm, "end": v(19.3, -2.74) * mm});
            skLineSegment(sketch, "E5370", {"start": v(19.3, -2.74) * mm, "end": v(19.6, -2.8) * mm});
            skLineSegment(sketch, "E5371", {"start": v(19.6, -2.8) * mm, "end": v(19.9, -2.84) * mm});
            skLineSegment(sketch, "E5372", {"start": v(19.9, -2.84) * mm, "end": v(20.22, -2.87) * mm});
            skLineSegment(sketch, "E5373", {"start": v(20.22, -2.87) * mm, "end": v(20.53, -2.9) * mm});
            skLineSegment(sketch, "E5374", {"start": v(20.53, -2.9) * mm, "end": v(20.83, -2.94) * mm});
            skLineSegment(sketch, "E5375", {"start": v(20.83, -2.94) * mm, "end": v(21.14, -2.97) * mm});
            skLineSegment(sketch, "E5376", {"start": v(21.14, -2.97) * mm, "end": v(21.45, -2.99) * mm});
            skLineSegment(sketch, "E5377", {"start": v(21.45, -2.99) * mm, "end": v(21.76, -3) * mm});
            skLineSegment(sketch, "E5378", {"start": v(21.76, -3) * mm, "end": v(22.07, -3.01) * mm});
            skLineSegment(sketch, "E5379", {"start": v(22.07, -3.01) * mm, "end": v(22.38, -3.02) * mm});
            skLineSegment(sketch, "E5380", {"start": v(22.38, -3.02) * mm, "end": v(22.7, -3.02) * mm});
            skLineSegment(sketch, "E5381", {"start": v(22.7, -3.02) * mm, "end": v(23, -3.02) * mm});
            skLineSegment(sketch, "E5382", {"start": v(-23.88, -3.15) * mm, "end": v(-23.57, -3.15) * mm});
            skLineSegment(sketch, "E5383", {"start": v(-23.57, -3.15) * mm, "end": v(-23.26, -3.13) * mm});
            skLineSegment(sketch, "E5384", {"start": v(-23.26, -3.13) * mm, "end": v(-22.96, -3.11) * mm});
            skLineSegment(sketch, "E5385", {"start": v(-22.96, -3.11) * mm, "end": v(-22.65, -3.09) * mm});
            skLineSegment(sketch, "E5386", {"start": v(-22.65, -3.09) * mm, "end": v(-22.34, -3.06) * mm});
            skLineSegment(sketch, "E5387", {"start": v(-22.34, -3.06) * mm, "end": v(-22.03, -3.02) * mm});
            skLineSegment(sketch, "E5388", {"start": v(-22.03, -3.02) * mm, "end": v(-21.73, -2.98) * mm});
            skLineSegment(sketch, "E5389", {"start": v(-21.73, -2.98) * mm, "end": v(-21.42, -2.94) * mm});
            skLineSegment(sketch, "E5390", {"start": v(-21.42, -2.94) * mm, "end": v(-21.11, -2.89) * mm});
            skLineSegment(sketch, "E5391", {"start": v(-21.11, -2.89) * mm, "end": v(-20.8, -2.83) * mm});
            skLineSegment(sketch, "E5392", {"start": v(-20.8, -2.83) * mm, "end": v(-20.5, -2.77) * mm});
            skLineSegment(sketch, "E5393", {"start": v(-20.5, -2.77) * mm, "end": v(-20.2, -2.7) * mm});
            skLineSegment(sketch, "E5394", {"start": v(-20.2, -2.7) * mm, "end": v(-19.89, -2.63) * mm});
            skLineSegment(sketch, "E5395", {"start": v(-19.89, -2.63) * mm, "end": v(-19.58, -2.55) * mm});
            skLineSegment(sketch, "E5396", {"start": v(-19.58, -2.55) * mm, "end": v(-19.28, -2.47) * mm});
            skLineSegment(sketch, "E5397", {"start": v(-19.28, -2.47) * mm, "end": v(-18.97, -2.38) * mm});
            skLineSegment(sketch, "E5398", {"start": v(-18.97, -2.38) * mm, "end": v(-18.67, -2.29) * mm});
            skLineSegment(sketch, "E5399", {"start": v(-18.67, -2.29) * mm, "end": v(-18.36, -2.19) * mm});
            skLineSegment(sketch, "E5400", {"start": v(-18.36, -2.19) * mm, "end": v(-18.06, -2.08) * mm});
            skLineSegment(sketch, "E5401", {"start": v(-18.06, -2.08) * mm, "end": v(-17.75, -1.98) * mm});
            skLineSegment(sketch, "E5402", {"start": v(-17.75, -1.98) * mm, "end": v(-17.45, -1.86) * mm});
            skLineSegment(sketch, "E5403", {"start": v(-17.45, -1.86) * mm, "end": v(-17.14, -1.74) * mm});
            skLineSegment(sketch, "E5404", {"start": v(-17.14, -1.74) * mm, "end": v(-16.84, -1.61) * mm});
            skLineSegment(sketch, "E5405", {"start": v(-16.84, -1.61) * mm, "end": v(-16.53, -1.48) * mm});
            skLineSegment(sketch, "E5406", {"start": v(-16.53, -1.48) * mm, "end": v(-16.23, -1.35) * mm});
            skLineSegment(sketch, "E5407", {"start": v(-16.23, -1.35) * mm, "end": v(-15.93, -1.2) * mm});
            skLineSegment(sketch, "E5408", {"start": v(-15.93, -1.2) * mm, "end": v(-15.62, -1.06) * mm});
            skLineSegment(sketch, "E5409", {"start": v(-15.62, -1.06) * mm, "end": v(-15.32, -0.9) * mm});
            skLineSegment(sketch, "E5410", {"start": v(-15.32, -0.9) * mm, "end": v(-15.01, -0.75) * mm});
            skLineSegment(sketch, "E5411", {"start": v(-15.01, -0.75) * mm, "end": v(-14.94, -0.71) * mm});
            skLineSegment(sketch, "E5412", {"start": v(-14.94, -0.71) * mm, "end": v(-14.94, 0.94) * mm});
            skLineSegment(sketch, "E5413", {"start": v(-14.94, 0.94) * mm, "end": v(-14.96, 0.95) * mm});
            skLineSegment(sketch, "E5414", {"start": v(-14.96, 0.95) * mm, "end": v(-15.27, 1.08) * mm});
            skLineSegment(sketch, "E5415", {"start": v(-15.27, 1.08) * mm, "end": v(-15.57, 1.21) * mm});
            skLineSegment(sketch, "E5416", {"start": v(-15.57, 1.21) * mm, "end": v(-15.88, 1.34) * mm});
            skLineSegment(sketch, "E5417", {"start": v(-15.88, 1.34) * mm, "end": v(-16.18, 1.46) * mm});
            skLineSegment(sketch, "E5418", {"start": v(-16.18, 1.46) * mm, "end": v(-16.49, 1.58) * mm});
            skLineSegment(sketch, "E5419", {"start": v(-16.49, 1.58) * mm, "end": v(-16.8, 1.7) * mm});
            skLineSegment(sketch, "E5420", {"start": v(-16.8, 1.7) * mm, "end": v(-17.1, 1.8) * mm});
            skLineSegment(sketch, "E5421", {"start": v(-17.1, 1.8) * mm, "end": v(-17.4, 1.9) * mm});
            skLineSegment(sketch, "E5422", {"start": v(-17.4, 1.9) * mm, "end": v(-17.71, 2) * mm});
            skLineSegment(sketch, "E5423", {"start": v(-17.71, 2) * mm, "end": v(-18.02, 2.1) * mm});
            skLineSegment(sketch, "E5424", {"start": v(-18.02, 2.1) * mm, "end": v(-18.32, 2.19) * mm});
            skLineSegment(sketch, "E5425", {"start": v(-18.32, 2.19) * mm, "end": v(-18.63, 2.27) * mm});
            skLineSegment(sketch, "E5426", {"start": v(-18.63, 2.27) * mm, "end": v(-18.94, 2.35) * mm});
            skLineSegment(sketch, "E5427", {"start": v(-18.94, 2.35) * mm, "end": v(-19.24, 2.43) * mm});
            skLineSegment(sketch, "E5428", {"start": v(-19.24, 2.43) * mm, "end": v(-19.55, 2.5) * mm});
            skLineSegment(sketch, "E5429", {"start": v(-19.55, 2.5) * mm, "end": v(-19.86, 2.57) * mm});
            skLineSegment(sketch, "E5430", {"start": v(-19.86, 2.57) * mm, "end": v(-20.17, 2.63) * mm});
            skLineSegment(sketch, "E5431", {"start": v(-20.17, 2.63) * mm, "end": v(-20.48, 2.69) * mm});
            skLineSegment(sketch, "E5432", {"start": v(-20.48, 2.69) * mm, "end": v(-20.78, 2.74) * mm});
            skLineSegment(sketch, "E5433", {"start": v(-20.78, 2.74) * mm, "end": v(-21.1, 2.8) * mm});
            skLineSegment(sketch, "E5434", {"start": v(-21.1, 2.8) * mm, "end": v(-21.4, 2.83) * mm});
            skLineSegment(sketch, "E5435", {"start": v(-21.4, 2.83) * mm, "end": v(-21.7, 2.87) * mm});
            skLineSegment(sketch, "E5436", {"start": v(-21.7, 2.87) * mm, "end": v(-22.02, 2.9) * mm});
            skLineSegment(sketch, "E5437", {"start": v(-22.02, 2.9) * mm, "end": v(-22.33, 2.94) * mm});
            skLineSegment(sketch, "E5438", {"start": v(-22.33, 2.94) * mm, "end": v(-22.64, 2.96) * mm});
            skLineSegment(sketch, "E5439", {"start": v(-22.64, 2.96) * mm, "end": v(-22.95, 2.99) * mm});
            skLineSegment(sketch, "E5440", {"start": v(-22.95, 2.99) * mm, "end": v(-23.26, 3) * mm});
            skLineSegment(sketch, "E5441", {"start": v(-23.26, 3) * mm, "end": v(-23.57, 3.01) * mm});
            skLineSegment(sketch, "E5442", {"start": v(-23.57, 3.01) * mm, "end": v(-23.88, 3.02) * mm});
            skLineSegment(sketch, "E5443", {"start": v(-23.88, 3.02) * mm, "end": v(-24.19, 3.02) * mm});
            skLineSegment(sketch, "E5444", {"start": v(-24.19, 3.02) * mm, "end": v(-24.5, 3.02) * mm});
            skLineSegment(sketch, "E5445", {"start": v(-24.5, 3.02) * mm, "end": v(-24.82, 3.01) * mm});
            skLineSegment(sketch, "E5446", {"start": v(-24.82, 3.01) * mm, "end": v(-25.13, 3) * mm});
            skLineSegment(sketch, "E5447", {"start": v(-25.13, 3) * mm, "end": v(-25.45, 2.98) * mm});
            skLineSegment(sketch, "E5448", {"start": v(-25.45, 2.98) * mm, "end": v(-25.76, 2.96) * mm});
            skLineSegment(sketch, "E5449", {"start": v(-25.76, 2.96) * mm, "end": v(-26.07, 2.94) * mm});
            skLineSegment(sketch, "E5450", {"start": v(-26.07, 2.94) * mm, "end": v(-26.39, 2.9) * mm});
            skLineSegment(sketch, "E5451", {"start": v(-26.39, 2.9) * mm, "end": v(-26.7, 2.87) * mm});
            skLineSegment(sketch, "E5452", {"start": v(-26.7, 2.87) * mm, "end": v(-27.01, 2.83) * mm});
            skLineSegment(sketch, "E5453", {"start": v(-27.01, 2.83) * mm, "end": v(-27.33, 2.78) * mm});
            skLineSegment(sketch, "E5454", {"start": v(-27.33, 2.78) * mm, "end": v(-27.64, 2.73) * mm});
            skLineSegment(sketch, "E5455", {"start": v(-27.64, 2.73) * mm, "end": v(-27.95, 2.68) * mm});
            skLineSegment(sketch, "E5456", {"start": v(-27.95, 2.68) * mm, "end": v(-28.26, 2.62) * mm});
            skLineSegment(sketch, "E5457", {"start": v(-28.26, 2.62) * mm, "end": v(-28.58, 2.55) * mm});
            skLineSegment(sketch, "E5458", {"start": v(-28.58, 2.55) * mm, "end": v(-28.89, 2.49) * mm});
            skLineSegment(sketch, "E5459", {"start": v(-28.89, 2.49) * mm, "end": v(-29.2, 2.41) * mm});
            skLineSegment(sketch, "E5460", {"start": v(-29.2, 2.41) * mm, "end": v(-29.51, 2.33) * mm});
            skLineSegment(sketch, "E5461", {"start": v(-29.51, 2.33) * mm, "end": v(-29.82, 2.25) * mm});
            skLineSegment(sketch, "E5462", {"start": v(-29.82, 2.25) * mm, "end": v(-30.13, 2.16) * mm});
            skLineSegment(sketch, "E5463", {"start": v(-30.13, 2.16) * mm, "end": v(-30.44, 2.07) * mm});
            skLineSegment(sketch, "E5464", {"start": v(-30.44, 2.07) * mm, "end": v(-30.76, 1.97) * mm});
            skLineSegment(sketch, "E5465", {"start": v(-30.76, 1.97) * mm, "end": v(-31.07, 1.87) * mm});
            skLineSegment(sketch, "E5466", {"start": v(-31.07, 1.87) * mm, "end": v(-31.38, 1.76) * mm});
            skLineSegment(sketch, "E5467", {"start": v(-31.38, 1.76) * mm, "end": v(-31.69, 1.65) * mm});
            skLineSegment(sketch, "E5468", {"start": v(-31.69, 1.65) * mm, "end": v(-32, 1.54) * mm});
            skLineSegment(sketch, "E5469", {"start": v(-32, 1.54) * mm, "end": v(-32.3, 1.42) * mm});
            skLineSegment(sketch, "E5470", {"start": v(-32.3, 1.42) * mm, "end": v(-32.62, 1.3) * mm});
            skLineSegment(sketch, "E5471", {"start": v(-32.62, 1.3) * mm, "end": v(-32.92, 1.16) * mm});
            skLineSegment(sketch, "E5472", {"start": v(-32.92, 1.16) * mm, "end": v(-33.23, 1.03) * mm});
            skLineSegment(sketch, "E5473", {"start": v(-33.23, 1.03) * mm, "end": v(-33.54, 0.89) * mm});
            skLineSegment(sketch, "E5474", {"start": v(-33.54, 0.89) * mm, "end": v(-33.58, 0.87) * mm});
            skLineSegment(sketch, "E5475", {"start": v(-33.58, 0.87) * mm, "end": v(-33.58, -0.63) * mm});
            skLineSegment(sketch, "E5476", {"start": v(-33.58, -0.63) * mm, "end": v(-33.5, -0.68) * mm});
            skLineSegment(sketch, "E5477", {"start": v(-33.5, -0.68) * mm, "end": v(-33.18, -0.84) * mm});
            skLineSegment(sketch, "E5478", {"start": v(-33.18, -0.84) * mm, "end": v(-32.87, -1) * mm});
            skLineSegment(sketch, "E5479", {"start": v(-32.87, -1) * mm, "end": v(-32.57, -1.15) * mm});
            skLineSegment(sketch, "E5480", {"start": v(-32.57, -1.15) * mm, "end": v(-32.26, -1.3) * mm});
            skLineSegment(sketch, "E5481", {"start": v(-32.26, -1.3) * mm, "end": v(-31.95, -1.44) * mm});
            skLineSegment(sketch, "E5482", {"start": v(-31.95, -1.44) * mm, "end": v(-31.64, -1.57) * mm});
            skLineSegment(sketch, "E5483", {"start": v(-31.64, -1.57) * mm, "end": v(-31.33, -1.7) * mm});
            skLineSegment(sketch, "E5484", {"start": v(-31.33, -1.7) * mm, "end": v(-31.02, -1.82) * mm});
            skLineSegment(sketch, "E5485", {"start": v(-31.02, -1.82) * mm, "end": v(-30.71, -1.94) * mm});
            skLineSegment(sketch, "E5486", {"start": v(-30.71, -1.94) * mm, "end": v(-30.4, -2.05) * mm});
            skLineSegment(sketch, "E5487", {"start": v(-30.4, -2.05) * mm, "end": v(-30.1, -2.16) * mm});
            skLineSegment(sketch, "E5488", {"start": v(-30.1, -2.16) * mm, "end": v(-29.79, -2.26) * mm});
            skLineSegment(sketch, "E5489", {"start": v(-29.79, -2.26) * mm, "end": v(-29.48, -2.36) * mm});
            skLineSegment(sketch, "E5490", {"start": v(-29.48, -2.36) * mm, "end": v(-29.17, -2.45) * mm});
            skLineSegment(sketch, "E5491", {"start": v(-29.17, -2.45) * mm, "end": v(-28.86, -2.54) * mm});
            skLineSegment(sketch, "E5492", {"start": v(-28.86, -2.54) * mm, "end": v(-28.55, -2.62) * mm});
            skLineSegment(sketch, "E5493", {"start": v(-28.55, -2.62) * mm, "end": v(-28.24, -2.69) * mm});
            skLineSegment(sketch, "E5494", {"start": v(-28.24, -2.69) * mm, "end": v(-27.93, -2.76) * mm});
            skLineSegment(sketch, "E5495", {"start": v(-27.93, -2.76) * mm, "end": v(-27.62, -2.82) * mm});
            skLineSegment(sketch, "E5496", {"start": v(-27.62, -2.82) * mm, "end": v(-27.3, -2.88) * mm});
            skLineSegment(sketch, "E5497", {"start": v(-27.3, -2.88) * mm, "end": v(-27, -2.93) * mm});
            skLineSegment(sketch, "E5498", {"start": v(-27, -2.93) * mm, "end": v(-26.68, -2.98) * mm});
            skLineSegment(sketch, "E5499", {"start": v(-26.68, -2.98) * mm, "end": v(-26.37, -3.02) * mm});
            skLineSegment(sketch, "E5500", {"start": v(-26.37, -3.02) * mm, "end": v(-26.06, -3.06) * mm});
            skLineSegment(sketch, "E5501", {"start": v(-26.06, -3.06) * mm, "end": v(-25.75, -3.09) * mm});
            skLineSegment(sketch, "E5502", {"start": v(-25.75, -3.09) * mm, "end": v(-25.44, -3.11) * mm});
            skLineSegment(sketch, "E5503", {"start": v(-25.44, -3.11) * mm, "end": v(-25.13, -3.13) * mm});
            skLineSegment(sketch, "E5504", {"start": v(-25.13, -3.13) * mm, "end": v(-24.81, -3.15) * mm});
            skLineSegment(sketch, "E5505", {"start": v(-24.81, -3.15) * mm, "end": v(-24.5, -3.15) * mm});
            skLineSegment(sketch, "E5506", {"start": v(-24.5, -3.15) * mm, "end": v(-24.19, -3.16) * mm});
            skLineSegment(sketch, "E5507", {"start": v(-24.19, -3.16) * mm, "end": v(-23.88, -3.15) * mm});
            skLineSegment(sketch, "E5508", {"start": v(-3.84, -40.93) * mm, "end": v(-4.08, -40.35) * mm});
            skLineSegment(sketch, "E5509", {"start": v(-4.08, -40.35) * mm, "end": v(-4.32, -39.77) * mm});
            skLineSegment(sketch, "E5510", {"start": v(-4.32, -39.77) * mm, "end": v(-4.54, -39.2) * mm});
            skLineSegment(sketch, "E5511", {"start": v(-4.54, -39.2) * mm, "end": v(-4.76, -38.61) * mm});
            skLineSegment(sketch, "E5512", {"start": v(-4.76, -38.61) * mm, "end": v(-4.97, -38.03) * mm});
            skLineSegment(sketch, "E5513", {"start": v(-4.97, -38.03) * mm, "end": v(-5.17, -37.45) * mm});
            skLineSegment(sketch, "E5514", {"start": v(-5.17, -37.45) * mm, "end": v(-5.37, -36.87) * mm});
            skLineSegment(sketch, "E5515", {"start": v(-5.37, -36.87) * mm, "end": v(-5.55, -36.29) * mm});
            skLineSegment(sketch, "E5516", {"start": v(-5.55, -36.29) * mm, "end": v(-5.73, -35.7) * mm});
            skLineSegment(sketch, "E5517", {"start": v(-5.73, -35.7) * mm, "end": v(-5.9, -35.12) * mm});
            skLineSegment(sketch, "E5518", {"start": v(-5.9, -35.12) * mm, "end": v(-6.06, -34.54) * mm});
            skLineSegment(sketch, "E5519", {"start": v(-6.06, -34.54) * mm, "end": v(-6.22, -33.95) * mm});
            skLineSegment(sketch, "E5520", {"start": v(-6.22, -33.95) * mm, "end": v(-6.36, -33.37) * mm});
            skLineSegment(sketch, "E5521", {"start": v(-6.36, -33.37) * mm, "end": v(-6.5, -32.78) * mm});
            skLineSegment(sketch, "E5522", {"start": v(-6.5, -32.78) * mm, "end": v(-6.63, -32.2) * mm});
            skLineSegment(sketch, "E5523", {"start": v(-6.63, -32.2) * mm, "end": v(-6.75, -31.6) * mm});
            skLineSegment(sketch, "E5524", {"start": v(-6.75, -31.6) * mm, "end": v(-6.86, -31.02) * mm});
            skLineSegment(sketch, "E5525", {"start": v(-6.86, -31.02) * mm, "end": v(-6.96, -30.43) * mm});
            skLineSegment(sketch, "E5526", {"start": v(-6.96, -30.43) * mm, "end": v(-7.06, -29.84) * mm});
            skLineSegment(sketch, "E5527", {"start": v(-7.06, -29.84) * mm, "end": v(-7.15, -29.26) * mm});
            skLineSegment(sketch, "E5528", {"start": v(-7.15, -29.26) * mm, "end": v(-7.23, -28.67) * mm});
            skLineSegment(sketch, "E5529", {"start": v(-7.23, -28.67) * mm, "end": v(-7.3, -28.08) * mm});
            skLineSegment(sketch, "E5530", {"start": v(-7.3, -28.08) * mm, "end": v(-7.36, -27.49) * mm});
            skLineSegment(sketch, "E5531", {"start": v(-7.36, -27.49) * mm, "end": v(-7.42, -26.9) * mm});
            skLineSegment(sketch, "E5532", {"start": v(-7.42, -26.9) * mm, "end": v(-7.46, -26.3) * mm});
            skLineSegment(sketch, "E5533", {"start": v(-7.46, -26.3) * mm, "end": v(-7.5, -25.71) * mm});
            skLineSegment(sketch, "E5534", {"start": v(-7.5, -25.71) * mm, "end": v(-7.53, -25.12) * mm});
            skLineSegment(sketch, "E5535", {"start": v(-7.53, -25.12) * mm, "end": v(-7.55, -24.52) * mm});
            skLineSegment(sketch, "E5536", {"start": v(-7.55, -24.52) * mm, "end": v(-7.56, -23.93) * mm});
            skLineSegment(sketch, "E5537", {"start": v(-7.56, -23.93) * mm, "end": v(-7.57, -23.34) * mm});
            skLineSegment(sketch, "E5538", {"start": v(-7.57, -23.34) * mm, "end": v(-7.56, -22.75) * mm});
            skLineSegment(sketch, "E5539", {"start": v(-7.56, -22.75) * mm, "end": v(-7.55, -22.17) * mm});
            skLineSegment(sketch, "E5540", {"start": v(-7.55, -22.17) * mm, "end": v(-7.53, -21.58) * mm});
            skLineSegment(sketch, "E5541", {"start": v(-7.53, -21.58) * mm, "end": v(-7.5, -21) * mm});
            skLineSegment(sketch, "E5542", {"start": v(-7.5, -21) * mm, "end": v(-7.46, -20.41) * mm});
            skLineSegment(sketch, "E5543", {"start": v(-7.46, -20.41) * mm, "end": v(-7.42, -19.83) * mm});
            skLineSegment(sketch, "E5544", {"start": v(-7.42, -19.83) * mm, "end": v(-7.37, -19.25) * mm});
            skLineSegment(sketch, "E5545", {"start": v(-7.37, -19.25) * mm, "end": v(-7.3, -18.66) * mm});
            skLineSegment(sketch, "E5546", {"start": v(-7.3, -18.66) * mm, "end": v(-7.24, -18.08) * mm});
            skLineSegment(sketch, "E5547", {"start": v(-7.24, -18.08) * mm, "end": v(-7.16, -17.5) * mm});
            skLineSegment(sketch, "E5548", {"start": v(-7.16, -17.5) * mm, "end": v(-7.07, -16.92) * mm});
            skLineSegment(sketch, "E5549", {"start": v(-7.07, -16.92) * mm, "end": v(-6.98, -16.34) * mm});
            skLineSegment(sketch, "E5550", {"start": v(-6.98, -16.34) * mm, "end": v(-6.88, -15.76) * mm});
            skLineSegment(sketch, "E5551", {"start": v(-6.88, -15.76) * mm, "end": v(-6.77, -15.18) * mm});
            skLineSegment(sketch, "E5552", {"start": v(-6.77, -15.18) * mm, "end": v(-6.65, -14.6) * mm});
            skLineSegment(sketch, "E5553", {"start": v(-6.65, -14.6) * mm, "end": v(-6.53, -14.02) * mm});
            skLineSegment(sketch, "E5554", {"start": v(-6.53, -14.02) * mm, "end": v(-6.4, -13.45) * mm});
            skLineSegment(sketch, "E5555", {"start": v(-6.4, -13.45) * mm, "end": v(-6.25, -12.87) * mm});
            skLineSegment(sketch, "E5556", {"start": v(-6.25, -12.87) * mm, "end": v(-6.1, -12.3) * mm});
            skLineSegment(sketch, "E5557", {"start": v(-6.1, -12.3) * mm, "end": v(-5.95, -11.72) * mm});
            skLineSegment(sketch, "E5558", {"start": v(-5.95, -11.72) * mm, "end": v(-5.78, -11.14) * mm});
            skLineSegment(sketch, "E5559", {"start": v(-5.78, -11.14) * mm, "end": v(-5.6, -10.57) * mm});
            skLineSegment(sketch, "E5560", {"start": v(-5.6, -10.57) * mm, "end": v(-5.43, -10) * mm});
            skLineSegment(sketch, "E5561", {"start": v(-5.43, -10) * mm, "end": v(-5.24, -9.42) * mm});
            skLineSegment(sketch, "E5562", {"start": v(-5.24, -9.42) * mm, "end": v(-5.04, -8.85) * mm});
            skLineSegment(sketch, "E5563", {"start": v(-5.04, -8.85) * mm, "end": v(-4.84, -8.27) * mm});
            skLineSegment(sketch, "E5564", {"start": v(-4.84, -8.27) * mm, "end": v(-4.63, -7.7) * mm});
            skLineSegment(sketch, "E5565", {"start": v(-4.63, -7.7) * mm, "end": v(-4.4, -7.13) * mm});
            skLineSegment(sketch, "E5566", {"start": v(-4.4, -7.13) * mm, "end": v(-4.18, -6.56) * mm});
            skLineSegment(sketch, "E5567", {"start": v(-4.18, -6.56) * mm, "end": v(-3.94, -6) * mm});
            skLineSegment(sketch, "E5568", {"start": v(-3.94, -6) * mm, "end": v(-3.7, -5.42) * mm});
            skLineSegment(sketch, "E5569", {"start": v(-3.7, -5.42) * mm, "end": v(-3.55, -5.07) * mm});
            skLineSegment(sketch, "E5570", {"start": v(-3.55, -5.07) * mm, "end": v(-3.85, -4.9) * mm});
            skLineSegment(sketch, "E5571", {"start": v(-3.85, -4.9) * mm, "end": v(-4.15, -4.69) * mm});
            skLineSegment(sketch, "E5572", {"start": v(-4.15, -4.69) * mm, "end": v(-4.44, -4.47) * mm});
            skLineSegment(sketch, "E5573", {"start": v(-4.44, -4.47) * mm, "end": v(-4.71, -4.23) * mm});
            skLineSegment(sketch, "E5574", {"start": v(-4.71, -4.23) * mm, "end": v(-4.97, -3.97) * mm});
            skLineSegment(sketch, "E5575", {"start": v(-4.97, -3.97) * mm, "end": v(-5.21, -3.7) * mm});
            skLineSegment(sketch, "E5576", {"start": v(-5.21, -3.7) * mm, "end": v(-5.44, -3.4) * mm});
            skLineSegment(sketch, "E5577", {"start": v(-5.44, -3.4) * mm, "end": v(-5.64, -3.1) * mm});
            skLineSegment(sketch, "E5578", {"start": v(-5.64, -3.1) * mm, "end": v(-5.83, -2.8) * mm});
            skLineSegment(sketch, "E5579", {"start": v(-5.83, -2.8) * mm, "end": v(-5.96, -2.52) * mm});
            skLineSegment(sketch, "E5580", {"start": v(-5.96, -2.52) * mm, "end": v(-6.17, -2.62) * mm});
            skLineSegment(sketch, "E5581", {"start": v(-6.17, -2.62) * mm, "end": v(-6.74, -2.9) * mm});
            skLineSegment(sketch, "E5582", {"start": v(-6.74, -2.9) * mm, "end": v(-7.3, -3.18) * mm});
            skLineSegment(sketch, "E5583", {"start": v(-7.3, -3.18) * mm, "end": v(-7.88, -3.44) * mm});
            skLineSegment(sketch, "E5584", {"start": v(-7.88, -3.44) * mm, "end": v(-8.45, -3.7) * mm});
            skLineSegment(sketch, "E5585", {"start": v(-8.45, -3.7) * mm, "end": v(-9.02, -3.95) * mm});
            skLineSegment(sketch, "E5586", {"start": v(-9.02, -3.95) * mm, "end": v(-9.6, -4.19) * mm});
            skLineSegment(sketch, "E5587", {"start": v(-9.6, -4.19) * mm, "end": v(-10.17, -4.41) * mm});
            skLineSegment(sketch, "E5588", {"start": v(-10.17, -4.41) * mm, "end": v(-10.74, -4.63) * mm});
            skLineSegment(sketch, "E5589", {"start": v(-10.74, -4.63) * mm, "end": v(-11.31, -4.84) * mm});
            skLineSegment(sketch, "E5590", {"start": v(-11.31, -4.84) * mm, "end": v(-11.89, -5.05) * mm});
            skLineSegment(sketch, "E5591", {"start": v(-11.89, -5.05) * mm, "end": v(-12.46, -5.24) * mm});
            skLineSegment(sketch, "E5592", {"start": v(-12.46, -5.24) * mm, "end": v(-13.04, -5.42) * mm});
            skLineSegment(sketch, "E5593", {"start": v(-13.04, -5.42) * mm, "end": v(-13.62, -5.6) * mm});
            skLineSegment(sketch, "E5594", {"start": v(-13.62, -5.6) * mm, "end": v(-14.2, -5.76) * mm});
            skLineSegment(sketch, "E5595", {"start": v(-14.2, -5.76) * mm, "end": v(-14.77, -5.91) * mm});
            skLineSegment(sketch, "E5596", {"start": v(-14.77, -5.91) * mm, "end": v(-15.35, -6.06) * mm});
            skLineSegment(sketch, "E5597", {"start": v(-15.35, -6.06) * mm, "end": v(-15.93, -6.2) * mm});
            skLineSegment(sketch, "E5598", {"start": v(-15.93, -6.2) * mm, "end": v(-16.5, -6.32) * mm});
            skLineSegment(sketch, "E5599", {"start": v(-16.5, -6.32) * mm, "end": v(-17.09, -6.44) * mm});
            skLineSegment(sketch, "E5600", {"start": v(-17.09, -6.44) * mm, "end": v(-17.67, -6.55) * mm});
            skLineSegment(sketch, "E5601", {"start": v(-17.67, -6.55) * mm, "end": v(-18.25, -6.65) * mm});
            skLineSegment(sketch, "E5602", {"start": v(-18.25, -6.65) * mm, "end": v(-18.83, -6.74) * mm});
            skLineSegment(sketch, "E5603", {"start": v(-18.83, -6.74) * mm, "end": v(-19.4, -6.82) * mm});
            skLineSegment(sketch, "E5604", {"start": v(-19.4, -6.82) * mm, "end": v(-20, -6.9) * mm});
            skLineSegment(sketch, "E5605", {"start": v(-20, -6.9) * mm, "end": v(-20.57, -6.95) * mm});
            skLineSegment(sketch, "E5606", {"start": v(-20.57, -6.95) * mm, "end": v(-21.16, -7) * mm});
            skLineSegment(sketch, "E5607", {"start": v(-21.16, -7) * mm, "end": v(-21.74, -7.05) * mm});
            skLineSegment(sketch, "E5608", {"start": v(-21.74, -7.05) * mm, "end": v(-22.33, -7.08) * mm});
            skLineSegment(sketch, "E5609", {"start": v(-22.33, -7.08) * mm, "end": v(-22.91, -7.1) * mm});
            skLineSegment(sketch, "E5610", {"start": v(-22.91, -7.1) * mm, "end": v(-23.5, -7.12) * mm});
            skLineSegment(sketch, "E5611", {"start": v(-23.5, -7.12) * mm, "end": v(-24.08, -7.12) * mm});
            skLineSegment(sketch, "E5612", {"start": v(-24.08, -7.12) * mm, "end": v(-24.68, -7.12) * mm});
            skLineSegment(sketch, "E5613", {"start": v(-24.68, -7.12) * mm, "end": v(-25.27, -7.1) * mm});
            skLineSegment(sketch, "E5614", {"start": v(-25.27, -7.1) * mm, "end": v(-25.86, -7.08) * mm});
            skLineSegment(sketch, "E5615", {"start": v(-25.86, -7.08) * mm, "end": v(-26.46, -7.04) * mm});
            skLineSegment(sketch, "E5616", {"start": v(-26.46, -7.04) * mm, "end": v(-27.05, -7) * mm});
            skLineSegment(sketch, "E5617", {"start": v(-27.05, -7) * mm, "end": v(-27.64, -6.95) * mm});
            skLineSegment(sketch, "E5618", {"start": v(-27.64, -6.95) * mm, "end": v(-28.23, -6.88) * mm});
            skLineSegment(sketch, "E5619", {"start": v(-28.23, -6.88) * mm, "end": v(-28.82, -6.81) * mm});
            skLineSegment(sketch, "E5620", {"start": v(-28.82, -6.81) * mm, "end": v(-29.41, -6.73) * mm});
            skLineSegment(sketch, "E5621", {"start": v(-29.41, -6.73) * mm, "end": v(-30, -6.64) * mm});
            skLineSegment(sketch, "E5622", {"start": v(-30, -6.64) * mm, "end": v(-30.59, -6.53) * mm});
            skLineSegment(sketch, "E5623", {"start": v(-30.59, -6.53) * mm, "end": v(-31.18, -6.42) * mm});
            skLineSegment(sketch, "E5624", {"start": v(-31.18, -6.42) * mm, "end": v(-31.77, -6.3) * mm});
            skLineSegment(sketch, "E5625", {"start": v(-31.77, -6.3) * mm, "end": v(-32.35, -6.17) * mm});
            skLineSegment(sketch, "E5626", {"start": v(-32.35, -6.17) * mm, "end": v(-32.94, -6.03) * mm});
            skLineSegment(sketch, "E5627", {"start": v(-32.94, -6.03) * mm, "end": v(-33.53, -5.88) * mm});
            skLineSegment(sketch, "E5628", {"start": v(-33.53, -5.88) * mm, "end": v(-34.11, -5.72) * mm});
            skLineSegment(sketch, "E5629", {"start": v(-34.11, -5.72) * mm, "end": v(-34.7, -5.55) * mm});
            skLineSegment(sketch, "E5630", {"start": v(-34.7, -5.55) * mm, "end": v(-35.28, -5.37) * mm});
            skLineSegment(sketch, "E5631", {"start": v(-35.28, -5.37) * mm, "end": v(-35.87, -5.18) * mm});
            skLineSegment(sketch, "E5632", {"start": v(-35.87, -5.18) * mm, "end": v(-36.45, -4.99) * mm});
            skLineSegment(sketch, "E5633", {"start": v(-36.45, -4.99) * mm, "end": v(-37.03, -4.78) * mm});
            skLineSegment(sketch, "E5634", {"start": v(-37.03, -4.78) * mm, "end": v(-37.61, -4.56) * mm});
            skLineSegment(sketch, "E5635", {"start": v(-37.61, -4.56) * mm, "end": v(-38.2, -4.34) * mm});
            skLineSegment(sketch, "E5636", {"start": v(-38.2, -4.34) * mm, "end": v(-38.78, -4.1) * mm});
            skLineSegment(sketch, "E5637", {"start": v(-38.78, -4.1) * mm, "end": v(-39.36, -3.86) * mm});
            skLineSegment(sketch, "E5638", {"start": v(-39.36, -3.86) * mm, "end": v(-39.94, -3.6) * mm});
            skLineSegment(sketch, "E5639", {"start": v(-39.94, -3.6) * mm, "end": v(-40.52, -3.34) * mm});
            skLineSegment(sketch, "E5640", {"start": v(-40.52, -3.34) * mm, "end": v(-41.1, -3.07) * mm});
            skLineSegment(sketch, "E5641", {"start": v(-41.1, -3.07) * mm, "end": v(-41.67, -2.79) * mm});
            skLineSegment(sketch, "E5642", {"start": v(-41.67, -2.79) * mm, "end": v(-42.02, -2.6) * mm});
            skLineSegment(sketch, "E5643", {"start": v(-42.02, -2.6) * mm, "end": v(-41.78, -5.18) * mm});
            skLineSegment(sketch, "E5644", {"start": v(-41.78, -5.18) * mm, "end": v(-41.37, -7.75) * mm});
            skLineSegment(sketch, "E5645", {"start": v(-41.37, -7.75) * mm, "end": v(-40.8, -10.29) * mm});
            skLineSegment(sketch, "E5646", {"start": v(-40.8, -10.29) * mm, "end": v(-40.08, -12.78) * mm});
            skLineSegment(sketch, "E5647", {"start": v(-40.08, -12.78) * mm, "end": v(-39.2, -15.23) * mm});
            skLineSegment(sketch, "E5648", {"start": v(-39.2, -15.23) * mm, "end": v(-38.17, -17.61) * mm});
            skLineSegment(sketch, "E5649", {"start": v(-38.17, -17.61) * mm, "end": v(-37, -19.93) * mm});
            skLineSegment(sketch, "E5650", {"start": v(-37, -19.93) * mm, "end": v(-35.67, -22.16) * mm});
            skLineSegment(sketch, "E5651", {"start": v(-35.67, -22.16) * mm, "end": v(-34.2, -24.31) * mm});
            skLineSegment(sketch, "E5652", {"start": v(-34.2, -24.31) * mm, "end": v(-32.62, -26.37) * mm});
            skLineSegment(sketch, "E5653", {"start": v(-32.62, -26.37) * mm, "end": v(-30.9, -28.31) * mm});
            skLineSegment(sketch, "E5654", {"start": v(-30.9, -28.31) * mm, "end": v(-29.06, -30.15) * mm});
            skLineSegment(sketch, "E5655", {"start": v(-29.06, -30.15) * mm, "end": v(-27.11, -31.87) * mm});
            skLineSegment(sketch, "E5656", {"start": v(-27.11, -31.87) * mm, "end": v(-25.06, -33.46) * mm});
            skLineSegment(sketch, "E5657", {"start": v(-25.06, -33.46) * mm, "end": v(-22.9, -34.92) * mm});
            skLineSegment(sketch, "E5658", {"start": v(-22.9, -34.92) * mm, "end": v(-20.67, -36.25) * mm});
            skLineSegment(sketch, "E5659", {"start": v(-20.67, -36.25) * mm, "end": v(-18.36, -37.43) * mm});
            skLineSegment(sketch, "E5660", {"start": v(-18.36, -37.43) * mm, "end": v(-15.97, -38.46) * mm});
            skLineSegment(sketch, "E5661", {"start": v(-15.97, -38.46) * mm, "end": v(-13.53, -39.34) * mm});
            skLineSegment(sketch, "E5662", {"start": v(-13.53, -39.34) * mm, "end": v(-11.03, -40.06) * mm});
            skLineSegment(sketch, "E5663", {"start": v(-11.03, -40.06) * mm, "end": v(-8.5, -40.63) * mm});
            skLineSegment(sketch, "E5664", {"start": v(-8.5, -40.63) * mm, "end": v(-5.93, -41.04) * mm});
            skLineSegment(sketch, "E5665", {"start": v(-5.93, -41.04) * mm, "end": v(-3.7, -41.25) * mm});
            skLineSegment(sketch, "E5666", {"start": v(-3.7, -41.25) * mm, "end": v(-3.84, -40.93) * mm});
            skLineSegment(sketch, "E5667", {"start": v(4.44, -41.04) * mm, "end": v(7, -40.63) * mm});
            skLineSegment(sketch, "E5668", {"start": v(7, -40.63) * mm, "end": v(9.54, -40.06) * mm});
            skLineSegment(sketch, "E5669", {"start": v(9.54, -40.06) * mm, "end": v(12.03, -39.34) * mm});
            skLineSegment(sketch, "E5670", {"start": v(12.03, -39.34) * mm, "end": v(14.48, -38.46) * mm});
            skLineSegment(sketch, "E5671", {"start": v(14.48, -38.46) * mm, "end": v(16.86, -37.43) * mm});
            skLineSegment(sketch, "E5672", {"start": v(16.86, -37.43) * mm, "end": v(19.18, -36.25) * mm});
            skLineSegment(sketch, "E5673", {"start": v(19.18, -36.25) * mm, "end": v(21.42, -34.92) * mm});
            skLineSegment(sketch, "E5674", {"start": v(21.42, -34.92) * mm, "end": v(23.57, -33.46) * mm});
            skLineSegment(sketch, "E5675", {"start": v(23.57, -33.46) * mm, "end": v(25.62, -31.87) * mm});
            skLineSegment(sketch, "E5676", {"start": v(25.62, -31.87) * mm, "end": v(27.57, -30.15) * mm});
            skLineSegment(sketch, "E5677", {"start": v(27.57, -30.15) * mm, "end": v(29.4, -28.31) * mm});
            skLineSegment(sketch, "E5678", {"start": v(29.4, -28.31) * mm, "end": v(31.12, -26.37) * mm});
            skLineSegment(sketch, "E5679", {"start": v(31.12, -26.37) * mm, "end": v(32.72, -24.31) * mm});
            skLineSegment(sketch, "E5680", {"start": v(32.72, -24.31) * mm, "end": v(34.18, -22.16) * mm});
            skLineSegment(sketch, "E5681", {"start": v(34.18, -22.16) * mm, "end": v(35.5, -19.93) * mm});
            skLineSegment(sketch, "E5682", {"start": v(35.5, -19.93) * mm, "end": v(36.68, -17.61) * mm});
            skLineSegment(sketch, "E5683", {"start": v(36.68, -17.61) * mm, "end": v(37.71, -15.23) * mm});
            skLineSegment(sketch, "E5684", {"start": v(37.71, -15.23) * mm, "end": v(38.6, -12.78) * mm});
            skLineSegment(sketch, "E5685", {"start": v(38.6, -12.78) * mm, "end": v(39.32, -10.29) * mm});
            skLineSegment(sketch, "E5686", {"start": v(39.32, -10.29) * mm, "end": v(39.88, -7.75) * mm});
            skLineSegment(sketch, "E5687", {"start": v(39.88, -7.75) * mm, "end": v(40.29, -5.18) * mm});
            skLineSegment(sketch, "E5688", {"start": v(40.29, -5.18) * mm, "end": v(40.5, -2.96) * mm});
            skLineSegment(sketch, "E5689", {"start": v(40.5, -2.96) * mm, "end": v(40.18, -3.1) * mm});
            skLineSegment(sketch, "E5690", {"start": v(40.18, -3.1) * mm, "end": v(39.6, -3.34) * mm});
            skLineSegment(sketch, "E5691", {"start": v(39.6, -3.34) * mm, "end": v(39.02, -3.57) * mm});
            skLineSegment(sketch, "E5692", {"start": v(39.02, -3.57) * mm, "end": v(38.44, -3.8) * mm});
            skLineSegment(sketch, "E5693", {"start": v(38.44, -3.8) * mm, "end": v(37.86, -4.02) * mm});
            skLineSegment(sketch, "E5694", {"start": v(37.86, -4.02) * mm, "end": v(37.28, -4.23) * mm});
            skLineSegment(sketch, "E5695", {"start": v(37.28, -4.23) * mm, "end": v(36.7, -4.43) * mm});
            skLineSegment(sketch, "E5696", {"start": v(36.7, -4.43) * mm, "end": v(36.12, -4.62) * mm});
            skLineSegment(sketch, "E5697", {"start": v(36.12, -4.62) * mm, "end": v(35.54, -4.8) * mm});
            skLineSegment(sketch, "E5698", {"start": v(35.54, -4.8) * mm, "end": v(34.96, -4.99) * mm});
            skLineSegment(sketch, "E5699", {"start": v(34.96, -4.99) * mm, "end": v(34.37, -5.15) * mm});
            skLineSegment(sketch, "E5700", {"start": v(34.37, -5.15) * mm, "end": v(33.79, -5.32) * mm});
            skLineSegment(sketch, "E5701", {"start": v(33.79, -5.32) * mm, "end": v(33.2, -5.47) * mm});
            skLineSegment(sketch, "E5702", {"start": v(33.2, -5.47) * mm, "end": v(32.62, -5.61) * mm});
            skLineSegment(sketch, "E5703", {"start": v(32.62, -5.61) * mm, "end": v(32.03, -5.75) * mm});
            skLineSegment(sketch, "E5704", {"start": v(32.03, -5.75) * mm, "end": v(31.45, -5.88) * mm});
            skLineSegment(sketch, "E5705", {"start": v(31.45, -5.88) * mm, "end": v(30.86, -6) * mm});
            skLineSegment(sketch, "E5706", {"start": v(30.86, -6) * mm, "end": v(30.27, -6.11) * mm});
            skLineSegment(sketch, "E5707", {"start": v(30.27, -6.11) * mm, "end": v(29.69, -6.22) * mm});
            skLineSegment(sketch, "E5708", {"start": v(29.69, -6.22) * mm, "end": v(29.1, -6.31) * mm});
            skLineSegment(sketch, "E5709", {"start": v(29.1, -6.31) * mm, "end": v(28.5, -6.4) * mm});
            skLineSegment(sketch, "E5710", {"start": v(28.5, -6.4) * mm, "end": v(27.92, -6.48) * mm});
            skLineSegment(sketch, "E5711", {"start": v(27.92, -6.48) * mm, "end": v(27.33, -6.55) * mm});
            skLineSegment(sketch, "E5712", {"start": v(27.33, -6.55) * mm, "end": v(26.74, -6.62) * mm});
            skLineSegment(sketch, "E5713", {"start": v(26.74, -6.62) * mm, "end": v(26.15, -6.67) * mm});
            skLineSegment(sketch, "E5714", {"start": v(26.15, -6.67) * mm, "end": v(25.56, -6.72) * mm});
            skLineSegment(sketch, "E5715", {"start": v(25.56, -6.72) * mm, "end": v(24.96, -6.75) * mm});
            skLineSegment(sketch, "E5716", {"start": v(24.96, -6.75) * mm, "end": v(24.37, -6.78) * mm});
            skLineSegment(sketch, "E5717", {"start": v(24.37, -6.78) * mm, "end": v(23.78, -6.8) * mm});
            skLineSegment(sketch, "E5718", {"start": v(23.78, -6.8) * mm, "end": v(23.18, -6.82) * mm});
            skLineSegment(sketch, "E5719", {"start": v(23.18, -6.82) * mm, "end": v(22.59, -6.82) * mm});
            skLineSegment(sketch, "E5720", {"start": v(22.59, -6.82) * mm, "end": v(22, -6.82) * mm});
            skLineSegment(sketch, "E5721", {"start": v(22, -6.82) * mm, "end": v(21.42, -6.8) * mm});
            skLineSegment(sketch, "E5722", {"start": v(21.42, -6.8) * mm, "end": v(20.83, -6.78) * mm});
            skLineSegment(sketch, "E5723", {"start": v(20.83, -6.78) * mm, "end": v(20.25, -6.76) * mm});
            skLineSegment(sketch, "E5724", {"start": v(20.25, -6.76) * mm, "end": v(19.67, -6.72) * mm});
            skLineSegment(sketch, "E5725", {"start": v(19.67, -6.72) * mm, "end": v(19.08, -6.67) * mm});
            skLineSegment(sketch, "E5726", {"start": v(19.08, -6.67) * mm, "end": v(18.5, -6.62) * mm});
            skLineSegment(sketch, "E5727", {"start": v(18.5, -6.62) * mm, "end": v(17.92, -6.56) * mm});
            skLineSegment(sketch, "E5728", {"start": v(17.92, -6.56) * mm, "end": v(17.34, -6.5) * mm});
            skLineSegment(sketch, "E5729", {"start": v(17.34, -6.5) * mm, "end": v(16.75, -6.41) * mm});
            skLineSegment(sketch, "E5730", {"start": v(16.75, -6.41) * mm, "end": v(16.17, -6.33) * mm});
            skLineSegment(sketch, "E5731", {"start": v(16.17, -6.33) * mm, "end": v(15.6, -6.23) * mm});
            skLineSegment(sketch, "E5732", {"start": v(15.6, -6.23) * mm, "end": v(15.01, -6.13) * mm});
            skLineSegment(sketch, "E5733", {"start": v(15.01, -6.13) * mm, "end": v(14.43, -6.02) * mm});
            skLineSegment(sketch, "E5734", {"start": v(14.43, -6.02) * mm, "end": v(13.86, -5.9) * mm});
            skLineSegment(sketch, "E5735", {"start": v(13.86, -5.9) * mm, "end": v(13.28, -5.78) * mm});
            skLineSegment(sketch, "E5736", {"start": v(13.28, -5.78) * mm, "end": v(12.7, -5.65) * mm});
            skLineSegment(sketch, "E5737", {"start": v(12.7, -5.65) * mm, "end": v(12.12, -5.5) * mm});
            skLineSegment(sketch, "E5738", {"start": v(12.12, -5.5) * mm, "end": v(11.55, -5.36) * mm});
            skLineSegment(sketch, "E5739", {"start": v(11.55, -5.36) * mm, "end": v(10.97, -5.2) * mm});
            skLineSegment(sketch, "E5740", {"start": v(10.97, -5.2) * mm, "end": v(10.4, -5.04) * mm});
            skLineSegment(sketch, "E5741", {"start": v(10.4, -5.04) * mm, "end": v(9.82, -4.86) * mm});
            skLineSegment(sketch, "E5742", {"start": v(9.82, -4.86) * mm, "end": v(9.25, -4.68) * mm});
            skLineSegment(sketch, "E5743", {"start": v(9.25, -4.68) * mm, "end": v(8.67, -4.5) * mm});
            skLineSegment(sketch, "E5744", {"start": v(8.67, -4.5) * mm, "end": v(8.1, -4.3) * mm});
            skLineSegment(sketch, "E5745", {"start": v(8.1, -4.3) * mm, "end": v(7.53, -4.1) * mm});
            skLineSegment(sketch, "E5746", {"start": v(7.53, -4.1) * mm, "end": v(6.96, -3.88) * mm});
            skLineSegment(sketch, "E5747", {"start": v(6.96, -3.88) * mm, "end": v(6.38, -3.66) * mm});
            skLineSegment(sketch, "E5748", {"start": v(6.38, -3.66) * mm, "end": v(5.81, -3.43) * mm});
            skLineSegment(sketch, "E5749", {"start": v(5.81, -3.43) * mm, "end": v(5.24, -3.2) * mm});
            skLineSegment(sketch, "E5750", {"start": v(5.24, -3.2) * mm, "end": v(4.67, -2.95) * mm});
            skLineSegment(sketch, "E5751", {"start": v(4.67, -2.95) * mm, "end": v(4.33, -2.8) * mm});
            skLineSegment(sketch, "E5752", {"start": v(4.33, -2.8) * mm, "end": v(4.15, -3.1) * mm});
            skLineSegment(sketch, "E5753", {"start": v(4.15, -3.1) * mm, "end": v(3.94, -3.4) * mm});
            skLineSegment(sketch, "E5754", {"start": v(3.94, -3.4) * mm, "end": v(3.72, -3.7) * mm});
            skLineSegment(sketch, "E5755", {"start": v(3.72, -3.7) * mm, "end": v(3.48, -3.97) * mm});
            skLineSegment(sketch, "E5756", {"start": v(3.48, -3.97) * mm, "end": v(3.22, -4.23) * mm});
            skLineSegment(sketch, "E5757", {"start": v(3.22, -4.23) * mm, "end": v(2.95, -4.47) * mm});
            skLineSegment(sketch, "E5758", {"start": v(2.95, -4.47) * mm, "end": v(2.66, -4.69) * mm});
            skLineSegment(sketch, "E5759", {"start": v(2.66, -4.69) * mm, "end": v(2.36, -4.9) * mm});
            skLineSegment(sketch, "E5760", {"start": v(2.36, -4.9) * mm, "end": v(2.05, -5.08) * mm});
            skLineSegment(sketch, "E5761", {"start": v(2.05, -5.08) * mm, "end": v(1.77, -5.22) * mm});
            skLineSegment(sketch, "E5762", {"start": v(1.77, -5.22) * mm, "end": v(1.88, -5.42) * mm});
            skLineSegment(sketch, "E5763", {"start": v(1.88, -5.42) * mm, "end": v(2.16, -6) * mm});
            skLineSegment(sketch, "E5764", {"start": v(2.16, -6) * mm, "end": v(2.43, -6.56) * mm});
            skLineSegment(sketch, "E5765", {"start": v(2.43, -6.56) * mm, "end": v(2.7, -7.13) * mm});
            skLineSegment(sketch, "E5766", {"start": v(2.7, -7.13) * mm, "end": v(2.95, -7.7) * mm});
            skLineSegment(sketch, "E5767", {"start": v(2.95, -7.7) * mm, "end": v(3.2, -8.27) * mm});
            skLineSegment(sketch, "E5768", {"start": v(3.2, -8.27) * mm, "end": v(3.44, -8.85) * mm});
            skLineSegment(sketch, "E5769", {"start": v(3.44, -8.85) * mm, "end": v(3.67, -9.42) * mm});
            skLineSegment(sketch, "E5770", {"start": v(3.67, -9.42) * mm, "end": v(3.89, -10) * mm});
            skLineSegment(sketch, "E5771", {"start": v(3.89, -10) * mm, "end": v(4.1, -10.57) * mm});
            skLineSegment(sketch, "E5772", {"start": v(4.1, -10.57) * mm, "end": v(4.3, -11.14) * mm});
            skLineSegment(sketch, "E5773", {"start": v(4.3, -11.14) * mm, "end": v(4.5, -11.72) * mm});
            skLineSegment(sketch, "E5774", {"start": v(4.5, -11.72) * mm, "end": v(4.67, -12.3) * mm});
            skLineSegment(sketch, "E5775", {"start": v(4.67, -12.3) * mm, "end": v(4.85, -12.87) * mm});
            skLineSegment(sketch, "E5776", {"start": v(4.85, -12.87) * mm, "end": v(5.01, -13.45) * mm});
            skLineSegment(sketch, "E5777", {"start": v(5.01, -13.45) * mm, "end": v(5.17, -14.02) * mm});
            skLineSegment(sketch, "E5778", {"start": v(5.17, -14.02) * mm, "end": v(5.31, -14.6) * mm});
            skLineSegment(sketch, "E5779", {"start": v(5.31, -14.6) * mm, "end": v(5.45, -15.18) * mm});
            skLineSegment(sketch, "E5780", {"start": v(5.45, -15.18) * mm, "end": v(5.58, -15.76) * mm});
            skLineSegment(sketch, "E5781", {"start": v(5.58, -15.76) * mm, "end": v(5.7, -16.34) * mm});
            skLineSegment(sketch, "E5782", {"start": v(5.7, -16.34) * mm, "end": v(5.8, -16.92) * mm});
            skLineSegment(sketch, "E5783", {"start": v(5.8, -16.92) * mm, "end": v(5.9, -17.5) * mm});
            skLineSegment(sketch, "E5784", {"start": v(5.9, -17.5) * mm, "end": v(6, -18.08) * mm});
            skLineSegment(sketch, "E5785", {"start": v(6, -18.08) * mm, "end": v(6.07, -18.66) * mm});
            skLineSegment(sketch, "E5786", {"start": v(6.07, -18.66) * mm, "end": v(6.14, -19.25) * mm});
            skLineSegment(sketch, "E5787", {"start": v(6.14, -19.25) * mm, "end": v(6.2, -19.83) * mm});
            skLineSegment(sketch, "E5788", {"start": v(6.2, -19.83) * mm, "end": v(6.26, -20.41) * mm});
            skLineSegment(sketch, "E5789", {"start": v(6.26, -20.41) * mm, "end": v(6.3, -21) * mm});
            skLineSegment(sketch, "E5790", {"start": v(6.3, -21) * mm, "end": v(6.33, -21.58) * mm});
            skLineSegment(sketch, "E5791", {"start": v(6.33, -21.58) * mm, "end": v(6.36, -22.17) * mm});
            skLineSegment(sketch, "E5792", {"start": v(6.36, -22.17) * mm, "end": v(6.37, -22.75) * mm});
            skLineSegment(sketch, "E5793", {"start": v(6.37, -22.75) * mm, "end": v(6.38, -23.34) * mm});
            skLineSegment(sketch, "E5794", {"start": v(6.38, -23.34) * mm, "end": v(6.37, -23.93) * mm});
            skLineSegment(sketch, "E5795", {"start": v(6.37, -23.93) * mm, "end": v(6.36, -24.52) * mm});
            skLineSegment(sketch, "E5796", {"start": v(6.36, -24.52) * mm, "end": v(6.33, -25.12) * mm});
            skLineSegment(sketch, "E5797", {"start": v(6.33, -25.12) * mm, "end": v(6.3, -25.71) * mm});
            skLineSegment(sketch, "E5798", {"start": v(6.3, -25.71) * mm, "end": v(6.25, -26.3) * mm});
            skLineSegment(sketch, "E5799", {"start": v(6.25, -26.3) * mm, "end": v(6.2, -26.9) * mm});
            skLineSegment(sketch, "E5800", {"start": v(6.2, -26.9) * mm, "end": v(6.14, -27.49) * mm});
            skLineSegment(sketch, "E5801", {"start": v(6.14, -27.49) * mm, "end": v(6.06, -28.08) * mm});
            skLineSegment(sketch, "E5802", {"start": v(6.06, -28.08) * mm, "end": v(5.98, -28.67) * mm});
            skLineSegment(sketch, "E5803", {"start": v(5.98, -28.67) * mm, "end": v(5.89, -29.26) * mm});
            skLineSegment(sketch, "E5804", {"start": v(5.89, -29.26) * mm, "end": v(5.79, -29.84) * mm});
            skLineSegment(sketch, "E5805", {"start": v(5.79, -29.84) * mm, "end": v(5.67, -30.43) * mm});
            skLineSegment(sketch, "E5806", {"start": v(5.67, -30.43) * mm, "end": v(5.55, -31.02) * mm});
            skLineSegment(sketch, "E5807", {"start": v(5.55, -31.02) * mm, "end": v(5.42, -31.6) * mm});
            skLineSegment(sketch, "E5808", {"start": v(5.42, -31.6) * mm, "end": v(5.28, -32.2) * mm});
            skLineSegment(sketch, "E5809", {"start": v(5.28, -32.2) * mm, "end": v(5.13, -32.78) * mm});
            skLineSegment(sketch, "E5810", {"start": v(5.13, -32.78) * mm, "end": v(4.97, -33.37) * mm});
            skLineSegment(sketch, "E5811", {"start": v(4.97, -33.37) * mm, "end": v(4.8, -33.95) * mm});
            skLineSegment(sketch, "E5812", {"start": v(4.8, -33.95) * mm, "end": v(4.63, -34.54) * mm});
            skLineSegment(sketch, "E5813", {"start": v(4.63, -34.54) * mm, "end": v(4.44, -35.12) * mm});
            skLineSegment(sketch, "E5814", {"start": v(4.44, -35.12) * mm, "end": v(4.24, -35.7) * mm});
            skLineSegment(sketch, "E5815", {"start": v(4.24, -35.7) * mm, "end": v(4.03, -36.29) * mm});
            skLineSegment(sketch, "E5816", {"start": v(4.03, -36.29) * mm, "end": v(3.82, -36.87) * mm});
            skLineSegment(sketch, "E5817", {"start": v(3.82, -36.87) * mm, "end": v(3.6, -37.45) * mm});
            skLineSegment(sketch, "E5818", {"start": v(3.6, -37.45) * mm, "end": v(3.36, -38.03) * mm});
            skLineSegment(sketch, "E5819", {"start": v(3.36, -38.03) * mm, "end": v(3.11, -38.61) * mm});
            skLineSegment(sketch, "E5820", {"start": v(3.11, -38.61) * mm, "end": v(2.86, -39.2) * mm});
            skLineSegment(sketch, "E5821", {"start": v(2.86, -39.2) * mm, "end": v(2.6, -39.77) * mm});
            skLineSegment(sketch, "E5822", {"start": v(2.6, -39.77) * mm, "end": v(2.32, -40.35) * mm});
            skLineSegment(sketch, "E5823", {"start": v(2.32, -40.35) * mm, "end": v(2.04, -40.93) * mm});
            skLineSegment(sketch, "E5824", {"start": v(2.04, -40.93) * mm, "end": v(1.86, -41.28) * mm});
            skLineSegment(sketch, "E5825", {"start": v(1.86, -41.28) * mm, "end": v(4.44, -41.04) * mm});
            skLineSegment(sketch, "E5826", {"start": v(-0.06, -32.75) * mm, "end": v(0.1, -32.44) * mm});
            skLineSegment(sketch, "E5827", {"start": v(0.1, -32.44) * mm, "end": v(0.25, -32.13) * mm});
            skLineSegment(sketch, "E5828", {"start": v(0.25, -32.13) * mm, "end": v(0.4, -31.82) * mm});
            skLineSegment(sketch, "E5829", {"start": v(0.4, -31.82) * mm, "end": v(0.55, -31.51) * mm});
            skLineSegment(sketch, "E5830", {"start": v(0.55, -31.51) * mm, "end": v(0.69, -31.2) * mm});
            skLineSegment(sketch, "E5831", {"start": v(0.69, -31.2) * mm, "end": v(0.82, -30.9) * mm});
            skLineSegment(sketch, "E5832", {"start": v(0.82, -30.9) * mm, "end": v(0.95, -30.59) * mm});
            skLineSegment(sketch, "E5833", {"start": v(0.95, -30.59) * mm, "end": v(1.08, -30.28) * mm});
            skLineSegment(sketch, "E5834", {"start": v(1.08, -30.28) * mm, "end": v(1.2, -29.97) * mm});
            skLineSegment(sketch, "E5835", {"start": v(1.2, -29.97) * mm, "end": v(1.3, -29.66) * mm});
            skLineSegment(sketch, "E5836", {"start": v(1.3, -29.66) * mm, "end": v(1.41, -29.35) * mm});
            skLineSegment(sketch, "E5837", {"start": v(1.41, -29.35) * mm, "end": v(1.52, -29.04) * mm});
            skLineSegment(sketch, "E5838", {"start": v(1.52, -29.04) * mm, "end": v(1.61, -28.73) * mm});
            skLineSegment(sketch, "E5839", {"start": v(1.61, -28.73) * mm, "end": v(1.7, -28.42) * mm});
            skLineSegment(sketch, "E5840", {"start": v(1.7, -28.42) * mm, "end": v(1.79, -28.11) * mm});
            skLineSegment(sketch, "E5841", {"start": v(1.79, -28.11) * mm, "end": v(1.87, -27.8) * mm});
            skLineSegment(sketch, "E5842", {"start": v(1.87, -27.8) * mm, "end": v(1.94, -27.5) * mm});
            skLineSegment(sketch, "E5843", {"start": v(1.94, -27.5) * mm, "end": v(2.01, -27.18) * mm});
            skLineSegment(sketch, "E5844", {"start": v(2.01, -27.18) * mm, "end": v(2.08, -26.87) * mm});
            skLineSegment(sketch, "E5845", {"start": v(2.08, -26.87) * mm, "end": v(2.13, -26.56) * mm});
            skLineSegment(sketch, "E5846", {"start": v(2.13, -26.56) * mm, "end": v(2.19, -26.25) * mm});
            skLineSegment(sketch, "E5847", {"start": v(2.19, -26.25) * mm, "end": v(2.23, -25.94) * mm});
            skLineSegment(sketch, "E5848", {"start": v(2.23, -25.94) * mm, "end": v(2.27, -25.63) * mm});
            skLineSegment(sketch, "E5849", {"start": v(2.27, -25.63) * mm, "end": v(2.3, -25.31) * mm});
            skLineSegment(sketch, "E5850", {"start": v(2.3, -25.31) * mm, "end": v(2.34, -25) * mm});
            skLineSegment(sketch, "E5851", {"start": v(2.34, -25) * mm, "end": v(2.37, -24.7) * mm});
            skLineSegment(sketch, "E5852", {"start": v(2.37, -24.7) * mm, "end": v(2.38, -24.38) * mm});
            skLineSegment(sketch, "E5853", {"start": v(2.38, -24.38) * mm, "end": v(2.4, -24.07) * mm});
            skLineSegment(sketch, "E5854", {"start": v(2.4, -24.07) * mm, "end": v(2.4, -23.75) * mm});
            skLineSegment(sketch, "E5855", {"start": v(2.4, -23.75) * mm, "end": v(2.4, -23.44) * mm});
            skLineSegment(sketch, "E5856", {"start": v(2.4, -23.44) * mm, "end": v(2.4, -23.13) * mm});
            skLineSegment(sketch, "E5857", {"start": v(2.4, -23.13) * mm, "end": v(2.4, -22.82) * mm});
            skLineSegment(sketch, "E5858", {"start": v(2.4, -22.82) * mm, "end": v(2.39, -22.52) * mm});
            skLineSegment(sketch, "E5859", {"start": v(2.39, -22.52) * mm, "end": v(2.37, -22.2) * mm});
            skLineSegment(sketch, "E5860", {"start": v(2.37, -22.2) * mm, "end": v(2.34, -21.9) * mm});
            skLineSegment(sketch, "E5861", {"start": v(2.34, -21.9) * mm, "end": v(2.31, -21.6) * mm});
            skLineSegment(sketch, "E5862", {"start": v(2.31, -21.6) * mm, "end": v(2.28, -21.29) * mm});
            skLineSegment(sketch, "E5863", {"start": v(2.28, -21.29) * mm, "end": v(2.24, -20.98) * mm});
            skLineSegment(sketch, "E5864", {"start": v(2.24, -20.98) * mm, "end": v(2.2, -20.67) * mm});
            skLineSegment(sketch, "E5865", {"start": v(2.2, -20.67) * mm, "end": v(2.14, -20.37) * mm});
            skLineSegment(sketch, "E5866", {"start": v(2.14, -20.37) * mm, "end": v(2.08, -20.06) * mm});
            skLineSegment(sketch, "E5867", {"start": v(2.08, -20.06) * mm, "end": v(2.02, -19.76) * mm});
            skLineSegment(sketch, "E5868", {"start": v(2.02, -19.76) * mm, "end": v(1.96, -19.45) * mm});
            skLineSegment(sketch, "E5869", {"start": v(1.96, -19.45) * mm, "end": v(1.88, -19.14) * mm});
            skLineSegment(sketch, "E5870", {"start": v(1.88, -19.14) * mm, "end": v(1.8, -18.84) * mm});
            skLineSegment(sketch, "E5871", {"start": v(1.8, -18.84) * mm, "end": v(1.72, -18.53) * mm});
            skLineSegment(sketch, "E5872", {"start": v(1.72, -18.53) * mm, "end": v(1.63, -18.23) * mm});
            skLineSegment(sketch, "E5873", {"start": v(1.63, -18.23) * mm, "end": v(1.54, -17.92) * mm});
            skLineSegment(sketch, "E5874", {"start": v(1.54, -17.92) * mm, "end": v(1.44, -17.62) * mm});
            skLineSegment(sketch, "E5875", {"start": v(1.44, -17.62) * mm, "end": v(1.34, -17.31) * mm});
            skLineSegment(sketch, "E5876", {"start": v(1.34, -17.31) * mm, "end": v(1.23, -17) * mm});
            skLineSegment(sketch, "E5877", {"start": v(1.23, -17) * mm, "end": v(1.11, -16.7) * mm});
            skLineSegment(sketch, "E5878", {"start": v(1.11, -16.7) * mm, "end": v(1, -16.4) * mm});
            skLineSegment(sketch, "E5879", {"start": v(1, -16.4) * mm, "end": v(0.87, -16.1) * mm});
            skLineSegment(sketch, "E5880", {"start": v(0.87, -16.1) * mm, "end": v(0.74, -15.79) * mm});
            skLineSegment(sketch, "E5881", {"start": v(0.74, -15.79) * mm, "end": v(0.6, -15.48) * mm});
            skLineSegment(sketch, "E5882", {"start": v(0.6, -15.48) * mm, "end": v(0.46, -15.18) * mm});
            skLineSegment(sketch, "E5883", {"start": v(0.46, -15.18) * mm, "end": v(0.31, -14.88) * mm});
            skLineSegment(sketch, "E5884", {"start": v(0.31, -14.88) * mm, "end": v(0.16, -14.57) * mm});
            skLineSegment(sketch, "E5885", {"start": v(0.16, -14.57) * mm, "end": v(0, -14.27) * mm});
            skLineSegment(sketch, "E5886", {"start": v(0, -14.27) * mm, "end": v(-0.04, -14.2) * mm});
            skLineSegment(sketch, "E5887", {"start": v(-0.04, -14.2) * mm, "end": v(-1.68, -14.2) * mm});
            skLineSegment(sketch, "E5888", {"start": v(-1.68, -14.2) * mm, "end": v(-1.7, -14.22) * mm});
            skLineSegment(sketch, "E5889", {"start": v(-1.7, -14.22) * mm, "end": v(-1.83, -14.52) * mm});
            skLineSegment(sketch, "E5890", {"start": v(-1.83, -14.52) * mm, "end": v(-1.96, -14.83) * mm});
            skLineSegment(sketch, "E5891", {"start": v(-1.96, -14.83) * mm, "end": v(-2.09, -15.13) * mm});
            skLineSegment(sketch, "E5892", {"start": v(-2.09, -15.13) * mm, "end": v(-2.2, -15.44) * mm});
            skLineSegment(sketch, "E5893", {"start": v(-2.2, -15.44) * mm, "end": v(-2.33, -15.74) * mm});
            skLineSegment(sketch, "E5894", {"start": v(-2.33, -15.74) * mm, "end": v(-2.44, -16.05) * mm});
            skLineSegment(sketch, "E5895", {"start": v(-2.44, -16.05) * mm, "end": v(-2.55, -16.35) * mm});
            skLineSegment(sketch, "E5896", {"start": v(-2.55, -16.35) * mm, "end": v(-2.65, -16.66) * mm});
            skLineSegment(sketch, "E5897", {"start": v(-2.65, -16.66) * mm, "end": v(-2.75, -16.97) * mm});
            skLineSegment(sketch, "E5898", {"start": v(-2.75, -16.97) * mm, "end": v(-2.84, -17.27) * mm});
            skLineSegment(sketch, "E5899", {"start": v(-2.84, -17.27) * mm, "end": v(-2.93, -17.58) * mm});
            skLineSegment(sketch, "E5900", {"start": v(-2.93, -17.58) * mm, "end": v(-3.02, -17.89) * mm});
            skLineSegment(sketch, "E5901", {"start": v(-3.02, -17.89) * mm, "end": v(-3.1, -18.2) * mm});
            skLineSegment(sketch, "E5902", {"start": v(-3.1, -18.2) * mm, "end": v(-3.18, -18.5) * mm});
            skLineSegment(sketch, "E5903", {"start": v(-3.18, -18.5) * mm, "end": v(-3.25, -18.8) * mm});
            skLineSegment(sketch, "E5904", {"start": v(-3.25, -18.8) * mm, "end": v(-3.31, -19.11) * mm});
            skLineSegment(sketch, "E5905", {"start": v(-3.31, -19.11) * mm, "end": v(-3.38, -19.42) * mm});
            skLineSegment(sketch, "E5906", {"start": v(-3.38, -19.42) * mm, "end": v(-3.44, -19.73) * mm});
            skLineSegment(sketch, "E5907", {"start": v(-3.44, -19.73) * mm, "end": v(-3.49, -20.04) * mm});
            skLineSegment(sketch, "E5908", {"start": v(-3.49, -20.04) * mm, "end": v(-3.54, -20.35) * mm});
            skLineSegment(sketch, "E5909", {"start": v(-3.54, -20.35) * mm, "end": v(-3.58, -20.65) * mm});
            skLineSegment(sketch, "E5910", {"start": v(-3.58, -20.65) * mm, "end": v(-3.62, -20.96) * mm});
            skLineSegment(sketch, "E5911", {"start": v(-3.62, -20.96) * mm, "end": v(-3.66, -21.27) * mm});
            skLineSegment(sketch, "E5912", {"start": v(-3.66, -21.27) * mm, "end": v(-3.69, -21.58) * mm});
            skLineSegment(sketch, "E5913", {"start": v(-3.69, -21.58) * mm, "end": v(-3.71, -21.9) * mm});
            skLineSegment(sketch, "E5914", {"start": v(-3.71, -21.9) * mm, "end": v(-3.73, -22.2) * mm});
            skLineSegment(sketch, "E5915", {"start": v(-3.73, -22.2) * mm, "end": v(-3.75, -22.51) * mm});
            skLineSegment(sketch, "E5916", {"start": v(-3.75, -22.51) * mm, "end": v(-3.76, -22.82) * mm});
            skLineSegment(sketch, "E5917", {"start": v(-3.76, -22.82) * mm, "end": v(-3.77, -23.13) * mm});
            skLineSegment(sketch, "E5918", {"start": v(-3.77, -23.13) * mm, "end": v(-3.77, -23.44) * mm});
            skLineSegment(sketch, "E5919", {"start": v(-3.77, -23.44) * mm, "end": v(-3.77, -23.76) * mm});
            skLineSegment(sketch, "E5920", {"start": v(-3.77, -23.76) * mm, "end": v(-3.76, -24.07) * mm});
            skLineSegment(sketch, "E5921", {"start": v(-3.76, -24.07) * mm, "end": v(-3.75, -24.39) * mm});
            skLineSegment(sketch, "E5922", {"start": v(-3.75, -24.39) * mm, "end": v(-3.73, -24.7) * mm});
            skLineSegment(sketch, "E5923", {"start": v(-3.73, -24.7) * mm, "end": v(-3.7, -25.01) * mm});
            skLineSegment(sketch, "E5924", {"start": v(-3.7, -25.01) * mm, "end": v(-3.68, -25.33) * mm});
            skLineSegment(sketch, "E5925", {"start": v(-3.68, -25.33) * mm, "end": v(-3.65, -25.64) * mm});
            skLineSegment(sketch, "E5926", {"start": v(-3.65, -25.64) * mm, "end": v(-3.62, -25.96) * mm});
            skLineSegment(sketch, "E5927", {"start": v(-3.62, -25.96) * mm, "end": v(-3.58, -26.27) * mm});
            skLineSegment(sketch, "E5928", {"start": v(-3.58, -26.27) * mm, "end": v(-3.53, -26.58) * mm});
            skLineSegment(sketch, "E5929", {"start": v(-3.53, -26.58) * mm, "end": v(-3.48, -26.9) * mm});
            skLineSegment(sketch, "E5930", {"start": v(-3.48, -26.9) * mm, "end": v(-3.43, -27.2) * mm});
            skLineSegment(sketch, "E5931", {"start": v(-3.43, -27.2) * mm, "end": v(-3.37, -27.52) * mm});
            skLineSegment(sketch, "E5932", {"start": v(-3.37, -27.52) * mm, "end": v(-3.3, -27.83) * mm});
            skLineSegment(sketch, "E5933", {"start": v(-3.3, -27.83) * mm, "end": v(-3.23, -28.14) * mm});
            skLineSegment(sketch, "E5934", {"start": v(-3.23, -28.14) * mm, "end": v(-3.16, -28.45) * mm});
            skLineSegment(sketch, "E5935", {"start": v(-3.16, -28.45) * mm, "end": v(-3.08, -28.77) * mm});
            skLineSegment(sketch, "E5936", {"start": v(-3.08, -28.77) * mm, "end": v(-3, -29.08) * mm});
            skLineSegment(sketch, "E5937", {"start": v(-3, -29.08) * mm, "end": v(-2.9, -29.39) * mm});
            skLineSegment(sketch, "E5938", {"start": v(-2.9, -29.39) * mm, "end": v(-2.82, -29.7) * mm});
            skLineSegment(sketch, "E5939", {"start": v(-2.82, -29.7) * mm, "end": v(-2.72, -30) * mm});
            skLineSegment(sketch, "E5940", {"start": v(-2.72, -30) * mm, "end": v(-2.62, -30.32) * mm});
            skLineSegment(sketch, "E5941", {"start": v(-2.62, -30.32) * mm, "end": v(-2.51, -30.63) * mm});
            skLineSegment(sketch, "E5942", {"start": v(-2.51, -30.63) * mm, "end": v(-2.4, -30.94) * mm});
            skLineSegment(sketch, "E5943", {"start": v(-2.4, -30.94) * mm, "end": v(-2.28, -31.25) * mm});
            skLineSegment(sketch, "E5944", {"start": v(-2.28, -31.25) * mm, "end": v(-2.16, -31.56) * mm});
            skLineSegment(sketch, "E5945", {"start": v(-2.16, -31.56) * mm, "end": v(-2.04, -31.87) * mm});
            skLineSegment(sketch, "E5946", {"start": v(-2.04, -31.87) * mm, "end": v(-1.9, -32.18) * mm});
            skLineSegment(sketch, "E5947", {"start": v(-1.9, -32.18) * mm, "end": v(-1.77, -32.49) * mm});
            skLineSegment(sketch, "E5948", {"start": v(-1.77, -32.49) * mm, "end": v(-1.63, -32.8) * mm});
            skLineSegment(sketch, "E5949", {"start": v(-1.63, -32.8) * mm, "end": v(-1.62, -32.83) * mm});
            skLineSegment(sketch, "E5950", {"start": v(-1.62, -32.83) * mm, "end": v(-0.11, -32.83) * mm});
            skLineSegment(sketch, "E5951", {"start": v(-0.11, -32.83) * mm, "end": v(-0.06, -32.75) * mm});
            skPoint(sketch, "E5952", {"position": v(-0.75, 0) * mm});
            skCircle(sketch, "E5953", {"center": v(-0.75, 0) * mm, "radius": 1.5 * mm});
            skLineSegment(sketch, "E5954", {"start": v(-0.75, 1.5) * mm, "end": v(-0.75, -1) * mm, "construction": true});
            skLineSegment(sketch, "E5955", {"start": v(-1.86, -1) * mm, "end": v(0.37, -1) * mm});
            skSolve(sketch);
        }
        {
            var Q0;
            Q0=makeQuery(id+"F0.imprint","IMPRINT",FACE,{"disambiguationData":[TD([[makeQuery(id+"F0.imprint","IMPRINT",EDGE,{"derivedFrom":sQuery(id+"F0.wireOp",EDGE,"E0")}),1.0]])]});
            var Q1;
            {var subQ0=sQuery(id+"F0.wireOp",EDGE,"E5955");Q1=makeQuery(id+"F0.imprint","IMPRINT",FACE,{"disambiguationData":[TD([[makeQuery(id+"F0.imprint","IMPRINT",EDGE,{"derivedFrom":subQ0}),-1.0]])]});}
            extrude(context, id + "F1", {"entities" : qUnion([Q0, Q1]), "depth" : 5 * mm});
        }
    });
